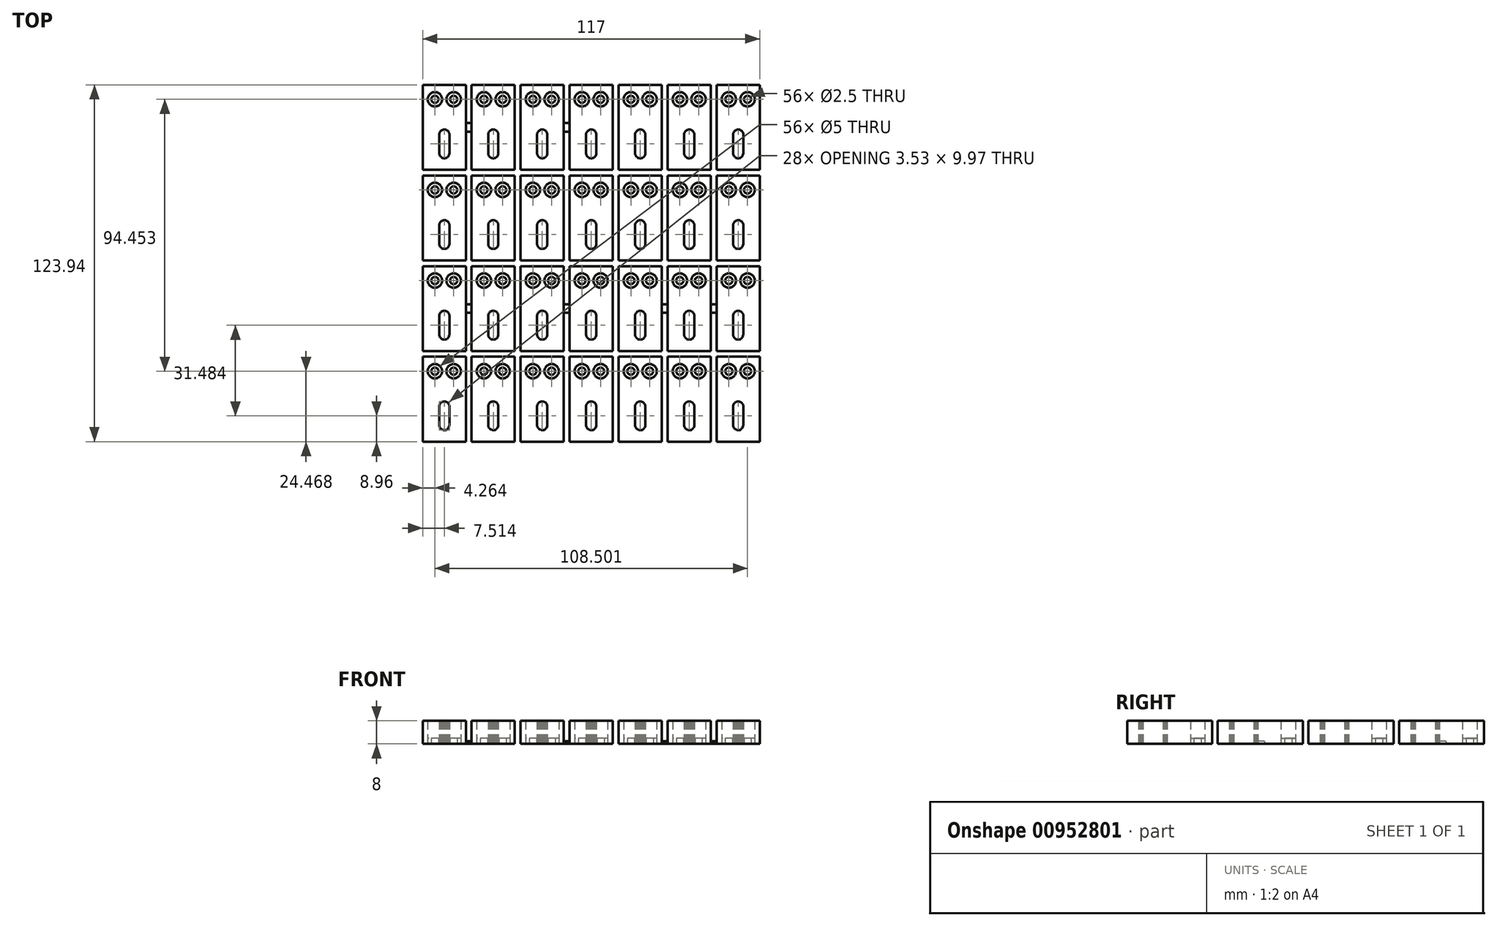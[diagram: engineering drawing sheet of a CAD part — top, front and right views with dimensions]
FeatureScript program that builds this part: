
annotation { "Feature Type Name" : "Feature", "Feature Type Description" : "" }
export const myFeature = defineFeature(function(context is Context, id is Id, definition is map)
    precondition{}
    {
        {
            var Q0;
            Q0=qCreatedBy(makeId("Top.planeOp"),FACE);
            var sketch = newSketch(context, id + "F0", { "sketchPlane" : qUnion([Q0])});
            skLineSegment(sketch, "E0", {"start": v(-58.5, -32.48) * mm, "end": v(-58.5, -61.97) * mm});
            skLineSegment(sketch, "E1", {"start": v(-58.5, -61.97) * mm, "end": v(-43.5, -61.97) * mm});
            skLineSegment(sketch, "E2", {"start": v(-43.5, -61.97) * mm, "end": v(-43.5, -32.48) * mm});
            skLineSegment(sketch, "E3", {"start": v(-43.5, -32.48) * mm, "end": v(-58.5, -32.48) * mm});
            skArc(sketch, "E4", {"start": v(-46.49, -37.5) * mm, "mid": v(-46.85, -36.62) * mm, "end": v(-47.74, -36.25) * mm});
            skArc(sketch, "E5", {"start": v(-47.74, -36.25) * mm, "mid": v(-48.62, -36.62) * mm, "end": v(-48.99, -37.5) * mm});
            skArc(sketch, "E6", {"start": v(-48.99, -37.5) * mm, "mid": v(-48.62, -38.39) * mm, "end": v(-47.74, -38.75) * mm});
            skArc(sketch, "E7", {"start": v(-47.74, -38.75) * mm, "mid": v(-46.85, -38.39) * mm, "end": v(-46.49, -37.5) * mm});
            skArc(sketch, "E8", {"start": v(-52.99, -37.5) * mm, "mid": v(-53.35, -36.62) * mm, "end": v(-54.24, -36.25) * mm});
            skArc(sketch, "E9", {"start": v(-54.24, -36.25) * mm, "mid": v(-55.12, -36.62) * mm, "end": v(-55.49, -37.5) * mm});
            skArc(sketch, "E10", {"start": v(-55.49, -37.5) * mm, "mid": v(-55.12, -38.39) * mm, "end": v(-54.24, -38.75) * mm});
            skArc(sketch, "E11", {"start": v(-54.24, -38.75) * mm, "mid": v(-53.35, -38.39) * mm, "end": v(-52.99, -37.5) * mm});
            skArc(sketch, "E12", {"start": v(-45.24, -37.5) * mm, "mid": v(-45.97, -35.73) * mm, "end": v(-47.74, -35) * mm});
            skArc(sketch, "E13", {"start": v(-47.74, -35) * mm, "mid": v(-49.5, -35.73) * mm, "end": v(-50.24, -37.5) * mm});
            skArc(sketch, "E14", {"start": v(-50.24, -37.5) * mm, "mid": v(-49.5, -39.27) * mm, "end": v(-47.74, -40) * mm});
            skArc(sketch, "E15", {"start": v(-47.74, -40) * mm, "mid": v(-45.97, -39.27) * mm, "end": v(-45.24, -37.5) * mm});
            skArc(sketch, "E16", {"start": v(-51.74, -37.5) * mm, "mid": v(-52.47, -35.73) * mm, "end": v(-54.24, -35) * mm});
            skArc(sketch, "E17", {"start": v(-54.24, -35) * mm, "mid": v(-56, -35.73) * mm, "end": v(-56.74, -37.5) * mm});
            skArc(sketch, "E18", {"start": v(-56.74, -37.5) * mm, "mid": v(-56, -39.27) * mm, "end": v(-54.24, -40) * mm});
            skArc(sketch, "E19", {"start": v(-54.24, -40) * mm, "mid": v(-52.47, -39.27) * mm, "end": v(-51.74, -37.5) * mm});
            skLineSegment(sketch, "E20", {"start": v(-52.75, -56.51) * mm, "end": v(-52.73, -56.57) * mm});
            skLineSegment(sketch, "E21", {"start": v(-52.73, -56.57) * mm, "end": v(-52.65, -56.81) * mm});
            skLineSegment(sketch, "E22", {"start": v(-52.65, -56.81) * mm, "end": v(-52.6, -56.95) * mm});
            skLineSegment(sketch, "E23", {"start": v(-52.6, -56.95) * mm, "end": v(-52.56, -57.05) * mm});
            skLineSegment(sketch, "E24", {"start": v(-52.56, -57.05) * mm, "end": v(-52.5, -57.13) * mm});
            skLineSegment(sketch, "E25", {"start": v(-52.5, -57.13) * mm, "end": v(-52.43, -57.22) * mm});
            skLineSegment(sketch, "E26", {"start": v(-52.43, -57.22) * mm, "end": v(-52.4, -57.26) * mm});
            skLineSegment(sketch, "E27", {"start": v(-52.4, -57.26) * mm, "end": v(-52.4, -57.3) * mm});
            skLineSegment(sketch, "E28", {"start": v(-52.4, -57.3) * mm, "end": v(-52.36, -57.35) * mm});
            skLineSegment(sketch, "E29", {"start": v(-52.36, -57.35) * mm, "end": v(-52.27, -57.44) * mm});
            skLineSegment(sketch, "E30", {"start": v(-52.27, -57.44) * mm, "end": v(-52.08, -57.62) * mm});
            skLineSegment(sketch, "E31", {"start": v(-52.08, -57.62) * mm, "end": v(-52.03, -57.67) * mm});
            skLineSegment(sketch, "E32", {"start": v(-52.03, -57.67) * mm, "end": v(-51.98, -57.69) * mm});
            skLineSegment(sketch, "E33", {"start": v(-51.98, -57.69) * mm, "end": v(-51.96, -57.7) * mm});
            skLineSegment(sketch, "E34", {"start": v(-51.96, -57.7) * mm, "end": v(-51.95, -57.7) * mm});
            skLineSegment(sketch, "E35", {"start": v(-51.95, -57.7) * mm, "end": v(-51.92, -57.73) * mm});
            skLineSegment(sketch, "E36", {"start": v(-51.92, -57.73) * mm, "end": v(-51.86, -57.76) * mm});
            skLineSegment(sketch, "E37", {"start": v(-51.86, -57.76) * mm, "end": v(-51.58, -57.9) * mm});
            skLineSegment(sketch, "E38", {"start": v(-51.58, -57.9) * mm, "end": v(-51.46, -57.94) * mm});
            skLineSegment(sketch, "E39", {"start": v(-51.46, -57.94) * mm, "end": v(-51.32, -57.97) * mm});
            skLineSegment(sketch, "E40", {"start": v(-51.32, -57.97) * mm, "end": v(-51.16, -57.99) * mm});
            skLineSegment(sketch, "E41", {"start": v(-51.16, -57.99) * mm, "end": v(-51, -58) * mm});
            skLineSegment(sketch, "E42", {"start": v(-51, -58) * mm, "end": v(-50.83, -57.99) * mm});
            skLineSegment(sketch, "E43", {"start": v(-50.83, -57.99) * mm, "end": v(-50.67, -57.97) * mm});
            skLineSegment(sketch, "E44", {"start": v(-50.67, -57.97) * mm, "end": v(-50.52, -57.94) * mm});
            skLineSegment(sketch, "E45", {"start": v(-50.52, -57.94) * mm, "end": v(-50.4, -57.9) * mm});
            skLineSegment(sketch, "E46", {"start": v(-50.4, -57.9) * mm, "end": v(-50.1, -57.77) * mm});
            skLineSegment(sketch, "E47", {"start": v(-50.1, -57.77) * mm, "end": v(-50.04, -57.73) * mm});
            skLineSegment(sketch, "E48", {"start": v(-50.04, -57.73) * mm, "end": v(-50.02, -57.7) * mm});
            skLineSegment(sketch, "E49", {"start": v(-50.02, -57.7) * mm, "end": v(-50.01, -57.7) * mm});
            skLineSegment(sketch, "E50", {"start": v(-50.01, -57.7) * mm, "end": v(-50, -57.69) * mm});
            skLineSegment(sketch, "E51", {"start": v(-50, -57.69) * mm, "end": v(-49.96, -57.67) * mm});
            skLineSegment(sketch, "E52", {"start": v(-49.96, -57.67) * mm, "end": v(-49.9, -57.63) * mm});
            skLineSegment(sketch, "E53", {"start": v(-49.9, -57.63) * mm, "end": v(-49.76, -57.5) * mm});
            skLineSegment(sketch, "E54", {"start": v(-49.76, -57.5) * mm, "end": v(-49.63, -57.38) * mm});
            skLineSegment(sketch, "E55", {"start": v(-49.63, -57.38) * mm, "end": v(-49.6, -57.33) * mm});
            skLineSegment(sketch, "E56", {"start": v(-49.6, -57.33) * mm, "end": v(-49.57, -57.3) * mm});
            skLineSegment(sketch, "E57", {"start": v(-49.57, -57.3) * mm, "end": v(-49.56, -57.26) * mm});
            skLineSegment(sketch, "E58", {"start": v(-49.56, -57.26) * mm, "end": v(-49.54, -57.22) * mm});
            skLineSegment(sketch, "E59", {"start": v(-49.54, -57.22) * mm, "end": v(-49.47, -57.14) * mm});
            skLineSegment(sketch, "E60", {"start": v(-49.47, -57.14) * mm, "end": v(-49.43, -57.08) * mm});
            skLineSegment(sketch, "E61", {"start": v(-49.43, -57.08) * mm, "end": v(-49.39, -56.99) * mm});
            skLineSegment(sketch, "E62", {"start": v(-49.39, -56.99) * mm, "end": v(-49.25, -56.59) * mm});
            skLineSegment(sketch, "E63", {"start": v(-49.25, -56.59) * mm, "end": v(-49.22, -56.48) * mm});
            skLineSegment(sketch, "E64", {"start": v(-49.22, -56.48) * mm, "end": v(-49.22, -49.5) * mm});
            skLineSegment(sketch, "E65", {"start": v(-49.22, -49.5) * mm, "end": v(-49.24, -49.42) * mm});
            skLineSegment(sketch, "E66", {"start": v(-49.24, -49.42) * mm, "end": v(-49.33, -49.18) * mm});
            skLineSegment(sketch, "E67", {"start": v(-49.33, -49.18) * mm, "end": v(-49.4, -49.01) * mm});
            skLineSegment(sketch, "E68", {"start": v(-49.4, -49.01) * mm, "end": v(-49.48, -48.86) * mm});
            skLineSegment(sketch, "E69", {"start": v(-49.48, -48.86) * mm, "end": v(-49.55, -48.76) * mm});
            skLineSegment(sketch, "E70", {"start": v(-49.55, -48.76) * mm, "end": v(-49.57, -48.7) * mm});
            skLineSegment(sketch, "E71", {"start": v(-49.57, -48.7) * mm, "end": v(-49.6, -48.66) * mm});
            skLineSegment(sketch, "E72", {"start": v(-49.6, -48.66) * mm, "end": v(-49.68, -48.58) * mm});
            skLineSegment(sketch, "E73", {"start": v(-49.68, -48.58) * mm, "end": v(-49.93, -48.35) * mm});
            skLineSegment(sketch, "E74", {"start": v(-49.93, -48.35) * mm, "end": v(-50.05, -48.27) * mm});
            skLineSegment(sketch, "E75", {"start": v(-50.05, -48.27) * mm, "end": v(-50.2, -48.2) * mm});
            skLineSegment(sketch, "E76", {"start": v(-50.2, -48.2) * mm, "end": v(-50.37, -48.12) * mm});
            skLineSegment(sketch, "E77", {"start": v(-50.37, -48.12) * mm, "end": v(-50.53, -48.06) * mm});
            skLineSegment(sketch, "E78", {"start": v(-50.53, -48.06) * mm, "end": v(-50.6, -48.05) * mm});
            skLineSegment(sketch, "E79", {"start": v(-50.6, -48.05) * mm, "end": v(-50.72, -48.04) * mm});
            skLineSegment(sketch, "E80", {"start": v(-50.72, -48.04) * mm, "end": v(-50.99, -48.03) * mm});
            skLineSegment(sketch, "E81", {"start": v(-50.99, -48.03) * mm, "end": v(-51.25, -48.04) * mm});
            skLineSegment(sketch, "E82", {"start": v(-51.25, -48.04) * mm, "end": v(-51.36, -48.05) * mm});
            skLineSegment(sketch, "E83", {"start": v(-51.36, -48.05) * mm, "end": v(-51.45, -48.06) * mm});
            skLineSegment(sketch, "E84", {"start": v(-51.45, -48.06) * mm, "end": v(-51.64, -48.13) * mm});
            skLineSegment(sketch, "E85", {"start": v(-51.64, -48.13) * mm, "end": v(-51.84, -48.23) * mm});
            skLineSegment(sketch, "E86", {"start": v(-51.84, -48.23) * mm, "end": v(-52.03, -48.35) * mm});
            skLineSegment(sketch, "E87", {"start": v(-52.03, -48.35) * mm, "end": v(-52.2, -48.49) * mm});
            skLineSegment(sketch, "E88", {"start": v(-52.2, -48.49) * mm, "end": v(-52.4, -48.67) * mm});
            skLineSegment(sketch, "E89", {"start": v(-52.4, -48.67) * mm, "end": v(-52.4, -48.7) * mm});
            skLineSegment(sketch, "E90", {"start": v(-52.4, -48.7) * mm, "end": v(-52.43, -48.76) * mm});
            skLineSegment(sketch, "E91", {"start": v(-52.43, -48.76) * mm, "end": v(-52.5, -48.86) * mm});
            skLineSegment(sketch, "E92", {"start": v(-52.5, -48.86) * mm, "end": v(-52.58, -49.01) * mm});
            skLineSegment(sketch, "E93", {"start": v(-52.58, -49.01) * mm, "end": v(-52.65, -49.18) * mm});
            skLineSegment(sketch, "E94", {"start": v(-52.65, -49.18) * mm, "end": v(-52.73, -49.42) * mm});
            skLineSegment(sketch, "E95", {"start": v(-52.73, -49.42) * mm, "end": v(-52.75, -49.5) * mm});
            skLineSegment(sketch, "E96", {"start": v(-52.75, -49.5) * mm, "end": v(-52.75, -56.51) * mm});
            skLineSegment(sketch, "E97", {"start": v(-43.5, -45.73) * mm, "end": v(-43.5, -48.73) * mm});
            skLineSegment(sketch, "E98", {"start": v(-43.5, -48.73) * mm, "end": v(-41.5, -48.73) * mm});
            skLineSegment(sketch, "E99", {"start": v(-41.5, -48.73) * mm, "end": v(-41.5, -45.73) * mm});
            skLineSegment(sketch, "E100", {"start": v(-41.5, -45.73) * mm, "end": v(-43.5, -45.73) * mm});
            skLineSegment(sketch, "E101", {"start": v(-41.5, -32.48) * mm, "end": v(-41.5, -61.97) * mm});
            skLineSegment(sketch, "E102", {"start": v(-41.5, -61.97) * mm, "end": v(-26.5, -61.97) * mm});
            skLineSegment(sketch, "E103", {"start": v(-26.5, -61.97) * mm, "end": v(-26.5, -32.48) * mm});
            skLineSegment(sketch, "E104", {"start": v(-26.5, -32.48) * mm, "end": v(-41.5, -32.48) * mm});
            skArc(sketch, "E105", {"start": v(-29.49, -37.5) * mm, "mid": v(-29.85, -36.62) * mm, "end": v(-30.74, -36.25) * mm});
            skArc(sketch, "E106", {"start": v(-30.74, -36.25) * mm, "mid": v(-31.62, -36.62) * mm, "end": v(-31.99, -37.5) * mm});
            skArc(sketch, "E107", {"start": v(-31.99, -37.5) * mm, "mid": v(-31.62, -38.39) * mm, "end": v(-30.74, -38.75) * mm});
            skArc(sketch, "E108", {"start": v(-30.74, -38.75) * mm, "mid": v(-29.85, -38.39) * mm, "end": v(-29.49, -37.5) * mm});
            skArc(sketch, "E109", {"start": v(-35.99, -37.5) * mm, "mid": v(-36.35, -36.62) * mm, "end": v(-37.24, -36.25) * mm});
            skArc(sketch, "E110", {"start": v(-37.24, -36.25) * mm, "mid": v(-38.12, -36.62) * mm, "end": v(-38.49, -37.5) * mm});
            skArc(sketch, "E111", {"start": v(-38.49, -37.5) * mm, "mid": v(-38.12, -38.39) * mm, "end": v(-37.24, -38.75) * mm});
            skArc(sketch, "E112", {"start": v(-37.24, -38.75) * mm, "mid": v(-36.35, -38.39) * mm, "end": v(-35.99, -37.5) * mm});
            skArc(sketch, "E113", {"start": v(-28.24, -37.5) * mm, "mid": v(-28.97, -35.73) * mm, "end": v(-30.74, -35) * mm});
            skArc(sketch, "E114", {"start": v(-30.74, -35) * mm, "mid": v(-32.5, -35.73) * mm, "end": v(-33.24, -37.5) * mm});
            skArc(sketch, "E115", {"start": v(-33.24, -37.5) * mm, "mid": v(-32.5, -39.27) * mm, "end": v(-30.74, -40) * mm});
            skArc(sketch, "E116", {"start": v(-30.74, -40) * mm, "mid": v(-28.97, -39.27) * mm, "end": v(-28.24, -37.5) * mm});
            skArc(sketch, "E117", {"start": v(-34.74, -37.5) * mm, "mid": v(-35.47, -35.73) * mm, "end": v(-37.24, -35) * mm});
            skArc(sketch, "E118", {"start": v(-37.24, -35) * mm, "mid": v(-39, -35.73) * mm, "end": v(-39.74, -37.5) * mm});
            skArc(sketch, "E119", {"start": v(-39.74, -37.5) * mm, "mid": v(-39, -39.27) * mm, "end": v(-37.24, -40) * mm});
            skArc(sketch, "E120", {"start": v(-37.24, -40) * mm, "mid": v(-35.47, -39.27) * mm, "end": v(-34.74, -37.5) * mm});
            skLineSegment(sketch, "E121", {"start": v(-35.75, -56.51) * mm, "end": v(-35.73, -56.57) * mm});
            skLineSegment(sketch, "E122", {"start": v(-35.73, -56.57) * mm, "end": v(-35.65, -56.81) * mm});
            skLineSegment(sketch, "E123", {"start": v(-35.65, -56.81) * mm, "end": v(-35.6, -56.95) * mm});
            skLineSegment(sketch, "E124", {"start": v(-35.6, -56.95) * mm, "end": v(-35.56, -57.05) * mm});
            skLineSegment(sketch, "E125", {"start": v(-35.56, -57.05) * mm, "end": v(-35.5, -57.13) * mm});
            skLineSegment(sketch, "E126", {"start": v(-35.5, -57.13) * mm, "end": v(-35.43, -57.22) * mm});
            skLineSegment(sketch, "E127", {"start": v(-35.43, -57.22) * mm, "end": v(-35.4, -57.26) * mm});
            skLineSegment(sketch, "E128", {"start": v(-35.4, -57.26) * mm, "end": v(-35.4, -57.3) * mm});
            skLineSegment(sketch, "E129", {"start": v(-35.4, -57.3) * mm, "end": v(-35.36, -57.35) * mm});
            skLineSegment(sketch, "E130", {"start": v(-35.36, -57.35) * mm, "end": v(-35.27, -57.44) * mm});
            skLineSegment(sketch, "E131", {"start": v(-35.27, -57.44) * mm, "end": v(-35.08, -57.62) * mm});
            skLineSegment(sketch, "E132", {"start": v(-35.08, -57.62) * mm, "end": v(-35.03, -57.67) * mm});
            skLineSegment(sketch, "E133", {"start": v(-35.03, -57.67) * mm, "end": v(-34.98, -57.69) * mm});
            skLineSegment(sketch, "E134", {"start": v(-34.98, -57.69) * mm, "end": v(-34.96, -57.7) * mm});
            skLineSegment(sketch, "E135", {"start": v(-34.96, -57.7) * mm, "end": v(-34.95, -57.7) * mm});
            skLineSegment(sketch, "E136", {"start": v(-34.95, -57.7) * mm, "end": v(-34.92, -57.73) * mm});
            skLineSegment(sketch, "E137", {"start": v(-34.92, -57.73) * mm, "end": v(-34.86, -57.76) * mm});
            skLineSegment(sketch, "E138", {"start": v(-34.86, -57.76) * mm, "end": v(-34.58, -57.9) * mm});
            skLineSegment(sketch, "E139", {"start": v(-34.58, -57.9) * mm, "end": v(-34.46, -57.94) * mm});
            skLineSegment(sketch, "E140", {"start": v(-34.46, -57.94) * mm, "end": v(-34.32, -57.97) * mm});
            skLineSegment(sketch, "E141", {"start": v(-34.32, -57.97) * mm, "end": v(-34.16, -57.99) * mm});
            skLineSegment(sketch, "E142", {"start": v(-34.16, -57.99) * mm, "end": v(-34, -58) * mm});
            skLineSegment(sketch, "E143", {"start": v(-34, -58) * mm, "end": v(-33.83, -57.99) * mm});
            skLineSegment(sketch, "E144", {"start": v(-33.83, -57.99) * mm, "end": v(-33.67, -57.97) * mm});
            skLineSegment(sketch, "E145", {"start": v(-33.67, -57.97) * mm, "end": v(-33.52, -57.94) * mm});
            skLineSegment(sketch, "E146", {"start": v(-33.52, -57.94) * mm, "end": v(-33.4, -57.9) * mm});
            skLineSegment(sketch, "E147", {"start": v(-33.4, -57.9) * mm, "end": v(-33.1, -57.77) * mm});
            skLineSegment(sketch, "E148", {"start": v(-33.1, -57.77) * mm, "end": v(-33.04, -57.73) * mm});
            skLineSegment(sketch, "E149", {"start": v(-33.04, -57.73) * mm, "end": v(-33.02, -57.7) * mm});
            skLineSegment(sketch, "E150", {"start": v(-33.02, -57.7) * mm, "end": v(-33.01, -57.7) * mm});
            skLineSegment(sketch, "E151", {"start": v(-33.01, -57.7) * mm, "end": v(-33, -57.69) * mm});
            skLineSegment(sketch, "E152", {"start": v(-33, -57.69) * mm, "end": v(-32.96, -57.67) * mm});
            skLineSegment(sketch, "E153", {"start": v(-32.96, -57.67) * mm, "end": v(-32.9, -57.63) * mm});
            skLineSegment(sketch, "E154", {"start": v(-32.9, -57.63) * mm, "end": v(-32.76, -57.5) * mm});
            skLineSegment(sketch, "E155", {"start": v(-32.76, -57.5) * mm, "end": v(-32.63, -57.38) * mm});
            skLineSegment(sketch, "E156", {"start": v(-32.63, -57.38) * mm, "end": v(-32.6, -57.33) * mm});
            skLineSegment(sketch, "E157", {"start": v(-32.6, -57.33) * mm, "end": v(-32.57, -57.3) * mm});
            skLineSegment(sketch, "E158", {"start": v(-32.57, -57.3) * mm, "end": v(-32.56, -57.26) * mm});
            skLineSegment(sketch, "E159", {"start": v(-32.56, -57.26) * mm, "end": v(-32.54, -57.22) * mm});
            skLineSegment(sketch, "E160", {"start": v(-32.54, -57.22) * mm, "end": v(-32.47, -57.14) * mm});
            skLineSegment(sketch, "E161", {"start": v(-32.47, -57.14) * mm, "end": v(-32.43, -57.08) * mm});
            skLineSegment(sketch, "E162", {"start": v(-32.43, -57.08) * mm, "end": v(-32.39, -56.99) * mm});
            skLineSegment(sketch, "E163", {"start": v(-32.39, -56.99) * mm, "end": v(-32.25, -56.59) * mm});
            skLineSegment(sketch, "E164", {"start": v(-32.25, -56.59) * mm, "end": v(-32.22, -56.48) * mm});
            skLineSegment(sketch, "E165", {"start": v(-32.22, -56.48) * mm, "end": v(-32.22, -49.5) * mm});
            skLineSegment(sketch, "E166", {"start": v(-32.22, -49.5) * mm, "end": v(-32.24, -49.42) * mm});
            skLineSegment(sketch, "E167", {"start": v(-32.24, -49.42) * mm, "end": v(-32.33, -49.18) * mm});
            skLineSegment(sketch, "E168", {"start": v(-32.33, -49.18) * mm, "end": v(-32.4, -49.01) * mm});
            skLineSegment(sketch, "E169", {"start": v(-32.4, -49.01) * mm, "end": v(-32.48, -48.86) * mm});
            skLineSegment(sketch, "E170", {"start": v(-32.48, -48.86) * mm, "end": v(-32.55, -48.76) * mm});
            skLineSegment(sketch, "E171", {"start": v(-32.55, -48.76) * mm, "end": v(-32.57, -48.7) * mm});
            skLineSegment(sketch, "E172", {"start": v(-32.57, -48.7) * mm, "end": v(-32.6, -48.66) * mm});
            skLineSegment(sketch, "E173", {"start": v(-32.6, -48.66) * mm, "end": v(-32.68, -48.58) * mm});
            skLineSegment(sketch, "E174", {"start": v(-32.68, -48.58) * mm, "end": v(-32.93, -48.35) * mm});
            skLineSegment(sketch, "E175", {"start": v(-32.93, -48.35) * mm, "end": v(-33.05, -48.27) * mm});
            skLineSegment(sketch, "E176", {"start": v(-33.05, -48.27) * mm, "end": v(-33.2, -48.2) * mm});
            skLineSegment(sketch, "E177", {"start": v(-33.2, -48.2) * mm, "end": v(-33.37, -48.12) * mm});
            skLineSegment(sketch, "E178", {"start": v(-33.37, -48.12) * mm, "end": v(-33.53, -48.06) * mm});
            skLineSegment(sketch, "E179", {"start": v(-33.53, -48.06) * mm, "end": v(-33.6, -48.05) * mm});
            skLineSegment(sketch, "E180", {"start": v(-33.6, -48.05) * mm, "end": v(-33.72, -48.04) * mm});
            skLineSegment(sketch, "E181", {"start": v(-33.72, -48.04) * mm, "end": v(-33.99, -48.03) * mm});
            skLineSegment(sketch, "E182", {"start": v(-33.99, -48.03) * mm, "end": v(-34.25, -48.04) * mm});
            skLineSegment(sketch, "E183", {"start": v(-34.25, -48.04) * mm, "end": v(-34.36, -48.05) * mm});
            skLineSegment(sketch, "E184", {"start": v(-34.36, -48.05) * mm, "end": v(-34.45, -48.06) * mm});
            skLineSegment(sketch, "E185", {"start": v(-34.45, -48.06) * mm, "end": v(-34.64, -48.13) * mm});
            skLineSegment(sketch, "E186", {"start": v(-34.64, -48.13) * mm, "end": v(-34.84, -48.23) * mm});
            skLineSegment(sketch, "E187", {"start": v(-34.84, -48.23) * mm, "end": v(-35.03, -48.35) * mm});
            skLineSegment(sketch, "E188", {"start": v(-35.03, -48.35) * mm, "end": v(-35.2, -48.49) * mm});
            skLineSegment(sketch, "E189", {"start": v(-35.2, -48.49) * mm, "end": v(-35.4, -48.67) * mm});
            skLineSegment(sketch, "E190", {"start": v(-35.4, -48.67) * mm, "end": v(-35.4, -48.7) * mm});
            skLineSegment(sketch, "E191", {"start": v(-35.4, -48.7) * mm, "end": v(-35.43, -48.76) * mm});
            skLineSegment(sketch, "E192", {"start": v(-35.43, -48.76) * mm, "end": v(-35.5, -48.86) * mm});
            skLineSegment(sketch, "E193", {"start": v(-35.5, -48.86) * mm, "end": v(-35.58, -49.01) * mm});
            skLineSegment(sketch, "E194", {"start": v(-35.58, -49.01) * mm, "end": v(-35.65, -49.18) * mm});
            skLineSegment(sketch, "E195", {"start": v(-35.65, -49.18) * mm, "end": v(-35.73, -49.42) * mm});
            skLineSegment(sketch, "E196", {"start": v(-35.73, -49.42) * mm, "end": v(-35.75, -49.5) * mm});
            skLineSegment(sketch, "E197", {"start": v(-35.75, -49.5) * mm, "end": v(-35.75, -56.51) * mm});
            skLineSegment(sketch, "E198", {"start": v(-26.5, -45.73) * mm, "end": v(-26.5, -48.73) * mm});
            skLineSegment(sketch, "E199", {"start": v(-26.5, -48.73) * mm, "end": v(-24.5, -48.73) * mm});
            skLineSegment(sketch, "E200", {"start": v(-24.5, -48.73) * mm, "end": v(-24.5, -45.73) * mm});
            skLineSegment(sketch, "E201", {"start": v(-24.5, -45.73) * mm, "end": v(-26.5, -45.73) * mm});
            skLineSegment(sketch, "E202", {"start": v(-35.5, -32.48) * mm, "end": v(-32.5, -32.48) * mm});
            skLineSegment(sketch, "E203", {"start": v(-32.5, -32.48) * mm, "end": v(-32.5, -30.48) * mm});
            skLineSegment(sketch, "E204", {"start": v(-32.5, -30.48) * mm, "end": v(-35.5, -30.48) * mm});
            skLineSegment(sketch, "E205", {"start": v(-35.5, -30.48) * mm, "end": v(-35.5, -32.48) * mm});
            skLineSegment(sketch, "E206", {"start": v(-24.5, -32.48) * mm, "end": v(-24.5, -61.97) * mm});
            skLineSegment(sketch, "E207", {"start": v(-24.5, -61.97) * mm, "end": v(-9.5, -61.97) * mm});
            skLineSegment(sketch, "E208", {"start": v(-9.5, -61.97) * mm, "end": v(-9.5, -32.48) * mm});
            skLineSegment(sketch, "E209", {"start": v(-9.5, -32.48) * mm, "end": v(-24.5, -32.48) * mm});
            skArc(sketch, "E210", {"start": v(-12.49, -37.5) * mm, "mid": v(-12.85, -36.62) * mm, "end": v(-13.74, -36.25) * mm});
            skArc(sketch, "E211", {"start": v(-13.74, -36.25) * mm, "mid": v(-14.62, -36.62) * mm, "end": v(-14.99, -37.5) * mm});
            skArc(sketch, "E212", {"start": v(-14.99, -37.5) * mm, "mid": v(-14.62, -38.39) * mm, "end": v(-13.74, -38.75) * mm});
            skArc(sketch, "E213", {"start": v(-13.74, -38.75) * mm, "mid": v(-12.85, -38.39) * mm, "end": v(-12.49, -37.5) * mm});
            skArc(sketch, "E214", {"start": v(-18.99, -37.5) * mm, "mid": v(-19.35, -36.62) * mm, "end": v(-20.24, -36.25) * mm});
            skArc(sketch, "E215", {"start": v(-20.24, -36.25) * mm, "mid": v(-21.12, -36.62) * mm, "end": v(-21.49, -37.5) * mm});
            skArc(sketch, "E216", {"start": v(-21.49, -37.5) * mm, "mid": v(-21.12, -38.39) * mm, "end": v(-20.24, -38.75) * mm});
            skArc(sketch, "E217", {"start": v(-20.24, -38.75) * mm, "mid": v(-19.35, -38.39) * mm, "end": v(-18.99, -37.5) * mm});
            skArc(sketch, "E218", {"start": v(-11.24, -37.5) * mm, "mid": v(-11.97, -35.73) * mm, "end": v(-13.74, -35) * mm});
            skArc(sketch, "E219", {"start": v(-13.74, -35) * mm, "mid": v(-15.5, -35.73) * mm, "end": v(-16.24, -37.5) * mm});
            skArc(sketch, "E220", {"start": v(-16.24, -37.5) * mm, "mid": v(-15.5, -39.27) * mm, "end": v(-13.74, -40) * mm});
            skArc(sketch, "E221", {"start": v(-13.74, -40) * mm, "mid": v(-11.97, -39.27) * mm, "end": v(-11.24, -37.5) * mm});
            skArc(sketch, "E222", {"start": v(-17.74, -37.5) * mm, "mid": v(-18.47, -35.73) * mm, "end": v(-20.24, -35) * mm});
            skArc(sketch, "E223", {"start": v(-20.24, -35) * mm, "mid": v(-22, -35.73) * mm, "end": v(-22.74, -37.5) * mm});
            skArc(sketch, "E224", {"start": v(-22.74, -37.5) * mm, "mid": v(-22, -39.27) * mm, "end": v(-20.24, -40) * mm});
            skArc(sketch, "E225", {"start": v(-20.24, -40) * mm, "mid": v(-18.47, -39.27) * mm, "end": v(-17.74, -37.5) * mm});
            skLineSegment(sketch, "E226", {"start": v(-18.75, -56.51) * mm, "end": v(-18.73, -56.57) * mm});
            skLineSegment(sketch, "E227", {"start": v(-18.73, -56.57) * mm, "end": v(-18.65, -56.81) * mm});
            skLineSegment(sketch, "E228", {"start": v(-18.65, -56.81) * mm, "end": v(-18.6, -56.95) * mm});
            skLineSegment(sketch, "E229", {"start": v(-18.6, -56.95) * mm, "end": v(-18.56, -57.05) * mm});
            skLineSegment(sketch, "E230", {"start": v(-18.56, -57.05) * mm, "end": v(-18.5, -57.13) * mm});
            skLineSegment(sketch, "E231", {"start": v(-18.5, -57.13) * mm, "end": v(-18.43, -57.22) * mm});
            skLineSegment(sketch, "E232", {"start": v(-18.43, -57.22) * mm, "end": v(-18.4, -57.26) * mm});
            skLineSegment(sketch, "E233", {"start": v(-18.4, -57.26) * mm, "end": v(-18.4, -57.3) * mm});
            skLineSegment(sketch, "E234", {"start": v(-18.4, -57.3) * mm, "end": v(-18.36, -57.35) * mm});
            skLineSegment(sketch, "E235", {"start": v(-18.36, -57.35) * mm, "end": v(-18.27, -57.44) * mm});
            skLineSegment(sketch, "E236", {"start": v(-18.27, -57.44) * mm, "end": v(-18.08, -57.62) * mm});
            skLineSegment(sketch, "E237", {"start": v(-18.08, -57.62) * mm, "end": v(-18.03, -57.67) * mm});
            skLineSegment(sketch, "E238", {"start": v(-18.03, -57.67) * mm, "end": v(-17.98, -57.69) * mm});
            skLineSegment(sketch, "E239", {"start": v(-17.98, -57.69) * mm, "end": v(-17.96, -57.7) * mm});
            skLineSegment(sketch, "E240", {"start": v(-17.96, -57.7) * mm, "end": v(-17.95, -57.7) * mm});
            skLineSegment(sketch, "E241", {"start": v(-17.95, -57.7) * mm, "end": v(-17.92, -57.73) * mm});
            skLineSegment(sketch, "E242", {"start": v(-17.92, -57.73) * mm, "end": v(-17.86, -57.76) * mm});
            skLineSegment(sketch, "E243", {"start": v(-17.86, -57.76) * mm, "end": v(-17.58, -57.9) * mm});
            skLineSegment(sketch, "E244", {"start": v(-17.58, -57.9) * mm, "end": v(-17.46, -57.94) * mm});
            skLineSegment(sketch, "E245", {"start": v(-17.46, -57.94) * mm, "end": v(-17.32, -57.97) * mm});
            skLineSegment(sketch, "E246", {"start": v(-17.32, -57.97) * mm, "end": v(-17.16, -57.99) * mm});
            skLineSegment(sketch, "E247", {"start": v(-17.16, -57.99) * mm, "end": v(-17, -58) * mm});
            skLineSegment(sketch, "E248", {"start": v(-17, -58) * mm, "end": v(-16.83, -57.99) * mm});
            skLineSegment(sketch, "E249", {"start": v(-16.83, -57.99) * mm, "end": v(-16.67, -57.97) * mm});
            skLineSegment(sketch, "E250", {"start": v(-16.67, -57.97) * mm, "end": v(-16.52, -57.94) * mm});
            skLineSegment(sketch, "E251", {"start": v(-16.52, -57.94) * mm, "end": v(-16.4, -57.9) * mm});
            skLineSegment(sketch, "E252", {"start": v(-16.4, -57.9) * mm, "end": v(-16.1, -57.77) * mm});
            skLineSegment(sketch, "E253", {"start": v(-16.1, -57.77) * mm, "end": v(-16.04, -57.73) * mm});
            skLineSegment(sketch, "E254", {"start": v(-16.04, -57.73) * mm, "end": v(-16.02, -57.7) * mm});
            skLineSegment(sketch, "E255", {"start": v(-16.02, -57.7) * mm, "end": v(-16.01, -57.7) * mm});
            skLineSegment(sketch, "E256", {"start": v(-16.01, -57.7) * mm, "end": v(-16, -57.69) * mm});
            skLineSegment(sketch, "E257", {"start": v(-16, -57.69) * mm, "end": v(-15.96, -57.67) * mm});
            skLineSegment(sketch, "E258", {"start": v(-15.96, -57.67) * mm, "end": v(-15.9, -57.63) * mm});
            skLineSegment(sketch, "E259", {"start": v(-15.9, -57.63) * mm, "end": v(-15.76, -57.5) * mm});
            skLineSegment(sketch, "E260", {"start": v(-15.76, -57.5) * mm, "end": v(-15.63, -57.38) * mm});
            skLineSegment(sketch, "E261", {"start": v(-15.63, -57.38) * mm, "end": v(-15.6, -57.33) * mm});
            skLineSegment(sketch, "E262", {"start": v(-15.6, -57.33) * mm, "end": v(-15.57, -57.3) * mm});
            skLineSegment(sketch, "E263", {"start": v(-15.57, -57.3) * mm, "end": v(-15.56, -57.26) * mm});
            skLineSegment(sketch, "E264", {"start": v(-15.56, -57.26) * mm, "end": v(-15.54, -57.22) * mm});
            skLineSegment(sketch, "E265", {"start": v(-15.54, -57.22) * mm, "end": v(-15.47, -57.14) * mm});
            skLineSegment(sketch, "E266", {"start": v(-15.47, -57.14) * mm, "end": v(-15.43, -57.08) * mm});
            skLineSegment(sketch, "E267", {"start": v(-15.43, -57.08) * mm, "end": v(-15.39, -56.99) * mm});
            skLineSegment(sketch, "E268", {"start": v(-15.39, -56.99) * mm, "end": v(-15.25, -56.59) * mm});
            skLineSegment(sketch, "E269", {"start": v(-15.25, -56.59) * mm, "end": v(-15.22, -56.48) * mm});
            skLineSegment(sketch, "E270", {"start": v(-15.22, -56.48) * mm, "end": v(-15.22, -49.5) * mm});
            skLineSegment(sketch, "E271", {"start": v(-15.22, -49.5) * mm, "end": v(-15.24, -49.42) * mm});
            skLineSegment(sketch, "E272", {"start": v(-15.24, -49.42) * mm, "end": v(-15.33, -49.18) * mm});
            skLineSegment(sketch, "E273", {"start": v(-15.33, -49.18) * mm, "end": v(-15.4, -49.01) * mm});
            skLineSegment(sketch, "E274", {"start": v(-15.4, -49.01) * mm, "end": v(-15.48, -48.86) * mm});
            skLineSegment(sketch, "E275", {"start": v(-15.48, -48.86) * mm, "end": v(-15.55, -48.76) * mm});
            skLineSegment(sketch, "E276", {"start": v(-15.55, -48.76) * mm, "end": v(-15.57, -48.7) * mm});
            skLineSegment(sketch, "E277", {"start": v(-15.57, -48.7) * mm, "end": v(-15.6, -48.66) * mm});
            skLineSegment(sketch, "E278", {"start": v(-15.6, -48.66) * mm, "end": v(-15.68, -48.58) * mm});
            skLineSegment(sketch, "E279", {"start": v(-15.68, -48.58) * mm, "end": v(-15.93, -48.35) * mm});
            skLineSegment(sketch, "E280", {"start": v(-15.93, -48.35) * mm, "end": v(-16.05, -48.27) * mm});
            skLineSegment(sketch, "E281", {"start": v(-16.05, -48.27) * mm, "end": v(-16.2, -48.2) * mm});
            skLineSegment(sketch, "E282", {"start": v(-16.2, -48.2) * mm, "end": v(-16.37, -48.12) * mm});
            skLineSegment(sketch, "E283", {"start": v(-16.37, -48.12) * mm, "end": v(-16.53, -48.06) * mm});
            skLineSegment(sketch, "E284", {"start": v(-16.53, -48.06) * mm, "end": v(-16.6, -48.05) * mm});
            skLineSegment(sketch, "E285", {"start": v(-16.6, -48.05) * mm, "end": v(-16.72, -48.04) * mm});
            skLineSegment(sketch, "E286", {"start": v(-16.72, -48.04) * mm, "end": v(-16.99, -48.03) * mm});
            skLineSegment(sketch, "E287", {"start": v(-16.99, -48.03) * mm, "end": v(-17.25, -48.04) * mm});
            skLineSegment(sketch, "E288", {"start": v(-17.25, -48.04) * mm, "end": v(-17.36, -48.05) * mm});
            skLineSegment(sketch, "E289", {"start": v(-17.36, -48.05) * mm, "end": v(-17.45, -48.06) * mm});
            skLineSegment(sketch, "E290", {"start": v(-17.45, -48.06) * mm, "end": v(-17.64, -48.13) * mm});
            skLineSegment(sketch, "E291", {"start": v(-17.64, -48.13) * mm, "end": v(-17.84, -48.23) * mm});
            skLineSegment(sketch, "E292", {"start": v(-17.84, -48.23) * mm, "end": v(-18.03, -48.35) * mm});
            skLineSegment(sketch, "E293", {"start": v(-18.03, -48.35) * mm, "end": v(-18.2, -48.49) * mm});
            skLineSegment(sketch, "E294", {"start": v(-18.2, -48.49) * mm, "end": v(-18.4, -48.67) * mm});
            skLineSegment(sketch, "E295", {"start": v(-18.4, -48.67) * mm, "end": v(-18.4, -48.7) * mm});
            skLineSegment(sketch, "E296", {"start": v(-18.4, -48.7) * mm, "end": v(-18.43, -48.76) * mm});
            skLineSegment(sketch, "E297", {"start": v(-18.43, -48.76) * mm, "end": v(-18.5, -48.86) * mm});
            skLineSegment(sketch, "E298", {"start": v(-18.5, -48.86) * mm, "end": v(-18.58, -49.01) * mm});
            skLineSegment(sketch, "E299", {"start": v(-18.58, -49.01) * mm, "end": v(-18.65, -49.18) * mm});
            skLineSegment(sketch, "E300", {"start": v(-18.65, -49.18) * mm, "end": v(-18.73, -49.42) * mm});
            skLineSegment(sketch, "E301", {"start": v(-18.73, -49.42) * mm, "end": v(-18.75, -49.5) * mm});
            skLineSegment(sketch, "E302", {"start": v(-18.75, -49.5) * mm, "end": v(-18.75, -56.51) * mm});
            skLineSegment(sketch, "E303", {"start": v(-18.5, -32.48) * mm, "end": v(-15.5, -32.48) * mm});
            skLineSegment(sketch, "E304", {"start": v(-15.5, -32.48) * mm, "end": v(-15.5, -30.48) * mm});
            skLineSegment(sketch, "E305", {"start": v(-15.5, -30.48) * mm, "end": v(-18.5, -30.48) * mm});
            skLineSegment(sketch, "E306", {"start": v(-18.5, -30.48) * mm, "end": v(-18.5, -32.48) * mm});
            skLineSegment(sketch, "E307", {"start": v(-7.5, -32.48) * mm, "end": v(-7.5, -61.97) * mm});
            skLineSegment(sketch, "E308", {"start": v(-7.5, -61.97) * mm, "end": v(7.5, -61.97) * mm});
            skLineSegment(sketch, "E309", {"start": v(7.5, -61.97) * mm, "end": v(7.5, -32.48) * mm});
            skLineSegment(sketch, "E310", {"start": v(7.5, -32.48) * mm, "end": v(-7.5, -32.48) * mm});
            skArc(sketch, "E311", {"start": v(4.51, -37.5) * mm, "mid": v(4.15, -36.62) * mm, "end": v(3.26, -36.25) * mm});
            skArc(sketch, "E312", {"start": v(3.26, -36.25) * mm, "mid": v(2.38, -36.62) * mm, "end": v(2.01, -37.5) * mm});
            skArc(sketch, "E313", {"start": v(2.01, -37.5) * mm, "mid": v(2.38, -38.39) * mm, "end": v(3.26, -38.75) * mm});
            skArc(sketch, "E314", {"start": v(3.26, -38.75) * mm, "mid": v(4.15, -38.39) * mm, "end": v(4.51, -37.5) * mm});
            skArc(sketch, "E315", {"start": v(-1.99, -37.5) * mm, "mid": v(-2.35, -36.62) * mm, "end": v(-3.24, -36.25) * mm});
            skArc(sketch, "E316", {"start": v(-3.24, -36.25) * mm, "mid": v(-4.12, -36.62) * mm, "end": v(-4.49, -37.5) * mm});
            skArc(sketch, "E317", {"start": v(-4.49, -37.5) * mm, "mid": v(-4.12, -38.39) * mm, "end": v(-3.24, -38.75) * mm});
            skArc(sketch, "E318", {"start": v(-3.24, -38.75) * mm, "mid": v(-2.35, -38.39) * mm, "end": v(-1.99, -37.5) * mm});
            skArc(sketch, "E319", {"start": v(5.76, -37.5) * mm, "mid": v(5.03, -35.73) * mm, "end": v(3.26, -35) * mm});
            skArc(sketch, "E320", {"start": v(3.26, -35) * mm, "mid": v(1.5, -35.73) * mm, "end": v(0.76, -37.5) * mm});
            skArc(sketch, "E321", {"start": v(0.76, -37.5) * mm, "mid": v(1.5, -39.27) * mm, "end": v(3.26, -40) * mm});
            skArc(sketch, "E322", {"start": v(3.26, -40) * mm, "mid": v(5.03, -39.27) * mm, "end": v(5.76, -37.5) * mm});
            skArc(sketch, "E323", {"start": v(-0.74, -37.5) * mm, "mid": v(-1.47, -35.73) * mm, "end": v(-3.24, -35) * mm});
            skArc(sketch, "E324", {"start": v(-3.24, -35) * mm, "mid": v(-5, -35.73) * mm, "end": v(-5.74, -37.5) * mm});
            skArc(sketch, "E325", {"start": v(-5.74, -37.5) * mm, "mid": v(-5, -39.27) * mm, "end": v(-3.24, -40) * mm});
            skArc(sketch, "E326", {"start": v(-3.24, -40) * mm, "mid": v(-1.47, -39.27) * mm, "end": v(-0.74, -37.5) * mm});
            skLineSegment(sketch, "E327", {"start": v(-9.5, -45.73) * mm, "end": v(-9.5, -48.73) * mm});
            skLineSegment(sketch, "E328", {"start": v(-9.5, -48.73) * mm, "end": v(-7.5, -48.73) * mm});
            skLineSegment(sketch, "E329", {"start": v(-7.5, -48.73) * mm, "end": v(-7.5, -45.73) * mm});
            skLineSegment(sketch, "E330", {"start": v(-7.5, -45.73) * mm, "end": v(-9.5, -45.73) * mm});
            skLineSegment(sketch, "E331", {"start": v(-1.75, -56.51) * mm, "end": v(-1.73, -56.57) * mm});
            skLineSegment(sketch, "E332", {"start": v(-1.73, -56.57) * mm, "end": v(-1.65, -56.81) * mm});
            skLineSegment(sketch, "E333", {"start": v(-1.65, -56.81) * mm, "end": v(-1.6, -56.95) * mm});
            skLineSegment(sketch, "E334", {"start": v(-1.6, -56.95) * mm, "end": v(-1.56, -57.05) * mm});
            skLineSegment(sketch, "E335", {"start": v(-1.56, -57.05) * mm, "end": v(-1.5, -57.13) * mm});
            skLineSegment(sketch, "E336", {"start": v(-1.5, -57.13) * mm, "end": v(-1.43, -57.22) * mm});
            skLineSegment(sketch, "E337", {"start": v(-1.43, -57.22) * mm, "end": v(-1.4, -57.26) * mm});
            skLineSegment(sketch, "E338", {"start": v(-1.4, -57.26) * mm, "end": v(-1.4, -57.3) * mm});
            skLineSegment(sketch, "E339", {"start": v(-1.4, -57.3) * mm, "end": v(-1.36, -57.35) * mm});
            skLineSegment(sketch, "E340", {"start": v(-1.36, -57.35) * mm, "end": v(-1.27, -57.44) * mm});
            skLineSegment(sketch, "E341", {"start": v(-1.27, -57.44) * mm, "end": v(-1.08, -57.62) * mm});
            skLineSegment(sketch, "E342", {"start": v(-1.08, -57.62) * mm, "end": v(-1.03, -57.67) * mm});
            skLineSegment(sketch, "E343", {"start": v(-1.03, -57.67) * mm, "end": v(-0.98, -57.69) * mm});
            skLineSegment(sketch, "E344", {"start": v(-0.98, -57.69) * mm, "end": v(-0.96, -57.7) * mm});
            skLineSegment(sketch, "E345", {"start": v(-0.96, -57.7) * mm, "end": v(-0.95, -57.7) * mm});
            skLineSegment(sketch, "E346", {"start": v(-0.95, -57.7) * mm, "end": v(-0.92, -57.73) * mm});
            skLineSegment(sketch, "E347", {"start": v(-0.92, -57.73) * mm, "end": v(-0.86, -57.76) * mm});
            skLineSegment(sketch, "E348", {"start": v(-0.86, -57.76) * mm, "end": v(-0.58, -57.9) * mm});
            skLineSegment(sketch, "E349", {"start": v(-0.58, -57.9) * mm, "end": v(-0.46, -57.94) * mm});
            skLineSegment(sketch, "E350", {"start": v(-0.46, -57.94) * mm, "end": v(-0.32, -57.97) * mm});
            skLineSegment(sketch, "E351", {"start": v(-0.32, -57.97) * mm, "end": v(-0.16, -57.99) * mm});
            skLineSegment(sketch, "E352", {"start": v(-0.16, -57.99) * mm, "end": v(0, -58) * mm});
            skLineSegment(sketch, "E353", {"start": v(0, -58) * mm, "end": v(0.17, -57.99) * mm});
            skLineSegment(sketch, "E354", {"start": v(0.17, -57.99) * mm, "end": v(0.33, -57.97) * mm});
            skLineSegment(sketch, "E355", {"start": v(0.33, -57.97) * mm, "end": v(0.48, -57.94) * mm});
            skLineSegment(sketch, "E356", {"start": v(0.48, -57.94) * mm, "end": v(0.6, -57.9) * mm});
            skLineSegment(sketch, "E357", {"start": v(0.6, -57.9) * mm, "end": v(0.9, -57.77) * mm});
            skLineSegment(sketch, "E358", {"start": v(0.9, -57.77) * mm, "end": v(0.96, -57.73) * mm});
            skLineSegment(sketch, "E359", {"start": v(0.96, -57.73) * mm, "end": v(0.98, -57.7) * mm});
            skLineSegment(sketch, "E360", {"start": v(0.98, -57.7) * mm, "end": v(0.99, -57.7) * mm});
            skLineSegment(sketch, "E361", {"start": v(0.99, -57.7) * mm, "end": v(1, -57.69) * mm});
            skLineSegment(sketch, "E362", {"start": v(1, -57.69) * mm, "end": v(1.04, -57.67) * mm});
            skLineSegment(sketch, "E363", {"start": v(1.04, -57.67) * mm, "end": v(1.1, -57.63) * mm});
            skLineSegment(sketch, "E364", {"start": v(1.1, -57.63) * mm, "end": v(1.24, -57.5) * mm});
            skLineSegment(sketch, "E365", {"start": v(1.24, -57.5) * mm, "end": v(1.37, -57.38) * mm});
            skLineSegment(sketch, "E366", {"start": v(1.37, -57.38) * mm, "end": v(1.4, -57.33) * mm});
            skLineSegment(sketch, "E367", {"start": v(1.4, -57.33) * mm, "end": v(1.43, -57.3) * mm});
            skLineSegment(sketch, "E368", {"start": v(1.43, -57.3) * mm, "end": v(1.44, -57.26) * mm});
            skLineSegment(sketch, "E369", {"start": v(1.44, -57.26) * mm, "end": v(1.46, -57.22) * mm});
            skLineSegment(sketch, "E370", {"start": v(1.46, -57.22) * mm, "end": v(1.53, -57.14) * mm});
            skLineSegment(sketch, "E371", {"start": v(1.53, -57.14) * mm, "end": v(1.57, -57.08) * mm});
            skLineSegment(sketch, "E372", {"start": v(1.57, -57.08) * mm, "end": v(1.61, -56.99) * mm});
            skLineSegment(sketch, "E373", {"start": v(1.61, -56.99) * mm, "end": v(1.75, -56.59) * mm});
            skLineSegment(sketch, "E374", {"start": v(1.75, -56.59) * mm, "end": v(1.78, -56.48) * mm});
            skLineSegment(sketch, "E375", {"start": v(1.78, -56.48) * mm, "end": v(1.78, -49.5) * mm});
            skLineSegment(sketch, "E376", {"start": v(1.78, -49.5) * mm, "end": v(1.76, -49.42) * mm});
            skLineSegment(sketch, "E377", {"start": v(1.76, -49.42) * mm, "end": v(1.67, -49.18) * mm});
            skLineSegment(sketch, "E378", {"start": v(1.67, -49.18) * mm, "end": v(1.6, -49.01) * mm});
            skLineSegment(sketch, "E379", {"start": v(1.6, -49.01) * mm, "end": v(1.52, -48.86) * mm});
            skLineSegment(sketch, "E380", {"start": v(1.52, -48.86) * mm, "end": v(1.45, -48.76) * mm});
            skLineSegment(sketch, "E381", {"start": v(1.45, -48.76) * mm, "end": v(1.43, -48.7) * mm});
            skLineSegment(sketch, "E382", {"start": v(1.43, -48.7) * mm, "end": v(1.4, -48.66) * mm});
            skLineSegment(sketch, "E383", {"start": v(1.4, -48.66) * mm, "end": v(1.32, -48.58) * mm});
            skLineSegment(sketch, "E384", {"start": v(1.32, -48.58) * mm, "end": v(1.07, -48.35) * mm});
            skLineSegment(sketch, "E385", {"start": v(1.07, -48.35) * mm, "end": v(0.95, -48.27) * mm});
            skLineSegment(sketch, "E386", {"start": v(0.95, -48.27) * mm, "end": v(0.8, -48.2) * mm});
            skLineSegment(sketch, "E387", {"start": v(0.8, -48.2) * mm, "end": v(0.63, -48.12) * mm});
            skLineSegment(sketch, "E388", {"start": v(0.63, -48.12) * mm, "end": v(0.47, -48.06) * mm});
            skLineSegment(sketch, "E389", {"start": v(0.47, -48.06) * mm, "end": v(0.4, -48.05) * mm});
            skLineSegment(sketch, "E390", {"start": v(0.4, -48.05) * mm, "end": v(0.28, -48.04) * mm});
            skLineSegment(sketch, "E391", {"start": v(0.28, -48.04) * mm, "end": v(0.01, -48.03) * mm});
            skLineSegment(sketch, "E392", {"start": v(0.01, -48.03) * mm, "end": v(-0.25, -48.04) * mm});
            skLineSegment(sketch, "E393", {"start": v(-0.25, -48.04) * mm, "end": v(-0.36, -48.05) * mm});
            skLineSegment(sketch, "E394", {"start": v(-0.36, -48.05) * mm, "end": v(-0.45, -48.06) * mm});
            skLineSegment(sketch, "E395", {"start": v(-0.45, -48.06) * mm, "end": v(-0.64, -48.13) * mm});
            skLineSegment(sketch, "E396", {"start": v(-0.64, -48.13) * mm, "end": v(-0.84, -48.23) * mm});
            skLineSegment(sketch, "E397", {"start": v(-0.84, -48.23) * mm, "end": v(-1.03, -48.35) * mm});
            skLineSegment(sketch, "E398", {"start": v(-1.03, -48.35) * mm, "end": v(-1.2, -48.49) * mm});
            skLineSegment(sketch, "E399", {"start": v(-1.2, -48.49) * mm, "end": v(-1.4, -48.67) * mm});
            skLineSegment(sketch, "E400", {"start": v(-1.4, -48.67) * mm, "end": v(-1.4, -48.7) * mm});
            skLineSegment(sketch, "E401", {"start": v(-1.4, -48.7) * mm, "end": v(-1.43, -48.76) * mm});
            skLineSegment(sketch, "E402", {"start": v(-1.43, -48.76) * mm, "end": v(-1.5, -48.86) * mm});
            skLineSegment(sketch, "E403", {"start": v(-1.5, -48.86) * mm, "end": v(-1.58, -49.01) * mm});
            skLineSegment(sketch, "E404", {"start": v(-1.58, -49.01) * mm, "end": v(-1.65, -49.18) * mm});
            skLineSegment(sketch, "E405", {"start": v(-1.65, -49.18) * mm, "end": v(-1.73, -49.42) * mm});
            skLineSegment(sketch, "E406", {"start": v(-1.73, -49.42) * mm, "end": v(-1.75, -49.5) * mm});
            skLineSegment(sketch, "E407", {"start": v(-1.75, -49.5) * mm, "end": v(-1.75, -56.51) * mm});
            skLineSegment(sketch, "E408", {"start": v(9.5, -32.48) * mm, "end": v(9.5, -61.97) * mm});
            skLineSegment(sketch, "E409", {"start": v(9.5, -61.97) * mm, "end": v(24.5, -61.97) * mm});
            skLineSegment(sketch, "E410", {"start": v(24.5, -61.97) * mm, "end": v(24.5, -32.48) * mm});
            skLineSegment(sketch, "E411", {"start": v(24.5, -32.48) * mm, "end": v(9.5, -32.48) * mm});
            skArc(sketch, "E412", {"start": v(21.51, -37.5) * mm, "mid": v(21.15, -36.62) * mm, "end": v(20.26, -36.25) * mm});
            skArc(sketch, "E413", {"start": v(20.26, -36.25) * mm, "mid": v(19.38, -36.62) * mm, "end": v(19.01, -37.5) * mm});
            skArc(sketch, "E414", {"start": v(19.01, -37.5) * mm, "mid": v(19.38, -38.39) * mm, "end": v(20.26, -38.75) * mm});
            skArc(sketch, "E415", {"start": v(20.26, -38.75) * mm, "mid": v(21.15, -38.39) * mm, "end": v(21.51, -37.5) * mm});
            skArc(sketch, "E416", {"start": v(15.01, -37.5) * mm, "mid": v(14.65, -36.62) * mm, "end": v(13.76, -36.25) * mm});
            skArc(sketch, "E417", {"start": v(13.76, -36.25) * mm, "mid": v(12.88, -36.62) * mm, "end": v(12.51, -37.5) * mm});
            skArc(sketch, "E418", {"start": v(12.51, -37.5) * mm, "mid": v(12.88, -38.39) * mm, "end": v(13.76, -38.75) * mm});
            skArc(sketch, "E419", {"start": v(13.76, -38.75) * mm, "mid": v(14.65, -38.39) * mm, "end": v(15.01, -37.5) * mm});
            skArc(sketch, "E420", {"start": v(22.76, -37.5) * mm, "mid": v(22.03, -35.73) * mm, "end": v(20.26, -35) * mm});
            skArc(sketch, "E421", {"start": v(20.26, -35) * mm, "mid": v(18.5, -35.73) * mm, "end": v(17.76, -37.5) * mm});
            skArc(sketch, "E422", {"start": v(17.76, -37.5) * mm, "mid": v(18.5, -39.27) * mm, "end": v(20.26, -40) * mm});
            skArc(sketch, "E423", {"start": v(20.26, -40) * mm, "mid": v(22.03, -39.27) * mm, "end": v(22.76, -37.5) * mm});
            skArc(sketch, "E424", {"start": v(16.26, -37.5) * mm, "mid": v(15.53, -35.73) * mm, "end": v(13.76, -35) * mm});
            skArc(sketch, "E425", {"start": v(13.76, -35) * mm, "mid": v(12, -35.73) * mm, "end": v(11.26, -37.5) * mm});
            skArc(sketch, "E426", {"start": v(11.26, -37.5) * mm, "mid": v(12, -39.27) * mm, "end": v(13.76, -40) * mm});
            skArc(sketch, "E427", {"start": v(13.76, -40) * mm, "mid": v(15.53, -39.27) * mm, "end": v(16.26, -37.5) * mm});
            skLineSegment(sketch, "E428", {"start": v(7.5, -45.73) * mm, "end": v(7.5, -48.73) * mm});
            skLineSegment(sketch, "E429", {"start": v(7.5, -48.73) * mm, "end": v(9.5, -48.73) * mm});
            skLineSegment(sketch, "E430", {"start": v(9.5, -48.73) * mm, "end": v(9.5, -45.73) * mm});
            skLineSegment(sketch, "E431", {"start": v(9.5, -45.73) * mm, "end": v(7.5, -45.73) * mm});
            skLineSegment(sketch, "E432", {"start": v(15.25, -56.51) * mm, "end": v(15.27, -56.57) * mm});
            skLineSegment(sketch, "E433", {"start": v(15.27, -56.57) * mm, "end": v(15.35, -56.81) * mm});
            skLineSegment(sketch, "E434", {"start": v(15.35, -56.81) * mm, "end": v(15.4, -56.95) * mm});
            skLineSegment(sketch, "E435", {"start": v(15.4, -56.95) * mm, "end": v(15.44, -57.05) * mm});
            skLineSegment(sketch, "E436", {"start": v(15.44, -57.05) * mm, "end": v(15.5, -57.13) * mm});
            skLineSegment(sketch, "E437", {"start": v(15.5, -57.13) * mm, "end": v(15.57, -57.22) * mm});
            skLineSegment(sketch, "E438", {"start": v(15.57, -57.22) * mm, "end": v(15.6, -57.26) * mm});
            skLineSegment(sketch, "E439", {"start": v(15.6, -57.26) * mm, "end": v(15.6, -57.3) * mm});
            skLineSegment(sketch, "E440", {"start": v(15.6, -57.3) * mm, "end": v(15.64, -57.35) * mm});
            skLineSegment(sketch, "E441", {"start": v(15.64, -57.35) * mm, "end": v(15.73, -57.44) * mm});
            skLineSegment(sketch, "E442", {"start": v(15.73, -57.44) * mm, "end": v(15.92, -57.62) * mm});
            skLineSegment(sketch, "E443", {"start": v(15.92, -57.62) * mm, "end": v(15.97, -57.67) * mm});
            skLineSegment(sketch, "E444", {"start": v(15.97, -57.67) * mm, "end": v(16.02, -57.69) * mm});
            skLineSegment(sketch, "E445", {"start": v(16.02, -57.69) * mm, "end": v(16.04, -57.7) * mm});
            skLineSegment(sketch, "E446", {"start": v(16.04, -57.7) * mm, "end": v(16.05, -57.7) * mm});
            skLineSegment(sketch, "E447", {"start": v(16.05, -57.7) * mm, "end": v(16.08, -57.73) * mm});
            skLineSegment(sketch, "E448", {"start": v(16.08, -57.73) * mm, "end": v(16.14, -57.76) * mm});
            skLineSegment(sketch, "E449", {"start": v(16.14, -57.76) * mm, "end": v(16.42, -57.9) * mm});
            skLineSegment(sketch, "E450", {"start": v(16.42, -57.9) * mm, "end": v(16.54, -57.94) * mm});
            skLineSegment(sketch, "E451", {"start": v(16.54, -57.94) * mm, "end": v(16.68, -57.97) * mm});
            skLineSegment(sketch, "E452", {"start": v(16.68, -57.97) * mm, "end": v(16.84, -57.99) * mm});
            skLineSegment(sketch, "E453", {"start": v(16.84, -57.99) * mm, "end": v(17, -58) * mm});
            skLineSegment(sketch, "E454", {"start": v(17, -58) * mm, "end": v(17.17, -57.99) * mm});
            skLineSegment(sketch, "E455", {"start": v(17.17, -57.99) * mm, "end": v(17.33, -57.97) * mm});
            skLineSegment(sketch, "E456", {"start": v(17.33, -57.97) * mm, "end": v(17.48, -57.94) * mm});
            skLineSegment(sketch, "E457", {"start": v(17.48, -57.94) * mm, "end": v(17.6, -57.9) * mm});
            skLineSegment(sketch, "E458", {"start": v(17.6, -57.9) * mm, "end": v(17.9, -57.77) * mm});
            skLineSegment(sketch, "E459", {"start": v(17.9, -57.77) * mm, "end": v(17.96, -57.73) * mm});
            skLineSegment(sketch, "E460", {"start": v(17.96, -57.73) * mm, "end": v(17.98, -57.7) * mm});
            skLineSegment(sketch, "E461", {"start": v(17.98, -57.7) * mm, "end": v(17.99, -57.7) * mm});
            skLineSegment(sketch, "E462", {"start": v(17.99, -57.7) * mm, "end": v(18, -57.69) * mm});
            skLineSegment(sketch, "E463", {"start": v(18, -57.69) * mm, "end": v(18.04, -57.67) * mm});
            skLineSegment(sketch, "E464", {"start": v(18.04, -57.67) * mm, "end": v(18.1, -57.63) * mm});
            skLineSegment(sketch, "E465", {"start": v(18.1, -57.63) * mm, "end": v(18.24, -57.5) * mm});
            skLineSegment(sketch, "E466", {"start": v(18.24, -57.5) * mm, "end": v(18.37, -57.38) * mm});
            skLineSegment(sketch, "E467", {"start": v(18.37, -57.38) * mm, "end": v(18.4, -57.33) * mm});
            skLineSegment(sketch, "E468", {"start": v(18.4, -57.33) * mm, "end": v(18.43, -57.3) * mm});
            skLineSegment(sketch, "E469", {"start": v(18.43, -57.3) * mm, "end": v(18.44, -57.26) * mm});
            skLineSegment(sketch, "E470", {"start": v(18.44, -57.26) * mm, "end": v(18.46, -57.22) * mm});
            skLineSegment(sketch, "E471", {"start": v(18.46, -57.22) * mm, "end": v(18.53, -57.14) * mm});
            skLineSegment(sketch, "E472", {"start": v(18.53, -57.14) * mm, "end": v(18.57, -57.08) * mm});
            skLineSegment(sketch, "E473", {"start": v(18.57, -57.08) * mm, "end": v(18.61, -56.99) * mm});
            skLineSegment(sketch, "E474", {"start": v(18.61, -56.99) * mm, "end": v(18.75, -56.59) * mm});
            skLineSegment(sketch, "E475", {"start": v(18.75, -56.59) * mm, "end": v(18.78, -56.48) * mm});
            skLineSegment(sketch, "E476", {"start": v(18.78, -56.48) * mm, "end": v(18.78, -49.5) * mm});
            skLineSegment(sketch, "E477", {"start": v(18.78, -49.5) * mm, "end": v(18.76, -49.42) * mm});
            skLineSegment(sketch, "E478", {"start": v(18.76, -49.42) * mm, "end": v(18.67, -49.18) * mm});
            skLineSegment(sketch, "E479", {"start": v(18.67, -49.18) * mm, "end": v(18.6, -49.01) * mm});
            skLineSegment(sketch, "E480", {"start": v(18.6, -49.01) * mm, "end": v(18.52, -48.86) * mm});
            skLineSegment(sketch, "E481", {"start": v(18.52, -48.86) * mm, "end": v(18.45, -48.76) * mm});
            skLineSegment(sketch, "E482", {"start": v(18.45, -48.76) * mm, "end": v(18.43, -48.7) * mm});
            skLineSegment(sketch, "E483", {"start": v(18.43, -48.7) * mm, "end": v(18.4, -48.66) * mm});
            skLineSegment(sketch, "E484", {"start": v(18.4, -48.66) * mm, "end": v(18.32, -48.58) * mm});
            skLineSegment(sketch, "E485", {"start": v(18.32, -48.58) * mm, "end": v(18.07, -48.35) * mm});
            skLineSegment(sketch, "E486", {"start": v(18.07, -48.35) * mm, "end": v(17.95, -48.27) * mm});
            skLineSegment(sketch, "E487", {"start": v(17.95, -48.27) * mm, "end": v(17.8, -48.2) * mm});
            skLineSegment(sketch, "E488", {"start": v(17.8, -48.2) * mm, "end": v(17.63, -48.12) * mm});
            skLineSegment(sketch, "E489", {"start": v(17.63, -48.12) * mm, "end": v(17.47, -48.06) * mm});
            skLineSegment(sketch, "E490", {"start": v(17.47, -48.06) * mm, "end": v(17.4, -48.05) * mm});
            skLineSegment(sketch, "E491", {"start": v(17.4, -48.05) * mm, "end": v(17.28, -48.04) * mm});
            skLineSegment(sketch, "E492", {"start": v(17.28, -48.04) * mm, "end": v(17.01, -48.03) * mm});
            skLineSegment(sketch, "E493", {"start": v(17.01, -48.03) * mm, "end": v(16.75, -48.04) * mm});
            skLineSegment(sketch, "E494", {"start": v(16.75, -48.04) * mm, "end": v(16.64, -48.05) * mm});
            skLineSegment(sketch, "E495", {"start": v(16.64, -48.05) * mm, "end": v(16.55, -48.06) * mm});
            skLineSegment(sketch, "E496", {"start": v(16.55, -48.06) * mm, "end": v(16.36, -48.13) * mm});
            skLineSegment(sketch, "E497", {"start": v(16.36, -48.13) * mm, "end": v(16.16, -48.23) * mm});
            skLineSegment(sketch, "E498", {"start": v(16.16, -48.23) * mm, "end": v(15.97, -48.35) * mm});
            skLineSegment(sketch, "E499", {"start": v(15.97, -48.35) * mm, "end": v(15.8, -48.49) * mm});
            skLineSegment(sketch, "E500", {"start": v(15.8, -48.49) * mm, "end": v(15.6, -48.67) * mm});
            skLineSegment(sketch, "E501", {"start": v(15.6, -48.67) * mm, "end": v(15.6, -48.7) * mm});
            skLineSegment(sketch, "E502", {"start": v(15.6, -48.7) * mm, "end": v(15.57, -48.76) * mm});
            skLineSegment(sketch, "E503", {"start": v(15.57, -48.76) * mm, "end": v(15.5, -48.86) * mm});
            skLineSegment(sketch, "E504", {"start": v(15.5, -48.86) * mm, "end": v(15.42, -49.01) * mm});
            skLineSegment(sketch, "E505", {"start": v(15.42, -49.01) * mm, "end": v(15.35, -49.18) * mm});
            skLineSegment(sketch, "E506", {"start": v(15.35, -49.18) * mm, "end": v(15.27, -49.42) * mm});
            skLineSegment(sketch, "E507", {"start": v(15.27, -49.42) * mm, "end": v(15.25, -49.5) * mm});
            skLineSegment(sketch, "E508", {"start": v(15.25, -49.5) * mm, "end": v(15.25, -56.51) * mm});
            skLineSegment(sketch, "E509", {"start": v(24.5, -45.73) * mm, "end": v(24.5, -48.73) * mm});
            skLineSegment(sketch, "E510", {"start": v(24.5, -48.73) * mm, "end": v(26.5, -48.73) * mm});
            skLineSegment(sketch, "E511", {"start": v(26.5, -48.73) * mm, "end": v(26.5, -45.73) * mm});
            skLineSegment(sketch, "E512", {"start": v(26.5, -45.73) * mm, "end": v(24.5, -45.73) * mm});
            skLineSegment(sketch, "E513", {"start": v(26.5, -32.48) * mm, "end": v(26.5, -61.97) * mm});
            skLineSegment(sketch, "E514", {"start": v(26.5, -61.97) * mm, "end": v(41.5, -61.97) * mm});
            skLineSegment(sketch, "E515", {"start": v(41.5, -61.97) * mm, "end": v(41.5, -32.48) * mm});
            skLineSegment(sketch, "E516", {"start": v(41.5, -32.48) * mm, "end": v(26.5, -32.48) * mm});
            skArc(sketch, "E517", {"start": v(38.51, -37.5) * mm, "mid": v(38.15, -36.62) * mm, "end": v(37.26, -36.25) * mm});
            skArc(sketch, "E518", {"start": v(37.26, -36.25) * mm, "mid": v(36.38, -36.62) * mm, "end": v(36.01, -37.5) * mm});
            skArc(sketch, "E519", {"start": v(36.01, -37.5) * mm, "mid": v(36.38, -38.39) * mm, "end": v(37.26, -38.75) * mm});
            skArc(sketch, "E520", {"start": v(37.26, -38.75) * mm, "mid": v(38.15, -38.39) * mm, "end": v(38.51, -37.5) * mm});
            skArc(sketch, "E521", {"start": v(32.01, -37.5) * mm, "mid": v(31.65, -36.62) * mm, "end": v(30.76, -36.25) * mm});
            skArc(sketch, "E522", {"start": v(30.76, -36.25) * mm, "mid": v(29.88, -36.62) * mm, "end": v(29.51, -37.5) * mm});
            skArc(sketch, "E523", {"start": v(29.51, -37.5) * mm, "mid": v(29.88, -38.39) * mm, "end": v(30.76, -38.75) * mm});
            skArc(sketch, "E524", {"start": v(30.76, -38.75) * mm, "mid": v(31.65, -38.39) * mm, "end": v(32.01, -37.5) * mm});
            skArc(sketch, "E525", {"start": v(39.76, -37.5) * mm, "mid": v(39.03, -35.73) * mm, "end": v(37.26, -35) * mm});
            skArc(sketch, "E526", {"start": v(37.26, -35) * mm, "mid": v(35.5, -35.73) * mm, "end": v(34.76, -37.5) * mm});
            skArc(sketch, "E527", {"start": v(34.76, -37.5) * mm, "mid": v(35.5, -39.27) * mm, "end": v(37.26, -40) * mm});
            skArc(sketch, "E528", {"start": v(37.26, -40) * mm, "mid": v(39.03, -39.27) * mm, "end": v(39.76, -37.5) * mm});
            skArc(sketch, "E529", {"start": v(33.26, -37.5) * mm, "mid": v(32.53, -35.73) * mm, "end": v(30.76, -35) * mm});
            skArc(sketch, "E530", {"start": v(30.76, -35) * mm, "mid": v(29, -35.73) * mm, "end": v(28.26, -37.5) * mm});
            skArc(sketch, "E531", {"start": v(28.26, -37.5) * mm, "mid": v(29, -39.27) * mm, "end": v(30.76, -40) * mm});
            skArc(sketch, "E532", {"start": v(30.76, -40) * mm, "mid": v(32.53, -39.27) * mm, "end": v(33.26, -37.5) * mm});
            skLineSegment(sketch, "E533", {"start": v(32.25, -56.51) * mm, "end": v(32.27, -56.57) * mm});
            skLineSegment(sketch, "E534", {"start": v(32.27, -56.57) * mm, "end": v(32.35, -56.81) * mm});
            skLineSegment(sketch, "E535", {"start": v(32.35, -56.81) * mm, "end": v(32.4, -56.95) * mm});
            skLineSegment(sketch, "E536", {"start": v(32.4, -56.95) * mm, "end": v(32.44, -57.05) * mm});
            skLineSegment(sketch, "E537", {"start": v(32.44, -57.05) * mm, "end": v(32.5, -57.13) * mm});
            skLineSegment(sketch, "E538", {"start": v(32.5, -57.13) * mm, "end": v(32.57, -57.22) * mm});
            skLineSegment(sketch, "E539", {"start": v(32.57, -57.22) * mm, "end": v(32.6, -57.26) * mm});
            skLineSegment(sketch, "E540", {"start": v(32.6, -57.26) * mm, "end": v(32.6, -57.3) * mm});
            skLineSegment(sketch, "E541", {"start": v(32.6, -57.3) * mm, "end": v(32.64, -57.35) * mm});
            skLineSegment(sketch, "E542", {"start": v(32.64, -57.35) * mm, "end": v(32.73, -57.44) * mm});
            skLineSegment(sketch, "E543", {"start": v(32.73, -57.44) * mm, "end": v(32.92, -57.62) * mm});
            skLineSegment(sketch, "E544", {"start": v(32.92, -57.62) * mm, "end": v(32.97, -57.67) * mm});
            skLineSegment(sketch, "E545", {"start": v(32.97, -57.67) * mm, "end": v(33.02, -57.69) * mm});
            skLineSegment(sketch, "E546", {"start": v(33.02, -57.69) * mm, "end": v(33.04, -57.7) * mm});
            skLineSegment(sketch, "E547", {"start": v(33.04, -57.7) * mm, "end": v(33.05, -57.7) * mm});
            skLineSegment(sketch, "E548", {"start": v(33.05, -57.7) * mm, "end": v(33.08, -57.73) * mm});
            skLineSegment(sketch, "E549", {"start": v(33.08, -57.73) * mm, "end": v(33.14, -57.76) * mm});
            skLineSegment(sketch, "E550", {"start": v(33.14, -57.76) * mm, "end": v(33.42, -57.9) * mm});
            skLineSegment(sketch, "E551", {"start": v(33.42, -57.9) * mm, "end": v(33.54, -57.94) * mm});
            skLineSegment(sketch, "E552", {"start": v(33.54, -57.94) * mm, "end": v(33.68, -57.97) * mm});
            skLineSegment(sketch, "E553", {"start": v(33.68, -57.97) * mm, "end": v(33.84, -57.99) * mm});
            skLineSegment(sketch, "E554", {"start": v(33.84, -57.99) * mm, "end": v(34, -58) * mm});
            skLineSegment(sketch, "E555", {"start": v(34, -58) * mm, "end": v(34.17, -57.99) * mm});
            skLineSegment(sketch, "E556", {"start": v(34.17, -57.99) * mm, "end": v(34.33, -57.97) * mm});
            skLineSegment(sketch, "E557", {"start": v(34.33, -57.97) * mm, "end": v(34.48, -57.94) * mm});
            skLineSegment(sketch, "E558", {"start": v(34.48, -57.94) * mm, "end": v(34.6, -57.9) * mm});
            skLineSegment(sketch, "E559", {"start": v(34.6, -57.9) * mm, "end": v(34.9, -57.77) * mm});
            skLineSegment(sketch, "E560", {"start": v(34.9, -57.77) * mm, "end": v(34.96, -57.73) * mm});
            skLineSegment(sketch, "E561", {"start": v(34.96, -57.73) * mm, "end": v(34.98, -57.7) * mm});
            skLineSegment(sketch, "E562", {"start": v(34.98, -57.7) * mm, "end": v(34.99, -57.7) * mm});
            skLineSegment(sketch, "E563", {"start": v(34.99, -57.7) * mm, "end": v(35, -57.69) * mm});
            skLineSegment(sketch, "E564", {"start": v(35, -57.69) * mm, "end": v(35.04, -57.67) * mm});
            skLineSegment(sketch, "E565", {"start": v(35.04, -57.67) * mm, "end": v(35.1, -57.63) * mm});
            skLineSegment(sketch, "E566", {"start": v(35.1, -57.63) * mm, "end": v(35.24, -57.5) * mm});
            skLineSegment(sketch, "E567", {"start": v(35.24, -57.5) * mm, "end": v(35.37, -57.38) * mm});
            skLineSegment(sketch, "E568", {"start": v(35.37, -57.38) * mm, "end": v(35.4, -57.33) * mm});
            skLineSegment(sketch, "E569", {"start": v(35.4, -57.33) * mm, "end": v(35.43, -57.3) * mm});
            skLineSegment(sketch, "E570", {"start": v(35.43, -57.3) * mm, "end": v(35.44, -57.26) * mm});
            skLineSegment(sketch, "E571", {"start": v(35.44, -57.26) * mm, "end": v(35.46, -57.22) * mm});
            skLineSegment(sketch, "E572", {"start": v(35.46, -57.22) * mm, "end": v(35.53, -57.14) * mm});
            skLineSegment(sketch, "E573", {"start": v(35.53, -57.14) * mm, "end": v(35.57, -57.08) * mm});
            skLineSegment(sketch, "E574", {"start": v(35.57, -57.08) * mm, "end": v(35.61, -56.99) * mm});
            skLineSegment(sketch, "E575", {"start": v(35.61, -56.99) * mm, "end": v(35.75, -56.59) * mm});
            skLineSegment(sketch, "E576", {"start": v(35.75, -56.59) * mm, "end": v(35.78, -56.48) * mm});
            skLineSegment(sketch, "E577", {"start": v(35.78, -56.48) * mm, "end": v(35.78, -49.5) * mm});
            skLineSegment(sketch, "E578", {"start": v(35.78, -49.5) * mm, "end": v(35.76, -49.42) * mm});
            skLineSegment(sketch, "E579", {"start": v(35.76, -49.42) * mm, "end": v(35.67, -49.18) * mm});
            skLineSegment(sketch, "E580", {"start": v(35.67, -49.18) * mm, "end": v(35.6, -49.01) * mm});
            skLineSegment(sketch, "E581", {"start": v(35.6, -49.01) * mm, "end": v(35.52, -48.86) * mm});
            skLineSegment(sketch, "E582", {"start": v(35.52, -48.86) * mm, "end": v(35.45, -48.76) * mm});
            skLineSegment(sketch, "E583", {"start": v(35.45, -48.76) * mm, "end": v(35.43, -48.7) * mm});
            skLineSegment(sketch, "E584", {"start": v(35.43, -48.7) * mm, "end": v(35.4, -48.66) * mm});
            skLineSegment(sketch, "E585", {"start": v(35.4, -48.66) * mm, "end": v(35.32, -48.58) * mm});
            skLineSegment(sketch, "E586", {"start": v(35.32, -48.58) * mm, "end": v(35.07, -48.35) * mm});
            skLineSegment(sketch, "E587", {"start": v(35.07, -48.35) * mm, "end": v(34.95, -48.27) * mm});
            skLineSegment(sketch, "E588", {"start": v(34.95, -48.27) * mm, "end": v(34.8, -48.2) * mm});
            skLineSegment(sketch, "E589", {"start": v(34.8, -48.2) * mm, "end": v(34.63, -48.12) * mm});
            skLineSegment(sketch, "E590", {"start": v(34.63, -48.12) * mm, "end": v(34.47, -48.06) * mm});
            skLineSegment(sketch, "E591", {"start": v(34.47, -48.06) * mm, "end": v(34.4, -48.05) * mm});
            skLineSegment(sketch, "E592", {"start": v(34.4, -48.05) * mm, "end": v(34.28, -48.04) * mm});
            skLineSegment(sketch, "E593", {"start": v(34.28, -48.04) * mm, "end": v(34.01, -48.03) * mm});
            skLineSegment(sketch, "E594", {"start": v(34.01, -48.03) * mm, "end": v(33.75, -48.04) * mm});
            skLineSegment(sketch, "E595", {"start": v(33.75, -48.04) * mm, "end": v(33.64, -48.05) * mm});
            skLineSegment(sketch, "E596", {"start": v(33.64, -48.05) * mm, "end": v(33.55, -48.06) * mm});
            skLineSegment(sketch, "E597", {"start": v(33.55, -48.06) * mm, "end": v(33.36, -48.13) * mm});
            skLineSegment(sketch, "E598", {"start": v(33.36, -48.13) * mm, "end": v(33.16, -48.23) * mm});
            skLineSegment(sketch, "E599", {"start": v(33.16, -48.23) * mm, "end": v(32.97, -48.35) * mm});
            skLineSegment(sketch, "E600", {"start": v(32.97, -48.35) * mm, "end": v(32.8, -48.49) * mm});
            skLineSegment(sketch, "E601", {"start": v(32.8, -48.49) * mm, "end": v(32.6, -48.67) * mm});
            skLineSegment(sketch, "E602", {"start": v(32.6, -48.67) * mm, "end": v(32.6, -48.7) * mm});
            skLineSegment(sketch, "E603", {"start": v(32.6, -48.7) * mm, "end": v(32.57, -48.76) * mm});
            skLineSegment(sketch, "E604", {"start": v(32.57, -48.76) * mm, "end": v(32.5, -48.86) * mm});
            skLineSegment(sketch, "E605", {"start": v(32.5, -48.86) * mm, "end": v(32.42, -49.01) * mm});
            skLineSegment(sketch, "E606", {"start": v(32.42, -49.01) * mm, "end": v(32.35, -49.18) * mm});
            skLineSegment(sketch, "E607", {"start": v(32.35, -49.18) * mm, "end": v(32.27, -49.42) * mm});
            skLineSegment(sketch, "E608", {"start": v(32.27, -49.42) * mm, "end": v(32.25, -49.5) * mm});
            skLineSegment(sketch, "E609", {"start": v(32.25, -49.5) * mm, "end": v(32.25, -56.51) * mm});
            skLineSegment(sketch, "E610", {"start": v(43.5, -32.48) * mm, "end": v(43.5, -61.97) * mm});
            skLineSegment(sketch, "E611", {"start": v(43.5, -61.97) * mm, "end": v(58.5, -61.97) * mm});
            skLineSegment(sketch, "E612", {"start": v(58.5, -61.97) * mm, "end": v(58.5, -32.48) * mm});
            skLineSegment(sketch, "E613", {"start": v(58.5, -32.48) * mm, "end": v(43.5, -32.48) * mm});
            skArc(sketch, "E614", {"start": v(55.51, -37.5) * mm, "mid": v(55.15, -36.62) * mm, "end": v(54.26, -36.25) * mm});
            skArc(sketch, "E615", {"start": v(54.26, -36.25) * mm, "mid": v(53.38, -36.62) * mm, "end": v(53.01, -37.5) * mm});
            skArc(sketch, "E616", {"start": v(53.01, -37.5) * mm, "mid": v(53.38, -38.39) * mm, "end": v(54.26, -38.75) * mm});
            skArc(sketch, "E617", {"start": v(54.26, -38.75) * mm, "mid": v(55.15, -38.39) * mm, "end": v(55.51, -37.5) * mm});
            skArc(sketch, "E618", {"start": v(49.01, -37.5) * mm, "mid": v(48.65, -36.62) * mm, "end": v(47.76, -36.25) * mm});
            skArc(sketch, "E619", {"start": v(47.76, -36.25) * mm, "mid": v(46.88, -36.62) * mm, "end": v(46.51, -37.5) * mm});
            skArc(sketch, "E620", {"start": v(46.51, -37.5) * mm, "mid": v(46.88, -38.39) * mm, "end": v(47.76, -38.75) * mm});
            skArc(sketch, "E621", {"start": v(47.76, -38.75) * mm, "mid": v(48.65, -38.39) * mm, "end": v(49.01, -37.5) * mm});
            skArc(sketch, "E622", {"start": v(56.76, -37.5) * mm, "mid": v(56.03, -35.73) * mm, "end": v(54.26, -35) * mm});
            skArc(sketch, "E623", {"start": v(54.26, -35) * mm, "mid": v(52.5, -35.73) * mm, "end": v(51.76, -37.5) * mm});
            skArc(sketch, "E624", {"start": v(51.76, -37.5) * mm, "mid": v(52.5, -39.27) * mm, "end": v(54.26, -40) * mm});
            skArc(sketch, "E625", {"start": v(54.26, -40) * mm, "mid": v(56.03, -39.27) * mm, "end": v(56.76, -37.5) * mm});
            skArc(sketch, "E626", {"start": v(50.26, -37.5) * mm, "mid": v(49.53, -35.73) * mm, "end": v(47.76, -35) * mm});
            skArc(sketch, "E627", {"start": v(47.76, -35) * mm, "mid": v(46, -35.73) * mm, "end": v(45.26, -37.5) * mm});
            skArc(sketch, "E628", {"start": v(45.26, -37.5) * mm, "mid": v(46, -39.27) * mm, "end": v(47.76, -40) * mm});
            skArc(sketch, "E629", {"start": v(47.76, -40) * mm, "mid": v(49.53, -39.27) * mm, "end": v(50.26, -37.5) * mm});
            skLineSegment(sketch, "E630", {"start": v(41.5, -45.73) * mm, "end": v(41.5, -48.73) * mm});
            skLineSegment(sketch, "E631", {"start": v(41.5, -48.73) * mm, "end": v(43.5, -48.73) * mm});
            skLineSegment(sketch, "E632", {"start": v(43.5, -48.73) * mm, "end": v(43.5, -45.73) * mm});
            skLineSegment(sketch, "E633", {"start": v(43.5, -45.73) * mm, "end": v(41.5, -45.73) * mm});
            skLineSegment(sketch, "E634", {"start": v(49.25, -56.51) * mm, "end": v(49.27, -56.57) * mm});
            skLineSegment(sketch, "E635", {"start": v(49.27, -56.57) * mm, "end": v(49.35, -56.81) * mm});
            skLineSegment(sketch, "E636", {"start": v(49.35, -56.81) * mm, "end": v(49.4, -56.95) * mm});
            skLineSegment(sketch, "E637", {"start": v(49.4, -56.95) * mm, "end": v(49.44, -57.05) * mm});
            skLineSegment(sketch, "E638", {"start": v(49.44, -57.05) * mm, "end": v(49.5, -57.13) * mm});
            skLineSegment(sketch, "E639", {"start": v(49.5, -57.13) * mm, "end": v(49.57, -57.22) * mm});
            skLineSegment(sketch, "E640", {"start": v(49.57, -57.22) * mm, "end": v(49.6, -57.26) * mm});
            skLineSegment(sketch, "E641", {"start": v(49.6, -57.26) * mm, "end": v(49.6, -57.3) * mm});
            skLineSegment(sketch, "E642", {"start": v(49.6, -57.3) * mm, "end": v(49.64, -57.35) * mm});
            skLineSegment(sketch, "E643", {"start": v(49.64, -57.35) * mm, "end": v(49.73, -57.44) * mm});
            skLineSegment(sketch, "E644", {"start": v(49.73, -57.44) * mm, "end": v(49.92, -57.62) * mm});
            skLineSegment(sketch, "E645", {"start": v(49.92, -57.62) * mm, "end": v(49.97, -57.67) * mm});
            skLineSegment(sketch, "E646", {"start": v(49.97, -57.67) * mm, "end": v(50.02, -57.69) * mm});
            skLineSegment(sketch, "E647", {"start": v(50.02, -57.69) * mm, "end": v(50.04, -57.7) * mm});
            skLineSegment(sketch, "E648", {"start": v(50.04, -57.7) * mm, "end": v(50.05, -57.7) * mm});
            skLineSegment(sketch, "E649", {"start": v(50.05, -57.7) * mm, "end": v(50.08, -57.73) * mm});
            skLineSegment(sketch, "E650", {"start": v(50.08, -57.73) * mm, "end": v(50.14, -57.76) * mm});
            skLineSegment(sketch, "E651", {"start": v(50.14, -57.76) * mm, "end": v(50.42, -57.9) * mm});
            skLineSegment(sketch, "E652", {"start": v(50.42, -57.9) * mm, "end": v(50.54, -57.94) * mm});
            skLineSegment(sketch, "E653", {"start": v(50.54, -57.94) * mm, "end": v(50.68, -57.97) * mm});
            skLineSegment(sketch, "E654", {"start": v(50.68, -57.97) * mm, "end": v(50.84, -57.99) * mm});
            skLineSegment(sketch, "E655", {"start": v(50.84, -57.99) * mm, "end": v(51, -58) * mm});
            skLineSegment(sketch, "E656", {"start": v(51, -58) * mm, "end": v(51.17, -57.99) * mm});
            skLineSegment(sketch, "E657", {"start": v(51.17, -57.99) * mm, "end": v(51.33, -57.97) * mm});
            skLineSegment(sketch, "E658", {"start": v(51.33, -57.97) * mm, "end": v(51.48, -57.94) * mm});
            skLineSegment(sketch, "E659", {"start": v(51.48, -57.94) * mm, "end": v(51.6, -57.9) * mm});
            skLineSegment(sketch, "E660", {"start": v(51.6, -57.9) * mm, "end": v(51.9, -57.77) * mm});
            skLineSegment(sketch, "E661", {"start": v(51.9, -57.77) * mm, "end": v(51.96, -57.73) * mm});
            skLineSegment(sketch, "E662", {"start": v(51.96, -57.73) * mm, "end": v(51.98, -57.7) * mm});
            skLineSegment(sketch, "E663", {"start": v(51.98, -57.7) * mm, "end": v(51.99, -57.7) * mm});
            skLineSegment(sketch, "E664", {"start": v(51.99, -57.7) * mm, "end": v(52, -57.69) * mm});
            skLineSegment(sketch, "E665", {"start": v(52, -57.69) * mm, "end": v(52.04, -57.67) * mm});
            skLineSegment(sketch, "E666", {"start": v(52.04, -57.67) * mm, "end": v(52.1, -57.63) * mm});
            skLineSegment(sketch, "E667", {"start": v(52.1, -57.63) * mm, "end": v(52.24, -57.5) * mm});
            skLineSegment(sketch, "E668", {"start": v(52.24, -57.5) * mm, "end": v(52.37, -57.38) * mm});
            skLineSegment(sketch, "E669", {"start": v(52.37, -57.38) * mm, "end": v(52.4, -57.33) * mm});
            skLineSegment(sketch, "E670", {"start": v(52.4, -57.33) * mm, "end": v(52.43, -57.3) * mm});
            skLineSegment(sketch, "E671", {"start": v(52.43, -57.3) * mm, "end": v(52.44, -57.26) * mm});
            skLineSegment(sketch, "E672", {"start": v(52.44, -57.26) * mm, "end": v(52.46, -57.22) * mm});
            skLineSegment(sketch, "E673", {"start": v(52.46, -57.22) * mm, "end": v(52.53, -57.14) * mm});
            skLineSegment(sketch, "E674", {"start": v(52.53, -57.14) * mm, "end": v(52.57, -57.08) * mm});
            skLineSegment(sketch, "E675", {"start": v(52.57, -57.08) * mm, "end": v(52.61, -56.99) * mm});
            skLineSegment(sketch, "E676", {"start": v(52.61, -56.99) * mm, "end": v(52.75, -56.59) * mm});
            skLineSegment(sketch, "E677", {"start": v(52.75, -56.59) * mm, "end": v(52.78, -56.48) * mm});
            skLineSegment(sketch, "E678", {"start": v(52.78, -56.48) * mm, "end": v(52.78, -49.5) * mm});
            skLineSegment(sketch, "E679", {"start": v(52.78, -49.5) * mm, "end": v(52.76, -49.42) * mm});
            skLineSegment(sketch, "E680", {"start": v(52.76, -49.42) * mm, "end": v(52.67, -49.18) * mm});
            skLineSegment(sketch, "E681", {"start": v(52.67, -49.18) * mm, "end": v(52.6, -49.01) * mm});
            skLineSegment(sketch, "E682", {"start": v(52.6, -49.01) * mm, "end": v(52.52, -48.86) * mm});
            skLineSegment(sketch, "E683", {"start": v(52.52, -48.86) * mm, "end": v(52.45, -48.76) * mm});
            skLineSegment(sketch, "E684", {"start": v(52.45, -48.76) * mm, "end": v(52.43, -48.7) * mm});
            skLineSegment(sketch, "E685", {"start": v(52.43, -48.7) * mm, "end": v(52.4, -48.66) * mm});
            skLineSegment(sketch, "E686", {"start": v(52.4, -48.66) * mm, "end": v(52.32, -48.58) * mm});
            skLineSegment(sketch, "E687", {"start": v(52.32, -48.58) * mm, "end": v(52.07, -48.35) * mm});
            skLineSegment(sketch, "E688", {"start": v(52.07, -48.35) * mm, "end": v(51.95, -48.27) * mm});
            skLineSegment(sketch, "E689", {"start": v(51.95, -48.27) * mm, "end": v(51.8, -48.2) * mm});
            skLineSegment(sketch, "E690", {"start": v(51.8, -48.2) * mm, "end": v(51.63, -48.12) * mm});
            skLineSegment(sketch, "E691", {"start": v(51.63, -48.12) * mm, "end": v(51.47, -48.06) * mm});
            skLineSegment(sketch, "E692", {"start": v(51.47, -48.06) * mm, "end": v(51.4, -48.05) * mm});
            skLineSegment(sketch, "E693", {"start": v(51.4, -48.05) * mm, "end": v(51.28, -48.04) * mm});
            skLineSegment(sketch, "E694", {"start": v(51.28, -48.04) * mm, "end": v(51.01, -48.03) * mm});
            skLineSegment(sketch, "E695", {"start": v(51.01, -48.03) * mm, "end": v(50.75, -48.04) * mm});
            skLineSegment(sketch, "E696", {"start": v(50.75, -48.04) * mm, "end": v(50.64, -48.05) * mm});
            skLineSegment(sketch, "E697", {"start": v(50.64, -48.05) * mm, "end": v(50.55, -48.06) * mm});
            skLineSegment(sketch, "E698", {"start": v(50.55, -48.06) * mm, "end": v(50.36, -48.13) * mm});
            skLineSegment(sketch, "E699", {"start": v(50.36, -48.13) * mm, "end": v(50.16, -48.23) * mm});
            skLineSegment(sketch, "E700", {"start": v(50.16, -48.23) * mm, "end": v(49.97, -48.35) * mm});
            skLineSegment(sketch, "E701", {"start": v(49.97, -48.35) * mm, "end": v(49.8, -48.49) * mm});
            skLineSegment(sketch, "E702", {"start": v(49.8, -48.49) * mm, "end": v(49.6, -48.67) * mm});
            skLineSegment(sketch, "E703", {"start": v(49.6, -48.67) * mm, "end": v(49.6, -48.7) * mm});
            skLineSegment(sketch, "E704", {"start": v(49.6, -48.7) * mm, "end": v(49.57, -48.76) * mm});
            skLineSegment(sketch, "E705", {"start": v(49.57, -48.76) * mm, "end": v(49.5, -48.86) * mm});
            skLineSegment(sketch, "E706", {"start": v(49.5, -48.86) * mm, "end": v(49.42, -49.01) * mm});
            skLineSegment(sketch, "E707", {"start": v(49.42, -49.01) * mm, "end": v(49.35, -49.18) * mm});
            skLineSegment(sketch, "E708", {"start": v(49.35, -49.18) * mm, "end": v(49.27, -49.42) * mm});
            skLineSegment(sketch, "E709", {"start": v(49.27, -49.42) * mm, "end": v(49.25, -49.5) * mm});
            skLineSegment(sketch, "E710", {"start": v(49.25, -49.5) * mm, "end": v(49.25, -56.51) * mm});
            skLineSegment(sketch, "E711", {"start": v(43.5, -1) * mm, "end": v(43.5, -30.48) * mm});
            skLineSegment(sketch, "E712", {"start": v(43.5, -30.48) * mm, "end": v(58.5, -30.48) * mm});
            skLineSegment(sketch, "E713", {"start": v(58.5, -30.48) * mm, "end": v(58.5, -1) * mm});
            skLineSegment(sketch, "E714", {"start": v(58.5, -1) * mm, "end": v(43.5, -1) * mm});
            skArc(sketch, "E715", {"start": v(55.51, -6.02) * mm, "mid": v(55.15, -5.13) * mm, "end": v(54.26, -4.77) * mm});
            skArc(sketch, "E716", {"start": v(54.26, -4.77) * mm, "mid": v(53.38, -5.13) * mm, "end": v(53.01, -6.02) * mm});
            skArc(sketch, "E717", {"start": v(53.01, -6.02) * mm, "mid": v(53.38, -6.9) * mm, "end": v(54.26, -7.27) * mm});
            skArc(sketch, "E718", {"start": v(54.26, -7.27) * mm, "mid": v(55.15, -6.9) * mm, "end": v(55.51, -6.02) * mm});
            skArc(sketch, "E719", {"start": v(49.01, -6.02) * mm, "mid": v(48.65, -5.13) * mm, "end": v(47.76, -4.77) * mm});
            skArc(sketch, "E720", {"start": v(47.76, -4.77) * mm, "mid": v(46.88, -5.13) * mm, "end": v(46.51, -6.02) * mm});
            skArc(sketch, "E721", {"start": v(46.51, -6.02) * mm, "mid": v(46.88, -6.9) * mm, "end": v(47.76, -7.27) * mm});
            skArc(sketch, "E722", {"start": v(47.76, -7.27) * mm, "mid": v(48.65, -6.9) * mm, "end": v(49.01, -6.02) * mm});
            skArc(sketch, "E723", {"start": v(56.76, -6.02) * mm, "mid": v(56.03, -4.25) * mm, "end": v(54.26, -3.52) * mm});
            skArc(sketch, "E724", {"start": v(54.26, -3.52) * mm, "mid": v(52.5, -4.25) * mm, "end": v(51.76, -6.02) * mm});
            skArc(sketch, "E725", {"start": v(51.76, -6.02) * mm, "mid": v(52.5, -7.79) * mm, "end": v(54.26, -8.52) * mm});
            skArc(sketch, "E726", {"start": v(54.26, -8.52) * mm, "mid": v(56.03, -7.79) * mm, "end": v(56.76, -6.02) * mm});
            skArc(sketch, "E727", {"start": v(50.26, -6.02) * mm, "mid": v(49.53, -4.25) * mm, "end": v(47.76, -3.52) * mm});
            skArc(sketch, "E728", {"start": v(47.76, -3.52) * mm, "mid": v(46, -4.25) * mm, "end": v(45.26, -6.02) * mm});
            skArc(sketch, "E729", {"start": v(45.26, -6.02) * mm, "mid": v(46, -7.79) * mm, "end": v(47.76, -8.52) * mm});
            skArc(sketch, "E730", {"start": v(47.76, -8.52) * mm, "mid": v(49.53, -7.79) * mm, "end": v(50.26, -6.02) * mm});
            skLineSegment(sketch, "E731", {"start": v(49.5, -32.48) * mm, "end": v(52.5, -32.48) * mm});
            skLineSegment(sketch, "E732", {"start": v(52.5, -32.48) * mm, "end": v(52.5, -30.48) * mm});
            skLineSegment(sketch, "E733", {"start": v(52.5, -30.48) * mm, "end": v(49.5, -30.48) * mm});
            skLineSegment(sketch, "E734", {"start": v(49.5, -30.48) * mm, "end": v(49.5, -32.48) * mm});
            skLineSegment(sketch, "E735", {"start": v(41.5, -14.24) * mm, "end": v(41.5, -17.24) * mm});
            skLineSegment(sketch, "E736", {"start": v(41.5, -17.24) * mm, "end": v(43.5, -17.24) * mm});
            skLineSegment(sketch, "E737", {"start": v(43.5, -17.24) * mm, "end": v(43.5, -14.24) * mm});
            skLineSegment(sketch, "E738", {"start": v(43.5, -14.24) * mm, "end": v(41.5, -14.24) * mm});
            skLineSegment(sketch, "E739", {"start": v(49.25, -25.03) * mm, "end": v(49.27, -25.09) * mm});
            skLineSegment(sketch, "E740", {"start": v(49.27, -25.09) * mm, "end": v(49.35, -25.33) * mm});
            skLineSegment(sketch, "E741", {"start": v(49.35, -25.33) * mm, "end": v(49.4, -25.47) * mm});
            skLineSegment(sketch, "E742", {"start": v(49.4, -25.47) * mm, "end": v(49.44, -25.56) * mm});
            skLineSegment(sketch, "E743", {"start": v(49.44, -25.56) * mm, "end": v(49.5, -25.64) * mm});
            skLineSegment(sketch, "E744", {"start": v(49.5, -25.64) * mm, "end": v(49.57, -25.74) * mm});
            skLineSegment(sketch, "E745", {"start": v(49.57, -25.74) * mm, "end": v(49.6, -25.78) * mm});
            skLineSegment(sketch, "E746", {"start": v(49.6, -25.78) * mm, "end": v(49.6, -25.81) * mm});
            skLineSegment(sketch, "E747", {"start": v(49.6, -25.81) * mm, "end": v(49.64, -25.86) * mm});
            skLineSegment(sketch, "E748", {"start": v(49.64, -25.86) * mm, "end": v(49.73, -25.95) * mm});
            skLineSegment(sketch, "E749", {"start": v(49.73, -25.95) * mm, "end": v(49.92, -26.14) * mm});
            skLineSegment(sketch, "E750", {"start": v(49.92, -26.14) * mm, "end": v(49.97, -26.18) * mm});
            skLineSegment(sketch, "E751", {"start": v(49.97, -26.18) * mm, "end": v(50.02, -26.2) * mm});
            skLineSegment(sketch, "E752", {"start": v(50.02, -26.2) * mm, "end": v(50.04, -26.2) * mm});
            skLineSegment(sketch, "E753", {"start": v(50.04, -26.2) * mm, "end": v(50.05, -26.22) * mm});
            skLineSegment(sketch, "E754", {"start": v(50.05, -26.22) * mm, "end": v(50.08, -26.25) * mm});
            skLineSegment(sketch, "E755", {"start": v(50.08, -26.25) * mm, "end": v(50.14, -26.28) * mm});
            skLineSegment(sketch, "E756", {"start": v(50.14, -26.28) * mm, "end": v(50.42, -26.4) * mm});
            skLineSegment(sketch, "E757", {"start": v(50.42, -26.4) * mm, "end": v(50.54, -26.45) * mm});
            skLineSegment(sketch, "E758", {"start": v(50.54, -26.45) * mm, "end": v(50.68, -26.48) * mm});
            skLineSegment(sketch, "E759", {"start": v(50.68, -26.48) * mm, "end": v(50.84, -26.5) * mm});
            skLineSegment(sketch, "E760", {"start": v(50.84, -26.5) * mm, "end": v(51, -26.5) * mm});
            skLineSegment(sketch, "E761", {"start": v(51, -26.5) * mm, "end": v(51.17, -26.5) * mm});
            skLineSegment(sketch, "E762", {"start": v(51.17, -26.5) * mm, "end": v(51.33, -26.49) * mm});
            skLineSegment(sketch, "E763", {"start": v(51.33, -26.49) * mm, "end": v(51.48, -26.45) * mm});
            skLineSegment(sketch, "E764", {"start": v(51.48, -26.45) * mm, "end": v(51.6, -26.41) * mm});
            skLineSegment(sketch, "E765", {"start": v(51.6, -26.41) * mm, "end": v(51.9, -26.29) * mm});
            skLineSegment(sketch, "E766", {"start": v(51.9, -26.29) * mm, "end": v(51.96, -26.25) * mm});
            skLineSegment(sketch, "E767", {"start": v(51.96, -26.25) * mm, "end": v(51.98, -26.22) * mm});
            skLineSegment(sketch, "E768", {"start": v(51.98, -26.22) * mm, "end": v(51.99, -26.2) * mm});
            skLineSegment(sketch, "E769", {"start": v(51.99, -26.2) * mm, "end": v(52, -26.2) * mm});
            skLineSegment(sketch, "E770", {"start": v(52, -26.2) * mm, "end": v(52.04, -26.19) * mm});
            skLineSegment(sketch, "E771", {"start": v(52.04, -26.19) * mm, "end": v(52.1, -26.15) * mm});
            skLineSegment(sketch, "E772", {"start": v(52.1, -26.15) * mm, "end": v(52.24, -26.02) * mm});
            skLineSegment(sketch, "E773", {"start": v(52.24, -26.02) * mm, "end": v(52.37, -25.9) * mm});
            skLineSegment(sketch, "E774", {"start": v(52.37, -25.9) * mm, "end": v(52.4, -25.84) * mm});
            skLineSegment(sketch, "E775", {"start": v(52.4, -25.84) * mm, "end": v(52.43, -25.81) * mm});
            skLineSegment(sketch, "E776", {"start": v(52.43, -25.81) * mm, "end": v(52.44, -25.78) * mm});
            skLineSegment(sketch, "E777", {"start": v(52.44, -25.78) * mm, "end": v(52.46, -25.74) * mm});
            skLineSegment(sketch, "E778", {"start": v(52.46, -25.74) * mm, "end": v(52.53, -25.66) * mm});
            skLineSegment(sketch, "E779", {"start": v(52.53, -25.66) * mm, "end": v(52.57, -25.6) * mm});
            skLineSegment(sketch, "E780", {"start": v(52.57, -25.6) * mm, "end": v(52.61, -25.5) * mm});
            skLineSegment(sketch, "E781", {"start": v(52.61, -25.5) * mm, "end": v(52.75, -25.1) * mm});
            skLineSegment(sketch, "E782", {"start": v(52.75, -25.1) * mm, "end": v(52.78, -25) * mm});
            skLineSegment(sketch, "E783", {"start": v(52.78, -25) * mm, "end": v(52.78, -18) * mm});
            skLineSegment(sketch, "E784", {"start": v(52.78, -18) * mm, "end": v(52.76, -17.94) * mm});
            skLineSegment(sketch, "E785", {"start": v(52.76, -17.94) * mm, "end": v(52.67, -17.7) * mm});
            skLineSegment(sketch, "E786", {"start": v(52.67, -17.7) * mm, "end": v(52.6, -17.53) * mm});
            skLineSegment(sketch, "E787", {"start": v(52.6, -17.53) * mm, "end": v(52.52, -17.38) * mm});
            skLineSegment(sketch, "E788", {"start": v(52.52, -17.38) * mm, "end": v(52.45, -17.27) * mm});
            skLineSegment(sketch, "E789", {"start": v(52.45, -17.27) * mm, "end": v(52.43, -17.22) * mm});
            skLineSegment(sketch, "E790", {"start": v(52.43, -17.22) * mm, "end": v(52.4, -17.18) * mm});
            skLineSegment(sketch, "E791", {"start": v(52.4, -17.18) * mm, "end": v(52.32, -17.1) * mm});
            skLineSegment(sketch, "E792", {"start": v(52.32, -17.1) * mm, "end": v(52.07, -16.87) * mm});
            skLineSegment(sketch, "E793", {"start": v(52.07, -16.87) * mm, "end": v(51.95, -16.79) * mm});
            skLineSegment(sketch, "E794", {"start": v(51.95, -16.79) * mm, "end": v(51.8, -16.7) * mm});
            skLineSegment(sketch, "E795", {"start": v(51.8, -16.7) * mm, "end": v(51.63, -16.63) * mm});
            skLineSegment(sketch, "E796", {"start": v(51.63, -16.63) * mm, "end": v(51.47, -16.58) * mm});
            skLineSegment(sketch, "E797", {"start": v(51.47, -16.58) * mm, "end": v(51.4, -16.56) * mm});
            skLineSegment(sketch, "E798", {"start": v(51.4, -16.56) * mm, "end": v(51.28, -16.55) * mm});
            skLineSegment(sketch, "E799", {"start": v(51.28, -16.55) * mm, "end": v(51.01, -16.54) * mm});
            skLineSegment(sketch, "E800", {"start": v(51.01, -16.54) * mm, "end": v(50.75, -16.55) * mm});
            skLineSegment(sketch, "E801", {"start": v(50.75, -16.55) * mm, "end": v(50.64, -16.56) * mm});
            skLineSegment(sketch, "E802", {"start": v(50.64, -16.56) * mm, "end": v(50.55, -16.58) * mm});
            skLineSegment(sketch, "E803", {"start": v(50.55, -16.58) * mm, "end": v(50.36, -16.65) * mm});
            skLineSegment(sketch, "E804", {"start": v(50.36, -16.65) * mm, "end": v(50.16, -16.74) * mm});
            skLineSegment(sketch, "E805", {"start": v(50.16, -16.74) * mm, "end": v(49.97, -16.87) * mm});
            skLineSegment(sketch, "E806", {"start": v(49.97, -16.87) * mm, "end": v(49.8, -17) * mm});
            skLineSegment(sketch, "E807", {"start": v(49.8, -17) * mm, "end": v(49.6, -17.19) * mm});
            skLineSegment(sketch, "E808", {"start": v(49.6, -17.19) * mm, "end": v(49.6, -17.21) * mm});
            skLineSegment(sketch, "E809", {"start": v(49.6, -17.21) * mm, "end": v(49.57, -17.27) * mm});
            skLineSegment(sketch, "E810", {"start": v(49.57, -17.27) * mm, "end": v(49.5, -17.38) * mm});
            skLineSegment(sketch, "E811", {"start": v(49.5, -17.38) * mm, "end": v(49.42, -17.53) * mm});
            skLineSegment(sketch, "E812", {"start": v(49.42, -17.53) * mm, "end": v(49.35, -17.7) * mm});
            skLineSegment(sketch, "E813", {"start": v(49.35, -17.7) * mm, "end": v(49.27, -17.94) * mm});
            skLineSegment(sketch, "E814", {"start": v(49.27, -17.94) * mm, "end": v(49.25, -18) * mm});
            skLineSegment(sketch, "E815", {"start": v(49.25, -18) * mm, "end": v(49.25, -25.03) * mm});
            skLineSegment(sketch, "E816", {"start": v(49.5, -1) * mm, "end": v(52.5, -1) * mm});
            skLineSegment(sketch, "E817", {"start": v(52.5, -1) * mm, "end": v(52.5, 1) * mm});
            skLineSegment(sketch, "E818", {"start": v(52.5, 1) * mm, "end": v(49.5, 1) * mm});
            skLineSegment(sketch, "E819", {"start": v(49.5, 1) * mm, "end": v(49.5, -1) * mm});
            skLineSegment(sketch, "E820", {"start": v(26.5, -1) * mm, "end": v(26.5, -30.48) * mm});
            skLineSegment(sketch, "E821", {"start": v(26.5, -30.48) * mm, "end": v(41.5, -30.48) * mm});
            skLineSegment(sketch, "E822", {"start": v(41.5, -30.48) * mm, "end": v(41.5, -1) * mm});
            skLineSegment(sketch, "E823", {"start": v(41.5, -1) * mm, "end": v(26.5, -1) * mm});
            skArc(sketch, "E824", {"start": v(38.51, -6.02) * mm, "mid": v(38.15, -5.13) * mm, "end": v(37.26, -4.77) * mm});
            skArc(sketch, "E825", {"start": v(37.26, -4.77) * mm, "mid": v(36.38, -5.13) * mm, "end": v(36.01, -6.02) * mm});
            skArc(sketch, "E826", {"start": v(36.01, -6.02) * mm, "mid": v(36.38, -6.9) * mm, "end": v(37.26, -7.27) * mm});
            skArc(sketch, "E827", {"start": v(37.26, -7.27) * mm, "mid": v(38.15, -6.9) * mm, "end": v(38.51, -6.02) * mm});
            skArc(sketch, "E828", {"start": v(32.01, -6.02) * mm, "mid": v(31.65, -5.13) * mm, "end": v(30.76, -4.77) * mm});
            skArc(sketch, "E829", {"start": v(30.76, -4.77) * mm, "mid": v(29.88, -5.13) * mm, "end": v(29.51, -6.02) * mm});
            skArc(sketch, "E830", {"start": v(29.51, -6.02) * mm, "mid": v(29.88, -6.9) * mm, "end": v(30.76, -7.27) * mm});
            skArc(sketch, "E831", {"start": v(30.76, -7.27) * mm, "mid": v(31.65, -6.9) * mm, "end": v(32.01, -6.02) * mm});
            skArc(sketch, "E832", {"start": v(39.76, -6.02) * mm, "mid": v(39.03, -4.25) * mm, "end": v(37.26, -3.52) * mm});
            skArc(sketch, "E833", {"start": v(37.26, -3.52) * mm, "mid": v(35.5, -4.25) * mm, "end": v(34.76, -6.02) * mm});
            skArc(sketch, "E834", {"start": v(34.76, -6.02) * mm, "mid": v(35.5, -7.79) * mm, "end": v(37.26, -8.52) * mm});
            skArc(sketch, "E835", {"start": v(37.26, -8.52) * mm, "mid": v(39.03, -7.79) * mm, "end": v(39.76, -6.02) * mm});
            skArc(sketch, "E836", {"start": v(33.26, -6.02) * mm, "mid": v(32.53, -4.25) * mm, "end": v(30.76, -3.52) * mm});
            skArc(sketch, "E837", {"start": v(30.76, -3.52) * mm, "mid": v(29, -4.25) * mm, "end": v(28.26, -6.02) * mm});
            skArc(sketch, "E838", {"start": v(28.26, -6.02) * mm, "mid": v(29, -7.79) * mm, "end": v(30.76, -8.52) * mm});
            skArc(sketch, "E839", {"start": v(30.76, -8.52) * mm, "mid": v(32.53, -7.79) * mm, "end": v(33.26, -6.02) * mm});
            skLineSegment(sketch, "E840", {"start": v(32.5, -32.48) * mm, "end": v(35.5, -32.48) * mm});
            skLineSegment(sketch, "E841", {"start": v(35.5, -32.48) * mm, "end": v(35.5, -30.48) * mm});
            skLineSegment(sketch, "E842", {"start": v(35.5, -30.48) * mm, "end": v(32.5, -30.48) * mm});
            skLineSegment(sketch, "E843", {"start": v(32.5, -30.48) * mm, "end": v(32.5, -32.48) * mm});
            skLineSegment(sketch, "E844", {"start": v(24.5, -14.24) * mm, "end": v(24.5, -17.24) * mm});
            skLineSegment(sketch, "E845", {"start": v(24.5, -17.24) * mm, "end": v(26.5, -17.24) * mm});
            skLineSegment(sketch, "E846", {"start": v(26.5, -17.24) * mm, "end": v(26.5, -14.24) * mm});
            skLineSegment(sketch, "E847", {"start": v(26.5, -14.24) * mm, "end": v(24.5, -14.24) * mm});
            skLineSegment(sketch, "E848", {"start": v(32.25, -25.03) * mm, "end": v(32.27, -25.09) * mm});
            skLineSegment(sketch, "E849", {"start": v(32.27, -25.09) * mm, "end": v(32.35, -25.33) * mm});
            skLineSegment(sketch, "E850", {"start": v(32.35, -25.33) * mm, "end": v(32.4, -25.47) * mm});
            skLineSegment(sketch, "E851", {"start": v(32.4, -25.47) * mm, "end": v(32.44, -25.56) * mm});
            skLineSegment(sketch, "E852", {"start": v(32.44, -25.56) * mm, "end": v(32.5, -25.64) * mm});
            skLineSegment(sketch, "E853", {"start": v(32.5, -25.64) * mm, "end": v(32.57, -25.74) * mm});
            skLineSegment(sketch, "E854", {"start": v(32.57, -25.74) * mm, "end": v(32.6, -25.78) * mm});
            skLineSegment(sketch, "E855", {"start": v(32.6, -25.78) * mm, "end": v(32.6, -25.81) * mm});
            skLineSegment(sketch, "E856", {"start": v(32.6, -25.81) * mm, "end": v(32.64, -25.86) * mm});
            skLineSegment(sketch, "E857", {"start": v(32.64, -25.86) * mm, "end": v(32.73, -25.95) * mm});
            skLineSegment(sketch, "E858", {"start": v(32.73, -25.95) * mm, "end": v(32.92, -26.14) * mm});
            skLineSegment(sketch, "E859", {"start": v(32.92, -26.14) * mm, "end": v(32.97, -26.18) * mm});
            skLineSegment(sketch, "E860", {"start": v(32.97, -26.18) * mm, "end": v(33.02, -26.2) * mm});
            skLineSegment(sketch, "E861", {"start": v(33.02, -26.2) * mm, "end": v(33.04, -26.2) * mm});
            skLineSegment(sketch, "E862", {"start": v(33.04, -26.2) * mm, "end": v(33.05, -26.22) * mm});
            skLineSegment(sketch, "E863", {"start": v(33.05, -26.22) * mm, "end": v(33.08, -26.25) * mm});
            skLineSegment(sketch, "E864", {"start": v(33.08, -26.25) * mm, "end": v(33.14, -26.28) * mm});
            skLineSegment(sketch, "E865", {"start": v(33.14, -26.28) * mm, "end": v(33.42, -26.4) * mm});
            skLineSegment(sketch, "E866", {"start": v(33.42, -26.4) * mm, "end": v(33.54, -26.45) * mm});
            skLineSegment(sketch, "E867", {"start": v(33.54, -26.45) * mm, "end": v(33.68, -26.48) * mm});
            skLineSegment(sketch, "E868", {"start": v(33.68, -26.48) * mm, "end": v(33.84, -26.5) * mm});
            skLineSegment(sketch, "E869", {"start": v(33.84, -26.5) * mm, "end": v(34, -26.5) * mm});
            skLineSegment(sketch, "E870", {"start": v(34, -26.5) * mm, "end": v(34.17, -26.5) * mm});
            skLineSegment(sketch, "E871", {"start": v(34.17, -26.5) * mm, "end": v(34.33, -26.49) * mm});
            skLineSegment(sketch, "E872", {"start": v(34.33, -26.49) * mm, "end": v(34.48, -26.45) * mm});
            skLineSegment(sketch, "E873", {"start": v(34.48, -26.45) * mm, "end": v(34.6, -26.41) * mm});
            skLineSegment(sketch, "E874", {"start": v(34.6, -26.41) * mm, "end": v(34.9, -26.29) * mm});
            skLineSegment(sketch, "E875", {"start": v(34.9, -26.29) * mm, "end": v(34.96, -26.25) * mm});
            skLineSegment(sketch, "E876", {"start": v(34.96, -26.25) * mm, "end": v(34.98, -26.22) * mm});
            skLineSegment(sketch, "E877", {"start": v(34.98, -26.22) * mm, "end": v(34.99, -26.2) * mm});
            skLineSegment(sketch, "E878", {"start": v(34.99, -26.2) * mm, "end": v(35, -26.2) * mm});
            skLineSegment(sketch, "E879", {"start": v(35, -26.2) * mm, "end": v(35.04, -26.19) * mm});
            skLineSegment(sketch, "E880", {"start": v(35.04, -26.19) * mm, "end": v(35.1, -26.15) * mm});
            skLineSegment(sketch, "E881", {"start": v(35.1, -26.15) * mm, "end": v(35.24, -26.02) * mm});
            skLineSegment(sketch, "E882", {"start": v(35.24, -26.02) * mm, "end": v(35.37, -25.9) * mm});
            skLineSegment(sketch, "E883", {"start": v(35.37, -25.9) * mm, "end": v(35.4, -25.84) * mm});
            skLineSegment(sketch, "E884", {"start": v(35.4, -25.84) * mm, "end": v(35.43, -25.81) * mm});
            skLineSegment(sketch, "E885", {"start": v(35.43, -25.81) * mm, "end": v(35.44, -25.78) * mm});
            skLineSegment(sketch, "E886", {"start": v(35.44, -25.78) * mm, "end": v(35.46, -25.74) * mm});
            skLineSegment(sketch, "E887", {"start": v(35.46, -25.74) * mm, "end": v(35.53, -25.66) * mm});
            skLineSegment(sketch, "E888", {"start": v(35.53, -25.66) * mm, "end": v(35.57, -25.6) * mm});
            skLineSegment(sketch, "E889", {"start": v(35.57, -25.6) * mm, "end": v(35.61, -25.5) * mm});
            skLineSegment(sketch, "E890", {"start": v(35.61, -25.5) * mm, "end": v(35.75, -25.1) * mm});
            skLineSegment(sketch, "E891", {"start": v(35.75, -25.1) * mm, "end": v(35.78, -25) * mm});
            skLineSegment(sketch, "E892", {"start": v(35.78, -25) * mm, "end": v(35.78, -18) * mm});
            skLineSegment(sketch, "E893", {"start": v(35.78, -18) * mm, "end": v(35.76, -17.94) * mm});
            skLineSegment(sketch, "E894", {"start": v(35.76, -17.94) * mm, "end": v(35.67, -17.7) * mm});
            skLineSegment(sketch, "E895", {"start": v(35.67, -17.7) * mm, "end": v(35.6, -17.53) * mm});
            skLineSegment(sketch, "E896", {"start": v(35.6, -17.53) * mm, "end": v(35.52, -17.38) * mm});
            skLineSegment(sketch, "E897", {"start": v(35.52, -17.38) * mm, "end": v(35.45, -17.27) * mm});
            skLineSegment(sketch, "E898", {"start": v(35.45, -17.27) * mm, "end": v(35.43, -17.22) * mm});
            skLineSegment(sketch, "E899", {"start": v(35.43, -17.22) * mm, "end": v(35.4, -17.18) * mm});
            skLineSegment(sketch, "E900", {"start": v(35.4, -17.18) * mm, "end": v(35.32, -17.1) * mm});
            skLineSegment(sketch, "E901", {"start": v(35.32, -17.1) * mm, "end": v(35.07, -16.87) * mm});
            skLineSegment(sketch, "E902", {"start": v(35.07, -16.87) * mm, "end": v(34.95, -16.79) * mm});
            skLineSegment(sketch, "E903", {"start": v(34.95, -16.79) * mm, "end": v(34.8, -16.7) * mm});
            skLineSegment(sketch, "E904", {"start": v(34.8, -16.7) * mm, "end": v(34.63, -16.63) * mm});
            skLineSegment(sketch, "E905", {"start": v(34.63, -16.63) * mm, "end": v(34.47, -16.58) * mm});
            skLineSegment(sketch, "E906", {"start": v(34.47, -16.58) * mm, "end": v(34.4, -16.56) * mm});
            skLineSegment(sketch, "E907", {"start": v(34.4, -16.56) * mm, "end": v(34.28, -16.55) * mm});
            skLineSegment(sketch, "E908", {"start": v(34.28, -16.55) * mm, "end": v(34.01, -16.54) * mm});
            skLineSegment(sketch, "E909", {"start": v(34.01, -16.54) * mm, "end": v(33.75, -16.55) * mm});
            skLineSegment(sketch, "E910", {"start": v(33.75, -16.55) * mm, "end": v(33.64, -16.56) * mm});
            skLineSegment(sketch, "E911", {"start": v(33.64, -16.56) * mm, "end": v(33.55, -16.58) * mm});
            skLineSegment(sketch, "E912", {"start": v(33.55, -16.58) * mm, "end": v(33.36, -16.65) * mm});
            skLineSegment(sketch, "E913", {"start": v(33.36, -16.65) * mm, "end": v(33.16, -16.74) * mm});
            skLineSegment(sketch, "E914", {"start": v(33.16, -16.74) * mm, "end": v(32.97, -16.87) * mm});
            skLineSegment(sketch, "E915", {"start": v(32.97, -16.87) * mm, "end": v(32.8, -17) * mm});
            skLineSegment(sketch, "E916", {"start": v(32.8, -17) * mm, "end": v(32.6, -17.19) * mm});
            skLineSegment(sketch, "E917", {"start": v(32.6, -17.19) * mm, "end": v(32.6, -17.21) * mm});
            skLineSegment(sketch, "E918", {"start": v(32.6, -17.21) * mm, "end": v(32.57, -17.27) * mm});
            skLineSegment(sketch, "E919", {"start": v(32.57, -17.27) * mm, "end": v(32.5, -17.38) * mm});
            skLineSegment(sketch, "E920", {"start": v(32.5, -17.38) * mm, "end": v(32.42, -17.53) * mm});
            skLineSegment(sketch, "E921", {"start": v(32.42, -17.53) * mm, "end": v(32.35, -17.7) * mm});
            skLineSegment(sketch, "E922", {"start": v(32.35, -17.7) * mm, "end": v(32.27, -17.94) * mm});
            skLineSegment(sketch, "E923", {"start": v(32.27, -17.94) * mm, "end": v(32.25, -18) * mm});
            skLineSegment(sketch, "E924", {"start": v(32.25, -18) * mm, "end": v(32.25, -25.03) * mm});
            skLineSegment(sketch, "E925", {"start": v(9.5, -1) * mm, "end": v(9.5, -30.48) * mm});
            skLineSegment(sketch, "E926", {"start": v(9.5, -30.48) * mm, "end": v(24.5, -30.48) * mm});
            skLineSegment(sketch, "E927", {"start": v(24.5, -30.48) * mm, "end": v(24.5, -1) * mm});
            skLineSegment(sketch, "E928", {"start": v(24.5, -1) * mm, "end": v(9.5, -1) * mm});
            skArc(sketch, "E929", {"start": v(21.51, -6.02) * mm, "mid": v(21.15, -5.13) * mm, "end": v(20.26, -4.77) * mm});
            skArc(sketch, "E930", {"start": v(20.26, -4.77) * mm, "mid": v(19.38, -5.13) * mm, "end": v(19.01, -6.02) * mm});
            skArc(sketch, "E931", {"start": v(19.01, -6.02) * mm, "mid": v(19.38, -6.9) * mm, "end": v(20.26, -7.27) * mm});
            skArc(sketch, "E932", {"start": v(20.26, -7.27) * mm, "mid": v(21.15, -6.9) * mm, "end": v(21.51, -6.02) * mm});
            skArc(sketch, "E933", {"start": v(15.01, -6.02) * mm, "mid": v(14.65, -5.13) * mm, "end": v(13.76, -4.77) * mm});
            skArc(sketch, "E934", {"start": v(13.76, -4.77) * mm, "mid": v(12.88, -5.13) * mm, "end": v(12.51, -6.02) * mm});
            skArc(sketch, "E935", {"start": v(12.51, -6.02) * mm, "mid": v(12.88, -6.9) * mm, "end": v(13.76, -7.27) * mm});
            skArc(sketch, "E936", {"start": v(13.76, -7.27) * mm, "mid": v(14.65, -6.9) * mm, "end": v(15.01, -6.02) * mm});
            skArc(sketch, "E937", {"start": v(22.76, -6.02) * mm, "mid": v(22.03, -4.25) * mm, "end": v(20.26, -3.52) * mm});
            skArc(sketch, "E938", {"start": v(20.26, -3.52) * mm, "mid": v(18.5, -4.25) * mm, "end": v(17.76, -6.02) * mm});
            skArc(sketch, "E939", {"start": v(17.76, -6.02) * mm, "mid": v(18.5, -7.79) * mm, "end": v(20.26, -8.52) * mm});
            skArc(sketch, "E940", {"start": v(20.26, -8.52) * mm, "mid": v(22.03, -7.79) * mm, "end": v(22.76, -6.02) * mm});
            skArc(sketch, "E941", {"start": v(16.26, -6.02) * mm, "mid": v(15.53, -4.25) * mm, "end": v(13.76, -3.52) * mm});
            skArc(sketch, "E942", {"start": v(13.76, -3.52) * mm, "mid": v(12, -4.25) * mm, "end": v(11.26, -6.02) * mm});
            skArc(sketch, "E943", {"start": v(11.26, -6.02) * mm, "mid": v(12, -7.79) * mm, "end": v(13.76, -8.52) * mm});
            skArc(sketch, "E944", {"start": v(13.76, -8.52) * mm, "mid": v(15.53, -7.79) * mm, "end": v(16.26, -6.02) * mm});
            skLineSegment(sketch, "E945", {"start": v(15.5, -32.48) * mm, "end": v(18.5, -32.48) * mm});
            skLineSegment(sketch, "E946", {"start": v(18.5, -32.48) * mm, "end": v(18.5, -30.48) * mm});
            skLineSegment(sketch, "E947", {"start": v(18.5, -30.48) * mm, "end": v(15.5, -30.48) * mm});
            skLineSegment(sketch, "E948", {"start": v(15.5, -30.48) * mm, "end": v(15.5, -32.48) * mm});
            skLineSegment(sketch, "E949", {"start": v(15.25, -25.03) * mm, "end": v(15.27, -25.09) * mm});
            skLineSegment(sketch, "E950", {"start": v(15.27, -25.09) * mm, "end": v(15.35, -25.33) * mm});
            skLineSegment(sketch, "E951", {"start": v(15.35, -25.33) * mm, "end": v(15.4, -25.47) * mm});
            skLineSegment(sketch, "E952", {"start": v(15.4, -25.47) * mm, "end": v(15.44, -25.56) * mm});
            skLineSegment(sketch, "E953", {"start": v(15.44, -25.56) * mm, "end": v(15.5, -25.64) * mm});
            skLineSegment(sketch, "E954", {"start": v(15.5, -25.64) * mm, "end": v(15.57, -25.74) * mm});
            skLineSegment(sketch, "E955", {"start": v(15.57, -25.74) * mm, "end": v(15.6, -25.78) * mm});
            skLineSegment(sketch, "E956", {"start": v(15.6, -25.78) * mm, "end": v(15.6, -25.81) * mm});
            skLineSegment(sketch, "E957", {"start": v(15.6, -25.81) * mm, "end": v(15.64, -25.86) * mm});
            skLineSegment(sketch, "E958", {"start": v(15.64, -25.86) * mm, "end": v(15.73, -25.95) * mm});
            skLineSegment(sketch, "E959", {"start": v(15.73, -25.95) * mm, "end": v(15.92, -26.14) * mm});
            skLineSegment(sketch, "E960", {"start": v(15.92, -26.14) * mm, "end": v(15.97, -26.18) * mm});
            skLineSegment(sketch, "E961", {"start": v(15.97, -26.18) * mm, "end": v(16.02, -26.2) * mm});
            skLineSegment(sketch, "E962", {"start": v(16.02, -26.2) * mm, "end": v(16.04, -26.2) * mm});
            skLineSegment(sketch, "E963", {"start": v(16.04, -26.2) * mm, "end": v(16.05, -26.22) * mm});
            skLineSegment(sketch, "E964", {"start": v(16.05, -26.22) * mm, "end": v(16.08, -26.25) * mm});
            skLineSegment(sketch, "E965", {"start": v(16.08, -26.25) * mm, "end": v(16.14, -26.28) * mm});
            skLineSegment(sketch, "E966", {"start": v(16.14, -26.28) * mm, "end": v(16.42, -26.4) * mm});
            skLineSegment(sketch, "E967", {"start": v(16.42, -26.4) * mm, "end": v(16.54, -26.45) * mm});
            skLineSegment(sketch, "E968", {"start": v(16.54, -26.45) * mm, "end": v(16.68, -26.48) * mm});
            skLineSegment(sketch, "E969", {"start": v(16.68, -26.48) * mm, "end": v(16.84, -26.5) * mm});
            skLineSegment(sketch, "E970", {"start": v(16.84, -26.5) * mm, "end": v(17, -26.5) * mm});
            skLineSegment(sketch, "E971", {"start": v(17, -26.5) * mm, "end": v(17.17, -26.5) * mm});
            skLineSegment(sketch, "E972", {"start": v(17.17, -26.5) * mm, "end": v(17.33, -26.49) * mm});
            skLineSegment(sketch, "E973", {"start": v(17.33, -26.49) * mm, "end": v(17.48, -26.45) * mm});
            skLineSegment(sketch, "E974", {"start": v(17.48, -26.45) * mm, "end": v(17.6, -26.41) * mm});
            skLineSegment(sketch, "E975", {"start": v(17.6, -26.41) * mm, "end": v(17.9, -26.29) * mm});
            skLineSegment(sketch, "E976", {"start": v(17.9, -26.29) * mm, "end": v(17.96, -26.25) * mm});
            skLineSegment(sketch, "E977", {"start": v(17.96, -26.25) * mm, "end": v(17.98, -26.22) * mm});
            skLineSegment(sketch, "E978", {"start": v(17.98, -26.22) * mm, "end": v(17.99, -26.2) * mm});
            skLineSegment(sketch, "E979", {"start": v(17.99, -26.2) * mm, "end": v(18, -26.2) * mm});
            skLineSegment(sketch, "E980", {"start": v(18, -26.2) * mm, "end": v(18.04, -26.19) * mm});
            skLineSegment(sketch, "E981", {"start": v(18.04, -26.19) * mm, "end": v(18.1, -26.15) * mm});
            skLineSegment(sketch, "E982", {"start": v(18.1, -26.15) * mm, "end": v(18.24, -26.02) * mm});
            skLineSegment(sketch, "E983", {"start": v(18.24, -26.02) * mm, "end": v(18.37, -25.9) * mm});
            skLineSegment(sketch, "E984", {"start": v(18.37, -25.9) * mm, "end": v(18.4, -25.84) * mm});
            skLineSegment(sketch, "E985", {"start": v(18.4, -25.84) * mm, "end": v(18.43, -25.81) * mm});
            skLineSegment(sketch, "E986", {"start": v(18.43, -25.81) * mm, "end": v(18.44, -25.78) * mm});
            skLineSegment(sketch, "E987", {"start": v(18.44, -25.78) * mm, "end": v(18.46, -25.74) * mm});
            skLineSegment(sketch, "E988", {"start": v(18.46, -25.74) * mm, "end": v(18.53, -25.66) * mm});
            skLineSegment(sketch, "E989", {"start": v(18.53, -25.66) * mm, "end": v(18.57, -25.6) * mm});
            skLineSegment(sketch, "E990", {"start": v(18.57, -25.6) * mm, "end": v(18.61, -25.5) * mm});
            skLineSegment(sketch, "E991", {"start": v(18.61, -25.5) * mm, "end": v(18.75, -25.1) * mm});
            skLineSegment(sketch, "E992", {"start": v(18.75, -25.1) * mm, "end": v(18.78, -25) * mm});
            skLineSegment(sketch, "E993", {"start": v(18.78, -25) * mm, "end": v(18.78, -18) * mm});
            skLineSegment(sketch, "E994", {"start": v(18.78, -18) * mm, "end": v(18.76, -17.94) * mm});
            skLineSegment(sketch, "E995", {"start": v(18.76, -17.94) * mm, "end": v(18.67, -17.7) * mm});
            skLineSegment(sketch, "E996", {"start": v(18.67, -17.7) * mm, "end": v(18.6, -17.53) * mm});
            skLineSegment(sketch, "E997", {"start": v(18.6, -17.53) * mm, "end": v(18.52, -17.38) * mm});
            skLineSegment(sketch, "E998", {"start": v(18.52, -17.38) * mm, "end": v(18.45, -17.27) * mm});
            skLineSegment(sketch, "E999", {"start": v(18.45, -17.27) * mm, "end": v(18.43, -17.22) * mm});
            skLineSegment(sketch, "E1000", {"start": v(18.43, -17.22) * mm, "end": v(18.4, -17.18) * mm});
            skLineSegment(sketch, "E1001", {"start": v(18.4, -17.18) * mm, "end": v(18.32, -17.1) * mm});
            skLineSegment(sketch, "E1002", {"start": v(18.32, -17.1) * mm, "end": v(18.07, -16.87) * mm});
            skLineSegment(sketch, "E1003", {"start": v(18.07, -16.87) * mm, "end": v(17.95, -16.79) * mm});
            skLineSegment(sketch, "E1004", {"start": v(17.95, -16.79) * mm, "end": v(17.8, -16.7) * mm});
            skLineSegment(sketch, "E1005", {"start": v(17.8, -16.7) * mm, "end": v(17.63, -16.63) * mm});
            skLineSegment(sketch, "E1006", {"start": v(17.63, -16.63) * mm, "end": v(17.47, -16.58) * mm});
            skLineSegment(sketch, "E1007", {"start": v(17.47, -16.58) * mm, "end": v(17.4, -16.56) * mm});
            skLineSegment(sketch, "E1008", {"start": v(17.4, -16.56) * mm, "end": v(17.28, -16.55) * mm});
            skLineSegment(sketch, "E1009", {"start": v(17.28, -16.55) * mm, "end": v(17.01, -16.54) * mm});
            skLineSegment(sketch, "E1010", {"start": v(17.01, -16.54) * mm, "end": v(16.75, -16.55) * mm});
            skLineSegment(sketch, "E1011", {"start": v(16.75, -16.55) * mm, "end": v(16.64, -16.56) * mm});
            skLineSegment(sketch, "E1012", {"start": v(16.64, -16.56) * mm, "end": v(16.55, -16.58) * mm});
            skLineSegment(sketch, "E1013", {"start": v(16.55, -16.58) * mm, "end": v(16.36, -16.65) * mm});
            skLineSegment(sketch, "E1014", {"start": v(16.36, -16.65) * mm, "end": v(16.16, -16.74) * mm});
            skLineSegment(sketch, "E1015", {"start": v(16.16, -16.74) * mm, "end": v(15.97, -16.87) * mm});
            skLineSegment(sketch, "E1016", {"start": v(15.97, -16.87) * mm, "end": v(15.8, -17) * mm});
            skLineSegment(sketch, "E1017", {"start": v(15.8, -17) * mm, "end": v(15.6, -17.19) * mm});
            skLineSegment(sketch, "E1018", {"start": v(15.6, -17.19) * mm, "end": v(15.6, -17.21) * mm});
            skLineSegment(sketch, "E1019", {"start": v(15.6, -17.21) * mm, "end": v(15.57, -17.27) * mm});
            skLineSegment(sketch, "E1020", {"start": v(15.57, -17.27) * mm, "end": v(15.5, -17.38) * mm});
            skLineSegment(sketch, "E1021", {"start": v(15.5, -17.38) * mm, "end": v(15.42, -17.53) * mm});
            skLineSegment(sketch, "E1022", {"start": v(15.42, -17.53) * mm, "end": v(15.35, -17.7) * mm});
            skLineSegment(sketch, "E1023", {"start": v(15.35, -17.7) * mm, "end": v(15.27, -17.94) * mm});
            skLineSegment(sketch, "E1024", {"start": v(15.27, -17.94) * mm, "end": v(15.25, -18) * mm});
            skLineSegment(sketch, "E1025", {"start": v(15.25, -18) * mm, "end": v(15.25, -25.03) * mm});
            skLineSegment(sketch, "E1026", {"start": v(15.5, -1) * mm, "end": v(18.5, -1) * mm});
            skLineSegment(sketch, "E1027", {"start": v(18.5, -1) * mm, "end": v(18.5, 1) * mm});
            skLineSegment(sketch, "E1028", {"start": v(18.5, 1) * mm, "end": v(15.5, 1) * mm});
            skLineSegment(sketch, "E1029", {"start": v(15.5, 1) * mm, "end": v(15.5, -1) * mm});
            skLineSegment(sketch, "E1030", {"start": v(-7.5, -1) * mm, "end": v(-7.5, -30.48) * mm});
            skLineSegment(sketch, "E1031", {"start": v(-7.5, -30.48) * mm, "end": v(7.5, -30.48) * mm});
            skLineSegment(sketch, "E1032", {"start": v(7.5, -30.48) * mm, "end": v(7.5, -1) * mm});
            skLineSegment(sketch, "E1033", {"start": v(7.5, -1) * mm, "end": v(-7.5, -1) * mm});
            skArc(sketch, "E1034", {"start": v(4.51, -6.02) * mm, "mid": v(4.15, -5.13) * mm, "end": v(3.26, -4.77) * mm});
            skArc(sketch, "E1035", {"start": v(3.26, -4.77) * mm, "mid": v(2.38, -5.13) * mm, "end": v(2.01, -6.02) * mm});
            skArc(sketch, "E1036", {"start": v(2.01, -6.02) * mm, "mid": v(2.38, -6.9) * mm, "end": v(3.26, -7.27) * mm});
            skArc(sketch, "E1037", {"start": v(3.26, -7.27) * mm, "mid": v(4.15, -6.9) * mm, "end": v(4.51, -6.02) * mm});
            skArc(sketch, "E1038", {"start": v(-1.99, -6.02) * mm, "mid": v(-2.35, -5.13) * mm, "end": v(-3.24, -4.77) * mm});
            skArc(sketch, "E1039", {"start": v(-3.24, -4.77) * mm, "mid": v(-4.12, -5.13) * mm, "end": v(-4.49, -6.02) * mm});
            skArc(sketch, "E1040", {"start": v(-4.49, -6.02) * mm, "mid": v(-4.12, -6.9) * mm, "end": v(-3.24, -7.27) * mm});
            skArc(sketch, "E1041", {"start": v(-3.24, -7.27) * mm, "mid": v(-2.35, -6.9) * mm, "end": v(-1.99, -6.02) * mm});
            skArc(sketch, "E1042", {"start": v(5.76, -6.02) * mm, "mid": v(5.03, -4.25) * mm, "end": v(3.26, -3.52) * mm});
            skArc(sketch, "E1043", {"start": v(3.26, -3.52) * mm, "mid": v(1.5, -4.25) * mm, "end": v(0.76, -6.02) * mm});
            skArc(sketch, "E1044", {"start": v(0.76, -6.02) * mm, "mid": v(1.5, -7.79) * mm, "end": v(3.26, -8.52) * mm});
            skArc(sketch, "E1045", {"start": v(3.26, -8.52) * mm, "mid": v(5.03, -7.79) * mm, "end": v(5.76, -6.02) * mm});
            skArc(sketch, "E1046", {"start": v(-0.74, -6.02) * mm, "mid": v(-1.47, -4.25) * mm, "end": v(-3.24, -3.52) * mm});
            skArc(sketch, "E1047", {"start": v(-3.24, -3.52) * mm, "mid": v(-5, -4.25) * mm, "end": v(-5.74, -6.02) * mm});
            skArc(sketch, "E1048", {"start": v(-5.74, -6.02) * mm, "mid": v(-5, -7.79) * mm, "end": v(-3.24, -8.52) * mm});
            skArc(sketch, "E1049", {"start": v(-3.24, -8.52) * mm, "mid": v(-1.47, -7.79) * mm, "end": v(-0.74, -6.02) * mm});
            skLineSegment(sketch, "E1050", {"start": v(-1.5, -32.48) * mm, "end": v(1.5, -32.48) * mm});
            skLineSegment(sketch, "E1051", {"start": v(1.5, -32.48) * mm, "end": v(1.5, -30.48) * mm});
            skLineSegment(sketch, "E1052", {"start": v(1.5, -30.48) * mm, "end": v(-1.5, -30.48) * mm});
            skLineSegment(sketch, "E1053", {"start": v(-1.5, -30.48) * mm, "end": v(-1.5, -32.48) * mm});
            skLineSegment(sketch, "E1054", {"start": v(-9.5, -14.24) * mm, "end": v(-9.5, -17.24) * mm});
            skLineSegment(sketch, "E1055", {"start": v(-9.5, -17.24) * mm, "end": v(-7.5, -17.24) * mm});
            skLineSegment(sketch, "E1056", {"start": v(-7.5, -17.24) * mm, "end": v(-7.5, -14.24) * mm});
            skLineSegment(sketch, "E1057", {"start": v(-7.5, -14.24) * mm, "end": v(-9.5, -14.24) * mm});
            skLineSegment(sketch, "E1058", {"start": v(-1.75, -25.03) * mm, "end": v(-1.73, -25.09) * mm});
            skLineSegment(sketch, "E1059", {"start": v(-1.73, -25.09) * mm, "end": v(-1.65, -25.33) * mm});
            skLineSegment(sketch, "E1060", {"start": v(-1.65, -25.33) * mm, "end": v(-1.6, -25.47) * mm});
            skLineSegment(sketch, "E1061", {"start": v(-1.6, -25.47) * mm, "end": v(-1.56, -25.56) * mm});
            skLineSegment(sketch, "E1062", {"start": v(-1.56, -25.56) * mm, "end": v(-1.5, -25.64) * mm});
            skLineSegment(sketch, "E1063", {"start": v(-1.5, -25.64) * mm, "end": v(-1.43, -25.74) * mm});
            skLineSegment(sketch, "E1064", {"start": v(-1.43, -25.74) * mm, "end": v(-1.4, -25.78) * mm});
            skLineSegment(sketch, "E1065", {"start": v(-1.4, -25.78) * mm, "end": v(-1.4, -25.81) * mm});
            skLineSegment(sketch, "E1066", {"start": v(-1.4, -25.81) * mm, "end": v(-1.36, -25.86) * mm});
            skLineSegment(sketch, "E1067", {"start": v(-1.36, -25.86) * mm, "end": v(-1.27, -25.95) * mm});
            skLineSegment(sketch, "E1068", {"start": v(-1.27, -25.95) * mm, "end": v(-1.08, -26.14) * mm});
            skLineSegment(sketch, "E1069", {"start": v(-1.08, -26.14) * mm, "end": v(-1.03, -26.18) * mm});
            skLineSegment(sketch, "E1070", {"start": v(-1.03, -26.18) * mm, "end": v(-0.98, -26.2) * mm});
            skLineSegment(sketch, "E1071", {"start": v(-0.98, -26.2) * mm, "end": v(-0.96, -26.2) * mm});
            skLineSegment(sketch, "E1072", {"start": v(-0.96, -26.2) * mm, "end": v(-0.95, -26.22) * mm});
            skLineSegment(sketch, "E1073", {"start": v(-0.95, -26.22) * mm, "end": v(-0.92, -26.25) * mm});
            skLineSegment(sketch, "E1074", {"start": v(-0.92, -26.25) * mm, "end": v(-0.86, -26.28) * mm});
            skLineSegment(sketch, "E1075", {"start": v(-0.86, -26.28) * mm, "end": v(-0.58, -26.4) * mm});
            skLineSegment(sketch, "E1076", {"start": v(-0.58, -26.4) * mm, "end": v(-0.46, -26.45) * mm});
            skLineSegment(sketch, "E1077", {"start": v(-0.46, -26.45) * mm, "end": v(-0.32, -26.48) * mm});
            skLineSegment(sketch, "E1078", {"start": v(-0.32, -26.48) * mm, "end": v(-0.16, -26.5) * mm});
            skLineSegment(sketch, "E1079", {"start": v(-0.16, -26.5) * mm, "end": v(0, -26.5) * mm});
            skLineSegment(sketch, "E1080", {"start": v(0, -26.5) * mm, "end": v(0.17, -26.5) * mm});
            skLineSegment(sketch, "E1081", {"start": v(0.17, -26.5) * mm, "end": v(0.33, -26.49) * mm});
            skLineSegment(sketch, "E1082", {"start": v(0.33, -26.49) * mm, "end": v(0.48, -26.45) * mm});
            skLineSegment(sketch, "E1083", {"start": v(0.48, -26.45) * mm, "end": v(0.6, -26.41) * mm});
            skLineSegment(sketch, "E1084", {"start": v(0.6, -26.41) * mm, "end": v(0.9, -26.29) * mm});
            skLineSegment(sketch, "E1085", {"start": v(0.9, -26.29) * mm, "end": v(0.96, -26.25) * mm});
            skLineSegment(sketch, "E1086", {"start": v(0.96, -26.25) * mm, "end": v(0.98, -26.22) * mm});
            skLineSegment(sketch, "E1087", {"start": v(0.98, -26.22) * mm, "end": v(0.99, -26.2) * mm});
            skLineSegment(sketch, "E1088", {"start": v(0.99, -26.2) * mm, "end": v(1, -26.2) * mm});
            skLineSegment(sketch, "E1089", {"start": v(1, -26.2) * mm, "end": v(1.04, -26.19) * mm});
            skLineSegment(sketch, "E1090", {"start": v(1.04, -26.19) * mm, "end": v(1.1, -26.15) * mm});
            skLineSegment(sketch, "E1091", {"start": v(1.1, -26.15) * mm, "end": v(1.24, -26.02) * mm});
            skLineSegment(sketch, "E1092", {"start": v(1.24, -26.02) * mm, "end": v(1.37, -25.9) * mm});
            skLineSegment(sketch, "E1093", {"start": v(1.37, -25.9) * mm, "end": v(1.4, -25.84) * mm});
            skLineSegment(sketch, "E1094", {"start": v(1.4, -25.84) * mm, "end": v(1.43, -25.81) * mm});
            skLineSegment(sketch, "E1095", {"start": v(1.43, -25.81) * mm, "end": v(1.44, -25.78) * mm});
            skLineSegment(sketch, "E1096", {"start": v(1.44, -25.78) * mm, "end": v(1.46, -25.74) * mm});
            skLineSegment(sketch, "E1097", {"start": v(1.46, -25.74) * mm, "end": v(1.53, -25.66) * mm});
            skLineSegment(sketch, "E1098", {"start": v(1.53, -25.66) * mm, "end": v(1.57, -25.6) * mm});
            skLineSegment(sketch, "E1099", {"start": v(1.57, -25.6) * mm, "end": v(1.61, -25.5) * mm});
            skLineSegment(sketch, "E1100", {"start": v(1.61, -25.5) * mm, "end": v(1.75, -25.1) * mm});
            skLineSegment(sketch, "E1101", {"start": v(1.75, -25.1) * mm, "end": v(1.78, -25) * mm});
            skLineSegment(sketch, "E1102", {"start": v(1.78, -25) * mm, "end": v(1.78, -18) * mm});
            skLineSegment(sketch, "E1103", {"start": v(1.78, -18) * mm, "end": v(1.76, -17.94) * mm});
            skLineSegment(sketch, "E1104", {"start": v(1.76, -17.94) * mm, "end": v(1.67, -17.7) * mm});
            skLineSegment(sketch, "E1105", {"start": v(1.67, -17.7) * mm, "end": v(1.6, -17.53) * mm});
            skLineSegment(sketch, "E1106", {"start": v(1.6, -17.53) * mm, "end": v(1.52, -17.38) * mm});
            skLineSegment(sketch, "E1107", {"start": v(1.52, -17.38) * mm, "end": v(1.45, -17.27) * mm});
            skLineSegment(sketch, "E1108", {"start": v(1.45, -17.27) * mm, "end": v(1.43, -17.22) * mm});
            skLineSegment(sketch, "E1109", {"start": v(1.43, -17.22) * mm, "end": v(1.4, -17.18) * mm});
            skLineSegment(sketch, "E1110", {"start": v(1.4, -17.18) * mm, "end": v(1.32, -17.1) * mm});
            skLineSegment(sketch, "E1111", {"start": v(1.32, -17.1) * mm, "end": v(1.07, -16.87) * mm});
            skLineSegment(sketch, "E1112", {"start": v(1.07, -16.87) * mm, "end": v(0.95, -16.79) * mm});
            skLineSegment(sketch, "E1113", {"start": v(0.95, -16.79) * mm, "end": v(0.8, -16.7) * mm});
            skLineSegment(sketch, "E1114", {"start": v(0.8, -16.7) * mm, "end": v(0.63, -16.63) * mm});
            skLineSegment(sketch, "E1115", {"start": v(0.63, -16.63) * mm, "end": v(0.47, -16.58) * mm});
            skLineSegment(sketch, "E1116", {"start": v(0.47, -16.58) * mm, "end": v(0.4, -16.56) * mm});
            skLineSegment(sketch, "E1117", {"start": v(0.4, -16.56) * mm, "end": v(0.28, -16.55) * mm});
            skLineSegment(sketch, "E1118", {"start": v(0.28, -16.55) * mm, "end": v(0.01, -16.54) * mm});
            skLineSegment(sketch, "E1119", {"start": v(0.01, -16.54) * mm, "end": v(-0.25, -16.55) * mm});
            skLineSegment(sketch, "E1120", {"start": v(-0.25, -16.55) * mm, "end": v(-0.36, -16.56) * mm});
            skLineSegment(sketch, "E1121", {"start": v(-0.36, -16.56) * mm, "end": v(-0.45, -16.58) * mm});
            skLineSegment(sketch, "E1122", {"start": v(-0.45, -16.58) * mm, "end": v(-0.64, -16.65) * mm});
            skLineSegment(sketch, "E1123", {"start": v(-0.64, -16.65) * mm, "end": v(-0.84, -16.74) * mm});
            skLineSegment(sketch, "E1124", {"start": v(-0.84, -16.74) * mm, "end": v(-1.03, -16.87) * mm});
            skLineSegment(sketch, "E1125", {"start": v(-1.03, -16.87) * mm, "end": v(-1.2, -17) * mm});
            skLineSegment(sketch, "E1126", {"start": v(-1.2, -17) * mm, "end": v(-1.4, -17.19) * mm});
            skLineSegment(sketch, "E1127", {"start": v(-1.4, -17.19) * mm, "end": v(-1.4, -17.21) * mm});
            skLineSegment(sketch, "E1128", {"start": v(-1.4, -17.21) * mm, "end": v(-1.43, -17.27) * mm});
            skLineSegment(sketch, "E1129", {"start": v(-1.43, -17.27) * mm, "end": v(-1.5, -17.38) * mm});
            skLineSegment(sketch, "E1130", {"start": v(-1.5, -17.38) * mm, "end": v(-1.58, -17.53) * mm});
            skLineSegment(sketch, "E1131", {"start": v(-1.58, -17.53) * mm, "end": v(-1.65, -17.7) * mm});
            skLineSegment(sketch, "E1132", {"start": v(-1.65, -17.7) * mm, "end": v(-1.73, -17.94) * mm});
            skLineSegment(sketch, "E1133", {"start": v(-1.73, -17.94) * mm, "end": v(-1.75, -18) * mm});
            skLineSegment(sketch, "E1134", {"start": v(-1.75, -18) * mm, "end": v(-1.75, -25.03) * mm});
            skLineSegment(sketch, "E1135", {"start": v(7.5, -14.24) * mm, "end": v(7.5, -17.24) * mm});
            skLineSegment(sketch, "E1136", {"start": v(7.5, -17.24) * mm, "end": v(9.5, -17.24) * mm});
            skLineSegment(sketch, "E1137", {"start": v(9.5, -17.24) * mm, "end": v(9.5, -14.24) * mm});
            skLineSegment(sketch, "E1138", {"start": v(9.5, -14.24) * mm, "end": v(7.5, -14.24) * mm});
            skLineSegment(sketch, "E1139", {"start": v(-1.5, -1) * mm, "end": v(1.5, -1) * mm});
            skLineSegment(sketch, "E1140", {"start": v(1.5, -1) * mm, "end": v(1.5, 1) * mm});
            skLineSegment(sketch, "E1141", {"start": v(1.5, 1) * mm, "end": v(-1.5, 1) * mm});
            skLineSegment(sketch, "E1142", {"start": v(-1.5, 1) * mm, "end": v(-1.5, -1) * mm});
            skLineSegment(sketch, "E1143", {"start": v(-24.5, -1) * mm, "end": v(-24.5, -30.48) * mm});
            skLineSegment(sketch, "E1144", {"start": v(-24.5, -30.48) * mm, "end": v(-9.5, -30.48) * mm});
            skLineSegment(sketch, "E1145", {"start": v(-9.5, -30.48) * mm, "end": v(-9.5, -1) * mm});
            skLineSegment(sketch, "E1146", {"start": v(-9.5, -1) * mm, "end": v(-24.5, -1) * mm});
            skArc(sketch, "E1147", {"start": v(-12.49, -6.02) * mm, "mid": v(-12.85, -5.13) * mm, "end": v(-13.74, -4.77) * mm});
            skArc(sketch, "E1148", {"start": v(-13.74, -4.77) * mm, "mid": v(-14.62, -5.13) * mm, "end": v(-14.99, -6.02) * mm});
            skArc(sketch, "E1149", {"start": v(-14.99, -6.02) * mm, "mid": v(-14.62, -6.9) * mm, "end": v(-13.74, -7.27) * mm});
            skArc(sketch, "E1150", {"start": v(-13.74, -7.27) * mm, "mid": v(-12.85, -6.9) * mm, "end": v(-12.49, -6.02) * mm});
            skArc(sketch, "E1151", {"start": v(-18.99, -6.02) * mm, "mid": v(-19.35, -5.13) * mm, "end": v(-20.24, -4.77) * mm});
            skArc(sketch, "E1152", {"start": v(-20.24, -4.77) * mm, "mid": v(-21.12, -5.13) * mm, "end": v(-21.49, -6.02) * mm});
            skArc(sketch, "E1153", {"start": v(-21.49, -6.02) * mm, "mid": v(-21.12, -6.9) * mm, "end": v(-20.24, -7.27) * mm});
            skArc(sketch, "E1154", {"start": v(-20.24, -7.27) * mm, "mid": v(-19.35, -6.9) * mm, "end": v(-18.99, -6.02) * mm});
            skArc(sketch, "E1155", {"start": v(-11.24, -6.02) * mm, "mid": v(-11.97, -4.25) * mm, "end": v(-13.74, -3.52) * mm});
            skArc(sketch, "E1156", {"start": v(-13.74, -3.52) * mm, "mid": v(-15.5, -4.25) * mm, "end": v(-16.24, -6.02) * mm});
            skArc(sketch, "E1157", {"start": v(-16.24, -6.02) * mm, "mid": v(-15.5, -7.79) * mm, "end": v(-13.74, -8.52) * mm});
            skArc(sketch, "E1158", {"start": v(-13.74, -8.52) * mm, "mid": v(-11.97, -7.79) * mm, "end": v(-11.24, -6.02) * mm});
            skArc(sketch, "E1159", {"start": v(-17.74, -6.02) * mm, "mid": v(-18.47, -4.25) * mm, "end": v(-20.24, -3.52) * mm});
            skArc(sketch, "E1160", {"start": v(-20.24, -3.52) * mm, "mid": v(-22, -4.25) * mm, "end": v(-22.74, -6.02) * mm});
            skArc(sketch, "E1161", {"start": v(-22.74, -6.02) * mm, "mid": v(-22, -7.79) * mm, "end": v(-20.24, -8.52) * mm});
            skArc(sketch, "E1162", {"start": v(-20.24, -8.52) * mm, "mid": v(-18.47, -7.79) * mm, "end": v(-17.74, -6.02) * mm});
            skLineSegment(sketch, "E1163", {"start": v(-18.75, -25.03) * mm, "end": v(-18.73, -25.09) * mm});
            skLineSegment(sketch, "E1164", {"start": v(-18.73, -25.09) * mm, "end": v(-18.65, -25.33) * mm});
            skLineSegment(sketch, "E1165", {"start": v(-18.65, -25.33) * mm, "end": v(-18.6, -25.47) * mm});
            skLineSegment(sketch, "E1166", {"start": v(-18.6, -25.47) * mm, "end": v(-18.56, -25.56) * mm});
            skLineSegment(sketch, "E1167", {"start": v(-18.56, -25.56) * mm, "end": v(-18.5, -25.64) * mm});
            skLineSegment(sketch, "E1168", {"start": v(-18.5, -25.64) * mm, "end": v(-18.43, -25.74) * mm});
            skLineSegment(sketch, "E1169", {"start": v(-18.43, -25.74) * mm, "end": v(-18.4, -25.78) * mm});
            skLineSegment(sketch, "E1170", {"start": v(-18.4, -25.78) * mm, "end": v(-18.4, -25.81) * mm});
            skLineSegment(sketch, "E1171", {"start": v(-18.4, -25.81) * mm, "end": v(-18.36, -25.86) * mm});
            skLineSegment(sketch, "E1172", {"start": v(-18.36, -25.86) * mm, "end": v(-18.27, -25.95) * mm});
            skLineSegment(sketch, "E1173", {"start": v(-18.27, -25.95) * mm, "end": v(-18.08, -26.14) * mm});
            skLineSegment(sketch, "E1174", {"start": v(-18.08, -26.14) * mm, "end": v(-18.03, -26.18) * mm});
            skLineSegment(sketch, "E1175", {"start": v(-18.03, -26.18) * mm, "end": v(-17.98, -26.2) * mm});
            skLineSegment(sketch, "E1176", {"start": v(-17.98, -26.2) * mm, "end": v(-17.96, -26.2) * mm});
            skLineSegment(sketch, "E1177", {"start": v(-17.96, -26.2) * mm, "end": v(-17.95, -26.22) * mm});
            skLineSegment(sketch, "E1178", {"start": v(-17.95, -26.22) * mm, "end": v(-17.92, -26.25) * mm});
            skLineSegment(sketch, "E1179", {"start": v(-17.92, -26.25) * mm, "end": v(-17.86, -26.28) * mm});
            skLineSegment(sketch, "E1180", {"start": v(-17.86, -26.28) * mm, "end": v(-17.58, -26.4) * mm});
            skLineSegment(sketch, "E1181", {"start": v(-17.58, -26.4) * mm, "end": v(-17.46, -26.45) * mm});
            skLineSegment(sketch, "E1182", {"start": v(-17.46, -26.45) * mm, "end": v(-17.32, -26.48) * mm});
            skLineSegment(sketch, "E1183", {"start": v(-17.32, -26.48) * mm, "end": v(-17.16, -26.5) * mm});
            skLineSegment(sketch, "E1184", {"start": v(-17.16, -26.5) * mm, "end": v(-17, -26.5) * mm});
            skLineSegment(sketch, "E1185", {"start": v(-17, -26.5) * mm, "end": v(-16.83, -26.5) * mm});
            skLineSegment(sketch, "E1186", {"start": v(-16.83, -26.5) * mm, "end": v(-16.67, -26.49) * mm});
            skLineSegment(sketch, "E1187", {"start": v(-16.67, -26.49) * mm, "end": v(-16.52, -26.45) * mm});
            skLineSegment(sketch, "E1188", {"start": v(-16.52, -26.45) * mm, "end": v(-16.4, -26.41) * mm});
            skLineSegment(sketch, "E1189", {"start": v(-16.4, -26.41) * mm, "end": v(-16.1, -26.29) * mm});
            skLineSegment(sketch, "E1190", {"start": v(-16.1, -26.29) * mm, "end": v(-16.04, -26.25) * mm});
            skLineSegment(sketch, "E1191", {"start": v(-16.04, -26.25) * mm, "end": v(-16.02, -26.22) * mm});
            skLineSegment(sketch, "E1192", {"start": v(-16.02, -26.22) * mm, "end": v(-16.01, -26.2) * mm});
            skLineSegment(sketch, "E1193", {"start": v(-16.01, -26.2) * mm, "end": v(-16, -26.2) * mm});
            skLineSegment(sketch, "E1194", {"start": v(-16, -26.2) * mm, "end": v(-15.96, -26.19) * mm});
            skLineSegment(sketch, "E1195", {"start": v(-15.96, -26.19) * mm, "end": v(-15.9, -26.15) * mm});
            skLineSegment(sketch, "E1196", {"start": v(-15.9, -26.15) * mm, "end": v(-15.76, -26.02) * mm});
            skLineSegment(sketch, "E1197", {"start": v(-15.76, -26.02) * mm, "end": v(-15.63, -25.9) * mm});
            skLineSegment(sketch, "E1198", {"start": v(-15.63, -25.9) * mm, "end": v(-15.6, -25.84) * mm});
            skLineSegment(sketch, "E1199", {"start": v(-15.6, -25.84) * mm, "end": v(-15.57, -25.81) * mm});
            skLineSegment(sketch, "E1200", {"start": v(-15.57, -25.81) * mm, "end": v(-15.56, -25.78) * mm});
            skLineSegment(sketch, "E1201", {"start": v(-15.56, -25.78) * mm, "end": v(-15.54, -25.74) * mm});
            skLineSegment(sketch, "E1202", {"start": v(-15.54, -25.74) * mm, "end": v(-15.47, -25.66) * mm});
            skLineSegment(sketch, "E1203", {"start": v(-15.47, -25.66) * mm, "end": v(-15.43, -25.6) * mm});
            skLineSegment(sketch, "E1204", {"start": v(-15.43, -25.6) * mm, "end": v(-15.39, -25.5) * mm});
            skLineSegment(sketch, "E1205", {"start": v(-15.39, -25.5) * mm, "end": v(-15.25, -25.1) * mm});
            skLineSegment(sketch, "E1206", {"start": v(-15.25, -25.1) * mm, "end": v(-15.22, -25) * mm});
            skLineSegment(sketch, "E1207", {"start": v(-15.22, -25) * mm, "end": v(-15.22, -18) * mm});
            skLineSegment(sketch, "E1208", {"start": v(-15.22, -18) * mm, "end": v(-15.24, -17.94) * mm});
            skLineSegment(sketch, "E1209", {"start": v(-15.24, -17.94) * mm, "end": v(-15.33, -17.7) * mm});
            skLineSegment(sketch, "E1210", {"start": v(-15.33, -17.7) * mm, "end": v(-15.4, -17.53) * mm});
            skLineSegment(sketch, "E1211", {"start": v(-15.4, -17.53) * mm, "end": v(-15.48, -17.38) * mm});
            skLineSegment(sketch, "E1212", {"start": v(-15.48, -17.38) * mm, "end": v(-15.55, -17.27) * mm});
            skLineSegment(sketch, "E1213", {"start": v(-15.55, -17.27) * mm, "end": v(-15.57, -17.22) * mm});
            skLineSegment(sketch, "E1214", {"start": v(-15.57, -17.22) * mm, "end": v(-15.6, -17.18) * mm});
            skLineSegment(sketch, "E1215", {"start": v(-15.6, -17.18) * mm, "end": v(-15.68, -17.1) * mm});
            skLineSegment(sketch, "E1216", {"start": v(-15.68, -17.1) * mm, "end": v(-15.93, -16.87) * mm});
            skLineSegment(sketch, "E1217", {"start": v(-15.93, -16.87) * mm, "end": v(-16.05, -16.79) * mm});
            skLineSegment(sketch, "E1218", {"start": v(-16.05, -16.79) * mm, "end": v(-16.2, -16.7) * mm});
            skLineSegment(sketch, "E1219", {"start": v(-16.2, -16.7) * mm, "end": v(-16.37, -16.63) * mm});
            skLineSegment(sketch, "E1220", {"start": v(-16.37, -16.63) * mm, "end": v(-16.53, -16.58) * mm});
            skLineSegment(sketch, "E1221", {"start": v(-16.53, -16.58) * mm, "end": v(-16.6, -16.56) * mm});
            skLineSegment(sketch, "E1222", {"start": v(-16.6, -16.56) * mm, "end": v(-16.72, -16.55) * mm});
            skLineSegment(sketch, "E1223", {"start": v(-16.72, -16.55) * mm, "end": v(-16.99, -16.54) * mm});
            skLineSegment(sketch, "E1224", {"start": v(-16.99, -16.54) * mm, "end": v(-17.25, -16.55) * mm});
            skLineSegment(sketch, "E1225", {"start": v(-17.25, -16.55) * mm, "end": v(-17.36, -16.56) * mm});
            skLineSegment(sketch, "E1226", {"start": v(-17.36, -16.56) * mm, "end": v(-17.45, -16.58) * mm});
            skLineSegment(sketch, "E1227", {"start": v(-17.45, -16.58) * mm, "end": v(-17.64, -16.65) * mm});
            skLineSegment(sketch, "E1228", {"start": v(-17.64, -16.65) * mm, "end": v(-17.84, -16.74) * mm});
            skLineSegment(sketch, "E1229", {"start": v(-17.84, -16.74) * mm, "end": v(-18.03, -16.87) * mm});
            skLineSegment(sketch, "E1230", {"start": v(-18.03, -16.87) * mm, "end": v(-18.2, -17) * mm});
            skLineSegment(sketch, "E1231", {"start": v(-18.2, -17) * mm, "end": v(-18.4, -17.19) * mm});
            skLineSegment(sketch, "E1232", {"start": v(-18.4, -17.19) * mm, "end": v(-18.4, -17.21) * mm});
            skLineSegment(sketch, "E1233", {"start": v(-18.4, -17.21) * mm, "end": v(-18.43, -17.27) * mm});
            skLineSegment(sketch, "E1234", {"start": v(-18.43, -17.27) * mm, "end": v(-18.5, -17.38) * mm});
            skLineSegment(sketch, "E1235", {"start": v(-18.5, -17.38) * mm, "end": v(-18.58, -17.53) * mm});
            skLineSegment(sketch, "E1236", {"start": v(-18.58, -17.53) * mm, "end": v(-18.65, -17.7) * mm});
            skLineSegment(sketch, "E1237", {"start": v(-18.65, -17.7) * mm, "end": v(-18.73, -17.94) * mm});
            skLineSegment(sketch, "E1238", {"start": v(-18.73, -17.94) * mm, "end": v(-18.75, -18) * mm});
            skLineSegment(sketch, "E1239", {"start": v(-18.75, -18) * mm, "end": v(-18.75, -25.03) * mm});
            skLineSegment(sketch, "E1240", {"start": v(-18.5, -1) * mm, "end": v(-15.5, -1) * mm});
            skLineSegment(sketch, "E1241", {"start": v(-15.5, -1) * mm, "end": v(-15.5, 1) * mm});
            skLineSegment(sketch, "E1242", {"start": v(-15.5, 1) * mm, "end": v(-18.5, 1) * mm});
            skLineSegment(sketch, "E1243", {"start": v(-18.5, 1) * mm, "end": v(-18.5, -1) * mm});
            skLineSegment(sketch, "E1244", {"start": v(-41.5, -1) * mm, "end": v(-41.5, -30.48) * mm});
            skLineSegment(sketch, "E1245", {"start": v(-41.5, -30.48) * mm, "end": v(-26.5, -30.48) * mm});
            skLineSegment(sketch, "E1246", {"start": v(-26.5, -30.48) * mm, "end": v(-26.5, -1) * mm});
            skLineSegment(sketch, "E1247", {"start": v(-26.5, -1) * mm, "end": v(-41.5, -1) * mm});
            skArc(sketch, "E1248", {"start": v(-29.49, -6.02) * mm, "mid": v(-29.85, -5.13) * mm, "end": v(-30.74, -4.77) * mm});
            skArc(sketch, "E1249", {"start": v(-30.74, -4.77) * mm, "mid": v(-31.62, -5.13) * mm, "end": v(-31.99, -6.02) * mm});
            skArc(sketch, "E1250", {"start": v(-31.99, -6.02) * mm, "mid": v(-31.62, -6.9) * mm, "end": v(-30.74, -7.27) * mm});
            skArc(sketch, "E1251", {"start": v(-30.74, -7.27) * mm, "mid": v(-29.85, -6.9) * mm, "end": v(-29.49, -6.02) * mm});
            skArc(sketch, "E1252", {"start": v(-35.99, -6.02) * mm, "mid": v(-36.35, -5.13) * mm, "end": v(-37.24, -4.77) * mm});
            skArc(sketch, "E1253", {"start": v(-37.24, -4.77) * mm, "mid": v(-38.12, -5.13) * mm, "end": v(-38.49, -6.02) * mm});
            skArc(sketch, "E1254", {"start": v(-38.49, -6.02) * mm, "mid": v(-38.12, -6.9) * mm, "end": v(-37.24, -7.27) * mm});
            skArc(sketch, "E1255", {"start": v(-37.24, -7.27) * mm, "mid": v(-36.35, -6.9) * mm, "end": v(-35.99, -6.02) * mm});
            skArc(sketch, "E1256", {"start": v(-28.24, -6.02) * mm, "mid": v(-28.97, -4.25) * mm, "end": v(-30.74, -3.52) * mm});
            skArc(sketch, "E1257", {"start": v(-30.74, -3.52) * mm, "mid": v(-32.5, -4.25) * mm, "end": v(-33.24, -6.02) * mm});
            skArc(sketch, "E1258", {"start": v(-33.24, -6.02) * mm, "mid": v(-32.5, -7.79) * mm, "end": v(-30.74, -8.52) * mm});
            skArc(sketch, "E1259", {"start": v(-30.74, -8.52) * mm, "mid": v(-28.97, -7.79) * mm, "end": v(-28.24, -6.02) * mm});
            skArc(sketch, "E1260", {"start": v(-34.74, -6.02) * mm, "mid": v(-35.47, -4.25) * mm, "end": v(-37.24, -3.52) * mm});
            skArc(sketch, "E1261", {"start": v(-37.24, -3.52) * mm, "mid": v(-39, -4.25) * mm, "end": v(-39.74, -6.02) * mm});
            skArc(sketch, "E1262", {"start": v(-39.74, -6.02) * mm, "mid": v(-39, -7.79) * mm, "end": v(-37.24, -8.52) * mm});
            skArc(sketch, "E1263", {"start": v(-37.24, -8.52) * mm, "mid": v(-35.47, -7.79) * mm, "end": v(-34.74, -6.02) * mm});
            skLineSegment(sketch, "E1264", {"start": v(-43.5, -14.24) * mm, "end": v(-43.5, -17.24) * mm});
            skLineSegment(sketch, "E1265", {"start": v(-43.5, -17.24) * mm, "end": v(-41.5, -17.24) * mm});
            skLineSegment(sketch, "E1266", {"start": v(-41.5, -17.24) * mm, "end": v(-41.5, -14.24) * mm});
            skLineSegment(sketch, "E1267", {"start": v(-41.5, -14.24) * mm, "end": v(-43.5, -14.24) * mm});
            skLineSegment(sketch, "E1268", {"start": v(-35.75, -25.03) * mm, "end": v(-35.73, -25.09) * mm});
            skLineSegment(sketch, "E1269", {"start": v(-35.73, -25.09) * mm, "end": v(-35.65, -25.33) * mm});
            skLineSegment(sketch, "E1270", {"start": v(-35.65, -25.33) * mm, "end": v(-35.6, -25.47) * mm});
            skLineSegment(sketch, "E1271", {"start": v(-35.6, -25.47) * mm, "end": v(-35.56, -25.56) * mm});
            skLineSegment(sketch, "E1272", {"start": v(-35.56, -25.56) * mm, "end": v(-35.5, -25.64) * mm});
            skLineSegment(sketch, "E1273", {"start": v(-35.5, -25.64) * mm, "end": v(-35.43, -25.74) * mm});
            skLineSegment(sketch, "E1274", {"start": v(-35.43, -25.74) * mm, "end": v(-35.4, -25.78) * mm});
            skLineSegment(sketch, "E1275", {"start": v(-35.4, -25.78) * mm, "end": v(-35.4, -25.81) * mm});
            skLineSegment(sketch, "E1276", {"start": v(-35.4, -25.81) * mm, "end": v(-35.36, -25.86) * mm});
            skLineSegment(sketch, "E1277", {"start": v(-35.36, -25.86) * mm, "end": v(-35.27, -25.95) * mm});
            skLineSegment(sketch, "E1278", {"start": v(-35.27, -25.95) * mm, "end": v(-35.08, -26.14) * mm});
            skLineSegment(sketch, "E1279", {"start": v(-35.08, -26.14) * mm, "end": v(-35.03, -26.18) * mm});
            skLineSegment(sketch, "E1280", {"start": v(-35.03, -26.18) * mm, "end": v(-34.98, -26.2) * mm});
            skLineSegment(sketch, "E1281", {"start": v(-34.98, -26.2) * mm, "end": v(-34.96, -26.2) * mm});
            skLineSegment(sketch, "E1282", {"start": v(-34.96, -26.2) * mm, "end": v(-34.95, -26.22) * mm});
            skLineSegment(sketch, "E1283", {"start": v(-34.95, -26.22) * mm, "end": v(-34.92, -26.25) * mm});
            skLineSegment(sketch, "E1284", {"start": v(-34.92, -26.25) * mm, "end": v(-34.86, -26.28) * mm});
            skLineSegment(sketch, "E1285", {"start": v(-34.86, -26.28) * mm, "end": v(-34.58, -26.4) * mm});
            skLineSegment(sketch, "E1286", {"start": v(-34.58, -26.4) * mm, "end": v(-34.46, -26.45) * mm});
            skLineSegment(sketch, "E1287", {"start": v(-34.46, -26.45) * mm, "end": v(-34.32, -26.48) * mm});
            skLineSegment(sketch, "E1288", {"start": v(-34.32, -26.48) * mm, "end": v(-34.16, -26.5) * mm});
            skLineSegment(sketch, "E1289", {"start": v(-34.16, -26.5) * mm, "end": v(-34, -26.5) * mm});
            skLineSegment(sketch, "E1290", {"start": v(-34, -26.5) * mm, "end": v(-33.83, -26.5) * mm});
            skLineSegment(sketch, "E1291", {"start": v(-33.83, -26.5) * mm, "end": v(-33.67, -26.49) * mm});
            skLineSegment(sketch, "E1292", {"start": v(-33.67, -26.49) * mm, "end": v(-33.52, -26.45) * mm});
            skLineSegment(sketch, "E1293", {"start": v(-33.52, -26.45) * mm, "end": v(-33.4, -26.41) * mm});
            skLineSegment(sketch, "E1294", {"start": v(-33.4, -26.41) * mm, "end": v(-33.1, -26.29) * mm});
            skLineSegment(sketch, "E1295", {"start": v(-33.1, -26.29) * mm, "end": v(-33.04, -26.25) * mm});
            skLineSegment(sketch, "E1296", {"start": v(-33.04, -26.25) * mm, "end": v(-33.02, -26.22) * mm});
            skLineSegment(sketch, "E1297", {"start": v(-33.02, -26.22) * mm, "end": v(-33.01, -26.2) * mm});
            skLineSegment(sketch, "E1298", {"start": v(-33.01, -26.2) * mm, "end": v(-33, -26.2) * mm});
            skLineSegment(sketch, "E1299", {"start": v(-33, -26.2) * mm, "end": v(-32.96, -26.19) * mm});
            skLineSegment(sketch, "E1300", {"start": v(-32.96, -26.19) * mm, "end": v(-32.9, -26.15) * mm});
            skLineSegment(sketch, "E1301", {"start": v(-32.9, -26.15) * mm, "end": v(-32.76, -26.02) * mm});
            skLineSegment(sketch, "E1302", {"start": v(-32.76, -26.02) * mm, "end": v(-32.63, -25.9) * mm});
            skLineSegment(sketch, "E1303", {"start": v(-32.63, -25.9) * mm, "end": v(-32.6, -25.84) * mm});
            skLineSegment(sketch, "E1304", {"start": v(-32.6, -25.84) * mm, "end": v(-32.57, -25.81) * mm});
            skLineSegment(sketch, "E1305", {"start": v(-32.57, -25.81) * mm, "end": v(-32.56, -25.78) * mm});
            skLineSegment(sketch, "E1306", {"start": v(-32.56, -25.78) * mm, "end": v(-32.54, -25.74) * mm});
            skLineSegment(sketch, "E1307", {"start": v(-32.54, -25.74) * mm, "end": v(-32.47, -25.66) * mm});
            skLineSegment(sketch, "E1308", {"start": v(-32.47, -25.66) * mm, "end": v(-32.43, -25.6) * mm});
            skLineSegment(sketch, "E1309", {"start": v(-32.43, -25.6) * mm, "end": v(-32.39, -25.5) * mm});
            skLineSegment(sketch, "E1310", {"start": v(-32.39, -25.5) * mm, "end": v(-32.25, -25.1) * mm});
            skLineSegment(sketch, "E1311", {"start": v(-32.25, -25.1) * mm, "end": v(-32.22, -25) * mm});
            skLineSegment(sketch, "E1312", {"start": v(-32.22, -25) * mm, "end": v(-32.22, -18) * mm});
            skLineSegment(sketch, "E1313", {"start": v(-32.22, -18) * mm, "end": v(-32.24, -17.94) * mm});
            skLineSegment(sketch, "E1314", {"start": v(-32.24, -17.94) * mm, "end": v(-32.33, -17.7) * mm});
            skLineSegment(sketch, "E1315", {"start": v(-32.33, -17.7) * mm, "end": v(-32.4, -17.53) * mm});
            skLineSegment(sketch, "E1316", {"start": v(-32.4, -17.53) * mm, "end": v(-32.48, -17.38) * mm});
            skLineSegment(sketch, "E1317", {"start": v(-32.48, -17.38) * mm, "end": v(-32.55, -17.27) * mm});
            skLineSegment(sketch, "E1318", {"start": v(-32.55, -17.27) * mm, "end": v(-32.57, -17.22) * mm});
            skLineSegment(sketch, "E1319", {"start": v(-32.57, -17.22) * mm, "end": v(-32.6, -17.18) * mm});
            skLineSegment(sketch, "E1320", {"start": v(-32.6, -17.18) * mm, "end": v(-32.68, -17.1) * mm});
            skLineSegment(sketch, "E1321", {"start": v(-32.68, -17.1) * mm, "end": v(-32.93, -16.87) * mm});
            skLineSegment(sketch, "E1322", {"start": v(-32.93, -16.87) * mm, "end": v(-33.05, -16.79) * mm});
            skLineSegment(sketch, "E1323", {"start": v(-33.05, -16.79) * mm, "end": v(-33.2, -16.7) * mm});
            skLineSegment(sketch, "E1324", {"start": v(-33.2, -16.7) * mm, "end": v(-33.37, -16.63) * mm});
            skLineSegment(sketch, "E1325", {"start": v(-33.37, -16.63) * mm, "end": v(-33.53, -16.58) * mm});
            skLineSegment(sketch, "E1326", {"start": v(-33.53, -16.58) * mm, "end": v(-33.6, -16.56) * mm});
            skLineSegment(sketch, "E1327", {"start": v(-33.6, -16.56) * mm, "end": v(-33.72, -16.55) * mm});
            skLineSegment(sketch, "E1328", {"start": v(-33.72, -16.55) * mm, "end": v(-33.99, -16.54) * mm});
            skLineSegment(sketch, "E1329", {"start": v(-33.99, -16.54) * mm, "end": v(-34.25, -16.55) * mm});
            skLineSegment(sketch, "E1330", {"start": v(-34.25, -16.55) * mm, "end": v(-34.36, -16.56) * mm});
            skLineSegment(sketch, "E1331", {"start": v(-34.36, -16.56) * mm, "end": v(-34.45, -16.58) * mm});
            skLineSegment(sketch, "E1332", {"start": v(-34.45, -16.58) * mm, "end": v(-34.64, -16.65) * mm});
            skLineSegment(sketch, "E1333", {"start": v(-34.64, -16.65) * mm, "end": v(-34.84, -16.74) * mm});
            skLineSegment(sketch, "E1334", {"start": v(-34.84, -16.74) * mm, "end": v(-35.03, -16.87) * mm});
            skLineSegment(sketch, "E1335", {"start": v(-35.03, -16.87) * mm, "end": v(-35.2, -17) * mm});
            skLineSegment(sketch, "E1336", {"start": v(-35.2, -17) * mm, "end": v(-35.4, -17.19) * mm});
            skLineSegment(sketch, "E1337", {"start": v(-35.4, -17.19) * mm, "end": v(-35.4, -17.21) * mm});
            skLineSegment(sketch, "E1338", {"start": v(-35.4, -17.21) * mm, "end": v(-35.43, -17.27) * mm});
            skLineSegment(sketch, "E1339", {"start": v(-35.43, -17.27) * mm, "end": v(-35.5, -17.38) * mm});
            skLineSegment(sketch, "E1340", {"start": v(-35.5, -17.38) * mm, "end": v(-35.58, -17.53) * mm});
            skLineSegment(sketch, "E1341", {"start": v(-35.58, -17.53) * mm, "end": v(-35.65, -17.7) * mm});
            skLineSegment(sketch, "E1342", {"start": v(-35.65, -17.7) * mm, "end": v(-35.73, -17.94) * mm});
            skLineSegment(sketch, "E1343", {"start": v(-35.73, -17.94) * mm, "end": v(-35.75, -18) * mm});
            skLineSegment(sketch, "E1344", {"start": v(-35.75, -18) * mm, "end": v(-35.75, -25.03) * mm});
            skLineSegment(sketch, "E1345", {"start": v(-26.5, -14.24) * mm, "end": v(-26.5, -17.24) * mm});
            skLineSegment(sketch, "E1346", {"start": v(-26.5, -17.24) * mm, "end": v(-24.5, -17.24) * mm});
            skLineSegment(sketch, "E1347", {"start": v(-24.5, -17.24) * mm, "end": v(-24.5, -14.24) * mm});
            skLineSegment(sketch, "E1348", {"start": v(-24.5, -14.24) * mm, "end": v(-26.5, -14.24) * mm});
            skLineSegment(sketch, "E1349", {"start": v(-58.5, -1) * mm, "end": v(-58.5, -30.48) * mm});
            skLineSegment(sketch, "E1350", {"start": v(-58.5, -30.48) * mm, "end": v(-43.5, -30.48) * mm});
            skLineSegment(sketch, "E1351", {"start": v(-43.5, -30.48) * mm, "end": v(-43.5, -1) * mm});
            skLineSegment(sketch, "E1352", {"start": v(-43.5, -1) * mm, "end": v(-58.5, -1) * mm});
            skArc(sketch, "E1353", {"start": v(-46.49, -6.02) * mm, "mid": v(-46.85, -5.13) * mm, "end": v(-47.74, -4.77) * mm});
            skArc(sketch, "E1354", {"start": v(-47.74, -4.77) * mm, "mid": v(-48.62, -5.13) * mm, "end": v(-48.99, -6.02) * mm});
            skArc(sketch, "E1355", {"start": v(-48.99, -6.02) * mm, "mid": v(-48.62, -6.9) * mm, "end": v(-47.74, -7.27) * mm});
            skArc(sketch, "E1356", {"start": v(-47.74, -7.27) * mm, "mid": v(-46.85, -6.9) * mm, "end": v(-46.49, -6.02) * mm});
            skArc(sketch, "E1357", {"start": v(-52.99, -6.02) * mm, "mid": v(-53.35, -5.13) * mm, "end": v(-54.24, -4.77) * mm});
            skArc(sketch, "E1358", {"start": v(-54.24, -4.77) * mm, "mid": v(-55.12, -5.13) * mm, "end": v(-55.49, -6.02) * mm});
            skArc(sketch, "E1359", {"start": v(-55.49, -6.02) * mm, "mid": v(-55.12, -6.9) * mm, "end": v(-54.24, -7.27) * mm});
            skArc(sketch, "E1360", {"start": v(-54.24, -7.27) * mm, "mid": v(-53.35, -6.9) * mm, "end": v(-52.99, -6.02) * mm});
            skArc(sketch, "E1361", {"start": v(-45.24, -6.02) * mm, "mid": v(-45.97, -4.25) * mm, "end": v(-47.74, -3.52) * mm});
            skArc(sketch, "E1362", {"start": v(-47.74, -3.52) * mm, "mid": v(-49.5, -4.25) * mm, "end": v(-50.24, -6.02) * mm});
            skArc(sketch, "E1363", {"start": v(-50.24, -6.02) * mm, "mid": v(-49.5, -7.79) * mm, "end": v(-47.74, -8.52) * mm});
            skArc(sketch, "E1364", {"start": v(-47.74, -8.52) * mm, "mid": v(-45.97, -7.79) * mm, "end": v(-45.24, -6.02) * mm});
            skArc(sketch, "E1365", {"start": v(-51.74, -6.02) * mm, "mid": v(-52.47, -4.25) * mm, "end": v(-54.24, -3.52) * mm});
            skArc(sketch, "E1366", {"start": v(-54.24, -3.52) * mm, "mid": v(-56, -4.25) * mm, "end": v(-56.74, -6.02) * mm});
            skArc(sketch, "E1367", {"start": v(-56.74, -6.02) * mm, "mid": v(-56, -7.79) * mm, "end": v(-54.24, -8.52) * mm});
            skArc(sketch, "E1368", {"start": v(-54.24, -8.52) * mm, "mid": v(-52.47, -7.79) * mm, "end": v(-51.74, -6.02) * mm});
            skLineSegment(sketch, "E1369", {"start": v(-52.5, -32.48) * mm, "end": v(-49.5, -32.48) * mm});
            skLineSegment(sketch, "E1370", {"start": v(-49.5, -32.48) * mm, "end": v(-49.5, -30.48) * mm});
            skLineSegment(sketch, "E1371", {"start": v(-49.5, -30.48) * mm, "end": v(-52.5, -30.48) * mm});
            skLineSegment(sketch, "E1372", {"start": v(-52.5, -30.48) * mm, "end": v(-52.5, -32.48) * mm});
            skLineSegment(sketch, "E1373", {"start": v(-52.75, -25.03) * mm, "end": v(-52.73, -25.09) * mm});
            skLineSegment(sketch, "E1374", {"start": v(-52.73, -25.09) * mm, "end": v(-52.65, -25.33) * mm});
            skLineSegment(sketch, "E1375", {"start": v(-52.65, -25.33) * mm, "end": v(-52.6, -25.47) * mm});
            skLineSegment(sketch, "E1376", {"start": v(-52.6, -25.47) * mm, "end": v(-52.56, -25.56) * mm});
            skLineSegment(sketch, "E1377", {"start": v(-52.56, -25.56) * mm, "end": v(-52.5, -25.64) * mm});
            skLineSegment(sketch, "E1378", {"start": v(-52.5, -25.64) * mm, "end": v(-52.43, -25.74) * mm});
            skLineSegment(sketch, "E1379", {"start": v(-52.43, -25.74) * mm, "end": v(-52.4, -25.78) * mm});
            skLineSegment(sketch, "E1380", {"start": v(-52.4, -25.78) * mm, "end": v(-52.4, -25.81) * mm});
            skLineSegment(sketch, "E1381", {"start": v(-52.4, -25.81) * mm, "end": v(-52.36, -25.86) * mm});
            skLineSegment(sketch, "E1382", {"start": v(-52.36, -25.86) * mm, "end": v(-52.27, -25.95) * mm});
            skLineSegment(sketch, "E1383", {"start": v(-52.27, -25.95) * mm, "end": v(-52.08, -26.14) * mm});
            skLineSegment(sketch, "E1384", {"start": v(-52.08, -26.14) * mm, "end": v(-52.03, -26.18) * mm});
            skLineSegment(sketch, "E1385", {"start": v(-52.03, -26.18) * mm, "end": v(-51.98, -26.2) * mm});
            skLineSegment(sketch, "E1386", {"start": v(-51.98, -26.2) * mm, "end": v(-51.96, -26.2) * mm});
            skLineSegment(sketch, "E1387", {"start": v(-51.96, -26.2) * mm, "end": v(-51.95, -26.22) * mm});
            skLineSegment(sketch, "E1388", {"start": v(-51.95, -26.22) * mm, "end": v(-51.92, -26.25) * mm});
            skLineSegment(sketch, "E1389", {"start": v(-51.92, -26.25) * mm, "end": v(-51.86, -26.28) * mm});
            skLineSegment(sketch, "E1390", {"start": v(-51.86, -26.28) * mm, "end": v(-51.58, -26.4) * mm});
            skLineSegment(sketch, "E1391", {"start": v(-51.58, -26.4) * mm, "end": v(-51.46, -26.45) * mm});
            skLineSegment(sketch, "E1392", {"start": v(-51.46, -26.45) * mm, "end": v(-51.32, -26.48) * mm});
            skLineSegment(sketch, "E1393", {"start": v(-51.32, -26.48) * mm, "end": v(-51.16, -26.5) * mm});
            skLineSegment(sketch, "E1394", {"start": v(-51.16, -26.5) * mm, "end": v(-51, -26.5) * mm});
            skLineSegment(sketch, "E1395", {"start": v(-51, -26.5) * mm, "end": v(-50.83, -26.5) * mm});
            skLineSegment(sketch, "E1396", {"start": v(-50.83, -26.5) * mm, "end": v(-50.67, -26.49) * mm});
            skLineSegment(sketch, "E1397", {"start": v(-50.67, -26.49) * mm, "end": v(-50.52, -26.45) * mm});
            skLineSegment(sketch, "E1398", {"start": v(-50.52, -26.45) * mm, "end": v(-50.4, -26.41) * mm});
            skLineSegment(sketch, "E1399", {"start": v(-50.4, -26.41) * mm, "end": v(-50.1, -26.29) * mm});
            skLineSegment(sketch, "E1400", {"start": v(-50.1, -26.29) * mm, "end": v(-50.04, -26.25) * mm});
            skLineSegment(sketch, "E1401", {"start": v(-50.04, -26.25) * mm, "end": v(-50.02, -26.22) * mm});
            skLineSegment(sketch, "E1402", {"start": v(-50.02, -26.22) * mm, "end": v(-50.01, -26.2) * mm});
            skLineSegment(sketch, "E1403", {"start": v(-50.01, -26.2) * mm, "end": v(-50, -26.2) * mm});
            skLineSegment(sketch, "E1404", {"start": v(-50, -26.2) * mm, "end": v(-49.96, -26.19) * mm});
            skLineSegment(sketch, "E1405", {"start": v(-49.96, -26.19) * mm, "end": v(-49.9, -26.15) * mm});
            skLineSegment(sketch, "E1406", {"start": v(-49.9, -26.15) * mm, "end": v(-49.76, -26.02) * mm});
            skLineSegment(sketch, "E1407", {"start": v(-49.76, -26.02) * mm, "end": v(-49.63, -25.9) * mm});
            skLineSegment(sketch, "E1408", {"start": v(-49.63, -25.9) * mm, "end": v(-49.6, -25.84) * mm});
            skLineSegment(sketch, "E1409", {"start": v(-49.6, -25.84) * mm, "end": v(-49.57, -25.81) * mm});
            skLineSegment(sketch, "E1410", {"start": v(-49.57, -25.81) * mm, "end": v(-49.56, -25.78) * mm});
            skLineSegment(sketch, "E1411", {"start": v(-49.56, -25.78) * mm, "end": v(-49.54, -25.74) * mm});
            skLineSegment(sketch, "E1412", {"start": v(-49.54, -25.74) * mm, "end": v(-49.47, -25.66) * mm});
            skLineSegment(sketch, "E1413", {"start": v(-49.47, -25.66) * mm, "end": v(-49.43, -25.6) * mm});
            skLineSegment(sketch, "E1414", {"start": v(-49.43, -25.6) * mm, "end": v(-49.39, -25.5) * mm});
            skLineSegment(sketch, "E1415", {"start": v(-49.39, -25.5) * mm, "end": v(-49.25, -25.1) * mm});
            skLineSegment(sketch, "E1416", {"start": v(-49.25, -25.1) * mm, "end": v(-49.22, -25) * mm});
            skLineSegment(sketch, "E1417", {"start": v(-49.22, -25) * mm, "end": v(-49.22, -18) * mm});
            skLineSegment(sketch, "E1418", {"start": v(-49.22, -18) * mm, "end": v(-49.24, -17.94) * mm});
            skLineSegment(sketch, "E1419", {"start": v(-49.24, -17.94) * mm, "end": v(-49.33, -17.7) * mm});
            skLineSegment(sketch, "E1420", {"start": v(-49.33, -17.7) * mm, "end": v(-49.4, -17.53) * mm});
            skLineSegment(sketch, "E1421", {"start": v(-49.4, -17.53) * mm, "end": v(-49.48, -17.38) * mm});
            skLineSegment(sketch, "E1422", {"start": v(-49.48, -17.38) * mm, "end": v(-49.55, -17.27) * mm});
            skLineSegment(sketch, "E1423", {"start": v(-49.55, -17.27) * mm, "end": v(-49.57, -17.22) * mm});
            skLineSegment(sketch, "E1424", {"start": v(-49.57, -17.22) * mm, "end": v(-49.6, -17.18) * mm});
            skLineSegment(sketch, "E1425", {"start": v(-49.6, -17.18) * mm, "end": v(-49.68, -17.1) * mm});
            skLineSegment(sketch, "E1426", {"start": v(-49.68, -17.1) * mm, "end": v(-49.93, -16.87) * mm});
            skLineSegment(sketch, "E1427", {"start": v(-49.93, -16.87) * mm, "end": v(-50.05, -16.79) * mm});
            skLineSegment(sketch, "E1428", {"start": v(-50.05, -16.79) * mm, "end": v(-50.2, -16.7) * mm});
            skLineSegment(sketch, "E1429", {"start": v(-50.2, -16.7) * mm, "end": v(-50.37, -16.63) * mm});
            skLineSegment(sketch, "E1430", {"start": v(-50.37, -16.63) * mm, "end": v(-50.53, -16.58) * mm});
            skLineSegment(sketch, "E1431", {"start": v(-50.53, -16.58) * mm, "end": v(-50.6, -16.56) * mm});
            skLineSegment(sketch, "E1432", {"start": v(-50.6, -16.56) * mm, "end": v(-50.72, -16.55) * mm});
            skLineSegment(sketch, "E1433", {"start": v(-50.72, -16.55) * mm, "end": v(-50.99, -16.54) * mm});
            skLineSegment(sketch, "E1434", {"start": v(-50.99, -16.54) * mm, "end": v(-51.25, -16.55) * mm});
            skLineSegment(sketch, "E1435", {"start": v(-51.25, -16.55) * mm, "end": v(-51.36, -16.56) * mm});
            skLineSegment(sketch, "E1436", {"start": v(-51.36, -16.56) * mm, "end": v(-51.45, -16.58) * mm});
            skLineSegment(sketch, "E1437", {"start": v(-51.45, -16.58) * mm, "end": v(-51.64, -16.65) * mm});
            skLineSegment(sketch, "E1438", {"start": v(-51.64, -16.65) * mm, "end": v(-51.84, -16.74) * mm});
            skLineSegment(sketch, "E1439", {"start": v(-51.84, -16.74) * mm, "end": v(-52.03, -16.87) * mm});
            skLineSegment(sketch, "E1440", {"start": v(-52.03, -16.87) * mm, "end": v(-52.2, -17) * mm});
            skLineSegment(sketch, "E1441", {"start": v(-52.2, -17) * mm, "end": v(-52.4, -17.19) * mm});
            skLineSegment(sketch, "E1442", {"start": v(-52.4, -17.19) * mm, "end": v(-52.4, -17.21) * mm});
            skLineSegment(sketch, "E1443", {"start": v(-52.4, -17.21) * mm, "end": v(-52.43, -17.27) * mm});
            skLineSegment(sketch, "E1444", {"start": v(-52.43, -17.27) * mm, "end": v(-52.5, -17.38) * mm});
            skLineSegment(sketch, "E1445", {"start": v(-52.5, -17.38) * mm, "end": v(-52.58, -17.53) * mm});
            skLineSegment(sketch, "E1446", {"start": v(-52.58, -17.53) * mm, "end": v(-52.65, -17.7) * mm});
            skLineSegment(sketch, "E1447", {"start": v(-52.65, -17.7) * mm, "end": v(-52.73, -17.94) * mm});
            skLineSegment(sketch, "E1448", {"start": v(-52.73, -17.94) * mm, "end": v(-52.75, -18) * mm});
            skLineSegment(sketch, "E1449", {"start": v(-52.75, -18) * mm, "end": v(-52.75, -25.03) * mm});
            skLineSegment(sketch, "E1450", {"start": v(-52.5, -1) * mm, "end": v(-49.5, -1) * mm});
            skLineSegment(sketch, "E1451", {"start": v(-49.5, -1) * mm, "end": v(-49.5, 1) * mm});
            skLineSegment(sketch, "E1452", {"start": v(-49.5, 1) * mm, "end": v(-52.5, 1) * mm});
            skLineSegment(sketch, "E1453", {"start": v(-52.5, 1) * mm, "end": v(-52.5, -1) * mm});
            skLineSegment(sketch, "E1454", {"start": v(-58.5, 30.48) * mm, "end": v(-58.5, 1) * mm});
            skLineSegment(sketch, "E1455", {"start": v(-58.5, 1) * mm, "end": v(-43.5, 1) * mm});
            skLineSegment(sketch, "E1456", {"start": v(-43.5, 1) * mm, "end": v(-43.5, 30.48) * mm});
            skLineSegment(sketch, "E1457", {"start": v(-43.5, 30.48) * mm, "end": v(-58.5, 30.48) * mm});
            skArc(sketch, "E1458", {"start": v(-46.49, 25.47) * mm, "mid": v(-46.85, 26.35) * mm, "end": v(-47.74, 26.72) * mm});
            skArc(sketch, "E1459", {"start": v(-47.74, 26.72) * mm, "mid": v(-48.62, 26.35) * mm, "end": v(-48.99, 25.47) * mm});
            skArc(sketch, "E1460", {"start": v(-48.99, 25.47) * mm, "mid": v(-48.62, 24.58) * mm, "end": v(-47.74, 24.22) * mm});
            skArc(sketch, "E1461", {"start": v(-47.74, 24.22) * mm, "mid": v(-46.85, 24.58) * mm, "end": v(-46.49, 25.47) * mm});
            skArc(sketch, "E1462", {"start": v(-52.99, 25.47) * mm, "mid": v(-53.35, 26.35) * mm, "end": v(-54.24, 26.72) * mm});
            skArc(sketch, "E1463", {"start": v(-54.24, 26.72) * mm, "mid": v(-55.12, 26.35) * mm, "end": v(-55.49, 25.47) * mm});
            skArc(sketch, "E1464", {"start": v(-55.49, 25.47) * mm, "mid": v(-55.12, 24.58) * mm, "end": v(-54.24, 24.22) * mm});
            skArc(sketch, "E1465", {"start": v(-54.24, 24.22) * mm, "mid": v(-53.35, 24.58) * mm, "end": v(-52.99, 25.47) * mm});
            skArc(sketch, "E1466", {"start": v(-45.24, 25.47) * mm, "mid": v(-45.97, 27.23) * mm, "end": v(-47.74, 27.97) * mm});
            skArc(sketch, "E1467", {"start": v(-47.74, 27.97) * mm, "mid": v(-49.5, 27.23) * mm, "end": v(-50.24, 25.47) * mm});
            skArc(sketch, "E1468", {"start": v(-50.24, 25.47) * mm, "mid": v(-49.5, 23.7) * mm, "end": v(-47.74, 22.97) * mm});
            skArc(sketch, "E1469", {"start": v(-47.74, 22.97) * mm, "mid": v(-45.97, 23.7) * mm, "end": v(-45.24, 25.47) * mm});
            skArc(sketch, "E1470", {"start": v(-51.74, 25.47) * mm, "mid": v(-52.47, 27.23) * mm, "end": v(-54.24, 27.97) * mm});
            skArc(sketch, "E1471", {"start": v(-54.24, 27.97) * mm, "mid": v(-56, 27.23) * mm, "end": v(-56.74, 25.47) * mm});
            skArc(sketch, "E1472", {"start": v(-56.74, 25.47) * mm, "mid": v(-56, 23.7) * mm, "end": v(-54.24, 22.97) * mm});
            skArc(sketch, "E1473", {"start": v(-54.24, 22.97) * mm, "mid": v(-52.47, 23.7) * mm, "end": v(-51.74, 25.47) * mm});
            skLineSegment(sketch, "E1474", {"start": v(-52.75, 6.46) * mm, "end": v(-52.73, 6.4) * mm});
            skLineSegment(sketch, "E1475", {"start": v(-52.73, 6.4) * mm, "end": v(-52.65, 6.16) * mm});
            skLineSegment(sketch, "E1476", {"start": v(-52.65, 6.16) * mm, "end": v(-52.6, 6.02) * mm});
            skLineSegment(sketch, "E1477", {"start": v(-52.6, 6.02) * mm, "end": v(-52.56, 5.92) * mm});
            skLineSegment(sketch, "E1478", {"start": v(-52.56, 5.92) * mm, "end": v(-52.5, 5.84) * mm});
            skLineSegment(sketch, "E1479", {"start": v(-52.5, 5.84) * mm, "end": v(-52.43, 5.74) * mm});
            skLineSegment(sketch, "E1480", {"start": v(-52.43, 5.74) * mm, "end": v(-52.4, 5.7) * mm});
            skLineSegment(sketch, "E1481", {"start": v(-52.4, 5.7) * mm, "end": v(-52.4, 5.67) * mm});
            skLineSegment(sketch, "E1482", {"start": v(-52.4, 5.67) * mm, "end": v(-52.36, 5.62) * mm});
            skLineSegment(sketch, "E1483", {"start": v(-52.36, 5.62) * mm, "end": v(-52.27, 5.53) * mm});
            skLineSegment(sketch, "E1484", {"start": v(-52.27, 5.53) * mm, "end": v(-52.08, 5.35) * mm});
            skLineSegment(sketch, "E1485", {"start": v(-52.08, 5.35) * mm, "end": v(-52.03, 5.3) * mm});
            skLineSegment(sketch, "E1486", {"start": v(-52.03, 5.3) * mm, "end": v(-51.98, 5.28) * mm});
            skLineSegment(sketch, "E1487", {"start": v(-51.98, 5.28) * mm, "end": v(-51.96, 5.28) * mm});
            skLineSegment(sketch, "E1488", {"start": v(-51.96, 5.28) * mm, "end": v(-51.95, 5.26) * mm});
            skLineSegment(sketch, "E1489", {"start": v(-51.95, 5.26) * mm, "end": v(-51.92, 5.24) * mm});
            skLineSegment(sketch, "E1490", {"start": v(-51.92, 5.24) * mm, "end": v(-51.86, 5.2) * mm});
            skLineSegment(sketch, "E1491", {"start": v(-51.86, 5.2) * mm, "end": v(-51.58, 5.08) * mm});
            skLineSegment(sketch, "E1492", {"start": v(-51.58, 5.08) * mm, "end": v(-51.46, 5.03) * mm});
            skLineSegment(sketch, "E1493", {"start": v(-51.46, 5.03) * mm, "end": v(-51.32, 5) * mm});
            skLineSegment(sketch, "E1494", {"start": v(-51.32, 5) * mm, "end": v(-51.16, 4.98) * mm});
            skLineSegment(sketch, "E1495", {"start": v(-51.16, 4.98) * mm, "end": v(-51, 4.98) * mm});
            skLineSegment(sketch, "E1496", {"start": v(-51, 4.98) * mm, "end": v(-50.83, 4.98) * mm});
            skLineSegment(sketch, "E1497", {"start": v(-50.83, 4.98) * mm, "end": v(-50.67, 5) * mm});
            skLineSegment(sketch, "E1498", {"start": v(-50.67, 5) * mm, "end": v(-50.52, 5.03) * mm});
            skLineSegment(sketch, "E1499", {"start": v(-50.52, 5.03) * mm, "end": v(-50.4, 5.07) * mm});
            skLineSegment(sketch, "E1500", {"start": v(-50.4, 5.07) * mm, "end": v(-50.1, 5.2) * mm});
            skLineSegment(sketch, "E1501", {"start": v(-50.1, 5.2) * mm, "end": v(-50.04, 5.24) * mm});
            skLineSegment(sketch, "E1502", {"start": v(-50.04, 5.24) * mm, "end": v(-50.02, 5.26) * mm});
            skLineSegment(sketch, "E1503", {"start": v(-50.02, 5.26) * mm, "end": v(-50.01, 5.28) * mm});
            skLineSegment(sketch, "E1504", {"start": v(-50.01, 5.28) * mm, "end": v(-50, 5.28) * mm});
            skLineSegment(sketch, "E1505", {"start": v(-50, 5.28) * mm, "end": v(-49.96, 5.3) * mm});
            skLineSegment(sketch, "E1506", {"start": v(-49.96, 5.3) * mm, "end": v(-49.9, 5.34) * mm});
            skLineSegment(sketch, "E1507", {"start": v(-49.9, 5.34) * mm, "end": v(-49.76, 5.46) * mm});
            skLineSegment(sketch, "E1508", {"start": v(-49.76, 5.46) * mm, "end": v(-49.63, 5.6) * mm});
            skLineSegment(sketch, "E1509", {"start": v(-49.63, 5.6) * mm, "end": v(-49.6, 5.64) * mm});
            skLineSegment(sketch, "E1510", {"start": v(-49.6, 5.64) * mm, "end": v(-49.57, 5.67) * mm});
            skLineSegment(sketch, "E1511", {"start": v(-49.57, 5.67) * mm, "end": v(-49.56, 5.7) * mm});
            skLineSegment(sketch, "E1512", {"start": v(-49.56, 5.7) * mm, "end": v(-49.54, 5.74) * mm});
            skLineSegment(sketch, "E1513", {"start": v(-49.54, 5.74) * mm, "end": v(-49.47, 5.83) * mm});
            skLineSegment(sketch, "E1514", {"start": v(-49.47, 5.83) * mm, "end": v(-49.43, 5.89) * mm});
            skLineSegment(sketch, "E1515", {"start": v(-49.43, 5.89) * mm, "end": v(-49.39, 5.98) * mm});
            skLineSegment(sketch, "E1516", {"start": v(-49.39, 5.98) * mm, "end": v(-49.25, 6.38) * mm});
            skLineSegment(sketch, "E1517", {"start": v(-49.25, 6.38) * mm, "end": v(-49.22, 6.49) * mm});
            skLineSegment(sketch, "E1518", {"start": v(-49.22, 6.49) * mm, "end": v(-49.22, 13.48) * mm});
            skLineSegment(sketch, "E1519", {"start": v(-49.22, 13.48) * mm, "end": v(-49.24, 13.55) * mm});
            skLineSegment(sketch, "E1520", {"start": v(-49.24, 13.55) * mm, "end": v(-49.33, 13.8) * mm});
            skLineSegment(sketch, "E1521", {"start": v(-49.33, 13.8) * mm, "end": v(-49.4, 13.96) * mm});
            skLineSegment(sketch, "E1522", {"start": v(-49.4, 13.96) * mm, "end": v(-49.48, 14.1) * mm});
            skLineSegment(sketch, "E1523", {"start": v(-49.48, 14.1) * mm, "end": v(-49.55, 14.21) * mm});
            skLineSegment(sketch, "E1524", {"start": v(-49.55, 14.21) * mm, "end": v(-49.57, 14.27) * mm});
            skLineSegment(sketch, "E1525", {"start": v(-49.57, 14.27) * mm, "end": v(-49.6, 14.3) * mm});
            skLineSegment(sketch, "E1526", {"start": v(-49.6, 14.3) * mm, "end": v(-49.68, 14.39) * mm});
            skLineSegment(sketch, "E1527", {"start": v(-49.68, 14.39) * mm, "end": v(-49.93, 14.62) * mm});
            skLineSegment(sketch, "E1528", {"start": v(-49.93, 14.62) * mm, "end": v(-50.05, 14.7) * mm});
            skLineSegment(sketch, "E1529", {"start": v(-50.05, 14.7) * mm, "end": v(-50.2, 14.78) * mm});
            skLineSegment(sketch, "E1530", {"start": v(-50.2, 14.78) * mm, "end": v(-50.37, 14.85) * mm});
            skLineSegment(sketch, "E1531", {"start": v(-50.37, 14.85) * mm, "end": v(-50.53, 14.9) * mm});
            skLineSegment(sketch, "E1532", {"start": v(-50.53, 14.9) * mm, "end": v(-50.6, 14.92) * mm});
            skLineSegment(sketch, "E1533", {"start": v(-50.6, 14.92) * mm, "end": v(-50.72, 14.93) * mm});
            skLineSegment(sketch, "E1534", {"start": v(-50.72, 14.93) * mm, "end": v(-50.99, 14.94) * mm});
            skLineSegment(sketch, "E1535", {"start": v(-50.99, 14.94) * mm, "end": v(-51.25, 14.93) * mm});
            skLineSegment(sketch, "E1536", {"start": v(-51.25, 14.93) * mm, "end": v(-51.36, 14.92) * mm});
            skLineSegment(sketch, "E1537", {"start": v(-51.36, 14.92) * mm, "end": v(-51.45, 14.9) * mm});
            skLineSegment(sketch, "E1538", {"start": v(-51.45, 14.9) * mm, "end": v(-51.64, 14.84) * mm});
            skLineSegment(sketch, "E1539", {"start": v(-51.64, 14.84) * mm, "end": v(-51.84, 14.74) * mm});
            skLineSegment(sketch, "E1540", {"start": v(-51.84, 14.74) * mm, "end": v(-52.03, 14.62) * mm});
            skLineSegment(sketch, "E1541", {"start": v(-52.03, 14.62) * mm, "end": v(-52.2, 14.48) * mm});
            skLineSegment(sketch, "E1542", {"start": v(-52.2, 14.48) * mm, "end": v(-52.4, 14.3) * mm});
            skLineSegment(sketch, "E1543", {"start": v(-52.4, 14.3) * mm, "end": v(-52.4, 14.27) * mm});
            skLineSegment(sketch, "E1544", {"start": v(-52.4, 14.27) * mm, "end": v(-52.43, 14.21) * mm});
            skLineSegment(sketch, "E1545", {"start": v(-52.43, 14.21) * mm, "end": v(-52.5, 14.1) * mm});
            skLineSegment(sketch, "E1546", {"start": v(-52.5, 14.1) * mm, "end": v(-52.58, 13.96) * mm});
            skLineSegment(sketch, "E1547", {"start": v(-52.58, 13.96) * mm, "end": v(-52.65, 13.8) * mm});
            skLineSegment(sketch, "E1548", {"start": v(-52.65, 13.8) * mm, "end": v(-52.73, 13.55) * mm});
            skLineSegment(sketch, "E1549", {"start": v(-52.73, 13.55) * mm, "end": v(-52.75, 13.48) * mm});
            skLineSegment(sketch, "E1550", {"start": v(-52.75, 13.48) * mm, "end": v(-52.75, 6.46) * mm});
            skLineSegment(sketch, "E1551", {"start": v(-52.5, 30.48) * mm, "end": v(-49.5, 30.48) * mm});
            skLineSegment(sketch, "E1552", {"start": v(-49.5, 30.48) * mm, "end": v(-49.5, 32.48) * mm});
            skLineSegment(sketch, "E1553", {"start": v(-49.5, 32.48) * mm, "end": v(-52.5, 32.48) * mm});
            skLineSegment(sketch, "E1554", {"start": v(-52.5, 32.48) * mm, "end": v(-52.5, 30.48) * mm});
            skLineSegment(sketch, "E1555", {"start": v(-41.5, 30.48) * mm, "end": v(-41.5, 1) * mm});
            skLineSegment(sketch, "E1556", {"start": v(-41.5, 1) * mm, "end": v(-26.5, 1) * mm});
            skLineSegment(sketch, "E1557", {"start": v(-26.5, 1) * mm, "end": v(-26.5, 30.48) * mm});
            skLineSegment(sketch, "E1558", {"start": v(-26.5, 30.48) * mm, "end": v(-41.5, 30.48) * mm});
            skArc(sketch, "E1559", {"start": v(-29.49, 25.47) * mm, "mid": v(-29.85, 26.35) * mm, "end": v(-30.74, 26.72) * mm});
            skArc(sketch, "E1560", {"start": v(-30.74, 26.72) * mm, "mid": v(-31.62, 26.35) * mm, "end": v(-31.99, 25.47) * mm});
            skArc(sketch, "E1561", {"start": v(-31.99, 25.47) * mm, "mid": v(-31.62, 24.58) * mm, "end": v(-30.74, 24.22) * mm});
            skArc(sketch, "E1562", {"start": v(-30.74, 24.22) * mm, "mid": v(-29.85, 24.58) * mm, "end": v(-29.49, 25.47) * mm});
            skArc(sketch, "E1563", {"start": v(-35.99, 25.47) * mm, "mid": v(-36.35, 26.35) * mm, "end": v(-37.24, 26.72) * mm});
            skArc(sketch, "E1564", {"start": v(-37.24, 26.72) * mm, "mid": v(-38.12, 26.35) * mm, "end": v(-38.49, 25.47) * mm});
            skArc(sketch, "E1565", {"start": v(-38.49, 25.47) * mm, "mid": v(-38.12, 24.58) * mm, "end": v(-37.24, 24.22) * mm});
            skArc(sketch, "E1566", {"start": v(-37.24, 24.22) * mm, "mid": v(-36.35, 24.58) * mm, "end": v(-35.99, 25.47) * mm});
            skArc(sketch, "E1567", {"start": v(-28.24, 25.47) * mm, "mid": v(-28.97, 27.23) * mm, "end": v(-30.74, 27.97) * mm});
            skArc(sketch, "E1568", {"start": v(-30.74, 27.97) * mm, "mid": v(-32.5, 27.23) * mm, "end": v(-33.24, 25.47) * mm});
            skArc(sketch, "E1569", {"start": v(-33.24, 25.47) * mm, "mid": v(-32.5, 23.7) * mm, "end": v(-30.74, 22.97) * mm});
            skArc(sketch, "E1570", {"start": v(-30.74, 22.97) * mm, "mid": v(-28.97, 23.7) * mm, "end": v(-28.24, 25.47) * mm});
            skArc(sketch, "E1571", {"start": v(-34.74, 25.47) * mm, "mid": v(-35.47, 27.23) * mm, "end": v(-37.24, 27.97) * mm});
            skArc(sketch, "E1572", {"start": v(-37.24, 27.97) * mm, "mid": v(-39, 27.23) * mm, "end": v(-39.74, 25.47) * mm});
            skArc(sketch, "E1573", {"start": v(-39.74, 25.47) * mm, "mid": v(-39, 23.7) * mm, "end": v(-37.24, 22.97) * mm});
            skArc(sketch, "E1574", {"start": v(-37.24, 22.97) * mm, "mid": v(-35.47, 23.7) * mm, "end": v(-34.74, 25.47) * mm});
            skLineSegment(sketch, "E1575", {"start": v(-35.5, -1) * mm, "end": v(-32.5, -1) * mm});
            skLineSegment(sketch, "E1576", {"start": v(-32.5, -1) * mm, "end": v(-32.5, 1) * mm});
            skLineSegment(sketch, "E1577", {"start": v(-32.5, 1) * mm, "end": v(-35.5, 1) * mm});
            skLineSegment(sketch, "E1578", {"start": v(-35.5, 1) * mm, "end": v(-35.5, -1) * mm});
            skLineSegment(sketch, "E1579", {"start": v(-43.5, 17.24) * mm, "end": v(-43.5, 14.24) * mm});
            skLineSegment(sketch, "E1580", {"start": v(-43.5, 14.24) * mm, "end": v(-41.5, 14.24) * mm});
            skLineSegment(sketch, "E1581", {"start": v(-41.5, 14.24) * mm, "end": v(-41.5, 17.24) * mm});
            skLineSegment(sketch, "E1582", {"start": v(-41.5, 17.24) * mm, "end": v(-43.5, 17.24) * mm});
            skLineSegment(sketch, "E1583", {"start": v(-35.75, 6.46) * mm, "end": v(-35.73, 6.4) * mm});
            skLineSegment(sketch, "E1584", {"start": v(-35.73, 6.4) * mm, "end": v(-35.65, 6.16) * mm});
            skLineSegment(sketch, "E1585", {"start": v(-35.65, 6.16) * mm, "end": v(-35.6, 6.02) * mm});
            skLineSegment(sketch, "E1586", {"start": v(-35.6, 6.02) * mm, "end": v(-35.56, 5.92) * mm});
            skLineSegment(sketch, "E1587", {"start": v(-35.56, 5.92) * mm, "end": v(-35.5, 5.84) * mm});
            skLineSegment(sketch, "E1588", {"start": v(-35.5, 5.84) * mm, "end": v(-35.43, 5.74) * mm});
            skLineSegment(sketch, "E1589", {"start": v(-35.43, 5.74) * mm, "end": v(-35.4, 5.7) * mm});
            skLineSegment(sketch, "E1590", {"start": v(-35.4, 5.7) * mm, "end": v(-35.4, 5.67) * mm});
            skLineSegment(sketch, "E1591", {"start": v(-35.4, 5.67) * mm, "end": v(-35.36, 5.62) * mm});
            skLineSegment(sketch, "E1592", {"start": v(-35.36, 5.62) * mm, "end": v(-35.27, 5.53) * mm});
            skLineSegment(sketch, "E1593", {"start": v(-35.27, 5.53) * mm, "end": v(-35.08, 5.35) * mm});
            skLineSegment(sketch, "E1594", {"start": v(-35.08, 5.35) * mm, "end": v(-35.03, 5.3) * mm});
            skLineSegment(sketch, "E1595", {"start": v(-35.03, 5.3) * mm, "end": v(-34.98, 5.28) * mm});
            skLineSegment(sketch, "E1596", {"start": v(-34.98, 5.28) * mm, "end": v(-34.96, 5.28) * mm});
            skLineSegment(sketch, "E1597", {"start": v(-34.96, 5.28) * mm, "end": v(-34.95, 5.26) * mm});
            skLineSegment(sketch, "E1598", {"start": v(-34.95, 5.26) * mm, "end": v(-34.92, 5.24) * mm});
            skLineSegment(sketch, "E1599", {"start": v(-34.92, 5.24) * mm, "end": v(-34.86, 5.2) * mm});
            skLineSegment(sketch, "E1600", {"start": v(-34.86, 5.2) * mm, "end": v(-34.58, 5.08) * mm});
            skLineSegment(sketch, "E1601", {"start": v(-34.58, 5.08) * mm, "end": v(-34.46, 5.03) * mm});
            skLineSegment(sketch, "E1602", {"start": v(-34.46, 5.03) * mm, "end": v(-34.32, 5) * mm});
            skLineSegment(sketch, "E1603", {"start": v(-34.32, 5) * mm, "end": v(-34.16, 4.98) * mm});
            skLineSegment(sketch, "E1604", {"start": v(-34.16, 4.98) * mm, "end": v(-34, 4.98) * mm});
            skLineSegment(sketch, "E1605", {"start": v(-34, 4.98) * mm, "end": v(-33.83, 4.98) * mm});
            skLineSegment(sketch, "E1606", {"start": v(-33.83, 4.98) * mm, "end": v(-33.67, 5) * mm});
            skLineSegment(sketch, "E1607", {"start": v(-33.67, 5) * mm, "end": v(-33.52, 5.03) * mm});
            skLineSegment(sketch, "E1608", {"start": v(-33.52, 5.03) * mm, "end": v(-33.4, 5.07) * mm});
            skLineSegment(sketch, "E1609", {"start": v(-33.4, 5.07) * mm, "end": v(-33.1, 5.2) * mm});
            skLineSegment(sketch, "E1610", {"start": v(-33.1, 5.2) * mm, "end": v(-33.04, 5.24) * mm});
            skLineSegment(sketch, "E1611", {"start": v(-33.04, 5.24) * mm, "end": v(-33.02, 5.26) * mm});
            skLineSegment(sketch, "E1612", {"start": v(-33.02, 5.26) * mm, "end": v(-33.01, 5.28) * mm});
            skLineSegment(sketch, "E1613", {"start": v(-33.01, 5.28) * mm, "end": v(-33, 5.28) * mm});
            skLineSegment(sketch, "E1614", {"start": v(-33, 5.28) * mm, "end": v(-32.96, 5.3) * mm});
            skLineSegment(sketch, "E1615", {"start": v(-32.96, 5.3) * mm, "end": v(-32.9, 5.34) * mm});
            skLineSegment(sketch, "E1616", {"start": v(-32.9, 5.34) * mm, "end": v(-32.76, 5.46) * mm});
            skLineSegment(sketch, "E1617", {"start": v(-32.76, 5.46) * mm, "end": v(-32.63, 5.6) * mm});
            skLineSegment(sketch, "E1618", {"start": v(-32.63, 5.6) * mm, "end": v(-32.6, 5.64) * mm});
            skLineSegment(sketch, "E1619", {"start": v(-32.6, 5.64) * mm, "end": v(-32.57, 5.67) * mm});
            skLineSegment(sketch, "E1620", {"start": v(-32.57, 5.67) * mm, "end": v(-32.56, 5.7) * mm});
            skLineSegment(sketch, "E1621", {"start": v(-32.56, 5.7) * mm, "end": v(-32.54, 5.74) * mm});
            skLineSegment(sketch, "E1622", {"start": v(-32.54, 5.74) * mm, "end": v(-32.47, 5.83) * mm});
            skLineSegment(sketch, "E1623", {"start": v(-32.47, 5.83) * mm, "end": v(-32.43, 5.89) * mm});
            skLineSegment(sketch, "E1624", {"start": v(-32.43, 5.89) * mm, "end": v(-32.39, 5.98) * mm});
            skLineSegment(sketch, "E1625", {"start": v(-32.39, 5.98) * mm, "end": v(-32.25, 6.38) * mm});
            skLineSegment(sketch, "E1626", {"start": v(-32.25, 6.38) * mm, "end": v(-32.22, 6.49) * mm});
            skLineSegment(sketch, "E1627", {"start": v(-32.22, 6.49) * mm, "end": v(-32.22, 13.48) * mm});
            skLineSegment(sketch, "E1628", {"start": v(-32.22, 13.48) * mm, "end": v(-32.24, 13.55) * mm});
            skLineSegment(sketch, "E1629", {"start": v(-32.24, 13.55) * mm, "end": v(-32.33, 13.8) * mm});
            skLineSegment(sketch, "E1630", {"start": v(-32.33, 13.8) * mm, "end": v(-32.4, 13.96) * mm});
            skLineSegment(sketch, "E1631", {"start": v(-32.4, 13.96) * mm, "end": v(-32.48, 14.1) * mm});
            skLineSegment(sketch, "E1632", {"start": v(-32.48, 14.1) * mm, "end": v(-32.55, 14.21) * mm});
            skLineSegment(sketch, "E1633", {"start": v(-32.55, 14.21) * mm, "end": v(-32.57, 14.27) * mm});
            skLineSegment(sketch, "E1634", {"start": v(-32.57, 14.27) * mm, "end": v(-32.6, 14.3) * mm});
            skLineSegment(sketch, "E1635", {"start": v(-32.6, 14.3) * mm, "end": v(-32.68, 14.39) * mm});
            skLineSegment(sketch, "E1636", {"start": v(-32.68, 14.39) * mm, "end": v(-32.93, 14.62) * mm});
            skLineSegment(sketch, "E1637", {"start": v(-32.93, 14.62) * mm, "end": v(-33.05, 14.7) * mm});
            skLineSegment(sketch, "E1638", {"start": v(-33.05, 14.7) * mm, "end": v(-33.2, 14.78) * mm});
            skLineSegment(sketch, "E1639", {"start": v(-33.2, 14.78) * mm, "end": v(-33.37, 14.85) * mm});
            skLineSegment(sketch, "E1640", {"start": v(-33.37, 14.85) * mm, "end": v(-33.53, 14.9) * mm});
            skLineSegment(sketch, "E1641", {"start": v(-33.53, 14.9) * mm, "end": v(-33.6, 14.92) * mm});
            skLineSegment(sketch, "E1642", {"start": v(-33.6, 14.92) * mm, "end": v(-33.72, 14.93) * mm});
            skLineSegment(sketch, "E1643", {"start": v(-33.72, 14.93) * mm, "end": v(-33.99, 14.94) * mm});
            skLineSegment(sketch, "E1644", {"start": v(-33.99, 14.94) * mm, "end": v(-34.25, 14.93) * mm});
            skLineSegment(sketch, "E1645", {"start": v(-34.25, 14.93) * mm, "end": v(-34.36, 14.92) * mm});
            skLineSegment(sketch, "E1646", {"start": v(-34.36, 14.92) * mm, "end": v(-34.45, 14.9) * mm});
            skLineSegment(sketch, "E1647", {"start": v(-34.45, 14.9) * mm, "end": v(-34.64, 14.84) * mm});
            skLineSegment(sketch, "E1648", {"start": v(-34.64, 14.84) * mm, "end": v(-34.84, 14.74) * mm});
            skLineSegment(sketch, "E1649", {"start": v(-34.84, 14.74) * mm, "end": v(-35.03, 14.62) * mm});
            skLineSegment(sketch, "E1650", {"start": v(-35.03, 14.62) * mm, "end": v(-35.2, 14.48) * mm});
            skLineSegment(sketch, "E1651", {"start": v(-35.2, 14.48) * mm, "end": v(-35.4, 14.3) * mm});
            skLineSegment(sketch, "E1652", {"start": v(-35.4, 14.3) * mm, "end": v(-35.4, 14.27) * mm});
            skLineSegment(sketch, "E1653", {"start": v(-35.4, 14.27) * mm, "end": v(-35.43, 14.21) * mm});
            skLineSegment(sketch, "E1654", {"start": v(-35.43, 14.21) * mm, "end": v(-35.5, 14.1) * mm});
            skLineSegment(sketch, "E1655", {"start": v(-35.5, 14.1) * mm, "end": v(-35.58, 13.96) * mm});
            skLineSegment(sketch, "E1656", {"start": v(-35.58, 13.96) * mm, "end": v(-35.65, 13.8) * mm});
            skLineSegment(sketch, "E1657", {"start": v(-35.65, 13.8) * mm, "end": v(-35.73, 13.55) * mm});
            skLineSegment(sketch, "E1658", {"start": v(-35.73, 13.55) * mm, "end": v(-35.75, 13.48) * mm});
            skLineSegment(sketch, "E1659", {"start": v(-35.75, 13.48) * mm, "end": v(-35.75, 6.46) * mm});
            skLineSegment(sketch, "E1660", {"start": v(-35.5, 30.48) * mm, "end": v(-32.5, 30.48) * mm});
            skLineSegment(sketch, "E1661", {"start": v(-32.5, 30.48) * mm, "end": v(-32.5, 32.48) * mm});
            skLineSegment(sketch, "E1662", {"start": v(-32.5, 32.48) * mm, "end": v(-35.5, 32.48) * mm});
            skLineSegment(sketch, "E1663", {"start": v(-35.5, 32.48) * mm, "end": v(-35.5, 30.48) * mm});
            skLineSegment(sketch, "E1664", {"start": v(-24.5, 30.48) * mm, "end": v(-24.5, 1) * mm});
            skLineSegment(sketch, "E1665", {"start": v(-24.5, 1) * mm, "end": v(-9.5, 1) * mm});
            skLineSegment(sketch, "E1666", {"start": v(-9.5, 1) * mm, "end": v(-9.5, 30.48) * mm});
            skLineSegment(sketch, "E1667", {"start": v(-9.5, 30.48) * mm, "end": v(-24.5, 30.48) * mm});
            skArc(sketch, "E1668", {"start": v(-12.49, 25.47) * mm, "mid": v(-12.85, 26.35) * mm, "end": v(-13.74, 26.72) * mm});
            skArc(sketch, "E1669", {"start": v(-13.74, 26.72) * mm, "mid": v(-14.62, 26.35) * mm, "end": v(-14.99, 25.47) * mm});
            skArc(sketch, "E1670", {"start": v(-14.99, 25.47) * mm, "mid": v(-14.62, 24.58) * mm, "end": v(-13.74, 24.22) * mm});
            skArc(sketch, "E1671", {"start": v(-13.74, 24.22) * mm, "mid": v(-12.85, 24.58) * mm, "end": v(-12.49, 25.47) * mm});
            skArc(sketch, "E1672", {"start": v(-18.99, 25.47) * mm, "mid": v(-19.35, 26.35) * mm, "end": v(-20.24, 26.72) * mm});
            skArc(sketch, "E1673", {"start": v(-20.24, 26.72) * mm, "mid": v(-21.12, 26.35) * mm, "end": v(-21.49, 25.47) * mm});
            skArc(sketch, "E1674", {"start": v(-21.49, 25.47) * mm, "mid": v(-21.12, 24.58) * mm, "end": v(-20.24, 24.22) * mm});
            skArc(sketch, "E1675", {"start": v(-20.24, 24.22) * mm, "mid": v(-19.35, 24.58) * mm, "end": v(-18.99, 25.47) * mm});
            skArc(sketch, "E1676", {"start": v(-11.24, 25.47) * mm, "mid": v(-11.97, 27.23) * mm, "end": v(-13.74, 27.97) * mm});
            skArc(sketch, "E1677", {"start": v(-13.74, 27.97) * mm, "mid": v(-15.5, 27.23) * mm, "end": v(-16.24, 25.47) * mm});
            skArc(sketch, "E1678", {"start": v(-16.24, 25.47) * mm, "mid": v(-15.5, 23.7) * mm, "end": v(-13.74, 22.97) * mm});
            skArc(sketch, "E1679", {"start": v(-13.74, 22.97) * mm, "mid": v(-11.97, 23.7) * mm, "end": v(-11.24, 25.47) * mm});
            skArc(sketch, "E1680", {"start": v(-17.74, 25.47) * mm, "mid": v(-18.47, 27.23) * mm, "end": v(-20.24, 27.97) * mm});
            skArc(sketch, "E1681", {"start": v(-20.24, 27.97) * mm, "mid": v(-22, 27.23) * mm, "end": v(-22.74, 25.47) * mm});
            skArc(sketch, "E1682", {"start": v(-22.74, 25.47) * mm, "mid": v(-22, 23.7) * mm, "end": v(-20.24, 22.97) * mm});
            skArc(sketch, "E1683", {"start": v(-20.24, 22.97) * mm, "mid": v(-18.47, 23.7) * mm, "end": v(-17.74, 25.47) * mm});
            skLineSegment(sketch, "E1684", {"start": v(-26.5, 17.24) * mm, "end": v(-26.5, 14.24) * mm});
            skLineSegment(sketch, "E1685", {"start": v(-26.5, 14.24) * mm, "end": v(-24.5, 14.24) * mm});
            skLineSegment(sketch, "E1686", {"start": v(-24.5, 14.24) * mm, "end": v(-24.5, 17.24) * mm});
            skLineSegment(sketch, "E1687", {"start": v(-24.5, 17.24) * mm, "end": v(-26.5, 17.24) * mm});
            skLineSegment(sketch, "E1688", {"start": v(-18.75, 6.46) * mm, "end": v(-18.73, 6.4) * mm});
            skLineSegment(sketch, "E1689", {"start": v(-18.73, 6.4) * mm, "end": v(-18.65, 6.16) * mm});
            skLineSegment(sketch, "E1690", {"start": v(-18.65, 6.16) * mm, "end": v(-18.6, 6.02) * mm});
            skLineSegment(sketch, "E1691", {"start": v(-18.6, 6.02) * mm, "end": v(-18.56, 5.92) * mm});
            skLineSegment(sketch, "E1692", {"start": v(-18.56, 5.92) * mm, "end": v(-18.5, 5.84) * mm});
            skLineSegment(sketch, "E1693", {"start": v(-18.5, 5.84) * mm, "end": v(-18.43, 5.74) * mm});
            skLineSegment(sketch, "E1694", {"start": v(-18.43, 5.74) * mm, "end": v(-18.4, 5.7) * mm});
            skLineSegment(sketch, "E1695", {"start": v(-18.4, 5.7) * mm, "end": v(-18.4, 5.67) * mm});
            skLineSegment(sketch, "E1696", {"start": v(-18.4, 5.67) * mm, "end": v(-18.36, 5.62) * mm});
            skLineSegment(sketch, "E1697", {"start": v(-18.36, 5.62) * mm, "end": v(-18.27, 5.53) * mm});
            skLineSegment(sketch, "E1698", {"start": v(-18.27, 5.53) * mm, "end": v(-18.08, 5.35) * mm});
            skLineSegment(sketch, "E1699", {"start": v(-18.08, 5.35) * mm, "end": v(-18.03, 5.3) * mm});
            skLineSegment(sketch, "E1700", {"start": v(-18.03, 5.3) * mm, "end": v(-17.98, 5.28) * mm});
            skLineSegment(sketch, "E1701", {"start": v(-17.98, 5.28) * mm, "end": v(-17.96, 5.28) * mm});
            skLineSegment(sketch, "E1702", {"start": v(-17.96, 5.28) * mm, "end": v(-17.95, 5.26) * mm});
            skLineSegment(sketch, "E1703", {"start": v(-17.95, 5.26) * mm, "end": v(-17.92, 5.24) * mm});
            skLineSegment(sketch, "E1704", {"start": v(-17.92, 5.24) * mm, "end": v(-17.86, 5.2) * mm});
            skLineSegment(sketch, "E1705", {"start": v(-17.86, 5.2) * mm, "end": v(-17.58, 5.08) * mm});
            skLineSegment(sketch, "E1706", {"start": v(-17.58, 5.08) * mm, "end": v(-17.46, 5.03) * mm});
            skLineSegment(sketch, "E1707", {"start": v(-17.46, 5.03) * mm, "end": v(-17.32, 5) * mm});
            skLineSegment(sketch, "E1708", {"start": v(-17.32, 5) * mm, "end": v(-17.16, 4.98) * mm});
            skLineSegment(sketch, "E1709", {"start": v(-17.16, 4.98) * mm, "end": v(-17, 4.98) * mm});
            skLineSegment(sketch, "E1710", {"start": v(-17, 4.98) * mm, "end": v(-16.83, 4.98) * mm});
            skLineSegment(sketch, "E1711", {"start": v(-16.83, 4.98) * mm, "end": v(-16.67, 5) * mm});
            skLineSegment(sketch, "E1712", {"start": v(-16.67, 5) * mm, "end": v(-16.52, 5.03) * mm});
            skLineSegment(sketch, "E1713", {"start": v(-16.52, 5.03) * mm, "end": v(-16.4, 5.07) * mm});
            skLineSegment(sketch, "E1714", {"start": v(-16.4, 5.07) * mm, "end": v(-16.1, 5.2) * mm});
            skLineSegment(sketch, "E1715", {"start": v(-16.1, 5.2) * mm, "end": v(-16.04, 5.24) * mm});
            skLineSegment(sketch, "E1716", {"start": v(-16.04, 5.24) * mm, "end": v(-16.02, 5.26) * mm});
            skLineSegment(sketch, "E1717", {"start": v(-16.02, 5.26) * mm, "end": v(-16.01, 5.28) * mm});
            skLineSegment(sketch, "E1718", {"start": v(-16.01, 5.28) * mm, "end": v(-16, 5.28) * mm});
            skLineSegment(sketch, "E1719", {"start": v(-16, 5.28) * mm, "end": v(-15.96, 5.3) * mm});
            skLineSegment(sketch, "E1720", {"start": v(-15.96, 5.3) * mm, "end": v(-15.9, 5.34) * mm});
            skLineSegment(sketch, "E1721", {"start": v(-15.9, 5.34) * mm, "end": v(-15.76, 5.46) * mm});
            skLineSegment(sketch, "E1722", {"start": v(-15.76, 5.46) * mm, "end": v(-15.63, 5.6) * mm});
            skLineSegment(sketch, "E1723", {"start": v(-15.63, 5.6) * mm, "end": v(-15.6, 5.64) * mm});
            skLineSegment(sketch, "E1724", {"start": v(-15.6, 5.64) * mm, "end": v(-15.57, 5.67) * mm});
            skLineSegment(sketch, "E1725", {"start": v(-15.57, 5.67) * mm, "end": v(-15.56, 5.7) * mm});
            skLineSegment(sketch, "E1726", {"start": v(-15.56, 5.7) * mm, "end": v(-15.54, 5.74) * mm});
            skLineSegment(sketch, "E1727", {"start": v(-15.54, 5.74) * mm, "end": v(-15.47, 5.83) * mm});
            skLineSegment(sketch, "E1728", {"start": v(-15.47, 5.83) * mm, "end": v(-15.43, 5.89) * mm});
            skLineSegment(sketch, "E1729", {"start": v(-15.43, 5.89) * mm, "end": v(-15.39, 5.98) * mm});
            skLineSegment(sketch, "E1730", {"start": v(-15.39, 5.98) * mm, "end": v(-15.25, 6.38) * mm});
            skLineSegment(sketch, "E1731", {"start": v(-15.25, 6.38) * mm, "end": v(-15.22, 6.49) * mm});
            skLineSegment(sketch, "E1732", {"start": v(-15.22, 6.49) * mm, "end": v(-15.22, 13.48) * mm});
            skLineSegment(sketch, "E1733", {"start": v(-15.22, 13.48) * mm, "end": v(-15.24, 13.55) * mm});
            skLineSegment(sketch, "E1734", {"start": v(-15.24, 13.55) * mm, "end": v(-15.33, 13.8) * mm});
            skLineSegment(sketch, "E1735", {"start": v(-15.33, 13.8) * mm, "end": v(-15.4, 13.96) * mm});
            skLineSegment(sketch, "E1736", {"start": v(-15.4, 13.96) * mm, "end": v(-15.48, 14.1) * mm});
            skLineSegment(sketch, "E1737", {"start": v(-15.48, 14.1) * mm, "end": v(-15.55, 14.21) * mm});
            skLineSegment(sketch, "E1738", {"start": v(-15.55, 14.21) * mm, "end": v(-15.57, 14.27) * mm});
            skLineSegment(sketch, "E1739", {"start": v(-15.57, 14.27) * mm, "end": v(-15.6, 14.3) * mm});
            skLineSegment(sketch, "E1740", {"start": v(-15.6, 14.3) * mm, "end": v(-15.68, 14.39) * mm});
            skLineSegment(sketch, "E1741", {"start": v(-15.68, 14.39) * mm, "end": v(-15.93, 14.62) * mm});
            skLineSegment(sketch, "E1742", {"start": v(-15.93, 14.62) * mm, "end": v(-16.05, 14.7) * mm});
            skLineSegment(sketch, "E1743", {"start": v(-16.05, 14.7) * mm, "end": v(-16.2, 14.78) * mm});
            skLineSegment(sketch, "E1744", {"start": v(-16.2, 14.78) * mm, "end": v(-16.37, 14.85) * mm});
            skLineSegment(sketch, "E1745", {"start": v(-16.37, 14.85) * mm, "end": v(-16.53, 14.9) * mm});
            skLineSegment(sketch, "E1746", {"start": v(-16.53, 14.9) * mm, "end": v(-16.6, 14.92) * mm});
            skLineSegment(sketch, "E1747", {"start": v(-16.6, 14.92) * mm, "end": v(-16.72, 14.93) * mm});
            skLineSegment(sketch, "E1748", {"start": v(-16.72, 14.93) * mm, "end": v(-16.99, 14.94) * mm});
            skLineSegment(sketch, "E1749", {"start": v(-16.99, 14.94) * mm, "end": v(-17.25, 14.93) * mm});
            skLineSegment(sketch, "E1750", {"start": v(-17.25, 14.93) * mm, "end": v(-17.36, 14.92) * mm});
            skLineSegment(sketch, "E1751", {"start": v(-17.36, 14.92) * mm, "end": v(-17.45, 14.9) * mm});
            skLineSegment(sketch, "E1752", {"start": v(-17.45, 14.9) * mm, "end": v(-17.64, 14.84) * mm});
            skLineSegment(sketch, "E1753", {"start": v(-17.64, 14.84) * mm, "end": v(-17.84, 14.74) * mm});
            skLineSegment(sketch, "E1754", {"start": v(-17.84, 14.74) * mm, "end": v(-18.03, 14.62) * mm});
            skLineSegment(sketch, "E1755", {"start": v(-18.03, 14.62) * mm, "end": v(-18.2, 14.48) * mm});
            skLineSegment(sketch, "E1756", {"start": v(-18.2, 14.48) * mm, "end": v(-18.4, 14.3) * mm});
            skLineSegment(sketch, "E1757", {"start": v(-18.4, 14.3) * mm, "end": v(-18.4, 14.27) * mm});
            skLineSegment(sketch, "E1758", {"start": v(-18.4, 14.27) * mm, "end": v(-18.43, 14.21) * mm});
            skLineSegment(sketch, "E1759", {"start": v(-18.43, 14.21) * mm, "end": v(-18.5, 14.1) * mm});
            skLineSegment(sketch, "E1760", {"start": v(-18.5, 14.1) * mm, "end": v(-18.58, 13.96) * mm});
            skLineSegment(sketch, "E1761", {"start": v(-18.58, 13.96) * mm, "end": v(-18.65, 13.8) * mm});
            skLineSegment(sketch, "E1762", {"start": v(-18.65, 13.8) * mm, "end": v(-18.73, 13.55) * mm});
            skLineSegment(sketch, "E1763", {"start": v(-18.73, 13.55) * mm, "end": v(-18.75, 13.48) * mm});
            skLineSegment(sketch, "E1764", {"start": v(-18.75, 13.48) * mm, "end": v(-18.75, 6.46) * mm});
            skLineSegment(sketch, "E1765", {"start": v(-18.5, 30.48) * mm, "end": v(-15.5, 30.48) * mm});
            skLineSegment(sketch, "E1766", {"start": v(-15.5, 30.48) * mm, "end": v(-15.5, 32.48) * mm});
            skLineSegment(sketch, "E1767", {"start": v(-15.5, 32.48) * mm, "end": v(-18.5, 32.48) * mm});
            skLineSegment(sketch, "E1768", {"start": v(-18.5, 32.48) * mm, "end": v(-18.5, 30.48) * mm});
            skLineSegment(sketch, "E1769", {"start": v(-7.5, 30.48) * mm, "end": v(-7.5, 1) * mm});
            skLineSegment(sketch, "E1770", {"start": v(-7.5, 1) * mm, "end": v(7.5, 1) * mm});
            skLineSegment(sketch, "E1771", {"start": v(7.5, 1) * mm, "end": v(7.5, 30.48) * mm});
            skLineSegment(sketch, "E1772", {"start": v(7.5, 30.48) * mm, "end": v(-7.5, 30.48) * mm});
            skArc(sketch, "E1773", {"start": v(4.51, 25.47) * mm, "mid": v(4.15, 26.35) * mm, "end": v(3.26, 26.72) * mm});
            skArc(sketch, "E1774", {"start": v(3.26, 26.72) * mm, "mid": v(2.38, 26.35) * mm, "end": v(2.01, 25.47) * mm});
            skArc(sketch, "E1775", {"start": v(2.01, 25.47) * mm, "mid": v(2.38, 24.58) * mm, "end": v(3.26, 24.22) * mm});
            skArc(sketch, "E1776", {"start": v(3.26, 24.22) * mm, "mid": v(4.15, 24.58) * mm, "end": v(4.51, 25.47) * mm});
            skArc(sketch, "E1777", {"start": v(-1.99, 25.47) * mm, "mid": v(-2.35, 26.35) * mm, "end": v(-3.24, 26.72) * mm});
            skArc(sketch, "E1778", {"start": v(-3.24, 26.72) * mm, "mid": v(-4.12, 26.35) * mm, "end": v(-4.49, 25.47) * mm});
            skArc(sketch, "E1779", {"start": v(-4.49, 25.47) * mm, "mid": v(-4.12, 24.58) * mm, "end": v(-3.24, 24.22) * mm});
            skArc(sketch, "E1780", {"start": v(-3.24, 24.22) * mm, "mid": v(-2.35, 24.58) * mm, "end": v(-1.99, 25.47) * mm});
            skArc(sketch, "E1781", {"start": v(5.76, 25.47) * mm, "mid": v(5.03, 27.23) * mm, "end": v(3.26, 27.97) * mm});
            skArc(sketch, "E1782", {"start": v(3.26, 27.97) * mm, "mid": v(1.5, 27.23) * mm, "end": v(0.76, 25.47) * mm});
            skArc(sketch, "E1783", {"start": v(0.76, 25.47) * mm, "mid": v(1.5, 23.7) * mm, "end": v(3.26, 22.97) * mm});
            skArc(sketch, "E1784", {"start": v(3.26, 22.97) * mm, "mid": v(5.03, 23.7) * mm, "end": v(5.76, 25.47) * mm});
            skArc(sketch, "E1785", {"start": v(-0.74, 25.47) * mm, "mid": v(-1.47, 27.23) * mm, "end": v(-3.24, 27.97) * mm});
            skArc(sketch, "E1786", {"start": v(-3.24, 27.97) * mm, "mid": v(-5, 27.23) * mm, "end": v(-5.74, 25.47) * mm});
            skArc(sketch, "E1787", {"start": v(-5.74, 25.47) * mm, "mid": v(-5, 23.7) * mm, "end": v(-3.24, 22.97) * mm});
            skArc(sketch, "E1788", {"start": v(-3.24, 22.97) * mm, "mid": v(-1.47, 23.7) * mm, "end": v(-0.74, 25.47) * mm});
            skLineSegment(sketch, "E1789", {"start": v(-9.5, 17.24) * mm, "end": v(-9.5, 14.24) * mm});
            skLineSegment(sketch, "E1790", {"start": v(-9.5, 14.24) * mm, "end": v(-7.5, 14.24) * mm});
            skLineSegment(sketch, "E1791", {"start": v(-7.5, 14.24) * mm, "end": v(-7.5, 17.24) * mm});
            skLineSegment(sketch, "E1792", {"start": v(-7.5, 17.24) * mm, "end": v(-9.5, 17.24) * mm});
            skLineSegment(sketch, "E1793", {"start": v(-1.75, 6.46) * mm, "end": v(-1.73, 6.4) * mm});
            skLineSegment(sketch, "E1794", {"start": v(-1.73, 6.4) * mm, "end": v(-1.65, 6.16) * mm});
            skLineSegment(sketch, "E1795", {"start": v(-1.65, 6.16) * mm, "end": v(-1.6, 6.02) * mm});
            skLineSegment(sketch, "E1796", {"start": v(-1.6, 6.02) * mm, "end": v(-1.56, 5.92) * mm});
            skLineSegment(sketch, "E1797", {"start": v(-1.56, 5.92) * mm, "end": v(-1.5, 5.84) * mm});
            skLineSegment(sketch, "E1798", {"start": v(-1.5, 5.84) * mm, "end": v(-1.43, 5.74) * mm});
            skLineSegment(sketch, "E1799", {"start": v(-1.43, 5.74) * mm, "end": v(-1.4, 5.7) * mm});
            skLineSegment(sketch, "E1800", {"start": v(-1.4, 5.7) * mm, "end": v(-1.4, 5.67) * mm});
            skLineSegment(sketch, "E1801", {"start": v(-1.4, 5.67) * mm, "end": v(-1.36, 5.62) * mm});
            skLineSegment(sketch, "E1802", {"start": v(-1.36, 5.62) * mm, "end": v(-1.27, 5.53) * mm});
            skLineSegment(sketch, "E1803", {"start": v(-1.27, 5.53) * mm, "end": v(-1.08, 5.35) * mm});
            skLineSegment(sketch, "E1804", {"start": v(-1.08, 5.35) * mm, "end": v(-1.03, 5.3) * mm});
            skLineSegment(sketch, "E1805", {"start": v(-1.03, 5.3) * mm, "end": v(-0.98, 5.28) * mm});
            skLineSegment(sketch, "E1806", {"start": v(-0.98, 5.28) * mm, "end": v(-0.96, 5.28) * mm});
            skLineSegment(sketch, "E1807", {"start": v(-0.96, 5.28) * mm, "end": v(-0.95, 5.26) * mm});
            skLineSegment(sketch, "E1808", {"start": v(-0.95, 5.26) * mm, "end": v(-0.92, 5.24) * mm});
            skLineSegment(sketch, "E1809", {"start": v(-0.92, 5.24) * mm, "end": v(-0.86, 5.2) * mm});
            skLineSegment(sketch, "E1810", {"start": v(-0.86, 5.2) * mm, "end": v(-0.58, 5.08) * mm});
            skLineSegment(sketch, "E1811", {"start": v(-0.58, 5.08) * mm, "end": v(-0.46, 5.03) * mm});
            skLineSegment(sketch, "E1812", {"start": v(-0.46, 5.03) * mm, "end": v(-0.32, 5) * mm});
            skLineSegment(sketch, "E1813", {"start": v(-0.32, 5) * mm, "end": v(-0.16, 4.98) * mm});
            skLineSegment(sketch, "E1814", {"start": v(-0.16, 4.98) * mm, "end": v(0, 4.98) * mm});
            skLineSegment(sketch, "E1815", {"start": v(0, 4.98) * mm, "end": v(0.17, 4.98) * mm});
            skLineSegment(sketch, "E1816", {"start": v(0.17, 4.98) * mm, "end": v(0.33, 5) * mm});
            skLineSegment(sketch, "E1817", {"start": v(0.33, 5) * mm, "end": v(0.48, 5.03) * mm});
            skLineSegment(sketch, "E1818", {"start": v(0.48, 5.03) * mm, "end": v(0.6, 5.07) * mm});
            skLineSegment(sketch, "E1819", {"start": v(0.6, 5.07) * mm, "end": v(0.9, 5.2) * mm});
            skLineSegment(sketch, "E1820", {"start": v(0.9, 5.2) * mm, "end": v(0.96, 5.24) * mm});
            skLineSegment(sketch, "E1821", {"start": v(0.96, 5.24) * mm, "end": v(0.98, 5.26) * mm});
            skLineSegment(sketch, "E1822", {"start": v(0.98, 5.26) * mm, "end": v(0.99, 5.28) * mm});
            skLineSegment(sketch, "E1823", {"start": v(0.99, 5.28) * mm, "end": v(1, 5.28) * mm});
            skLineSegment(sketch, "E1824", {"start": v(1, 5.28) * mm, "end": v(1.04, 5.3) * mm});
            skLineSegment(sketch, "E1825", {"start": v(1.04, 5.3) * mm, "end": v(1.1, 5.34) * mm});
            skLineSegment(sketch, "E1826", {"start": v(1.1, 5.34) * mm, "end": v(1.24, 5.46) * mm});
            skLineSegment(sketch, "E1827", {"start": v(1.24, 5.46) * mm, "end": v(1.37, 5.6) * mm});
            skLineSegment(sketch, "E1828", {"start": v(1.37, 5.6) * mm, "end": v(1.4, 5.64) * mm});
            skLineSegment(sketch, "E1829", {"start": v(1.4, 5.64) * mm, "end": v(1.43, 5.67) * mm});
            skLineSegment(sketch, "E1830", {"start": v(1.43, 5.67) * mm, "end": v(1.44, 5.7) * mm});
            skLineSegment(sketch, "E1831", {"start": v(1.44, 5.7) * mm, "end": v(1.46, 5.74) * mm});
            skLineSegment(sketch, "E1832", {"start": v(1.46, 5.74) * mm, "end": v(1.53, 5.83) * mm});
            skLineSegment(sketch, "E1833", {"start": v(1.53, 5.83) * mm, "end": v(1.57, 5.89) * mm});
            skLineSegment(sketch, "E1834", {"start": v(1.57, 5.89) * mm, "end": v(1.61, 5.98) * mm});
            skLineSegment(sketch, "E1835", {"start": v(1.61, 5.98) * mm, "end": v(1.75, 6.38) * mm});
            skLineSegment(sketch, "E1836", {"start": v(1.75, 6.38) * mm, "end": v(1.78, 6.49) * mm});
            skLineSegment(sketch, "E1837", {"start": v(1.78, 6.49) * mm, "end": v(1.78, 13.48) * mm});
            skLineSegment(sketch, "E1838", {"start": v(1.78, 13.48) * mm, "end": v(1.76, 13.55) * mm});
            skLineSegment(sketch, "E1839", {"start": v(1.76, 13.55) * mm, "end": v(1.67, 13.8) * mm});
            skLineSegment(sketch, "E1840", {"start": v(1.67, 13.8) * mm, "end": v(1.6, 13.96) * mm});
            skLineSegment(sketch, "E1841", {"start": v(1.6, 13.96) * mm, "end": v(1.52, 14.1) * mm});
            skLineSegment(sketch, "E1842", {"start": v(1.52, 14.1) * mm, "end": v(1.45, 14.21) * mm});
            skLineSegment(sketch, "E1843", {"start": v(1.45, 14.21) * mm, "end": v(1.43, 14.27) * mm});
            skLineSegment(sketch, "E1844", {"start": v(1.43, 14.27) * mm, "end": v(1.4, 14.3) * mm});
            skLineSegment(sketch, "E1845", {"start": v(1.4, 14.3) * mm, "end": v(1.32, 14.39) * mm});
            skLineSegment(sketch, "E1846", {"start": v(1.32, 14.39) * mm, "end": v(1.07, 14.62) * mm});
            skLineSegment(sketch, "E1847", {"start": v(1.07, 14.62) * mm, "end": v(0.95, 14.7) * mm});
            skLineSegment(sketch, "E1848", {"start": v(0.95, 14.7) * mm, "end": v(0.8, 14.78) * mm});
            skLineSegment(sketch, "E1849", {"start": v(0.8, 14.78) * mm, "end": v(0.63, 14.85) * mm});
            skLineSegment(sketch, "E1850", {"start": v(0.63, 14.85) * mm, "end": v(0.47, 14.9) * mm});
            skLineSegment(sketch, "E1851", {"start": v(0.47, 14.9) * mm, "end": v(0.4, 14.92) * mm});
            skLineSegment(sketch, "E1852", {"start": v(0.4, 14.92) * mm, "end": v(0.28, 14.93) * mm});
            skLineSegment(sketch, "E1853", {"start": v(0.28, 14.93) * mm, "end": v(0.01, 14.94) * mm});
            skLineSegment(sketch, "E1854", {"start": v(0.01, 14.94) * mm, "end": v(-0.25, 14.93) * mm});
            skLineSegment(sketch, "E1855", {"start": v(-0.25, 14.93) * mm, "end": v(-0.36, 14.92) * mm});
            skLineSegment(sketch, "E1856", {"start": v(-0.36, 14.92) * mm, "end": v(-0.45, 14.9) * mm});
            skLineSegment(sketch, "E1857", {"start": v(-0.45, 14.9) * mm, "end": v(-0.64, 14.84) * mm});
            skLineSegment(sketch, "E1858", {"start": v(-0.64, 14.84) * mm, "end": v(-0.84, 14.74) * mm});
            skLineSegment(sketch, "E1859", {"start": v(-0.84, 14.74) * mm, "end": v(-1.03, 14.62) * mm});
            skLineSegment(sketch, "E1860", {"start": v(-1.03, 14.62) * mm, "end": v(-1.2, 14.48) * mm});
            skLineSegment(sketch, "E1861", {"start": v(-1.2, 14.48) * mm, "end": v(-1.4, 14.3) * mm});
            skLineSegment(sketch, "E1862", {"start": v(-1.4, 14.3) * mm, "end": v(-1.4, 14.27) * mm});
            skLineSegment(sketch, "E1863", {"start": v(-1.4, 14.27) * mm, "end": v(-1.43, 14.21) * mm});
            skLineSegment(sketch, "E1864", {"start": v(-1.43, 14.21) * mm, "end": v(-1.5, 14.1) * mm});
            skLineSegment(sketch, "E1865", {"start": v(-1.5, 14.1) * mm, "end": v(-1.58, 13.96) * mm});
            skLineSegment(sketch, "E1866", {"start": v(-1.58, 13.96) * mm, "end": v(-1.65, 13.8) * mm});
            skLineSegment(sketch, "E1867", {"start": v(-1.65, 13.8) * mm, "end": v(-1.73, 13.55) * mm});
            skLineSegment(sketch, "E1868", {"start": v(-1.73, 13.55) * mm, "end": v(-1.75, 13.48) * mm});
            skLineSegment(sketch, "E1869", {"start": v(-1.75, 13.48) * mm, "end": v(-1.75, 6.46) * mm});
            skLineSegment(sketch, "E1870", {"start": v(-1.5, 30.48) * mm, "end": v(1.5, 30.48) * mm});
            skLineSegment(sketch, "E1871", {"start": v(1.5, 30.48) * mm, "end": v(1.5, 32.48) * mm});
            skLineSegment(sketch, "E1872", {"start": v(1.5, 32.48) * mm, "end": v(-1.5, 32.48) * mm});
            skLineSegment(sketch, "E1873", {"start": v(-1.5, 32.48) * mm, "end": v(-1.5, 30.48) * mm});
            skLineSegment(sketch, "E1874", {"start": v(9.5, 30.48) * mm, "end": v(9.5, 1) * mm});
            skLineSegment(sketch, "E1875", {"start": v(9.5, 1) * mm, "end": v(24.5, 1) * mm});
            skLineSegment(sketch, "E1876", {"start": v(24.5, 1) * mm, "end": v(24.5, 30.48) * mm});
            skLineSegment(sketch, "E1877", {"start": v(24.5, 30.48) * mm, "end": v(9.5, 30.48) * mm});
            skArc(sketch, "E1878", {"start": v(21.51, 25.47) * mm, "mid": v(21.15, 26.35) * mm, "end": v(20.26, 26.72) * mm});
            skArc(sketch, "E1879", {"start": v(20.26, 26.72) * mm, "mid": v(19.38, 26.35) * mm, "end": v(19.01, 25.47) * mm});
            skArc(sketch, "E1880", {"start": v(19.01, 25.47) * mm, "mid": v(19.38, 24.58) * mm, "end": v(20.26, 24.22) * mm});
            skArc(sketch, "E1881", {"start": v(20.26, 24.22) * mm, "mid": v(21.15, 24.58) * mm, "end": v(21.51, 25.47) * mm});
            skArc(sketch, "E1882", {"start": v(15.01, 25.47) * mm, "mid": v(14.65, 26.35) * mm, "end": v(13.76, 26.72) * mm});
            skArc(sketch, "E1883", {"start": v(13.76, 26.72) * mm, "mid": v(12.88, 26.35) * mm, "end": v(12.51, 25.47) * mm});
            skArc(sketch, "E1884", {"start": v(12.51, 25.47) * mm, "mid": v(12.88, 24.58) * mm, "end": v(13.76, 24.22) * mm});
            skArc(sketch, "E1885", {"start": v(13.76, 24.22) * mm, "mid": v(14.65, 24.58) * mm, "end": v(15.01, 25.47) * mm});
            skArc(sketch, "E1886", {"start": v(22.76, 25.47) * mm, "mid": v(22.03, 27.23) * mm, "end": v(20.26, 27.97) * mm});
            skArc(sketch, "E1887", {"start": v(20.26, 27.97) * mm, "mid": v(18.5, 27.23) * mm, "end": v(17.76, 25.47) * mm});
            skArc(sketch, "E1888", {"start": v(17.76, 25.47) * mm, "mid": v(18.5, 23.7) * mm, "end": v(20.26, 22.97) * mm});
            skArc(sketch, "E1889", {"start": v(20.26, 22.97) * mm, "mid": v(22.03, 23.7) * mm, "end": v(22.76, 25.47) * mm});
            skArc(sketch, "E1890", {"start": v(16.26, 25.47) * mm, "mid": v(15.53, 27.23) * mm, "end": v(13.76, 27.97) * mm});
            skArc(sketch, "E1891", {"start": v(13.76, 27.97) * mm, "mid": v(12, 27.23) * mm, "end": v(11.26, 25.47) * mm});
            skArc(sketch, "E1892", {"start": v(11.26, 25.47) * mm, "mid": v(12, 23.7) * mm, "end": v(13.76, 22.97) * mm});
            skArc(sketch, "E1893", {"start": v(13.76, 22.97) * mm, "mid": v(15.53, 23.7) * mm, "end": v(16.26, 25.47) * mm});
            skLineSegment(sketch, "E1894", {"start": v(7.5, 17.24) * mm, "end": v(7.5, 14.24) * mm});
            skLineSegment(sketch, "E1895", {"start": v(7.5, 14.24) * mm, "end": v(9.5, 14.24) * mm});
            skLineSegment(sketch, "E1896", {"start": v(9.5, 14.24) * mm, "end": v(9.5, 17.24) * mm});
            skLineSegment(sketch, "E1897", {"start": v(9.5, 17.24) * mm, "end": v(7.5, 17.24) * mm});
            skLineSegment(sketch, "E1898", {"start": v(15.25, 6.46) * mm, "end": v(15.27, 6.4) * mm});
            skLineSegment(sketch, "E1899", {"start": v(15.27, 6.4) * mm, "end": v(15.35, 6.16) * mm});
            skLineSegment(sketch, "E1900", {"start": v(15.35, 6.16) * mm, "end": v(15.4, 6.02) * mm});
            skLineSegment(sketch, "E1901", {"start": v(15.4, 6.02) * mm, "end": v(15.44, 5.92) * mm});
            skLineSegment(sketch, "E1902", {"start": v(15.44, 5.92) * mm, "end": v(15.5, 5.84) * mm});
            skLineSegment(sketch, "E1903", {"start": v(15.5, 5.84) * mm, "end": v(15.57, 5.74) * mm});
            skLineSegment(sketch, "E1904", {"start": v(15.57, 5.74) * mm, "end": v(15.6, 5.7) * mm});
            skLineSegment(sketch, "E1905", {"start": v(15.6, 5.7) * mm, "end": v(15.6, 5.67) * mm});
            skLineSegment(sketch, "E1906", {"start": v(15.6, 5.67) * mm, "end": v(15.64, 5.62) * mm});
            skLineSegment(sketch, "E1907", {"start": v(15.64, 5.62) * mm, "end": v(15.73, 5.53) * mm});
            skLineSegment(sketch, "E1908", {"start": v(15.73, 5.53) * mm, "end": v(15.92, 5.35) * mm});
            skLineSegment(sketch, "E1909", {"start": v(15.92, 5.35) * mm, "end": v(15.97, 5.3) * mm});
            skLineSegment(sketch, "E1910", {"start": v(15.97, 5.3) * mm, "end": v(16.02, 5.28) * mm});
            skLineSegment(sketch, "E1911", {"start": v(16.02, 5.28) * mm, "end": v(16.04, 5.28) * mm});
            skLineSegment(sketch, "E1912", {"start": v(16.04, 5.28) * mm, "end": v(16.05, 5.26) * mm});
            skLineSegment(sketch, "E1913", {"start": v(16.05, 5.26) * mm, "end": v(16.08, 5.24) * mm});
            skLineSegment(sketch, "E1914", {"start": v(16.08, 5.24) * mm, "end": v(16.14, 5.2) * mm});
            skLineSegment(sketch, "E1915", {"start": v(16.14, 5.2) * mm, "end": v(16.42, 5.08) * mm});
            skLineSegment(sketch, "E1916", {"start": v(16.42, 5.08) * mm, "end": v(16.54, 5.03) * mm});
            skLineSegment(sketch, "E1917", {"start": v(16.54, 5.03) * mm, "end": v(16.68, 5) * mm});
            skLineSegment(sketch, "E1918", {"start": v(16.68, 5) * mm, "end": v(16.84, 4.98) * mm});
            skLineSegment(sketch, "E1919", {"start": v(16.84, 4.98) * mm, "end": v(17, 4.98) * mm});
            skLineSegment(sketch, "E1920", {"start": v(17, 4.98) * mm, "end": v(17.17, 4.98) * mm});
            skLineSegment(sketch, "E1921", {"start": v(17.17, 4.98) * mm, "end": v(17.33, 5) * mm});
            skLineSegment(sketch, "E1922", {"start": v(17.33, 5) * mm, "end": v(17.48, 5.03) * mm});
            skLineSegment(sketch, "E1923", {"start": v(17.48, 5.03) * mm, "end": v(17.6, 5.07) * mm});
            skLineSegment(sketch, "E1924", {"start": v(17.6, 5.07) * mm, "end": v(17.9, 5.2) * mm});
            skLineSegment(sketch, "E1925", {"start": v(17.9, 5.2) * mm, "end": v(17.96, 5.24) * mm});
            skLineSegment(sketch, "E1926", {"start": v(17.96, 5.24) * mm, "end": v(17.98, 5.26) * mm});
            skLineSegment(sketch, "E1927", {"start": v(17.98, 5.26) * mm, "end": v(17.99, 5.28) * mm});
            skLineSegment(sketch, "E1928", {"start": v(17.99, 5.28) * mm, "end": v(18, 5.28) * mm});
            skLineSegment(sketch, "E1929", {"start": v(18, 5.28) * mm, "end": v(18.04, 5.3) * mm});
            skLineSegment(sketch, "E1930", {"start": v(18.04, 5.3) * mm, "end": v(18.1, 5.34) * mm});
            skLineSegment(sketch, "E1931", {"start": v(18.1, 5.34) * mm, "end": v(18.24, 5.46) * mm});
            skLineSegment(sketch, "E1932", {"start": v(18.24, 5.46) * mm, "end": v(18.37, 5.6) * mm});
            skLineSegment(sketch, "E1933", {"start": v(18.37, 5.6) * mm, "end": v(18.4, 5.64) * mm});
            skLineSegment(sketch, "E1934", {"start": v(18.4, 5.64) * mm, "end": v(18.43, 5.67) * mm});
            skLineSegment(sketch, "E1935", {"start": v(18.43, 5.67) * mm, "end": v(18.44, 5.7) * mm});
            skLineSegment(sketch, "E1936", {"start": v(18.44, 5.7) * mm, "end": v(18.46, 5.74) * mm});
            skLineSegment(sketch, "E1937", {"start": v(18.46, 5.74) * mm, "end": v(18.53, 5.83) * mm});
            skLineSegment(sketch, "E1938", {"start": v(18.53, 5.83) * mm, "end": v(18.57, 5.89) * mm});
            skLineSegment(sketch, "E1939", {"start": v(18.57, 5.89) * mm, "end": v(18.61, 5.98) * mm});
            skLineSegment(sketch, "E1940", {"start": v(18.61, 5.98) * mm, "end": v(18.75, 6.38) * mm});
            skLineSegment(sketch, "E1941", {"start": v(18.75, 6.38) * mm, "end": v(18.78, 6.49) * mm});
            skLineSegment(sketch, "E1942", {"start": v(18.78, 6.49) * mm, "end": v(18.78, 13.48) * mm});
            skLineSegment(sketch, "E1943", {"start": v(18.78, 13.48) * mm, "end": v(18.76, 13.55) * mm});
            skLineSegment(sketch, "E1944", {"start": v(18.76, 13.55) * mm, "end": v(18.67, 13.8) * mm});
            skLineSegment(sketch, "E1945", {"start": v(18.67, 13.8) * mm, "end": v(18.6, 13.96) * mm});
            skLineSegment(sketch, "E1946", {"start": v(18.6, 13.96) * mm, "end": v(18.52, 14.1) * mm});
            skLineSegment(sketch, "E1947", {"start": v(18.52, 14.1) * mm, "end": v(18.45, 14.21) * mm});
            skLineSegment(sketch, "E1948", {"start": v(18.45, 14.21) * mm, "end": v(18.43, 14.27) * mm});
            skLineSegment(sketch, "E1949", {"start": v(18.43, 14.27) * mm, "end": v(18.4, 14.3) * mm});
            skLineSegment(sketch, "E1950", {"start": v(18.4, 14.3) * mm, "end": v(18.32, 14.39) * mm});
            skLineSegment(sketch, "E1951", {"start": v(18.32, 14.39) * mm, "end": v(18.07, 14.62) * mm});
            skLineSegment(sketch, "E1952", {"start": v(18.07, 14.62) * mm, "end": v(17.95, 14.7) * mm});
            skLineSegment(sketch, "E1953", {"start": v(17.95, 14.7) * mm, "end": v(17.8, 14.78) * mm});
            skLineSegment(sketch, "E1954", {"start": v(17.8, 14.78) * mm, "end": v(17.63, 14.85) * mm});
            skLineSegment(sketch, "E1955", {"start": v(17.63, 14.85) * mm, "end": v(17.47, 14.9) * mm});
            skLineSegment(sketch, "E1956", {"start": v(17.47, 14.9) * mm, "end": v(17.4, 14.92) * mm});
            skLineSegment(sketch, "E1957", {"start": v(17.4, 14.92) * mm, "end": v(17.28, 14.93) * mm});
            skLineSegment(sketch, "E1958", {"start": v(17.28, 14.93) * mm, "end": v(17.01, 14.94) * mm});
            skLineSegment(sketch, "E1959", {"start": v(17.01, 14.94) * mm, "end": v(16.75, 14.93) * mm});
            skLineSegment(sketch, "E1960", {"start": v(16.75, 14.93) * mm, "end": v(16.64, 14.92) * mm});
            skLineSegment(sketch, "E1961", {"start": v(16.64, 14.92) * mm, "end": v(16.55, 14.9) * mm});
            skLineSegment(sketch, "E1962", {"start": v(16.55, 14.9) * mm, "end": v(16.36, 14.84) * mm});
            skLineSegment(sketch, "E1963", {"start": v(16.36, 14.84) * mm, "end": v(16.16, 14.74) * mm});
            skLineSegment(sketch, "E1964", {"start": v(16.16, 14.74) * mm, "end": v(15.97, 14.62) * mm});
            skLineSegment(sketch, "E1965", {"start": v(15.97, 14.62) * mm, "end": v(15.8, 14.48) * mm});
            skLineSegment(sketch, "E1966", {"start": v(15.8, 14.48) * mm, "end": v(15.6, 14.3) * mm});
            skLineSegment(sketch, "E1967", {"start": v(15.6, 14.3) * mm, "end": v(15.6, 14.27) * mm});
            skLineSegment(sketch, "E1968", {"start": v(15.6, 14.27) * mm, "end": v(15.57, 14.21) * mm});
            skLineSegment(sketch, "E1969", {"start": v(15.57, 14.21) * mm, "end": v(15.5, 14.1) * mm});
            skLineSegment(sketch, "E1970", {"start": v(15.5, 14.1) * mm, "end": v(15.42, 13.96) * mm});
            skLineSegment(sketch, "E1971", {"start": v(15.42, 13.96) * mm, "end": v(15.35, 13.8) * mm});
            skLineSegment(sketch, "E1972", {"start": v(15.35, 13.8) * mm, "end": v(15.27, 13.55) * mm});
            skLineSegment(sketch, "E1973", {"start": v(15.27, 13.55) * mm, "end": v(15.25, 13.48) * mm});
            skLineSegment(sketch, "E1974", {"start": v(15.25, 13.48) * mm, "end": v(15.25, 6.46) * mm});
            skLineSegment(sketch, "E1975", {"start": v(24.5, 17.24) * mm, "end": v(24.5, 14.24) * mm});
            skLineSegment(sketch, "E1976", {"start": v(24.5, 14.24) * mm, "end": v(26.5, 14.24) * mm});
            skLineSegment(sketch, "E1977", {"start": v(26.5, 14.24) * mm, "end": v(26.5, 17.24) * mm});
            skLineSegment(sketch, "E1978", {"start": v(26.5, 17.24) * mm, "end": v(24.5, 17.24) * mm});
            skLineSegment(sketch, "E1979", {"start": v(26.5, 30.48) * mm, "end": v(26.5, 1) * mm});
            skLineSegment(sketch, "E1980", {"start": v(26.5, 1) * mm, "end": v(41.5, 1) * mm});
            skLineSegment(sketch, "E1981", {"start": v(41.5, 1) * mm, "end": v(41.5, 30.48) * mm});
            skLineSegment(sketch, "E1982", {"start": v(41.5, 30.48) * mm, "end": v(26.5, 30.48) * mm});
            skArc(sketch, "E1983", {"start": v(38.51, 25.47) * mm, "mid": v(38.15, 26.35) * mm, "end": v(37.26, 26.72) * mm});
            skArc(sketch, "E1984", {"start": v(37.26, 26.72) * mm, "mid": v(36.38, 26.35) * mm, "end": v(36.01, 25.47) * mm});
            skArc(sketch, "E1985", {"start": v(36.01, 25.47) * mm, "mid": v(36.38, 24.58) * mm, "end": v(37.26, 24.22) * mm});
            skArc(sketch, "E1986", {"start": v(37.26, 24.22) * mm, "mid": v(38.15, 24.58) * mm, "end": v(38.51, 25.47) * mm});
            skArc(sketch, "E1987", {"start": v(32.01, 25.47) * mm, "mid": v(31.65, 26.35) * mm, "end": v(30.76, 26.72) * mm});
            skArc(sketch, "E1988", {"start": v(30.76, 26.72) * mm, "mid": v(29.88, 26.35) * mm, "end": v(29.51, 25.47) * mm});
            skArc(sketch, "E1989", {"start": v(29.51, 25.47) * mm, "mid": v(29.88, 24.58) * mm, "end": v(30.76, 24.22) * mm});
            skArc(sketch, "E1990", {"start": v(30.76, 24.22) * mm, "mid": v(31.65, 24.58) * mm, "end": v(32.01, 25.47) * mm});
            skArc(sketch, "E1991", {"start": v(39.76, 25.47) * mm, "mid": v(39.03, 27.23) * mm, "end": v(37.26, 27.97) * mm});
            skArc(sketch, "E1992", {"start": v(37.26, 27.97) * mm, "mid": v(35.5, 27.23) * mm, "end": v(34.76, 25.47) * mm});
            skArc(sketch, "E1993", {"start": v(34.76, 25.47) * mm, "mid": v(35.5, 23.7) * mm, "end": v(37.26, 22.97) * mm});
            skArc(sketch, "E1994", {"start": v(37.26, 22.97) * mm, "mid": v(39.03, 23.7) * mm, "end": v(39.76, 25.47) * mm});
            skArc(sketch, "E1995", {"start": v(33.26, 25.47) * mm, "mid": v(32.53, 27.23) * mm, "end": v(30.76, 27.97) * mm});
            skArc(sketch, "E1996", {"start": v(30.76, 27.97) * mm, "mid": v(29, 27.23) * mm, "end": v(28.26, 25.47) * mm});
            skArc(sketch, "E1997", {"start": v(28.26, 25.47) * mm, "mid": v(29, 23.7) * mm, "end": v(30.76, 22.97) * mm});
            skArc(sketch, "E1998", {"start": v(30.76, 22.97) * mm, "mid": v(32.53, 23.7) * mm, "end": v(33.26, 25.47) * mm});
            skLineSegment(sketch, "E1999", {"start": v(32.5, -1) * mm, "end": v(35.5, -1) * mm});
            skLineSegment(sketch, "E2000", {"start": v(35.5, -1) * mm, "end": v(35.5, 1) * mm});
            skLineSegment(sketch, "E2001", {"start": v(35.5, 1) * mm, "end": v(32.5, 1) * mm});
            skLineSegment(sketch, "E2002", {"start": v(32.5, 1) * mm, "end": v(32.5, -1) * mm});
            skLineSegment(sketch, "E2003", {"start": v(32.25, 6.46) * mm, "end": v(32.27, 6.4) * mm});
            skLineSegment(sketch, "E2004", {"start": v(32.27, 6.4) * mm, "end": v(32.35, 6.16) * mm});
            skLineSegment(sketch, "E2005", {"start": v(32.35, 6.16) * mm, "end": v(32.4, 6.02) * mm});
            skLineSegment(sketch, "E2006", {"start": v(32.4, 6.02) * mm, "end": v(32.44, 5.92) * mm});
            skLineSegment(sketch, "E2007", {"start": v(32.44, 5.92) * mm, "end": v(32.5, 5.84) * mm});
            skLineSegment(sketch, "E2008", {"start": v(32.5, 5.84) * mm, "end": v(32.57, 5.74) * mm});
            skLineSegment(sketch, "E2009", {"start": v(32.57, 5.74) * mm, "end": v(32.6, 5.7) * mm});
            skLineSegment(sketch, "E2010", {"start": v(32.6, 5.7) * mm, "end": v(32.6, 5.67) * mm});
            skLineSegment(sketch, "E2011", {"start": v(32.6, 5.67) * mm, "end": v(32.64, 5.62) * mm});
            skLineSegment(sketch, "E2012", {"start": v(32.64, 5.62) * mm, "end": v(32.73, 5.53) * mm});
            skLineSegment(sketch, "E2013", {"start": v(32.73, 5.53) * mm, "end": v(32.92, 5.35) * mm});
            skLineSegment(sketch, "E2014", {"start": v(32.92, 5.35) * mm, "end": v(32.97, 5.3) * mm});
            skLineSegment(sketch, "E2015", {"start": v(32.97, 5.3) * mm, "end": v(33.02, 5.28) * mm});
            skLineSegment(sketch, "E2016", {"start": v(33.02, 5.28) * mm, "end": v(33.04, 5.28) * mm});
            skLineSegment(sketch, "E2017", {"start": v(33.04, 5.28) * mm, "end": v(33.05, 5.26) * mm});
            skLineSegment(sketch, "E2018", {"start": v(33.05, 5.26) * mm, "end": v(33.08, 5.24) * mm});
            skLineSegment(sketch, "E2019", {"start": v(33.08, 5.24) * mm, "end": v(33.14, 5.2) * mm});
            skLineSegment(sketch, "E2020", {"start": v(33.14, 5.2) * mm, "end": v(33.42, 5.08) * mm});
            skLineSegment(sketch, "E2021", {"start": v(33.42, 5.08) * mm, "end": v(33.54, 5.03) * mm});
            skLineSegment(sketch, "E2022", {"start": v(33.54, 5.03) * mm, "end": v(33.68, 5) * mm});
            skLineSegment(sketch, "E2023", {"start": v(33.68, 5) * mm, "end": v(33.84, 4.98) * mm});
            skLineSegment(sketch, "E2024", {"start": v(33.84, 4.98) * mm, "end": v(34, 4.98) * mm});
            skLineSegment(sketch, "E2025", {"start": v(34, 4.98) * mm, "end": v(34.17, 4.98) * mm});
            skLineSegment(sketch, "E2026", {"start": v(34.17, 4.98) * mm, "end": v(34.33, 5) * mm});
            skLineSegment(sketch, "E2027", {"start": v(34.33, 5) * mm, "end": v(34.48, 5.03) * mm});
            skLineSegment(sketch, "E2028", {"start": v(34.48, 5.03) * mm, "end": v(34.6, 5.07) * mm});
            skLineSegment(sketch, "E2029", {"start": v(34.6, 5.07) * mm, "end": v(34.9, 5.2) * mm});
            skLineSegment(sketch, "E2030", {"start": v(34.9, 5.2) * mm, "end": v(34.96, 5.24) * mm});
            skLineSegment(sketch, "E2031", {"start": v(34.96, 5.24) * mm, "end": v(34.98, 5.26) * mm});
            skLineSegment(sketch, "E2032", {"start": v(34.98, 5.26) * mm, "end": v(34.99, 5.28) * mm});
            skLineSegment(sketch, "E2033", {"start": v(34.99, 5.28) * mm, "end": v(35, 5.28) * mm});
            skLineSegment(sketch, "E2034", {"start": v(35, 5.28) * mm, "end": v(35.04, 5.3) * mm});
            skLineSegment(sketch, "E2035", {"start": v(35.04, 5.3) * mm, "end": v(35.1, 5.34) * mm});
            skLineSegment(sketch, "E2036", {"start": v(35.1, 5.34) * mm, "end": v(35.24, 5.46) * mm});
            skLineSegment(sketch, "E2037", {"start": v(35.24, 5.46) * mm, "end": v(35.37, 5.6) * mm});
            skLineSegment(sketch, "E2038", {"start": v(35.37, 5.6) * mm, "end": v(35.4, 5.64) * mm});
            skLineSegment(sketch, "E2039", {"start": v(35.4, 5.64) * mm, "end": v(35.43, 5.67) * mm});
            skLineSegment(sketch, "E2040", {"start": v(35.43, 5.67) * mm, "end": v(35.44, 5.7) * mm});
            skLineSegment(sketch, "E2041", {"start": v(35.44, 5.7) * mm, "end": v(35.46, 5.74) * mm});
            skLineSegment(sketch, "E2042", {"start": v(35.46, 5.74) * mm, "end": v(35.53, 5.83) * mm});
            skLineSegment(sketch, "E2043", {"start": v(35.53, 5.83) * mm, "end": v(35.57, 5.89) * mm});
            skLineSegment(sketch, "E2044", {"start": v(35.57, 5.89) * mm, "end": v(35.61, 5.98) * mm});
            skLineSegment(sketch, "E2045", {"start": v(35.61, 5.98) * mm, "end": v(35.75, 6.38) * mm});
            skLineSegment(sketch, "E2046", {"start": v(35.75, 6.38) * mm, "end": v(35.78, 6.49) * mm});
            skLineSegment(sketch, "E2047", {"start": v(35.78, 6.49) * mm, "end": v(35.78, 13.48) * mm});
            skLineSegment(sketch, "E2048", {"start": v(35.78, 13.48) * mm, "end": v(35.76, 13.55) * mm});
            skLineSegment(sketch, "E2049", {"start": v(35.76, 13.55) * mm, "end": v(35.67, 13.8) * mm});
            skLineSegment(sketch, "E2050", {"start": v(35.67, 13.8) * mm, "end": v(35.6, 13.96) * mm});
            skLineSegment(sketch, "E2051", {"start": v(35.6, 13.96) * mm, "end": v(35.52, 14.1) * mm});
            skLineSegment(sketch, "E2052", {"start": v(35.52, 14.1) * mm, "end": v(35.45, 14.21) * mm});
            skLineSegment(sketch, "E2053", {"start": v(35.45, 14.21) * mm, "end": v(35.43, 14.27) * mm});
            skLineSegment(sketch, "E2054", {"start": v(35.43, 14.27) * mm, "end": v(35.4, 14.3) * mm});
            skLineSegment(sketch, "E2055", {"start": v(35.4, 14.3) * mm, "end": v(35.32, 14.39) * mm});
            skLineSegment(sketch, "E2056", {"start": v(35.32, 14.39) * mm, "end": v(35.07, 14.62) * mm});
            skLineSegment(sketch, "E2057", {"start": v(35.07, 14.62) * mm, "end": v(34.95, 14.7) * mm});
            skLineSegment(sketch, "E2058", {"start": v(34.95, 14.7) * mm, "end": v(34.8, 14.78) * mm});
            skLineSegment(sketch, "E2059", {"start": v(34.8, 14.78) * mm, "end": v(34.63, 14.85) * mm});
            skLineSegment(sketch, "E2060", {"start": v(34.63, 14.85) * mm, "end": v(34.47, 14.9) * mm});
            skLineSegment(sketch, "E2061", {"start": v(34.47, 14.9) * mm, "end": v(34.4, 14.92) * mm});
            skLineSegment(sketch, "E2062", {"start": v(34.4, 14.92) * mm, "end": v(34.28, 14.93) * mm});
            skLineSegment(sketch, "E2063", {"start": v(34.28, 14.93) * mm, "end": v(34.01, 14.94) * mm});
            skLineSegment(sketch, "E2064", {"start": v(34.01, 14.94) * mm, "end": v(33.75, 14.93) * mm});
            skLineSegment(sketch, "E2065", {"start": v(33.75, 14.93) * mm, "end": v(33.64, 14.92) * mm});
            skLineSegment(sketch, "E2066", {"start": v(33.64, 14.92) * mm, "end": v(33.55, 14.9) * mm});
            skLineSegment(sketch, "E2067", {"start": v(33.55, 14.9) * mm, "end": v(33.36, 14.84) * mm});
            skLineSegment(sketch, "E2068", {"start": v(33.36, 14.84) * mm, "end": v(33.16, 14.74) * mm});
            skLineSegment(sketch, "E2069", {"start": v(33.16, 14.74) * mm, "end": v(32.97, 14.62) * mm});
            skLineSegment(sketch, "E2070", {"start": v(32.97, 14.62) * mm, "end": v(32.8, 14.48) * mm});
            skLineSegment(sketch, "E2071", {"start": v(32.8, 14.48) * mm, "end": v(32.6, 14.3) * mm});
            skLineSegment(sketch, "E2072", {"start": v(32.6, 14.3) * mm, "end": v(32.6, 14.27) * mm});
            skLineSegment(sketch, "E2073", {"start": v(32.6, 14.27) * mm, "end": v(32.57, 14.21) * mm});
            skLineSegment(sketch, "E2074", {"start": v(32.57, 14.21) * mm, "end": v(32.5, 14.1) * mm});
            skLineSegment(sketch, "E2075", {"start": v(32.5, 14.1) * mm, "end": v(32.42, 13.96) * mm});
            skLineSegment(sketch, "E2076", {"start": v(32.42, 13.96) * mm, "end": v(32.35, 13.8) * mm});
            skLineSegment(sketch, "E2077", {"start": v(32.35, 13.8) * mm, "end": v(32.27, 13.55) * mm});
            skLineSegment(sketch, "E2078", {"start": v(32.27, 13.55) * mm, "end": v(32.25, 13.48) * mm});
            skLineSegment(sketch, "E2079", {"start": v(32.25, 13.48) * mm, "end": v(32.25, 6.46) * mm});
            skLineSegment(sketch, "E2080", {"start": v(32.5, 30.48) * mm, "end": v(35.5, 30.48) * mm});
            skLineSegment(sketch, "E2081", {"start": v(35.5, 30.48) * mm, "end": v(35.5, 32.48) * mm});
            skLineSegment(sketch, "E2082", {"start": v(35.5, 32.48) * mm, "end": v(32.5, 32.48) * mm});
            skLineSegment(sketch, "E2083", {"start": v(32.5, 32.48) * mm, "end": v(32.5, 30.48) * mm});
            skLineSegment(sketch, "E2084", {"start": v(43.5, 30.48) * mm, "end": v(43.5, 1) * mm});
            skLineSegment(sketch, "E2085", {"start": v(43.5, 1) * mm, "end": v(58.5, 1) * mm});
            skLineSegment(sketch, "E2086", {"start": v(58.5, 1) * mm, "end": v(58.5, 30.48) * mm});
            skLineSegment(sketch, "E2087", {"start": v(58.5, 30.48) * mm, "end": v(43.5, 30.48) * mm});
            skArc(sketch, "E2088", {"start": v(55.51, 25.47) * mm, "mid": v(55.15, 26.35) * mm, "end": v(54.26, 26.72) * mm});
            skArc(sketch, "E2089", {"start": v(54.26, 26.72) * mm, "mid": v(53.38, 26.35) * mm, "end": v(53.01, 25.47) * mm});
            skArc(sketch, "E2090", {"start": v(53.01, 25.47) * mm, "mid": v(53.38, 24.58) * mm, "end": v(54.26, 24.22) * mm});
            skArc(sketch, "E2091", {"start": v(54.26, 24.22) * mm, "mid": v(55.15, 24.58) * mm, "end": v(55.51, 25.47) * mm});
            skArc(sketch, "E2092", {"start": v(49.01, 25.47) * mm, "mid": v(48.65, 26.35) * mm, "end": v(47.76, 26.72) * mm});
            skArc(sketch, "E2093", {"start": v(47.76, 26.72) * mm, "mid": v(46.88, 26.35) * mm, "end": v(46.51, 25.47) * mm});
            skArc(sketch, "E2094", {"start": v(46.51, 25.47) * mm, "mid": v(46.88, 24.58) * mm, "end": v(47.76, 24.22) * mm});
            skArc(sketch, "E2095", {"start": v(47.76, 24.22) * mm, "mid": v(48.65, 24.58) * mm, "end": v(49.01, 25.47) * mm});
            skArc(sketch, "E2096", {"start": v(56.76, 25.47) * mm, "mid": v(56.03, 27.23) * mm, "end": v(54.26, 27.97) * mm});
            skArc(sketch, "E2097", {"start": v(54.26, 27.97) * mm, "mid": v(52.5, 27.23) * mm, "end": v(51.76, 25.47) * mm});
            skArc(sketch, "E2098", {"start": v(51.76, 25.47) * mm, "mid": v(52.5, 23.7) * mm, "end": v(54.26, 22.97) * mm});
            skArc(sketch, "E2099", {"start": v(54.26, 22.97) * mm, "mid": v(56.03, 23.7) * mm, "end": v(56.76, 25.47) * mm});
            skArc(sketch, "E2100", {"start": v(50.26, 25.47) * mm, "mid": v(49.53, 27.23) * mm, "end": v(47.76, 27.97) * mm});
            skArc(sketch, "E2101", {"start": v(47.76, 27.97) * mm, "mid": v(46, 27.23) * mm, "end": v(45.26, 25.47) * mm});
            skArc(sketch, "E2102", {"start": v(45.26, 25.47) * mm, "mid": v(46, 23.7) * mm, "end": v(47.76, 22.97) * mm});
            skArc(sketch, "E2103", {"start": v(47.76, 22.97) * mm, "mid": v(49.53, 23.7) * mm, "end": v(50.26, 25.47) * mm});
            skLineSegment(sketch, "E2104", {"start": v(41.5, 17.24) * mm, "end": v(41.5, 14.24) * mm});
            skLineSegment(sketch, "E2105", {"start": v(41.5, 14.24) * mm, "end": v(43.5, 14.24) * mm});
            skLineSegment(sketch, "E2106", {"start": v(43.5, 14.24) * mm, "end": v(43.5, 17.24) * mm});
            skLineSegment(sketch, "E2107", {"start": v(43.5, 17.24) * mm, "end": v(41.5, 17.24) * mm});
            skLineSegment(sketch, "E2108", {"start": v(49.25, 6.46) * mm, "end": v(49.27, 6.4) * mm});
            skLineSegment(sketch, "E2109", {"start": v(49.27, 6.4) * mm, "end": v(49.35, 6.16) * mm});
            skLineSegment(sketch, "E2110", {"start": v(49.35, 6.16) * mm, "end": v(49.4, 6.02) * mm});
            skLineSegment(sketch, "E2111", {"start": v(49.4, 6.02) * mm, "end": v(49.44, 5.92) * mm});
            skLineSegment(sketch, "E2112", {"start": v(49.44, 5.92) * mm, "end": v(49.5, 5.84) * mm});
            skLineSegment(sketch, "E2113", {"start": v(49.5, 5.84) * mm, "end": v(49.57, 5.74) * mm});
            skLineSegment(sketch, "E2114", {"start": v(49.57, 5.74) * mm, "end": v(49.6, 5.7) * mm});
            skLineSegment(sketch, "E2115", {"start": v(49.6, 5.7) * mm, "end": v(49.6, 5.67) * mm});
            skLineSegment(sketch, "E2116", {"start": v(49.6, 5.67) * mm, "end": v(49.64, 5.62) * mm});
            skLineSegment(sketch, "E2117", {"start": v(49.64, 5.62) * mm, "end": v(49.73, 5.53) * mm});
            skLineSegment(sketch, "E2118", {"start": v(49.73, 5.53) * mm, "end": v(49.92, 5.35) * mm});
            skLineSegment(sketch, "E2119", {"start": v(49.92, 5.35) * mm, "end": v(49.97, 5.3) * mm});
            skLineSegment(sketch, "E2120", {"start": v(49.97, 5.3) * mm, "end": v(50.02, 5.28) * mm});
            skLineSegment(sketch, "E2121", {"start": v(50.02, 5.28) * mm, "end": v(50.04, 5.28) * mm});
            skLineSegment(sketch, "E2122", {"start": v(50.04, 5.28) * mm, "end": v(50.05, 5.26) * mm});
            skLineSegment(sketch, "E2123", {"start": v(50.05, 5.26) * mm, "end": v(50.08, 5.24) * mm});
            skLineSegment(sketch, "E2124", {"start": v(50.08, 5.24) * mm, "end": v(50.14, 5.2) * mm});
            skLineSegment(sketch, "E2125", {"start": v(50.14, 5.2) * mm, "end": v(50.42, 5.08) * mm});
            skLineSegment(sketch, "E2126", {"start": v(50.42, 5.08) * mm, "end": v(50.54, 5.03) * mm});
            skLineSegment(sketch, "E2127", {"start": v(50.54, 5.03) * mm, "end": v(50.68, 5) * mm});
            skLineSegment(sketch, "E2128", {"start": v(50.68, 5) * mm, "end": v(50.84, 4.98) * mm});
            skLineSegment(sketch, "E2129", {"start": v(50.84, 4.98) * mm, "end": v(51, 4.98) * mm});
            skLineSegment(sketch, "E2130", {"start": v(51, 4.98) * mm, "end": v(51.17, 4.98) * mm});
            skLineSegment(sketch, "E2131", {"start": v(51.17, 4.98) * mm, "end": v(51.33, 5) * mm});
            skLineSegment(sketch, "E2132", {"start": v(51.33, 5) * mm, "end": v(51.48, 5.03) * mm});
            skLineSegment(sketch, "E2133", {"start": v(51.48, 5.03) * mm, "end": v(51.6, 5.07) * mm});
            skLineSegment(sketch, "E2134", {"start": v(51.6, 5.07) * mm, "end": v(51.9, 5.2) * mm});
            skLineSegment(sketch, "E2135", {"start": v(51.9, 5.2) * mm, "end": v(51.96, 5.24) * mm});
            skLineSegment(sketch, "E2136", {"start": v(51.96, 5.24) * mm, "end": v(51.98, 5.26) * mm});
            skLineSegment(sketch, "E2137", {"start": v(51.98, 5.26) * mm, "end": v(51.99, 5.28) * mm});
            skLineSegment(sketch, "E2138", {"start": v(51.99, 5.28) * mm, "end": v(52, 5.28) * mm});
            skLineSegment(sketch, "E2139", {"start": v(52, 5.28) * mm, "end": v(52.04, 5.3) * mm});
            skLineSegment(sketch, "E2140", {"start": v(52.04, 5.3) * mm, "end": v(52.1, 5.34) * mm});
            skLineSegment(sketch, "E2141", {"start": v(52.1, 5.34) * mm, "end": v(52.24, 5.46) * mm});
            skLineSegment(sketch, "E2142", {"start": v(52.24, 5.46) * mm, "end": v(52.37, 5.6) * mm});
            skLineSegment(sketch, "E2143", {"start": v(52.37, 5.6) * mm, "end": v(52.4, 5.64) * mm});
            skLineSegment(sketch, "E2144", {"start": v(52.4, 5.64) * mm, "end": v(52.43, 5.67) * mm});
            skLineSegment(sketch, "E2145", {"start": v(52.43, 5.67) * mm, "end": v(52.44, 5.7) * mm});
            skLineSegment(sketch, "E2146", {"start": v(52.44, 5.7) * mm, "end": v(52.46, 5.74) * mm});
            skLineSegment(sketch, "E2147", {"start": v(52.46, 5.74) * mm, "end": v(52.53, 5.83) * mm});
            skLineSegment(sketch, "E2148", {"start": v(52.53, 5.83) * mm, "end": v(52.57, 5.89) * mm});
            skLineSegment(sketch, "E2149", {"start": v(52.57, 5.89) * mm, "end": v(52.61, 5.98) * mm});
            skLineSegment(sketch, "E2150", {"start": v(52.61, 5.98) * mm, "end": v(52.75, 6.38) * mm});
            skLineSegment(sketch, "E2151", {"start": v(52.75, 6.38) * mm, "end": v(52.78, 6.49) * mm});
            skLineSegment(sketch, "E2152", {"start": v(52.78, 6.49) * mm, "end": v(52.78, 13.48) * mm});
            skLineSegment(sketch, "E2153", {"start": v(52.78, 13.48) * mm, "end": v(52.76, 13.55) * mm});
            skLineSegment(sketch, "E2154", {"start": v(52.76, 13.55) * mm, "end": v(52.67, 13.8) * mm});
            skLineSegment(sketch, "E2155", {"start": v(52.67, 13.8) * mm, "end": v(52.6, 13.96) * mm});
            skLineSegment(sketch, "E2156", {"start": v(52.6, 13.96) * mm, "end": v(52.52, 14.1) * mm});
            skLineSegment(sketch, "E2157", {"start": v(52.52, 14.1) * mm, "end": v(52.45, 14.21) * mm});
            skLineSegment(sketch, "E2158", {"start": v(52.45, 14.21) * mm, "end": v(52.43, 14.27) * mm});
            skLineSegment(sketch, "E2159", {"start": v(52.43, 14.27) * mm, "end": v(52.4, 14.3) * mm});
            skLineSegment(sketch, "E2160", {"start": v(52.4, 14.3) * mm, "end": v(52.32, 14.39) * mm});
            skLineSegment(sketch, "E2161", {"start": v(52.32, 14.39) * mm, "end": v(52.07, 14.62) * mm});
            skLineSegment(sketch, "E2162", {"start": v(52.07, 14.62) * mm, "end": v(51.95, 14.7) * mm});
            skLineSegment(sketch, "E2163", {"start": v(51.95, 14.7) * mm, "end": v(51.8, 14.78) * mm});
            skLineSegment(sketch, "E2164", {"start": v(51.8, 14.78) * mm, "end": v(51.63, 14.85) * mm});
            skLineSegment(sketch, "E2165", {"start": v(51.63, 14.85) * mm, "end": v(51.47, 14.9) * mm});
            skLineSegment(sketch, "E2166", {"start": v(51.47, 14.9) * mm, "end": v(51.4, 14.92) * mm});
            skLineSegment(sketch, "E2167", {"start": v(51.4, 14.92) * mm, "end": v(51.28, 14.93) * mm});
            skLineSegment(sketch, "E2168", {"start": v(51.28, 14.93) * mm, "end": v(51.01, 14.94) * mm});
            skLineSegment(sketch, "E2169", {"start": v(51.01, 14.94) * mm, "end": v(50.75, 14.93) * mm});
            skLineSegment(sketch, "E2170", {"start": v(50.75, 14.93) * mm, "end": v(50.64, 14.92) * mm});
            skLineSegment(sketch, "E2171", {"start": v(50.64, 14.92) * mm, "end": v(50.55, 14.9) * mm});
            skLineSegment(sketch, "E2172", {"start": v(50.55, 14.9) * mm, "end": v(50.36, 14.84) * mm});
            skLineSegment(sketch, "E2173", {"start": v(50.36, 14.84) * mm, "end": v(50.16, 14.74) * mm});
            skLineSegment(sketch, "E2174", {"start": v(50.16, 14.74) * mm, "end": v(49.97, 14.62) * mm});
            skLineSegment(sketch, "E2175", {"start": v(49.97, 14.62) * mm, "end": v(49.8, 14.48) * mm});
            skLineSegment(sketch, "E2176", {"start": v(49.8, 14.48) * mm, "end": v(49.6, 14.3) * mm});
            skLineSegment(sketch, "E2177", {"start": v(49.6, 14.3) * mm, "end": v(49.6, 14.27) * mm});
            skLineSegment(sketch, "E2178", {"start": v(49.6, 14.27) * mm, "end": v(49.57, 14.21) * mm});
            skLineSegment(sketch, "E2179", {"start": v(49.57, 14.21) * mm, "end": v(49.5, 14.1) * mm});
            skLineSegment(sketch, "E2180", {"start": v(49.5, 14.1) * mm, "end": v(49.42, 13.96) * mm});
            skLineSegment(sketch, "E2181", {"start": v(49.42, 13.96) * mm, "end": v(49.35, 13.8) * mm});
            skLineSegment(sketch, "E2182", {"start": v(49.35, 13.8) * mm, "end": v(49.27, 13.55) * mm});
            skLineSegment(sketch, "E2183", {"start": v(49.27, 13.55) * mm, "end": v(49.25, 13.48) * mm});
            skLineSegment(sketch, "E2184", {"start": v(49.25, 13.48) * mm, "end": v(49.25, 6.46) * mm});
            skLineSegment(sketch, "E2185", {"start": v(43.5, 61.97) * mm, "end": v(43.5, 32.48) * mm});
            skLineSegment(sketch, "E2186", {"start": v(43.5, 32.48) * mm, "end": v(58.5, 32.48) * mm});
            skLineSegment(sketch, "E2187", {"start": v(58.5, 32.48) * mm, "end": v(58.5, 61.97) * mm});
            skLineSegment(sketch, "E2188", {"start": v(58.5, 61.97) * mm, "end": v(43.5, 61.97) * mm});
            skArc(sketch, "E2189", {"start": v(55.51, 56.95) * mm, "mid": v(55.15, 57.83) * mm, "end": v(54.26, 58.2) * mm});
            skArc(sketch, "E2190", {"start": v(54.26, 58.2) * mm, "mid": v(53.38, 57.83) * mm, "end": v(53.01, 56.95) * mm});
            skArc(sketch, "E2191", {"start": v(53.01, 56.95) * mm, "mid": v(53.38, 56.07) * mm, "end": v(54.26, 55.7) * mm});
            skArc(sketch, "E2192", {"start": v(54.26, 55.7) * mm, "mid": v(55.15, 56.07) * mm, "end": v(55.51, 56.95) * mm});
            skArc(sketch, "E2193", {"start": v(49.01, 56.95) * mm, "mid": v(48.65, 57.83) * mm, "end": v(47.76, 58.2) * mm});
            skArc(sketch, "E2194", {"start": v(47.76, 58.2) * mm, "mid": v(46.88, 57.83) * mm, "end": v(46.51, 56.95) * mm});
            skArc(sketch, "E2195", {"start": v(46.51, 56.95) * mm, "mid": v(46.88, 56.07) * mm, "end": v(47.76, 55.7) * mm});
            skArc(sketch, "E2196", {"start": v(47.76, 55.7) * mm, "mid": v(48.65, 56.07) * mm, "end": v(49.01, 56.95) * mm});
            skArc(sketch, "E2197", {"start": v(56.76, 56.95) * mm, "mid": v(56.03, 58.72) * mm, "end": v(54.26, 59.45) * mm});
            skArc(sketch, "E2198", {"start": v(54.26, 59.45) * mm, "mid": v(52.5, 58.72) * mm, "end": v(51.76, 56.95) * mm});
            skArc(sketch, "E2199", {"start": v(51.76, 56.95) * mm, "mid": v(52.5, 55.18) * mm, "end": v(54.26, 54.45) * mm});
            skArc(sketch, "E2200", {"start": v(54.26, 54.45) * mm, "mid": v(56.03, 55.18) * mm, "end": v(56.76, 56.95) * mm});
            skArc(sketch, "E2201", {"start": v(50.26, 56.95) * mm, "mid": v(49.53, 58.72) * mm, "end": v(47.76, 59.45) * mm});
            skArc(sketch, "E2202", {"start": v(47.76, 59.45) * mm, "mid": v(46, 58.72) * mm, "end": v(45.26, 56.95) * mm});
            skArc(sketch, "E2203", {"start": v(45.26, 56.95) * mm, "mid": v(46, 55.18) * mm, "end": v(47.76, 54.45) * mm});
            skArc(sketch, "E2204", {"start": v(47.76, 54.45) * mm, "mid": v(49.53, 55.18) * mm, "end": v(50.26, 56.95) * mm});
            skLineSegment(sketch, "E2205", {"start": v(49.5, 30.48) * mm, "end": v(52.5, 30.48) * mm});
            skLineSegment(sketch, "E2206", {"start": v(52.5, 30.48) * mm, "end": v(52.5, 32.48) * mm});
            skLineSegment(sketch, "E2207", {"start": v(52.5, 32.48) * mm, "end": v(49.5, 32.48) * mm});
            skLineSegment(sketch, "E2208", {"start": v(49.5, 32.48) * mm, "end": v(49.5, 30.48) * mm});
            skLineSegment(sketch, "E2209", {"start": v(49.25, 37.94) * mm, "end": v(49.27, 37.88) * mm});
            skLineSegment(sketch, "E2210", {"start": v(49.27, 37.88) * mm, "end": v(49.35, 37.64) * mm});
            skLineSegment(sketch, "E2211", {"start": v(49.35, 37.64) * mm, "end": v(49.4, 37.5) * mm});
            skLineSegment(sketch, "E2212", {"start": v(49.4, 37.5) * mm, "end": v(49.44, 37.4) * mm});
            skLineSegment(sketch, "E2213", {"start": v(49.44, 37.4) * mm, "end": v(49.5, 37.32) * mm});
            skLineSegment(sketch, "E2214", {"start": v(49.5, 37.32) * mm, "end": v(49.57, 37.23) * mm});
            skLineSegment(sketch, "E2215", {"start": v(49.57, 37.23) * mm, "end": v(49.6, 37.19) * mm});
            skLineSegment(sketch, "E2216", {"start": v(49.6, 37.19) * mm, "end": v(49.6, 37.16) * mm});
            skLineSegment(sketch, "E2217", {"start": v(49.6, 37.16) * mm, "end": v(49.64, 37.1) * mm});
            skLineSegment(sketch, "E2218", {"start": v(49.64, 37.1) * mm, "end": v(49.73, 37.02) * mm});
            skLineSegment(sketch, "E2219", {"start": v(49.73, 37.02) * mm, "end": v(49.92, 36.83) * mm});
            skLineSegment(sketch, "E2220", {"start": v(49.92, 36.83) * mm, "end": v(49.97, 36.79) * mm});
            skLineSegment(sketch, "E2221", {"start": v(49.97, 36.79) * mm, "end": v(50.02, 36.77) * mm});
            skLineSegment(sketch, "E2222", {"start": v(50.02, 36.77) * mm, "end": v(50.04, 36.76) * mm});
            skLineSegment(sketch, "E2223", {"start": v(50.04, 36.76) * mm, "end": v(50.05, 36.74) * mm});
            skLineSegment(sketch, "E2224", {"start": v(50.05, 36.74) * mm, "end": v(50.08, 36.72) * mm});
            skLineSegment(sketch, "E2225", {"start": v(50.08, 36.72) * mm, "end": v(50.14, 36.69) * mm});
            skLineSegment(sketch, "E2226", {"start": v(50.14, 36.69) * mm, "end": v(50.42, 36.56) * mm});
            skLineSegment(sketch, "E2227", {"start": v(50.42, 36.56) * mm, "end": v(50.54, 36.52) * mm});
            skLineSegment(sketch, "E2228", {"start": v(50.54, 36.52) * mm, "end": v(50.68, 36.49) * mm});
            skLineSegment(sketch, "E2229", {"start": v(50.68, 36.49) * mm, "end": v(50.84, 36.47) * mm});
            skLineSegment(sketch, "E2230", {"start": v(50.84, 36.47) * mm, "end": v(51, 36.46) * mm});
            skLineSegment(sketch, "E2231", {"start": v(51, 36.46) * mm, "end": v(51.17, 36.47) * mm});
            skLineSegment(sketch, "E2232", {"start": v(51.17, 36.47) * mm, "end": v(51.33, 36.48) * mm});
            skLineSegment(sketch, "E2233", {"start": v(51.33, 36.48) * mm, "end": v(51.48, 36.51) * mm});
            skLineSegment(sketch, "E2234", {"start": v(51.48, 36.51) * mm, "end": v(51.6, 36.56) * mm});
            skLineSegment(sketch, "E2235", {"start": v(51.6, 36.56) * mm, "end": v(51.9, 36.68) * mm});
            skLineSegment(sketch, "E2236", {"start": v(51.9, 36.68) * mm, "end": v(51.96, 36.72) * mm});
            skLineSegment(sketch, "E2237", {"start": v(51.96, 36.72) * mm, "end": v(51.98, 36.74) * mm});
            skLineSegment(sketch, "E2238", {"start": v(51.98, 36.74) * mm, "end": v(51.99, 36.76) * mm});
            skLineSegment(sketch, "E2239", {"start": v(51.99, 36.76) * mm, "end": v(52, 36.77) * mm});
            skLineSegment(sketch, "E2240", {"start": v(52, 36.77) * mm, "end": v(52.04, 36.78) * mm});
            skLineSegment(sketch, "E2241", {"start": v(52.04, 36.78) * mm, "end": v(52.1, 36.82) * mm});
            skLineSegment(sketch, "E2242", {"start": v(52.1, 36.82) * mm, "end": v(52.24, 36.94) * mm});
            skLineSegment(sketch, "E2243", {"start": v(52.24, 36.94) * mm, "end": v(52.37, 37.08) * mm});
            skLineSegment(sketch, "E2244", {"start": v(52.37, 37.08) * mm, "end": v(52.4, 37.13) * mm});
            skLineSegment(sketch, "E2245", {"start": v(52.4, 37.13) * mm, "end": v(52.43, 37.16) * mm});
            skLineSegment(sketch, "E2246", {"start": v(52.43, 37.16) * mm, "end": v(52.44, 37.19) * mm});
            skLineSegment(sketch, "E2247", {"start": v(52.44, 37.19) * mm, "end": v(52.46, 37.23) * mm});
            skLineSegment(sketch, "E2248", {"start": v(52.46, 37.23) * mm, "end": v(52.53, 37.3) * mm});
            skLineSegment(sketch, "E2249", {"start": v(52.53, 37.3) * mm, "end": v(52.57, 37.37) * mm});
            skLineSegment(sketch, "E2250", {"start": v(52.57, 37.37) * mm, "end": v(52.61, 37.47) * mm});
            skLineSegment(sketch, "E2251", {"start": v(52.61, 37.47) * mm, "end": v(52.75, 37.87) * mm});
            skLineSegment(sketch, "E2252", {"start": v(52.75, 37.87) * mm, "end": v(52.78, 37.97) * mm});
            skLineSegment(sketch, "E2253", {"start": v(52.78, 37.97) * mm, "end": v(52.78, 44.96) * mm});
            skLineSegment(sketch, "E2254", {"start": v(52.78, 44.96) * mm, "end": v(52.76, 45.03) * mm});
            skLineSegment(sketch, "E2255", {"start": v(52.76, 45.03) * mm, "end": v(52.67, 45.28) * mm});
            skLineSegment(sketch, "E2256", {"start": v(52.67, 45.28) * mm, "end": v(52.6, 45.44) * mm});
            skLineSegment(sketch, "E2257", {"start": v(52.6, 45.44) * mm, "end": v(52.52, 45.6) * mm});
            skLineSegment(sketch, "E2258", {"start": v(52.52, 45.6) * mm, "end": v(52.45, 45.7) * mm});
            skLineSegment(sketch, "E2259", {"start": v(52.45, 45.7) * mm, "end": v(52.43, 45.75) * mm});
            skLineSegment(sketch, "E2260", {"start": v(52.43, 45.75) * mm, "end": v(52.4, 45.8) * mm});
            skLineSegment(sketch, "E2261", {"start": v(52.4, 45.8) * mm, "end": v(52.32, 45.87) * mm});
            skLineSegment(sketch, "E2262", {"start": v(52.32, 45.87) * mm, "end": v(52.07, 46.1) * mm});
            skLineSegment(sketch, "E2263", {"start": v(52.07, 46.1) * mm, "end": v(51.95, 46.18) * mm});
            skLineSegment(sketch, "E2264", {"start": v(51.95, 46.18) * mm, "end": v(51.8, 46.26) * mm});
            skLineSegment(sketch, "E2265", {"start": v(51.8, 46.26) * mm, "end": v(51.63, 46.34) * mm});
            skLineSegment(sketch, "E2266", {"start": v(51.63, 46.34) * mm, "end": v(51.47, 46.4) * mm});
            skLineSegment(sketch, "E2267", {"start": v(51.47, 46.4) * mm, "end": v(51.4, 46.4) * mm});
            skLineSegment(sketch, "E2268", {"start": v(51.4, 46.4) * mm, "end": v(51.28, 46.42) * mm});
            skLineSegment(sketch, "E2269", {"start": v(51.28, 46.42) * mm, "end": v(51.01, 46.43) * mm});
            skLineSegment(sketch, "E2270", {"start": v(51.01, 46.43) * mm, "end": v(50.75, 46.42) * mm});
            skLineSegment(sketch, "E2271", {"start": v(50.75, 46.42) * mm, "end": v(50.64, 46.4) * mm});
            skLineSegment(sketch, "E2272", {"start": v(50.64, 46.4) * mm, "end": v(50.55, 46.4) * mm});
            skLineSegment(sketch, "E2273", {"start": v(50.55, 46.4) * mm, "end": v(50.36, 46.32) * mm});
            skLineSegment(sketch, "E2274", {"start": v(50.36, 46.32) * mm, "end": v(50.16, 46.22) * mm});
            skLineSegment(sketch, "E2275", {"start": v(50.16, 46.22) * mm, "end": v(49.97, 46.1) * mm});
            skLineSegment(sketch, "E2276", {"start": v(49.97, 46.1) * mm, "end": v(49.8, 45.97) * mm});
            skLineSegment(sketch, "E2277", {"start": v(49.8, 45.97) * mm, "end": v(49.6, 45.78) * mm});
            skLineSegment(sketch, "E2278", {"start": v(49.6, 45.78) * mm, "end": v(49.6, 45.75) * mm});
            skLineSegment(sketch, "E2279", {"start": v(49.6, 45.75) * mm, "end": v(49.57, 45.7) * mm});
            skLineSegment(sketch, "E2280", {"start": v(49.57, 45.7) * mm, "end": v(49.5, 45.6) * mm});
            skLineSegment(sketch, "E2281", {"start": v(49.5, 45.6) * mm, "end": v(49.42, 45.44) * mm});
            skLineSegment(sketch, "E2282", {"start": v(49.42, 45.44) * mm, "end": v(49.35, 45.28) * mm});
            skLineSegment(sketch, "E2283", {"start": v(49.35, 45.28) * mm, "end": v(49.27, 45.03) * mm});
            skLineSegment(sketch, "E2284", {"start": v(49.27, 45.03) * mm, "end": v(49.25, 44.96) * mm});
            skLineSegment(sketch, "E2285", {"start": v(49.25, 44.96) * mm, "end": v(49.25, 37.94) * mm});
            skLineSegment(sketch, "E2286", {"start": v(26.5, 61.97) * mm, "end": v(26.5, 32.48) * mm});
            skLineSegment(sketch, "E2287", {"start": v(26.5, 32.48) * mm, "end": v(41.5, 32.48) * mm});
            skLineSegment(sketch, "E2288", {"start": v(41.5, 32.48) * mm, "end": v(41.5, 61.97) * mm});
            skLineSegment(sketch, "E2289", {"start": v(41.5, 61.97) * mm, "end": v(26.5, 61.97) * mm});
            skArc(sketch, "E2290", {"start": v(38.51, 56.95) * mm, "mid": v(38.15, 57.83) * mm, "end": v(37.26, 58.2) * mm});
            skArc(sketch, "E2291", {"start": v(37.26, 58.2) * mm, "mid": v(36.38, 57.83) * mm, "end": v(36.01, 56.95) * mm});
            skArc(sketch, "E2292", {"start": v(36.01, 56.95) * mm, "mid": v(36.38, 56.07) * mm, "end": v(37.26, 55.7) * mm});
            skArc(sketch, "E2293", {"start": v(37.26, 55.7) * mm, "mid": v(38.15, 56.07) * mm, "end": v(38.51, 56.95) * mm});
            skArc(sketch, "E2294", {"start": v(32.01, 56.95) * mm, "mid": v(31.65, 57.83) * mm, "end": v(30.76, 58.2) * mm});
            skArc(sketch, "E2295", {"start": v(30.76, 58.2) * mm, "mid": v(29.88, 57.83) * mm, "end": v(29.51, 56.95) * mm});
            skArc(sketch, "E2296", {"start": v(29.51, 56.95) * mm, "mid": v(29.88, 56.07) * mm, "end": v(30.76, 55.7) * mm});
            skArc(sketch, "E2297", {"start": v(30.76, 55.7) * mm, "mid": v(31.65, 56.07) * mm, "end": v(32.01, 56.95) * mm});
            skArc(sketch, "E2298", {"start": v(39.76, 56.95) * mm, "mid": v(39.03, 58.72) * mm, "end": v(37.26, 59.45) * mm});
            skArc(sketch, "E2299", {"start": v(37.26, 59.45) * mm, "mid": v(35.5, 58.72) * mm, "end": v(34.76, 56.95) * mm});
            skArc(sketch, "E2300", {"start": v(34.76, 56.95) * mm, "mid": v(35.5, 55.18) * mm, "end": v(37.26, 54.45) * mm});
            skArc(sketch, "E2301", {"start": v(37.26, 54.45) * mm, "mid": v(39.03, 55.18) * mm, "end": v(39.76, 56.95) * mm});
            skArc(sketch, "E2302", {"start": v(33.26, 56.95) * mm, "mid": v(32.53, 58.72) * mm, "end": v(30.76, 59.45) * mm});
            skArc(sketch, "E2303", {"start": v(30.76, 59.45) * mm, "mid": v(29, 58.72) * mm, "end": v(28.26, 56.95) * mm});
            skArc(sketch, "E2304", {"start": v(28.26, 56.95) * mm, "mid": v(29, 55.18) * mm, "end": v(30.76, 54.45) * mm});
            skArc(sketch, "E2305", {"start": v(30.76, 54.45) * mm, "mid": v(32.53, 55.18) * mm, "end": v(33.26, 56.95) * mm});
            skLineSegment(sketch, "E2306", {"start": v(32.25, 37.94) * mm, "end": v(32.27, 37.88) * mm});
            skLineSegment(sketch, "E2307", {"start": v(32.27, 37.88) * mm, "end": v(32.35, 37.64) * mm});
            skLineSegment(sketch, "E2308", {"start": v(32.35, 37.64) * mm, "end": v(32.4, 37.5) * mm});
            skLineSegment(sketch, "E2309", {"start": v(32.4, 37.5) * mm, "end": v(32.44, 37.4) * mm});
            skLineSegment(sketch, "E2310", {"start": v(32.44, 37.4) * mm, "end": v(32.5, 37.32) * mm});
            skLineSegment(sketch, "E2311", {"start": v(32.5, 37.32) * mm, "end": v(32.57, 37.23) * mm});
            skLineSegment(sketch, "E2312", {"start": v(32.57, 37.23) * mm, "end": v(32.6, 37.19) * mm});
            skLineSegment(sketch, "E2313", {"start": v(32.6, 37.19) * mm, "end": v(32.6, 37.16) * mm});
            skLineSegment(sketch, "E2314", {"start": v(32.6, 37.16) * mm, "end": v(32.64, 37.1) * mm});
            skLineSegment(sketch, "E2315", {"start": v(32.64, 37.1) * mm, "end": v(32.73, 37.02) * mm});
            skLineSegment(sketch, "E2316", {"start": v(32.73, 37.02) * mm, "end": v(32.92, 36.83) * mm});
            skLineSegment(sketch, "E2317", {"start": v(32.92, 36.83) * mm, "end": v(32.97, 36.79) * mm});
            skLineSegment(sketch, "E2318", {"start": v(32.97, 36.79) * mm, "end": v(33.02, 36.77) * mm});
            skLineSegment(sketch, "E2319", {"start": v(33.02, 36.77) * mm, "end": v(33.04, 36.76) * mm});
            skLineSegment(sketch, "E2320", {"start": v(33.04, 36.76) * mm, "end": v(33.05, 36.74) * mm});
            skLineSegment(sketch, "E2321", {"start": v(33.05, 36.74) * mm, "end": v(33.08, 36.72) * mm});
            skLineSegment(sketch, "E2322", {"start": v(33.08, 36.72) * mm, "end": v(33.14, 36.69) * mm});
            skLineSegment(sketch, "E2323", {"start": v(33.14, 36.69) * mm, "end": v(33.42, 36.56) * mm});
            skLineSegment(sketch, "E2324", {"start": v(33.42, 36.56) * mm, "end": v(33.54, 36.52) * mm});
            skLineSegment(sketch, "E2325", {"start": v(33.54, 36.52) * mm, "end": v(33.68, 36.49) * mm});
            skLineSegment(sketch, "E2326", {"start": v(33.68, 36.49) * mm, "end": v(33.84, 36.47) * mm});
            skLineSegment(sketch, "E2327", {"start": v(33.84, 36.47) * mm, "end": v(34, 36.46) * mm});
            skLineSegment(sketch, "E2328", {"start": v(34, 36.46) * mm, "end": v(34.17, 36.47) * mm});
            skLineSegment(sketch, "E2329", {"start": v(34.17, 36.47) * mm, "end": v(34.33, 36.48) * mm});
            skLineSegment(sketch, "E2330", {"start": v(34.33, 36.48) * mm, "end": v(34.48, 36.51) * mm});
            skLineSegment(sketch, "E2331", {"start": v(34.48, 36.51) * mm, "end": v(34.6, 36.56) * mm});
            skLineSegment(sketch, "E2332", {"start": v(34.6, 36.56) * mm, "end": v(34.9, 36.68) * mm});
            skLineSegment(sketch, "E2333", {"start": v(34.9, 36.68) * mm, "end": v(34.96, 36.72) * mm});
            skLineSegment(sketch, "E2334", {"start": v(34.96, 36.72) * mm, "end": v(34.98, 36.74) * mm});
            skLineSegment(sketch, "E2335", {"start": v(34.98, 36.74) * mm, "end": v(34.99, 36.76) * mm});
            skLineSegment(sketch, "E2336", {"start": v(34.99, 36.76) * mm, "end": v(35, 36.77) * mm});
            skLineSegment(sketch, "E2337", {"start": v(35, 36.77) * mm, "end": v(35.04, 36.78) * mm});
            skLineSegment(sketch, "E2338", {"start": v(35.04, 36.78) * mm, "end": v(35.1, 36.82) * mm});
            skLineSegment(sketch, "E2339", {"start": v(35.1, 36.82) * mm, "end": v(35.24, 36.94) * mm});
            skLineSegment(sketch, "E2340", {"start": v(35.24, 36.94) * mm, "end": v(35.37, 37.08) * mm});
            skLineSegment(sketch, "E2341", {"start": v(35.37, 37.08) * mm, "end": v(35.4, 37.13) * mm});
            skLineSegment(sketch, "E2342", {"start": v(35.4, 37.13) * mm, "end": v(35.43, 37.16) * mm});
            skLineSegment(sketch, "E2343", {"start": v(35.43, 37.16) * mm, "end": v(35.44, 37.19) * mm});
            skLineSegment(sketch, "E2344", {"start": v(35.44, 37.19) * mm, "end": v(35.46, 37.23) * mm});
            skLineSegment(sketch, "E2345", {"start": v(35.46, 37.23) * mm, "end": v(35.53, 37.3) * mm});
            skLineSegment(sketch, "E2346", {"start": v(35.53, 37.3) * mm, "end": v(35.57, 37.37) * mm});
            skLineSegment(sketch, "E2347", {"start": v(35.57, 37.37) * mm, "end": v(35.61, 37.47) * mm});
            skLineSegment(sketch, "E2348", {"start": v(35.61, 37.47) * mm, "end": v(35.75, 37.87) * mm});
            skLineSegment(sketch, "E2349", {"start": v(35.75, 37.87) * mm, "end": v(35.78, 37.97) * mm});
            skLineSegment(sketch, "E2350", {"start": v(35.78, 37.97) * mm, "end": v(35.78, 44.96) * mm});
            skLineSegment(sketch, "E2351", {"start": v(35.78, 44.96) * mm, "end": v(35.76, 45.03) * mm});
            skLineSegment(sketch, "E2352", {"start": v(35.76, 45.03) * mm, "end": v(35.67, 45.28) * mm});
            skLineSegment(sketch, "E2353", {"start": v(35.67, 45.28) * mm, "end": v(35.6, 45.44) * mm});
            skLineSegment(sketch, "E2354", {"start": v(35.6, 45.44) * mm, "end": v(35.52, 45.6) * mm});
            skLineSegment(sketch, "E2355", {"start": v(35.52, 45.6) * mm, "end": v(35.45, 45.7) * mm});
            skLineSegment(sketch, "E2356", {"start": v(35.45, 45.7) * mm, "end": v(35.43, 45.75) * mm});
            skLineSegment(sketch, "E2357", {"start": v(35.43, 45.75) * mm, "end": v(35.4, 45.8) * mm});
            skLineSegment(sketch, "E2358", {"start": v(35.4, 45.8) * mm, "end": v(35.32, 45.87) * mm});
            skLineSegment(sketch, "E2359", {"start": v(35.32, 45.87) * mm, "end": v(35.07, 46.1) * mm});
            skLineSegment(sketch, "E2360", {"start": v(35.07, 46.1) * mm, "end": v(34.95, 46.18) * mm});
            skLineSegment(sketch, "E2361", {"start": v(34.95, 46.18) * mm, "end": v(34.8, 46.26) * mm});
            skLineSegment(sketch, "E2362", {"start": v(34.8, 46.26) * mm, "end": v(34.63, 46.34) * mm});
            skLineSegment(sketch, "E2363", {"start": v(34.63, 46.34) * mm, "end": v(34.47, 46.4) * mm});
            skLineSegment(sketch, "E2364", {"start": v(34.47, 46.4) * mm, "end": v(34.4, 46.4) * mm});
            skLineSegment(sketch, "E2365", {"start": v(34.4, 46.4) * mm, "end": v(34.28, 46.42) * mm});
            skLineSegment(sketch, "E2366", {"start": v(34.28, 46.42) * mm, "end": v(34.01, 46.43) * mm});
            skLineSegment(sketch, "E2367", {"start": v(34.01, 46.43) * mm, "end": v(33.75, 46.42) * mm});
            skLineSegment(sketch, "E2368", {"start": v(33.75, 46.42) * mm, "end": v(33.64, 46.4) * mm});
            skLineSegment(sketch, "E2369", {"start": v(33.64, 46.4) * mm, "end": v(33.55, 46.4) * mm});
            skLineSegment(sketch, "E2370", {"start": v(33.55, 46.4) * mm, "end": v(33.36, 46.32) * mm});
            skLineSegment(sketch, "E2371", {"start": v(33.36, 46.32) * mm, "end": v(33.16, 46.22) * mm});
            skLineSegment(sketch, "E2372", {"start": v(33.16, 46.22) * mm, "end": v(32.97, 46.1) * mm});
            skLineSegment(sketch, "E2373", {"start": v(32.97, 46.1) * mm, "end": v(32.8, 45.97) * mm});
            skLineSegment(sketch, "E2374", {"start": v(32.8, 45.97) * mm, "end": v(32.6, 45.78) * mm});
            skLineSegment(sketch, "E2375", {"start": v(32.6, 45.78) * mm, "end": v(32.6, 45.75) * mm});
            skLineSegment(sketch, "E2376", {"start": v(32.6, 45.75) * mm, "end": v(32.57, 45.7) * mm});
            skLineSegment(sketch, "E2377", {"start": v(32.57, 45.7) * mm, "end": v(32.5, 45.6) * mm});
            skLineSegment(sketch, "E2378", {"start": v(32.5, 45.6) * mm, "end": v(32.42, 45.44) * mm});
            skLineSegment(sketch, "E2379", {"start": v(32.42, 45.44) * mm, "end": v(32.35, 45.28) * mm});
            skLineSegment(sketch, "E2380", {"start": v(32.35, 45.28) * mm, "end": v(32.27, 45.03) * mm});
            skLineSegment(sketch, "E2381", {"start": v(32.27, 45.03) * mm, "end": v(32.25, 44.96) * mm});
            skLineSegment(sketch, "E2382", {"start": v(32.25, 44.96) * mm, "end": v(32.25, 37.94) * mm});
            skLineSegment(sketch, "E2383", {"start": v(41.5, 48.73) * mm, "end": v(41.5, 45.73) * mm});
            skLineSegment(sketch, "E2384", {"start": v(41.5, 45.73) * mm, "end": v(43.5, 45.73) * mm});
            skLineSegment(sketch, "E2385", {"start": v(43.5, 45.73) * mm, "end": v(43.5, 48.73) * mm});
            skLineSegment(sketch, "E2386", {"start": v(43.5, 48.73) * mm, "end": v(41.5, 48.73) * mm});
            skLineSegment(sketch, "E2387", {"start": v(9.5, 61.97) * mm, "end": v(9.5, 32.48) * mm});
            skLineSegment(sketch, "E2388", {"start": v(9.5, 32.48) * mm, "end": v(24.5, 32.48) * mm});
            skLineSegment(sketch, "E2389", {"start": v(24.5, 32.48) * mm, "end": v(24.5, 61.97) * mm});
            skLineSegment(sketch, "E2390", {"start": v(24.5, 61.97) * mm, "end": v(9.5, 61.97) * mm});
            skArc(sketch, "E2391", {"start": v(21.51, 56.95) * mm, "mid": v(21.15, 57.83) * mm, "end": v(20.26, 58.2) * mm});
            skArc(sketch, "E2392", {"start": v(20.26, 58.2) * mm, "mid": v(19.38, 57.83) * mm, "end": v(19.01, 56.95) * mm});
            skArc(sketch, "E2393", {"start": v(19.01, 56.95) * mm, "mid": v(19.38, 56.07) * mm, "end": v(20.26, 55.7) * mm});
            skArc(sketch, "E2394", {"start": v(20.26, 55.7) * mm, "mid": v(21.15, 56.07) * mm, "end": v(21.51, 56.95) * mm});
            skArc(sketch, "E2395", {"start": v(15.01, 56.95) * mm, "mid": v(14.65, 57.83) * mm, "end": v(13.76, 58.2) * mm});
            skArc(sketch, "E2396", {"start": v(13.76, 58.2) * mm, "mid": v(12.88, 57.83) * mm, "end": v(12.51, 56.95) * mm});
            skArc(sketch, "E2397", {"start": v(12.51, 56.95) * mm, "mid": v(12.88, 56.07) * mm, "end": v(13.76, 55.7) * mm});
            skArc(sketch, "E2398", {"start": v(13.76, 55.7) * mm, "mid": v(14.65, 56.07) * mm, "end": v(15.01, 56.95) * mm});
            skArc(sketch, "E2399", {"start": v(22.76, 56.95) * mm, "mid": v(22.03, 58.72) * mm, "end": v(20.26, 59.45) * mm});
            skArc(sketch, "E2400", {"start": v(20.26, 59.45) * mm, "mid": v(18.5, 58.72) * mm, "end": v(17.76, 56.95) * mm});
            skArc(sketch, "E2401", {"start": v(17.76, 56.95) * mm, "mid": v(18.5, 55.18) * mm, "end": v(20.26, 54.45) * mm});
            skArc(sketch, "E2402", {"start": v(20.26, 54.45) * mm, "mid": v(22.03, 55.18) * mm, "end": v(22.76, 56.95) * mm});
            skArc(sketch, "E2403", {"start": v(16.26, 56.95) * mm, "mid": v(15.53, 58.72) * mm, "end": v(13.76, 59.45) * mm});
            skArc(sketch, "E2404", {"start": v(13.76, 59.45) * mm, "mid": v(12, 58.72) * mm, "end": v(11.26, 56.95) * mm});
            skArc(sketch, "E2405", {"start": v(11.26, 56.95) * mm, "mid": v(12, 55.18) * mm, "end": v(13.76, 54.45) * mm});
            skArc(sketch, "E2406", {"start": v(13.76, 54.45) * mm, "mid": v(15.53, 55.18) * mm, "end": v(16.26, 56.95) * mm});
            skLineSegment(sketch, "E2407", {"start": v(15.5, 30.48) * mm, "end": v(18.5, 30.48) * mm});
            skLineSegment(sketch, "E2408", {"start": v(18.5, 30.48) * mm, "end": v(18.5, 32.48) * mm});
            skLineSegment(sketch, "E2409", {"start": v(18.5, 32.48) * mm, "end": v(15.5, 32.48) * mm});
            skLineSegment(sketch, "E2410", {"start": v(15.5, 32.48) * mm, "end": v(15.5, 30.48) * mm});
            skLineSegment(sketch, "E2411", {"start": v(15.25, 37.94) * mm, "end": v(15.27, 37.88) * mm});
            skLineSegment(sketch, "E2412", {"start": v(15.27, 37.88) * mm, "end": v(15.35, 37.64) * mm});
            skLineSegment(sketch, "E2413", {"start": v(15.35, 37.64) * mm, "end": v(15.4, 37.5) * mm});
            skLineSegment(sketch, "E2414", {"start": v(15.4, 37.5) * mm, "end": v(15.44, 37.4) * mm});
            skLineSegment(sketch, "E2415", {"start": v(15.44, 37.4) * mm, "end": v(15.5, 37.32) * mm});
            skLineSegment(sketch, "E2416", {"start": v(15.5, 37.32) * mm, "end": v(15.57, 37.23) * mm});
            skLineSegment(sketch, "E2417", {"start": v(15.57, 37.23) * mm, "end": v(15.6, 37.19) * mm});
            skLineSegment(sketch, "E2418", {"start": v(15.6, 37.19) * mm, "end": v(15.6, 37.16) * mm});
            skLineSegment(sketch, "E2419", {"start": v(15.6, 37.16) * mm, "end": v(15.64, 37.1) * mm});
            skLineSegment(sketch, "E2420", {"start": v(15.64, 37.1) * mm, "end": v(15.73, 37.02) * mm});
            skLineSegment(sketch, "E2421", {"start": v(15.73, 37.02) * mm, "end": v(15.92, 36.83) * mm});
            skLineSegment(sketch, "E2422", {"start": v(15.92, 36.83) * mm, "end": v(15.97, 36.79) * mm});
            skLineSegment(sketch, "E2423", {"start": v(15.97, 36.79) * mm, "end": v(16.02, 36.77) * mm});
            skLineSegment(sketch, "E2424", {"start": v(16.02, 36.77) * mm, "end": v(16.04, 36.76) * mm});
            skLineSegment(sketch, "E2425", {"start": v(16.04, 36.76) * mm, "end": v(16.05, 36.74) * mm});
            skLineSegment(sketch, "E2426", {"start": v(16.05, 36.74) * mm, "end": v(16.08, 36.72) * mm});
            skLineSegment(sketch, "E2427", {"start": v(16.08, 36.72) * mm, "end": v(16.14, 36.69) * mm});
            skLineSegment(sketch, "E2428", {"start": v(16.14, 36.69) * mm, "end": v(16.42, 36.56) * mm});
            skLineSegment(sketch, "E2429", {"start": v(16.42, 36.56) * mm, "end": v(16.54, 36.52) * mm});
            skLineSegment(sketch, "E2430", {"start": v(16.54, 36.52) * mm, "end": v(16.68, 36.49) * mm});
            skLineSegment(sketch, "E2431", {"start": v(16.68, 36.49) * mm, "end": v(16.84, 36.47) * mm});
            skLineSegment(sketch, "E2432", {"start": v(16.84, 36.47) * mm, "end": v(17, 36.46) * mm});
            skLineSegment(sketch, "E2433", {"start": v(17, 36.46) * mm, "end": v(17.17, 36.47) * mm});
            skLineSegment(sketch, "E2434", {"start": v(17.17, 36.47) * mm, "end": v(17.33, 36.48) * mm});
            skLineSegment(sketch, "E2435", {"start": v(17.33, 36.48) * mm, "end": v(17.48, 36.51) * mm});
            skLineSegment(sketch, "E2436", {"start": v(17.48, 36.51) * mm, "end": v(17.6, 36.56) * mm});
            skLineSegment(sketch, "E2437", {"start": v(17.6, 36.56) * mm, "end": v(17.9, 36.68) * mm});
            skLineSegment(sketch, "E2438", {"start": v(17.9, 36.68) * mm, "end": v(17.96, 36.72) * mm});
            skLineSegment(sketch, "E2439", {"start": v(17.96, 36.72) * mm, "end": v(17.98, 36.74) * mm});
            skLineSegment(sketch, "E2440", {"start": v(17.98, 36.74) * mm, "end": v(17.99, 36.76) * mm});
            skLineSegment(sketch, "E2441", {"start": v(17.99, 36.76) * mm, "end": v(18, 36.77) * mm});
            skLineSegment(sketch, "E2442", {"start": v(18, 36.77) * mm, "end": v(18.04, 36.78) * mm});
            skLineSegment(sketch, "E2443", {"start": v(18.04, 36.78) * mm, "end": v(18.1, 36.82) * mm});
            skLineSegment(sketch, "E2444", {"start": v(18.1, 36.82) * mm, "end": v(18.24, 36.94) * mm});
            skLineSegment(sketch, "E2445", {"start": v(18.24, 36.94) * mm, "end": v(18.37, 37.08) * mm});
            skLineSegment(sketch, "E2446", {"start": v(18.37, 37.08) * mm, "end": v(18.4, 37.13) * mm});
            skLineSegment(sketch, "E2447", {"start": v(18.4, 37.13) * mm, "end": v(18.43, 37.16) * mm});
            skLineSegment(sketch, "E2448", {"start": v(18.43, 37.16) * mm, "end": v(18.44, 37.19) * mm});
            skLineSegment(sketch, "E2449", {"start": v(18.44, 37.19) * mm, "end": v(18.46, 37.23) * mm});
            skLineSegment(sketch, "E2450", {"start": v(18.46, 37.23) * mm, "end": v(18.53, 37.3) * mm});
            skLineSegment(sketch, "E2451", {"start": v(18.53, 37.3) * mm, "end": v(18.57, 37.37) * mm});
            skLineSegment(sketch, "E2452", {"start": v(18.57, 37.37) * mm, "end": v(18.61, 37.47) * mm});
            skLineSegment(sketch, "E2453", {"start": v(18.61, 37.47) * mm, "end": v(18.75, 37.87) * mm});
            skLineSegment(sketch, "E2454", {"start": v(18.75, 37.87) * mm, "end": v(18.78, 37.97) * mm});
            skLineSegment(sketch, "E2455", {"start": v(18.78, 37.97) * mm, "end": v(18.78, 44.96) * mm});
            skLineSegment(sketch, "E2456", {"start": v(18.78, 44.96) * mm, "end": v(18.76, 45.03) * mm});
            skLineSegment(sketch, "E2457", {"start": v(18.76, 45.03) * mm, "end": v(18.67, 45.28) * mm});
            skLineSegment(sketch, "E2458", {"start": v(18.67, 45.28) * mm, "end": v(18.6, 45.44) * mm});
            skLineSegment(sketch, "E2459", {"start": v(18.6, 45.44) * mm, "end": v(18.52, 45.6) * mm});
            skLineSegment(sketch, "E2460", {"start": v(18.52, 45.6) * mm, "end": v(18.45, 45.7) * mm});
            skLineSegment(sketch, "E2461", {"start": v(18.45, 45.7) * mm, "end": v(18.43, 45.75) * mm});
            skLineSegment(sketch, "E2462", {"start": v(18.43, 45.75) * mm, "end": v(18.4, 45.8) * mm});
            skLineSegment(sketch, "E2463", {"start": v(18.4, 45.8) * mm, "end": v(18.32, 45.87) * mm});
            skLineSegment(sketch, "E2464", {"start": v(18.32, 45.87) * mm, "end": v(18.07, 46.1) * mm});
            skLineSegment(sketch, "E2465", {"start": v(18.07, 46.1) * mm, "end": v(17.95, 46.18) * mm});
            skLineSegment(sketch, "E2466", {"start": v(17.95, 46.18) * mm, "end": v(17.8, 46.26) * mm});
            skLineSegment(sketch, "E2467", {"start": v(17.8, 46.26) * mm, "end": v(17.63, 46.34) * mm});
            skLineSegment(sketch, "E2468", {"start": v(17.63, 46.34) * mm, "end": v(17.47, 46.4) * mm});
            skLineSegment(sketch, "E2469", {"start": v(17.47, 46.4) * mm, "end": v(17.4, 46.4) * mm});
            skLineSegment(sketch, "E2470", {"start": v(17.4, 46.4) * mm, "end": v(17.28, 46.42) * mm});
            skLineSegment(sketch, "E2471", {"start": v(17.28, 46.42) * mm, "end": v(17.01, 46.43) * mm});
            skLineSegment(sketch, "E2472", {"start": v(17.01, 46.43) * mm, "end": v(16.75, 46.42) * mm});
            skLineSegment(sketch, "E2473", {"start": v(16.75, 46.42) * mm, "end": v(16.64, 46.4) * mm});
            skLineSegment(sketch, "E2474", {"start": v(16.64, 46.4) * mm, "end": v(16.55, 46.4) * mm});
            skLineSegment(sketch, "E2475", {"start": v(16.55, 46.4) * mm, "end": v(16.36, 46.32) * mm});
            skLineSegment(sketch, "E2476", {"start": v(16.36, 46.32) * mm, "end": v(16.16, 46.22) * mm});
            skLineSegment(sketch, "E2477", {"start": v(16.16, 46.22) * mm, "end": v(15.97, 46.1) * mm});
            skLineSegment(sketch, "E2478", {"start": v(15.97, 46.1) * mm, "end": v(15.8, 45.97) * mm});
            skLineSegment(sketch, "E2479", {"start": v(15.8, 45.97) * mm, "end": v(15.6, 45.78) * mm});
            skLineSegment(sketch, "E2480", {"start": v(15.6, 45.78) * mm, "end": v(15.6, 45.75) * mm});
            skLineSegment(sketch, "E2481", {"start": v(15.6, 45.75) * mm, "end": v(15.57, 45.7) * mm});
            skLineSegment(sketch, "E2482", {"start": v(15.57, 45.7) * mm, "end": v(15.5, 45.6) * mm});
            skLineSegment(sketch, "E2483", {"start": v(15.5, 45.6) * mm, "end": v(15.42, 45.44) * mm});
            skLineSegment(sketch, "E2484", {"start": v(15.42, 45.44) * mm, "end": v(15.35, 45.28) * mm});
            skLineSegment(sketch, "E2485", {"start": v(15.35, 45.28) * mm, "end": v(15.27, 45.03) * mm});
            skLineSegment(sketch, "E2486", {"start": v(15.27, 45.03) * mm, "end": v(15.25, 44.96) * mm});
            skLineSegment(sketch, "E2487", {"start": v(15.25, 44.96) * mm, "end": v(15.25, 37.94) * mm});
            skLineSegment(sketch, "E2488", {"start": v(24.5, 48.73) * mm, "end": v(24.5, 45.73) * mm});
            skLineSegment(sketch, "E2489", {"start": v(24.5, 45.73) * mm, "end": v(26.5, 45.73) * mm});
            skLineSegment(sketch, "E2490", {"start": v(26.5, 45.73) * mm, "end": v(26.5, 48.73) * mm});
            skLineSegment(sketch, "E2491", {"start": v(26.5, 48.73) * mm, "end": v(24.5, 48.73) * mm});
            skLineSegment(sketch, "E2492", {"start": v(-7.5, 61.97) * mm, "end": v(-7.5, 32.48) * mm});
            skLineSegment(sketch, "E2493", {"start": v(-7.5, 32.48) * mm, "end": v(7.5, 32.48) * mm});
            skLineSegment(sketch, "E2494", {"start": v(7.5, 32.48) * mm, "end": v(7.5, 61.97) * mm});
            skLineSegment(sketch, "E2495", {"start": v(7.5, 61.97) * mm, "end": v(-7.5, 61.97) * mm});
            skArc(sketch, "E2496", {"start": v(4.51, 56.95) * mm, "mid": v(4.15, 57.83) * mm, "end": v(3.26, 58.2) * mm});
            skArc(sketch, "E2497", {"start": v(3.26, 58.2) * mm, "mid": v(2.38, 57.83) * mm, "end": v(2.01, 56.95) * mm});
            skArc(sketch, "E2498", {"start": v(2.01, 56.95) * mm, "mid": v(2.38, 56.07) * mm, "end": v(3.26, 55.7) * mm});
            skArc(sketch, "E2499", {"start": v(3.26, 55.7) * mm, "mid": v(4.15, 56.07) * mm, "end": v(4.51, 56.95) * mm});
            skArc(sketch, "E2500", {"start": v(-1.99, 56.95) * mm, "mid": v(-2.35, 57.83) * mm, "end": v(-3.24, 58.2) * mm});
            skArc(sketch, "E2501", {"start": v(-3.24, 58.2) * mm, "mid": v(-4.12, 57.83) * mm, "end": v(-4.49, 56.95) * mm});
            skArc(sketch, "E2502", {"start": v(-4.49, 56.95) * mm, "mid": v(-4.12, 56.07) * mm, "end": v(-3.24, 55.7) * mm});
            skArc(sketch, "E2503", {"start": v(-3.24, 55.7) * mm, "mid": v(-2.35, 56.07) * mm, "end": v(-1.99, 56.95) * mm});
            skArc(sketch, "E2504", {"start": v(5.76, 56.95) * mm, "mid": v(5.03, 58.72) * mm, "end": v(3.26, 59.45) * mm});
            skArc(sketch, "E2505", {"start": v(3.26, 59.45) * mm, "mid": v(1.5, 58.72) * mm, "end": v(0.76, 56.95) * mm});
            skArc(sketch, "E2506", {"start": v(0.76, 56.95) * mm, "mid": v(1.5, 55.18) * mm, "end": v(3.26, 54.45) * mm});
            skArc(sketch, "E2507", {"start": v(3.26, 54.45) * mm, "mid": v(5.03, 55.18) * mm, "end": v(5.76, 56.95) * mm});
            skArc(sketch, "E2508", {"start": v(-0.74, 56.95) * mm, "mid": v(-1.47, 58.72) * mm, "end": v(-3.24, 59.45) * mm});
            skArc(sketch, "E2509", {"start": v(-3.24, 59.45) * mm, "mid": v(-5, 58.72) * mm, "end": v(-5.74, 56.95) * mm});
            skArc(sketch, "E2510", {"start": v(-5.74, 56.95) * mm, "mid": v(-5, 55.18) * mm, "end": v(-3.24, 54.45) * mm});
            skArc(sketch, "E2511", {"start": v(-3.24, 54.45) * mm, "mid": v(-1.47, 55.18) * mm, "end": v(-0.74, 56.95) * mm});
            skLineSegment(sketch, "E2512", {"start": v(-9.5, 48.73) * mm, "end": v(-9.5, 45.73) * mm});
            skLineSegment(sketch, "E2513", {"start": v(-9.5, 45.73) * mm, "end": v(-7.5, 45.73) * mm});
            skLineSegment(sketch, "E2514", {"start": v(-7.5, 45.73) * mm, "end": v(-7.5, 48.73) * mm});
            skLineSegment(sketch, "E2515", {"start": v(-7.5, 48.73) * mm, "end": v(-9.5, 48.73) * mm});
            skLineSegment(sketch, "E2516", {"start": v(-1.75, 37.94) * mm, "end": v(-1.73, 37.88) * mm});
            skLineSegment(sketch, "E2517", {"start": v(-1.73, 37.88) * mm, "end": v(-1.65, 37.64) * mm});
            skLineSegment(sketch, "E2518", {"start": v(-1.65, 37.64) * mm, "end": v(-1.6, 37.5) * mm});
            skLineSegment(sketch, "E2519", {"start": v(-1.6, 37.5) * mm, "end": v(-1.56, 37.4) * mm});
            skLineSegment(sketch, "E2520", {"start": v(-1.56, 37.4) * mm, "end": v(-1.5, 37.32) * mm});
            skLineSegment(sketch, "E2521", {"start": v(-1.5, 37.32) * mm, "end": v(-1.43, 37.23) * mm});
            skLineSegment(sketch, "E2522", {"start": v(-1.43, 37.23) * mm, "end": v(-1.4, 37.19) * mm});
            skLineSegment(sketch, "E2523", {"start": v(-1.4, 37.19) * mm, "end": v(-1.4, 37.16) * mm});
            skLineSegment(sketch, "E2524", {"start": v(-1.4, 37.16) * mm, "end": v(-1.36, 37.1) * mm});
            skLineSegment(sketch, "E2525", {"start": v(-1.36, 37.1) * mm, "end": v(-1.27, 37.02) * mm});
            skLineSegment(sketch, "E2526", {"start": v(-1.27, 37.02) * mm, "end": v(-1.08, 36.83) * mm});
            skLineSegment(sketch, "E2527", {"start": v(-1.08, 36.83) * mm, "end": v(-1.03, 36.79) * mm});
            skLineSegment(sketch, "E2528", {"start": v(-1.03, 36.79) * mm, "end": v(-0.98, 36.77) * mm});
            skLineSegment(sketch, "E2529", {"start": v(-0.98, 36.77) * mm, "end": v(-0.96, 36.76) * mm});
            skLineSegment(sketch, "E2530", {"start": v(-0.96, 36.76) * mm, "end": v(-0.95, 36.74) * mm});
            skLineSegment(sketch, "E2531", {"start": v(-0.95, 36.74) * mm, "end": v(-0.92, 36.72) * mm});
            skLineSegment(sketch, "E2532", {"start": v(-0.92, 36.72) * mm, "end": v(-0.86, 36.69) * mm});
            skLineSegment(sketch, "E2533", {"start": v(-0.86, 36.69) * mm, "end": v(-0.58, 36.56) * mm});
            skLineSegment(sketch, "E2534", {"start": v(-0.58, 36.56) * mm, "end": v(-0.46, 36.52) * mm});
            skLineSegment(sketch, "E2535", {"start": v(-0.46, 36.52) * mm, "end": v(-0.32, 36.49) * mm});
            skLineSegment(sketch, "E2536", {"start": v(-0.32, 36.49) * mm, "end": v(-0.16, 36.47) * mm});
            skLineSegment(sketch, "E2537", {"start": v(-0.16, 36.47) * mm, "end": v(0, 36.46) * mm});
            skLineSegment(sketch, "E2538", {"start": v(0, 36.46) * mm, "end": v(0.17, 36.47) * mm});
            skLineSegment(sketch, "E2539", {"start": v(0.17, 36.47) * mm, "end": v(0.33, 36.48) * mm});
            skLineSegment(sketch, "E2540", {"start": v(0.33, 36.48) * mm, "end": v(0.48, 36.51) * mm});
            skLineSegment(sketch, "E2541", {"start": v(0.48, 36.51) * mm, "end": v(0.6, 36.56) * mm});
            skLineSegment(sketch, "E2542", {"start": v(0.6, 36.56) * mm, "end": v(0.9, 36.68) * mm});
            skLineSegment(sketch, "E2543", {"start": v(0.9, 36.68) * mm, "end": v(0.96, 36.72) * mm});
            skLineSegment(sketch, "E2544", {"start": v(0.96, 36.72) * mm, "end": v(0.98, 36.74) * mm});
            skLineSegment(sketch, "E2545", {"start": v(0.98, 36.74) * mm, "end": v(0.99, 36.76) * mm});
            skLineSegment(sketch, "E2546", {"start": v(0.99, 36.76) * mm, "end": v(1, 36.77) * mm});
            skLineSegment(sketch, "E2547", {"start": v(1, 36.77) * mm, "end": v(1.04, 36.78) * mm});
            skLineSegment(sketch, "E2548", {"start": v(1.04, 36.78) * mm, "end": v(1.1, 36.82) * mm});
            skLineSegment(sketch, "E2549", {"start": v(1.1, 36.82) * mm, "end": v(1.24, 36.94) * mm});
            skLineSegment(sketch, "E2550", {"start": v(1.24, 36.94) * mm, "end": v(1.37, 37.08) * mm});
            skLineSegment(sketch, "E2551", {"start": v(1.37, 37.08) * mm, "end": v(1.4, 37.13) * mm});
            skLineSegment(sketch, "E2552", {"start": v(1.4, 37.13) * mm, "end": v(1.43, 37.16) * mm});
            skLineSegment(sketch, "E2553", {"start": v(1.43, 37.16) * mm, "end": v(1.44, 37.19) * mm});
            skLineSegment(sketch, "E2554", {"start": v(1.44, 37.19) * mm, "end": v(1.46, 37.23) * mm});
            skLineSegment(sketch, "E2555", {"start": v(1.46, 37.23) * mm, "end": v(1.53, 37.3) * mm});
            skLineSegment(sketch, "E2556", {"start": v(1.53, 37.3) * mm, "end": v(1.57, 37.37) * mm});
            skLineSegment(sketch, "E2557", {"start": v(1.57, 37.37) * mm, "end": v(1.61, 37.47) * mm});
            skLineSegment(sketch, "E2558", {"start": v(1.61, 37.47) * mm, "end": v(1.75, 37.87) * mm});
            skLineSegment(sketch, "E2559", {"start": v(1.75, 37.87) * mm, "end": v(1.78, 37.97) * mm});
            skLineSegment(sketch, "E2560", {"start": v(1.78, 37.97) * mm, "end": v(1.78, 44.96) * mm});
            skLineSegment(sketch, "E2561", {"start": v(1.78, 44.96) * mm, "end": v(1.76, 45.03) * mm});
            skLineSegment(sketch, "E2562", {"start": v(1.76, 45.03) * mm, "end": v(1.67, 45.28) * mm});
            skLineSegment(sketch, "E2563", {"start": v(1.67, 45.28) * mm, "end": v(1.6, 45.44) * mm});
            skLineSegment(sketch, "E2564", {"start": v(1.6, 45.44) * mm, "end": v(1.52, 45.6) * mm});
            skLineSegment(sketch, "E2565", {"start": v(1.52, 45.6) * mm, "end": v(1.45, 45.7) * mm});
            skLineSegment(sketch, "E2566", {"start": v(1.45, 45.7) * mm, "end": v(1.43, 45.75) * mm});
            skLineSegment(sketch, "E2567", {"start": v(1.43, 45.75) * mm, "end": v(1.4, 45.8) * mm});
            skLineSegment(sketch, "E2568", {"start": v(1.4, 45.8) * mm, "end": v(1.32, 45.87) * mm});
            skLineSegment(sketch, "E2569", {"start": v(1.32, 45.87) * mm, "end": v(1.07, 46.1) * mm});
            skLineSegment(sketch, "E2570", {"start": v(1.07, 46.1) * mm, "end": v(0.95, 46.18) * mm});
            skLineSegment(sketch, "E2571", {"start": v(0.95, 46.18) * mm, "end": v(0.8, 46.26) * mm});
            skLineSegment(sketch, "E2572", {"start": v(0.8, 46.26) * mm, "end": v(0.63, 46.34) * mm});
            skLineSegment(sketch, "E2573", {"start": v(0.63, 46.34) * mm, "end": v(0.47, 46.4) * mm});
            skLineSegment(sketch, "E2574", {"start": v(0.47, 46.4) * mm, "end": v(0.4, 46.4) * mm});
            skLineSegment(sketch, "E2575", {"start": v(0.4, 46.4) * mm, "end": v(0.28, 46.42) * mm});
            skLineSegment(sketch, "E2576", {"start": v(0.28, 46.42) * mm, "end": v(0.01, 46.43) * mm});
            skLineSegment(sketch, "E2577", {"start": v(0.01, 46.43) * mm, "end": v(-0.25, 46.42) * mm});
            skLineSegment(sketch, "E2578", {"start": v(-0.25, 46.42) * mm, "end": v(-0.36, 46.4) * mm});
            skLineSegment(sketch, "E2579", {"start": v(-0.36, 46.4) * mm, "end": v(-0.45, 46.4) * mm});
            skLineSegment(sketch, "E2580", {"start": v(-0.45, 46.4) * mm, "end": v(-0.64, 46.32) * mm});
            skLineSegment(sketch, "E2581", {"start": v(-0.64, 46.32) * mm, "end": v(-0.84, 46.22) * mm});
            skLineSegment(sketch, "E2582", {"start": v(-0.84, 46.22) * mm, "end": v(-1.03, 46.1) * mm});
            skLineSegment(sketch, "E2583", {"start": v(-1.03, 46.1) * mm, "end": v(-1.2, 45.97) * mm});
            skLineSegment(sketch, "E2584", {"start": v(-1.2, 45.97) * mm, "end": v(-1.4, 45.78) * mm});
            skLineSegment(sketch, "E2585", {"start": v(-1.4, 45.78) * mm, "end": v(-1.4, 45.75) * mm});
            skLineSegment(sketch, "E2586", {"start": v(-1.4, 45.75) * mm, "end": v(-1.43, 45.7) * mm});
            skLineSegment(sketch, "E2587", {"start": v(-1.43, 45.7) * mm, "end": v(-1.5, 45.6) * mm});
            skLineSegment(sketch, "E2588", {"start": v(-1.5, 45.6) * mm, "end": v(-1.58, 45.44) * mm});
            skLineSegment(sketch, "E2589", {"start": v(-1.58, 45.44) * mm, "end": v(-1.65, 45.28) * mm});
            skLineSegment(sketch, "E2590", {"start": v(-1.65, 45.28) * mm, "end": v(-1.73, 45.03) * mm});
            skLineSegment(sketch, "E2591", {"start": v(-1.73, 45.03) * mm, "end": v(-1.75, 44.96) * mm});
            skLineSegment(sketch, "E2592", {"start": v(-1.75, 44.96) * mm, "end": v(-1.75, 37.94) * mm});
            skLineSegment(sketch, "E2593", {"start": v(7.5, 48.73) * mm, "end": v(7.5, 45.73) * mm});
            skLineSegment(sketch, "E2594", {"start": v(7.5, 45.73) * mm, "end": v(9.5, 45.73) * mm});
            skLineSegment(sketch, "E2595", {"start": v(9.5, 45.73) * mm, "end": v(9.5, 48.73) * mm});
            skLineSegment(sketch, "E2596", {"start": v(9.5, 48.73) * mm, "end": v(7.5, 48.73) * mm});
            skLineSegment(sketch, "E2597", {"start": v(-24.5, 61.97) * mm, "end": v(-24.5, 32.48) * mm});
            skLineSegment(sketch, "E2598", {"start": v(-24.5, 32.48) * mm, "end": v(-9.5, 32.48) * mm});
            skLineSegment(sketch, "E2599", {"start": v(-9.5, 32.48) * mm, "end": v(-9.5, 61.97) * mm});
            skLineSegment(sketch, "E2600", {"start": v(-9.5, 61.97) * mm, "end": v(-24.5, 61.97) * mm});
            skArc(sketch, "E2601", {"start": v(-12.49, 56.95) * mm, "mid": v(-12.85, 57.83) * mm, "end": v(-13.74, 58.2) * mm});
            skArc(sketch, "E2602", {"start": v(-13.74, 58.2) * mm, "mid": v(-14.62, 57.83) * mm, "end": v(-14.99, 56.95) * mm});
            skArc(sketch, "E2603", {"start": v(-14.99, 56.95) * mm, "mid": v(-14.62, 56.07) * mm, "end": v(-13.74, 55.7) * mm});
            skArc(sketch, "E2604", {"start": v(-13.74, 55.7) * mm, "mid": v(-12.85, 56.07) * mm, "end": v(-12.49, 56.95) * mm});
            skArc(sketch, "E2605", {"start": v(-18.99, 56.95) * mm, "mid": v(-19.35, 57.83) * mm, "end": v(-20.24, 58.2) * mm});
            skArc(sketch, "E2606", {"start": v(-20.24, 58.2) * mm, "mid": v(-21.12, 57.83) * mm, "end": v(-21.49, 56.95) * mm});
            skArc(sketch, "E2607", {"start": v(-21.49, 56.95) * mm, "mid": v(-21.12, 56.07) * mm, "end": v(-20.24, 55.7) * mm});
            skArc(sketch, "E2608", {"start": v(-20.24, 55.7) * mm, "mid": v(-19.35, 56.07) * mm, "end": v(-18.99, 56.95) * mm});
            skArc(sketch, "E2609", {"start": v(-11.24, 56.95) * mm, "mid": v(-11.97, 58.72) * mm, "end": v(-13.74, 59.45) * mm});
            skArc(sketch, "E2610", {"start": v(-13.74, 59.45) * mm, "mid": v(-15.5, 58.72) * mm, "end": v(-16.24, 56.95) * mm});
            skArc(sketch, "E2611", {"start": v(-16.24, 56.95) * mm, "mid": v(-15.5, 55.18) * mm, "end": v(-13.74, 54.45) * mm});
            skArc(sketch, "E2612", {"start": v(-13.74, 54.45) * mm, "mid": v(-11.97, 55.18) * mm, "end": v(-11.24, 56.95) * mm});
            skArc(sketch, "E2613", {"start": v(-17.74, 56.95) * mm, "mid": v(-18.47, 58.72) * mm, "end": v(-20.24, 59.45) * mm});
            skArc(sketch, "E2614", {"start": v(-20.24, 59.45) * mm, "mid": v(-22, 58.72) * mm, "end": v(-22.74, 56.95) * mm});
            skArc(sketch, "E2615", {"start": v(-22.74, 56.95) * mm, "mid": v(-22, 55.18) * mm, "end": v(-20.24, 54.45) * mm});
            skArc(sketch, "E2616", {"start": v(-20.24, 54.45) * mm, "mid": v(-18.47, 55.18) * mm, "end": v(-17.74, 56.95) * mm});
            skLineSegment(sketch, "E2617", {"start": v(-18.75, 37.94) * mm, "end": v(-18.73, 37.88) * mm});
            skLineSegment(sketch, "E2618", {"start": v(-18.73, 37.88) * mm, "end": v(-18.65, 37.64) * mm});
            skLineSegment(sketch, "E2619", {"start": v(-18.65, 37.64) * mm, "end": v(-18.6, 37.5) * mm});
            skLineSegment(sketch, "E2620", {"start": v(-18.6, 37.5) * mm, "end": v(-18.56, 37.4) * mm});
            skLineSegment(sketch, "E2621", {"start": v(-18.56, 37.4) * mm, "end": v(-18.5, 37.32) * mm});
            skLineSegment(sketch, "E2622", {"start": v(-18.5, 37.32) * mm, "end": v(-18.43, 37.23) * mm});
            skLineSegment(sketch, "E2623", {"start": v(-18.43, 37.23) * mm, "end": v(-18.4, 37.19) * mm});
            skLineSegment(sketch, "E2624", {"start": v(-18.4, 37.19) * mm, "end": v(-18.4, 37.16) * mm});
            skLineSegment(sketch, "E2625", {"start": v(-18.4, 37.16) * mm, "end": v(-18.36, 37.1) * mm});
            skLineSegment(sketch, "E2626", {"start": v(-18.36, 37.1) * mm, "end": v(-18.27, 37.02) * mm});
            skLineSegment(sketch, "E2627", {"start": v(-18.27, 37.02) * mm, "end": v(-18.08, 36.83) * mm});
            skLineSegment(sketch, "E2628", {"start": v(-18.08, 36.83) * mm, "end": v(-18.03, 36.79) * mm});
            skLineSegment(sketch, "E2629", {"start": v(-18.03, 36.79) * mm, "end": v(-17.98, 36.77) * mm});
            skLineSegment(sketch, "E2630", {"start": v(-17.98, 36.77) * mm, "end": v(-17.96, 36.76) * mm});
            skLineSegment(sketch, "E2631", {"start": v(-17.96, 36.76) * mm, "end": v(-17.95, 36.74) * mm});
            skLineSegment(sketch, "E2632", {"start": v(-17.95, 36.74) * mm, "end": v(-17.92, 36.72) * mm});
            skLineSegment(sketch, "E2633", {"start": v(-17.92, 36.72) * mm, "end": v(-17.86, 36.69) * mm});
            skLineSegment(sketch, "E2634", {"start": v(-17.86, 36.69) * mm, "end": v(-17.58, 36.56) * mm});
            skLineSegment(sketch, "E2635", {"start": v(-17.58, 36.56) * mm, "end": v(-17.46, 36.52) * mm});
            skLineSegment(sketch, "E2636", {"start": v(-17.46, 36.52) * mm, "end": v(-17.32, 36.49) * mm});
            skLineSegment(sketch, "E2637", {"start": v(-17.32, 36.49) * mm, "end": v(-17.16, 36.47) * mm});
            skLineSegment(sketch, "E2638", {"start": v(-17.16, 36.47) * mm, "end": v(-17, 36.46) * mm});
            skLineSegment(sketch, "E2639", {"start": v(-17, 36.46) * mm, "end": v(-16.83, 36.47) * mm});
            skLineSegment(sketch, "E2640", {"start": v(-16.83, 36.47) * mm, "end": v(-16.67, 36.48) * mm});
            skLineSegment(sketch, "E2641", {"start": v(-16.67, 36.48) * mm, "end": v(-16.52, 36.51) * mm});
            skLineSegment(sketch, "E2642", {"start": v(-16.52, 36.51) * mm, "end": v(-16.4, 36.56) * mm});
            skLineSegment(sketch, "E2643", {"start": v(-16.4, 36.56) * mm, "end": v(-16.1, 36.68) * mm});
            skLineSegment(sketch, "E2644", {"start": v(-16.1, 36.68) * mm, "end": v(-16.04, 36.72) * mm});
            skLineSegment(sketch, "E2645", {"start": v(-16.04, 36.72) * mm, "end": v(-16.02, 36.74) * mm});
            skLineSegment(sketch, "E2646", {"start": v(-16.02, 36.74) * mm, "end": v(-16.01, 36.76) * mm});
            skLineSegment(sketch, "E2647", {"start": v(-16.01, 36.76) * mm, "end": v(-16, 36.77) * mm});
            skLineSegment(sketch, "E2648", {"start": v(-16, 36.77) * mm, "end": v(-15.96, 36.78) * mm});
            skLineSegment(sketch, "E2649", {"start": v(-15.96, 36.78) * mm, "end": v(-15.9, 36.82) * mm});
            skLineSegment(sketch, "E2650", {"start": v(-15.9, 36.82) * mm, "end": v(-15.76, 36.94) * mm});
            skLineSegment(sketch, "E2651", {"start": v(-15.76, 36.94) * mm, "end": v(-15.63, 37.08) * mm});
            skLineSegment(sketch, "E2652", {"start": v(-15.63, 37.08) * mm, "end": v(-15.6, 37.13) * mm});
            skLineSegment(sketch, "E2653", {"start": v(-15.6, 37.13) * mm, "end": v(-15.57, 37.16) * mm});
            skLineSegment(sketch, "E2654", {"start": v(-15.57, 37.16) * mm, "end": v(-15.56, 37.19) * mm});
            skLineSegment(sketch, "E2655", {"start": v(-15.56, 37.19) * mm, "end": v(-15.54, 37.23) * mm});
            skLineSegment(sketch, "E2656", {"start": v(-15.54, 37.23) * mm, "end": v(-15.47, 37.3) * mm});
            skLineSegment(sketch, "E2657", {"start": v(-15.47, 37.3) * mm, "end": v(-15.43, 37.37) * mm});
            skLineSegment(sketch, "E2658", {"start": v(-15.43, 37.37) * mm, "end": v(-15.39, 37.47) * mm});
            skLineSegment(sketch, "E2659", {"start": v(-15.39, 37.47) * mm, "end": v(-15.25, 37.87) * mm});
            skLineSegment(sketch, "E2660", {"start": v(-15.25, 37.87) * mm, "end": v(-15.22, 37.97) * mm});
            skLineSegment(sketch, "E2661", {"start": v(-15.22, 37.97) * mm, "end": v(-15.22, 44.96) * mm});
            skLineSegment(sketch, "E2662", {"start": v(-15.22, 44.96) * mm, "end": v(-15.24, 45.03) * mm});
            skLineSegment(sketch, "E2663", {"start": v(-15.24, 45.03) * mm, "end": v(-15.33, 45.28) * mm});
            skLineSegment(sketch, "E2664", {"start": v(-15.33, 45.28) * mm, "end": v(-15.4, 45.44) * mm});
            skLineSegment(sketch, "E2665", {"start": v(-15.4, 45.44) * mm, "end": v(-15.48, 45.6) * mm});
            skLineSegment(sketch, "E2666", {"start": v(-15.48, 45.6) * mm, "end": v(-15.55, 45.7) * mm});
            skLineSegment(sketch, "E2667", {"start": v(-15.55, 45.7) * mm, "end": v(-15.57, 45.75) * mm});
            skLineSegment(sketch, "E2668", {"start": v(-15.57, 45.75) * mm, "end": v(-15.6, 45.8) * mm});
            skLineSegment(sketch, "E2669", {"start": v(-15.6, 45.8) * mm, "end": v(-15.68, 45.87) * mm});
            skLineSegment(sketch, "E2670", {"start": v(-15.68, 45.87) * mm, "end": v(-15.93, 46.1) * mm});
            skLineSegment(sketch, "E2671", {"start": v(-15.93, 46.1) * mm, "end": v(-16.05, 46.18) * mm});
            skLineSegment(sketch, "E2672", {"start": v(-16.05, 46.18) * mm, "end": v(-16.2, 46.26) * mm});
            skLineSegment(sketch, "E2673", {"start": v(-16.2, 46.26) * mm, "end": v(-16.37, 46.34) * mm});
            skLineSegment(sketch, "E2674", {"start": v(-16.37, 46.34) * mm, "end": v(-16.53, 46.4) * mm});
            skLineSegment(sketch, "E2675", {"start": v(-16.53, 46.4) * mm, "end": v(-16.6, 46.4) * mm});
            skLineSegment(sketch, "E2676", {"start": v(-16.6, 46.4) * mm, "end": v(-16.72, 46.42) * mm});
            skLineSegment(sketch, "E2677", {"start": v(-16.72, 46.42) * mm, "end": v(-16.99, 46.43) * mm});
            skLineSegment(sketch, "E2678", {"start": v(-16.99, 46.43) * mm, "end": v(-17.25, 46.42) * mm});
            skLineSegment(sketch, "E2679", {"start": v(-17.25, 46.42) * mm, "end": v(-17.36, 46.4) * mm});
            skLineSegment(sketch, "E2680", {"start": v(-17.36, 46.4) * mm, "end": v(-17.45, 46.4) * mm});
            skLineSegment(sketch, "E2681", {"start": v(-17.45, 46.4) * mm, "end": v(-17.64, 46.32) * mm});
            skLineSegment(sketch, "E2682", {"start": v(-17.64, 46.32) * mm, "end": v(-17.84, 46.22) * mm});
            skLineSegment(sketch, "E2683", {"start": v(-17.84, 46.22) * mm, "end": v(-18.03, 46.1) * mm});
            skLineSegment(sketch, "E2684", {"start": v(-18.03, 46.1) * mm, "end": v(-18.2, 45.97) * mm});
            skLineSegment(sketch, "E2685", {"start": v(-18.2, 45.97) * mm, "end": v(-18.4, 45.78) * mm});
            skLineSegment(sketch, "E2686", {"start": v(-18.4, 45.78) * mm, "end": v(-18.4, 45.75) * mm});
            skLineSegment(sketch, "E2687", {"start": v(-18.4, 45.75) * mm, "end": v(-18.43, 45.7) * mm});
            skLineSegment(sketch, "E2688", {"start": v(-18.43, 45.7) * mm, "end": v(-18.5, 45.6) * mm});
            skLineSegment(sketch, "E2689", {"start": v(-18.5, 45.6) * mm, "end": v(-18.58, 45.44) * mm});
            skLineSegment(sketch, "E2690", {"start": v(-18.58, 45.44) * mm, "end": v(-18.65, 45.28) * mm});
            skLineSegment(sketch, "E2691", {"start": v(-18.65, 45.28) * mm, "end": v(-18.73, 45.03) * mm});
            skLineSegment(sketch, "E2692", {"start": v(-18.73, 45.03) * mm, "end": v(-18.75, 44.96) * mm});
            skLineSegment(sketch, "E2693", {"start": v(-18.75, 44.96) * mm, "end": v(-18.75, 37.94) * mm});
            skLineSegment(sketch, "E2694", {"start": v(-41.5, 61.97) * mm, "end": v(-41.5, 32.48) * mm});
            skLineSegment(sketch, "E2695", {"start": v(-41.5, 32.48) * mm, "end": v(-26.5, 32.48) * mm});
            skLineSegment(sketch, "E2696", {"start": v(-26.5, 32.48) * mm, "end": v(-26.5, 61.97) * mm});
            skLineSegment(sketch, "E2697", {"start": v(-26.5, 61.97) * mm, "end": v(-41.5, 61.97) * mm});
            skArc(sketch, "E2698", {"start": v(-29.49, 56.95) * mm, "mid": v(-29.85, 57.83) * mm, "end": v(-30.74, 58.2) * mm});
            skArc(sketch, "E2699", {"start": v(-30.74, 58.2) * mm, "mid": v(-31.62, 57.83) * mm, "end": v(-31.99, 56.95) * mm});
            skArc(sketch, "E2700", {"start": v(-31.99, 56.95) * mm, "mid": v(-31.62, 56.07) * mm, "end": v(-30.74, 55.7) * mm});
            skArc(sketch, "E2701", {"start": v(-30.74, 55.7) * mm, "mid": v(-29.85, 56.07) * mm, "end": v(-29.49, 56.95) * mm});
            skArc(sketch, "E2702", {"start": v(-35.99, 56.95) * mm, "mid": v(-36.35, 57.83) * mm, "end": v(-37.24, 58.2) * mm});
            skArc(sketch, "E2703", {"start": v(-37.24, 58.2) * mm, "mid": v(-38.12, 57.83) * mm, "end": v(-38.49, 56.95) * mm});
            skArc(sketch, "E2704", {"start": v(-38.49, 56.95) * mm, "mid": v(-38.12, 56.07) * mm, "end": v(-37.24, 55.7) * mm});
            skArc(sketch, "E2705", {"start": v(-37.24, 55.7) * mm, "mid": v(-36.35, 56.07) * mm, "end": v(-35.99, 56.95) * mm});
            skArc(sketch, "E2706", {"start": v(-28.24, 56.95) * mm, "mid": v(-28.97, 58.72) * mm, "end": v(-30.74, 59.45) * mm});
            skArc(sketch, "E2707", {"start": v(-30.74, 59.45) * mm, "mid": v(-32.5, 58.72) * mm, "end": v(-33.24, 56.95) * mm});
            skArc(sketch, "E2708", {"start": v(-33.24, 56.95) * mm, "mid": v(-32.5, 55.18) * mm, "end": v(-30.74, 54.45) * mm});
            skArc(sketch, "E2709", {"start": v(-30.74, 54.45) * mm, "mid": v(-28.97, 55.18) * mm, "end": v(-28.24, 56.95) * mm});
            skArc(sketch, "E2710", {"start": v(-34.74, 56.95) * mm, "mid": v(-35.47, 58.72) * mm, "end": v(-37.24, 59.45) * mm});
            skArc(sketch, "E2711", {"start": v(-37.24, 59.45) * mm, "mid": v(-39, 58.72) * mm, "end": v(-39.74, 56.95) * mm});
            skArc(sketch, "E2712", {"start": v(-39.74, 56.95) * mm, "mid": v(-39, 55.18) * mm, "end": v(-37.24, 54.45) * mm});
            skArc(sketch, "E2713", {"start": v(-37.24, 54.45) * mm, "mid": v(-35.47, 55.18) * mm, "end": v(-34.74, 56.95) * mm});
            skLineSegment(sketch, "E2714", {"start": v(-43.5, 48.73) * mm, "end": v(-43.5, 45.73) * mm});
            skLineSegment(sketch, "E2715", {"start": v(-43.5, 45.73) * mm, "end": v(-41.5, 45.73) * mm});
            skLineSegment(sketch, "E2716", {"start": v(-41.5, 45.73) * mm, "end": v(-41.5, 48.73) * mm});
            skLineSegment(sketch, "E2717", {"start": v(-41.5, 48.73) * mm, "end": v(-43.5, 48.73) * mm});
            skLineSegment(sketch, "E2718", {"start": v(-35.75, 37.94) * mm, "end": v(-35.73, 37.88) * mm});
            skLineSegment(sketch, "E2719", {"start": v(-35.73, 37.88) * mm, "end": v(-35.65, 37.64) * mm});
            skLineSegment(sketch, "E2720", {"start": v(-35.65, 37.64) * mm, "end": v(-35.6, 37.5) * mm});
            skLineSegment(sketch, "E2721", {"start": v(-35.6, 37.5) * mm, "end": v(-35.56, 37.4) * mm});
            skLineSegment(sketch, "E2722", {"start": v(-35.56, 37.4) * mm, "end": v(-35.5, 37.32) * mm});
            skLineSegment(sketch, "E2723", {"start": v(-35.5, 37.32) * mm, "end": v(-35.43, 37.23) * mm});
            skLineSegment(sketch, "E2724", {"start": v(-35.43, 37.23) * mm, "end": v(-35.4, 37.19) * mm});
            skLineSegment(sketch, "E2725", {"start": v(-35.4, 37.19) * mm, "end": v(-35.4, 37.16) * mm});
            skLineSegment(sketch, "E2726", {"start": v(-35.4, 37.16) * mm, "end": v(-35.36, 37.1) * mm});
            skLineSegment(sketch, "E2727", {"start": v(-35.36, 37.1) * mm, "end": v(-35.27, 37.02) * mm});
            skLineSegment(sketch, "E2728", {"start": v(-35.27, 37.02) * mm, "end": v(-35.08, 36.83) * mm});
            skLineSegment(sketch, "E2729", {"start": v(-35.08, 36.83) * mm, "end": v(-35.03, 36.79) * mm});
            skLineSegment(sketch, "E2730", {"start": v(-35.03, 36.79) * mm, "end": v(-34.98, 36.77) * mm});
            skLineSegment(sketch, "E2731", {"start": v(-34.98, 36.77) * mm, "end": v(-34.96, 36.76) * mm});
            skLineSegment(sketch, "E2732", {"start": v(-34.96, 36.76) * mm, "end": v(-34.95, 36.74) * mm});
            skLineSegment(sketch, "E2733", {"start": v(-34.95, 36.74) * mm, "end": v(-34.92, 36.72) * mm});
            skLineSegment(sketch, "E2734", {"start": v(-34.92, 36.72) * mm, "end": v(-34.86, 36.69) * mm});
            skLineSegment(sketch, "E2735", {"start": v(-34.86, 36.69) * mm, "end": v(-34.58, 36.56) * mm});
            skLineSegment(sketch, "E2736", {"start": v(-34.58, 36.56) * mm, "end": v(-34.46, 36.52) * mm});
            skLineSegment(sketch, "E2737", {"start": v(-34.46, 36.52) * mm, "end": v(-34.32, 36.49) * mm});
            skLineSegment(sketch, "E2738", {"start": v(-34.32, 36.49) * mm, "end": v(-34.16, 36.47) * mm});
            skLineSegment(sketch, "E2739", {"start": v(-34.16, 36.47) * mm, "end": v(-34, 36.46) * mm});
            skLineSegment(sketch, "E2740", {"start": v(-34, 36.46) * mm, "end": v(-33.83, 36.47) * mm});
            skLineSegment(sketch, "E2741", {"start": v(-33.83, 36.47) * mm, "end": v(-33.67, 36.48) * mm});
            skLineSegment(sketch, "E2742", {"start": v(-33.67, 36.48) * mm, "end": v(-33.52, 36.51) * mm});
            skLineSegment(sketch, "E2743", {"start": v(-33.52, 36.51) * mm, "end": v(-33.4, 36.56) * mm});
            skLineSegment(sketch, "E2744", {"start": v(-33.4, 36.56) * mm, "end": v(-33.1, 36.68) * mm});
            skLineSegment(sketch, "E2745", {"start": v(-33.1, 36.68) * mm, "end": v(-33.04, 36.72) * mm});
            skLineSegment(sketch, "E2746", {"start": v(-33.04, 36.72) * mm, "end": v(-33.02, 36.74) * mm});
            skLineSegment(sketch, "E2747", {"start": v(-33.02, 36.74) * mm, "end": v(-33.01, 36.76) * mm});
            skLineSegment(sketch, "E2748", {"start": v(-33.01, 36.76) * mm, "end": v(-33, 36.77) * mm});
            skLineSegment(sketch, "E2749", {"start": v(-33, 36.77) * mm, "end": v(-32.96, 36.78) * mm});
            skLineSegment(sketch, "E2750", {"start": v(-32.96, 36.78) * mm, "end": v(-32.9, 36.82) * mm});
            skLineSegment(sketch, "E2751", {"start": v(-32.9, 36.82) * mm, "end": v(-32.76, 36.94) * mm});
            skLineSegment(sketch, "E2752", {"start": v(-32.76, 36.94) * mm, "end": v(-32.63, 37.08) * mm});
            skLineSegment(sketch, "E2753", {"start": v(-32.63, 37.08) * mm, "end": v(-32.6, 37.13) * mm});
            skLineSegment(sketch, "E2754", {"start": v(-32.6, 37.13) * mm, "end": v(-32.57, 37.16) * mm});
            skLineSegment(sketch, "E2755", {"start": v(-32.57, 37.16) * mm, "end": v(-32.56, 37.19) * mm});
            skLineSegment(sketch, "E2756", {"start": v(-32.56, 37.19) * mm, "end": v(-32.54, 37.23) * mm});
            skLineSegment(sketch, "E2757", {"start": v(-32.54, 37.23) * mm, "end": v(-32.47, 37.3) * mm});
            skLineSegment(sketch, "E2758", {"start": v(-32.47, 37.3) * mm, "end": v(-32.43, 37.37) * mm});
            skLineSegment(sketch, "E2759", {"start": v(-32.43, 37.37) * mm, "end": v(-32.39, 37.47) * mm});
            skLineSegment(sketch, "E2760", {"start": v(-32.39, 37.47) * mm, "end": v(-32.25, 37.87) * mm});
            skLineSegment(sketch, "E2761", {"start": v(-32.25, 37.87) * mm, "end": v(-32.22, 37.97) * mm});
            skLineSegment(sketch, "E2762", {"start": v(-32.22, 37.97) * mm, "end": v(-32.22, 44.96) * mm});
            skLineSegment(sketch, "E2763", {"start": v(-32.22, 44.96) * mm, "end": v(-32.24, 45.03) * mm});
            skLineSegment(sketch, "E2764", {"start": v(-32.24, 45.03) * mm, "end": v(-32.33, 45.28) * mm});
            skLineSegment(sketch, "E2765", {"start": v(-32.33, 45.28) * mm, "end": v(-32.4, 45.44) * mm});
            skLineSegment(sketch, "E2766", {"start": v(-32.4, 45.44) * mm, "end": v(-32.48, 45.6) * mm});
            skLineSegment(sketch, "E2767", {"start": v(-32.48, 45.6) * mm, "end": v(-32.55, 45.7) * mm});
            skLineSegment(sketch, "E2768", {"start": v(-32.55, 45.7) * mm, "end": v(-32.57, 45.75) * mm});
            skLineSegment(sketch, "E2769", {"start": v(-32.57, 45.75) * mm, "end": v(-32.6, 45.8) * mm});
            skLineSegment(sketch, "E2770", {"start": v(-32.6, 45.8) * mm, "end": v(-32.68, 45.87) * mm});
            skLineSegment(sketch, "E2771", {"start": v(-32.68, 45.87) * mm, "end": v(-32.93, 46.1) * mm});
            skLineSegment(sketch, "E2772", {"start": v(-32.93, 46.1) * mm, "end": v(-33.05, 46.18) * mm});
            skLineSegment(sketch, "E2773", {"start": v(-33.05, 46.18) * mm, "end": v(-33.2, 46.26) * mm});
            skLineSegment(sketch, "E2774", {"start": v(-33.2, 46.26) * mm, "end": v(-33.37, 46.34) * mm});
            skLineSegment(sketch, "E2775", {"start": v(-33.37, 46.34) * mm, "end": v(-33.53, 46.4) * mm});
            skLineSegment(sketch, "E2776", {"start": v(-33.53, 46.4) * mm, "end": v(-33.6, 46.4) * mm});
            skLineSegment(sketch, "E2777", {"start": v(-33.6, 46.4) * mm, "end": v(-33.72, 46.42) * mm});
            skLineSegment(sketch, "E2778", {"start": v(-33.72, 46.42) * mm, "end": v(-33.99, 46.43) * mm});
            skLineSegment(sketch, "E2779", {"start": v(-33.99, 46.43) * mm, "end": v(-34.25, 46.42) * mm});
            skLineSegment(sketch, "E2780", {"start": v(-34.25, 46.42) * mm, "end": v(-34.36, 46.4) * mm});
            skLineSegment(sketch, "E2781", {"start": v(-34.36, 46.4) * mm, "end": v(-34.45, 46.4) * mm});
            skLineSegment(sketch, "E2782", {"start": v(-34.45, 46.4) * mm, "end": v(-34.64, 46.32) * mm});
            skLineSegment(sketch, "E2783", {"start": v(-34.64, 46.32) * mm, "end": v(-34.84, 46.22) * mm});
            skLineSegment(sketch, "E2784", {"start": v(-34.84, 46.22) * mm, "end": v(-35.03, 46.1) * mm});
            skLineSegment(sketch, "E2785", {"start": v(-35.03, 46.1) * mm, "end": v(-35.2, 45.97) * mm});
            skLineSegment(sketch, "E2786", {"start": v(-35.2, 45.97) * mm, "end": v(-35.4, 45.78) * mm});
            skLineSegment(sketch, "E2787", {"start": v(-35.4, 45.78) * mm, "end": v(-35.4, 45.75) * mm});
            skLineSegment(sketch, "E2788", {"start": v(-35.4, 45.75) * mm, "end": v(-35.43, 45.7) * mm});
            skLineSegment(sketch, "E2789", {"start": v(-35.43, 45.7) * mm, "end": v(-35.5, 45.6) * mm});
            skLineSegment(sketch, "E2790", {"start": v(-35.5, 45.6) * mm, "end": v(-35.58, 45.44) * mm});
            skLineSegment(sketch, "E2791", {"start": v(-35.58, 45.44) * mm, "end": v(-35.65, 45.28) * mm});
            skLineSegment(sketch, "E2792", {"start": v(-35.65, 45.28) * mm, "end": v(-35.73, 45.03) * mm});
            skLineSegment(sketch, "E2793", {"start": v(-35.73, 45.03) * mm, "end": v(-35.75, 44.96) * mm});
            skLineSegment(sketch, "E2794", {"start": v(-35.75, 44.96) * mm, "end": v(-35.75, 37.94) * mm});
            skLineSegment(sketch, "E2795", {"start": v(-26.5, 48.73) * mm, "end": v(-26.5, 45.73) * mm});
            skLineSegment(sketch, "E2796", {"start": v(-26.5, 45.73) * mm, "end": v(-24.5, 45.73) * mm});
            skLineSegment(sketch, "E2797", {"start": v(-24.5, 45.73) * mm, "end": v(-24.5, 48.73) * mm});
            skLineSegment(sketch, "E2798", {"start": v(-24.5, 48.73) * mm, "end": v(-26.5, 48.73) * mm});
            skLineSegment(sketch, "E2799", {"start": v(-58.5, 61.97) * mm, "end": v(-58.5, 32.48) * mm});
            skLineSegment(sketch, "E2800", {"start": v(-58.5, 32.48) * mm, "end": v(-43.5, 32.48) * mm});
            skLineSegment(sketch, "E2801", {"start": v(-43.5, 32.48) * mm, "end": v(-43.5, 61.97) * mm});
            skLineSegment(sketch, "E2802", {"start": v(-43.5, 61.97) * mm, "end": v(-58.5, 61.97) * mm});
            skArc(sketch, "E2803", {"start": v(-46.49, 56.95) * mm, "mid": v(-46.85, 57.83) * mm, "end": v(-47.74, 58.2) * mm});
            skArc(sketch, "E2804", {"start": v(-47.74, 58.2) * mm, "mid": v(-48.62, 57.83) * mm, "end": v(-48.99, 56.95) * mm});
            skArc(sketch, "E2805", {"start": v(-48.99, 56.95) * mm, "mid": v(-48.62, 56.07) * mm, "end": v(-47.74, 55.7) * mm});
            skArc(sketch, "E2806", {"start": v(-47.74, 55.7) * mm, "mid": v(-46.85, 56.07) * mm, "end": v(-46.49, 56.95) * mm});
            skArc(sketch, "E2807", {"start": v(-52.99, 56.95) * mm, "mid": v(-53.35, 57.83) * mm, "end": v(-54.24, 58.2) * mm});
            skArc(sketch, "E2808", {"start": v(-54.24, 58.2) * mm, "mid": v(-55.12, 57.83) * mm, "end": v(-55.49, 56.95) * mm});
            skArc(sketch, "E2809", {"start": v(-55.49, 56.95) * mm, "mid": v(-55.12, 56.07) * mm, "end": v(-54.24, 55.7) * mm});
            skArc(sketch, "E2810", {"start": v(-54.24, 55.7) * mm, "mid": v(-53.35, 56.07) * mm, "end": v(-52.99, 56.95) * mm});
            skArc(sketch, "E2811", {"start": v(-45.24, 56.95) * mm, "mid": v(-45.97, 58.72) * mm, "end": v(-47.74, 59.45) * mm});
            skArc(sketch, "E2812", {"start": v(-47.74, 59.45) * mm, "mid": v(-49.5, 58.72) * mm, "end": v(-50.24, 56.95) * mm});
            skArc(sketch, "E2813", {"start": v(-50.24, 56.95) * mm, "mid": v(-49.5, 55.18) * mm, "end": v(-47.74, 54.45) * mm});
            skArc(sketch, "E2814", {"start": v(-47.74, 54.45) * mm, "mid": v(-45.97, 55.18) * mm, "end": v(-45.24, 56.95) * mm});
            skArc(sketch, "E2815", {"start": v(-51.74, 56.95) * mm, "mid": v(-52.47, 58.72) * mm, "end": v(-54.24, 59.45) * mm});
            skArc(sketch, "E2816", {"start": v(-54.24, 59.45) * mm, "mid": v(-56, 58.72) * mm, "end": v(-56.74, 56.95) * mm});
            skArc(sketch, "E2817", {"start": v(-56.74, 56.95) * mm, "mid": v(-56, 55.18) * mm, "end": v(-54.24, 54.45) * mm});
            skArc(sketch, "E2818", {"start": v(-54.24, 54.45) * mm, "mid": v(-52.47, 55.18) * mm, "end": v(-51.74, 56.95) * mm});
            skLineSegment(sketch, "E2819", {"start": v(-52.75, 37.94) * mm, "end": v(-52.73, 37.88) * mm});
            skLineSegment(sketch, "E2820", {"start": v(-52.73, 37.88) * mm, "end": v(-52.65, 37.64) * mm});
            skLineSegment(sketch, "E2821", {"start": v(-52.65, 37.64) * mm, "end": v(-52.6, 37.5) * mm});
            skLineSegment(sketch, "E2822", {"start": v(-52.6, 37.5) * mm, "end": v(-52.56, 37.4) * mm});
            skLineSegment(sketch, "E2823", {"start": v(-52.56, 37.4) * mm, "end": v(-52.5, 37.32) * mm});
            skLineSegment(sketch, "E2824", {"start": v(-52.5, 37.32) * mm, "end": v(-52.43, 37.23) * mm});
            skLineSegment(sketch, "E2825", {"start": v(-52.43, 37.23) * mm, "end": v(-52.4, 37.19) * mm});
            skLineSegment(sketch, "E2826", {"start": v(-52.4, 37.19) * mm, "end": v(-52.4, 37.16) * mm});
            skLineSegment(sketch, "E2827", {"start": v(-52.4, 37.16) * mm, "end": v(-52.36, 37.1) * mm});
            skLineSegment(sketch, "E2828", {"start": v(-52.36, 37.1) * mm, "end": v(-52.27, 37.02) * mm});
            skLineSegment(sketch, "E2829", {"start": v(-52.27, 37.02) * mm, "end": v(-52.08, 36.83) * mm});
            skLineSegment(sketch, "E2830", {"start": v(-52.08, 36.83) * mm, "end": v(-52.03, 36.79) * mm});
            skLineSegment(sketch, "E2831", {"start": v(-52.03, 36.79) * mm, "end": v(-51.98, 36.77) * mm});
            skLineSegment(sketch, "E2832", {"start": v(-51.98, 36.77) * mm, "end": v(-51.96, 36.76) * mm});
            skLineSegment(sketch, "E2833", {"start": v(-51.96, 36.76) * mm, "end": v(-51.95, 36.74) * mm});
            skLineSegment(sketch, "E2834", {"start": v(-51.95, 36.74) * mm, "end": v(-51.92, 36.72) * mm});
            skLineSegment(sketch, "E2835", {"start": v(-51.92, 36.72) * mm, "end": v(-51.86, 36.69) * mm});
            skLineSegment(sketch, "E2836", {"start": v(-51.86, 36.69) * mm, "end": v(-51.58, 36.56) * mm});
            skLineSegment(sketch, "E2837", {"start": v(-51.58, 36.56) * mm, "end": v(-51.46, 36.52) * mm});
            skLineSegment(sketch, "E2838", {"start": v(-51.46, 36.52) * mm, "end": v(-51.32, 36.49) * mm});
            skLineSegment(sketch, "E2839", {"start": v(-51.32, 36.49) * mm, "end": v(-51.16, 36.47) * mm});
            skLineSegment(sketch, "E2840", {"start": v(-51.16, 36.47) * mm, "end": v(-51, 36.46) * mm});
            skLineSegment(sketch, "E2841", {"start": v(-51, 36.46) * mm, "end": v(-50.83, 36.47) * mm});
            skLineSegment(sketch, "E2842", {"start": v(-50.83, 36.47) * mm, "end": v(-50.67, 36.48) * mm});
            skLineSegment(sketch, "E2843", {"start": v(-50.67, 36.48) * mm, "end": v(-50.52, 36.51) * mm});
            skLineSegment(sketch, "E2844", {"start": v(-50.52, 36.51) * mm, "end": v(-50.4, 36.56) * mm});
            skLineSegment(sketch, "E2845", {"start": v(-50.4, 36.56) * mm, "end": v(-50.1, 36.68) * mm});
            skLineSegment(sketch, "E2846", {"start": v(-50.1, 36.68) * mm, "end": v(-50.04, 36.72) * mm});
            skLineSegment(sketch, "E2847", {"start": v(-50.04, 36.72) * mm, "end": v(-50.02, 36.74) * mm});
            skLineSegment(sketch, "E2848", {"start": v(-50.02, 36.74) * mm, "end": v(-50.01, 36.76) * mm});
            skLineSegment(sketch, "E2849", {"start": v(-50.01, 36.76) * mm, "end": v(-50, 36.77) * mm});
            skLineSegment(sketch, "E2850", {"start": v(-50, 36.77) * mm, "end": v(-49.96, 36.78) * mm});
            skLineSegment(sketch, "E2851", {"start": v(-49.96, 36.78) * mm, "end": v(-49.9, 36.82) * mm});
            skLineSegment(sketch, "E2852", {"start": v(-49.9, 36.82) * mm, "end": v(-49.76, 36.94) * mm});
            skLineSegment(sketch, "E2853", {"start": v(-49.76, 36.94) * mm, "end": v(-49.63, 37.08) * mm});
            skLineSegment(sketch, "E2854", {"start": v(-49.63, 37.08) * mm, "end": v(-49.6, 37.13) * mm});
            skLineSegment(sketch, "E2855", {"start": v(-49.6, 37.13) * mm, "end": v(-49.57, 37.16) * mm});
            skLineSegment(sketch, "E2856", {"start": v(-49.57, 37.16) * mm, "end": v(-49.56, 37.19) * mm});
            skLineSegment(sketch, "E2857", {"start": v(-49.56, 37.19) * mm, "end": v(-49.54, 37.23) * mm});
            skLineSegment(sketch, "E2858", {"start": v(-49.54, 37.23) * mm, "end": v(-49.47, 37.3) * mm});
            skLineSegment(sketch, "E2859", {"start": v(-49.47, 37.3) * mm, "end": v(-49.43, 37.37) * mm});
            skLineSegment(sketch, "E2860", {"start": v(-49.43, 37.37) * mm, "end": v(-49.39, 37.47) * mm});
            skLineSegment(sketch, "E2861", {"start": v(-49.39, 37.47) * mm, "end": v(-49.25, 37.87) * mm});
            skLineSegment(sketch, "E2862", {"start": v(-49.25, 37.87) * mm, "end": v(-49.22, 37.97) * mm});
            skLineSegment(sketch, "E2863", {"start": v(-49.22, 37.97) * mm, "end": v(-49.22, 44.96) * mm});
            skLineSegment(sketch, "E2864", {"start": v(-49.22, 44.96) * mm, "end": v(-49.24, 45.03) * mm});
            skLineSegment(sketch, "E2865", {"start": v(-49.24, 45.03) * mm, "end": v(-49.33, 45.28) * mm});
            skLineSegment(sketch, "E2866", {"start": v(-49.33, 45.28) * mm, "end": v(-49.4, 45.44) * mm});
            skLineSegment(sketch, "E2867", {"start": v(-49.4, 45.44) * mm, "end": v(-49.48, 45.6) * mm});
            skLineSegment(sketch, "E2868", {"start": v(-49.48, 45.6) * mm, "end": v(-49.55, 45.7) * mm});
            skLineSegment(sketch, "E2869", {"start": v(-49.55, 45.7) * mm, "end": v(-49.57, 45.75) * mm});
            skLineSegment(sketch, "E2870", {"start": v(-49.57, 45.75) * mm, "end": v(-49.6, 45.8) * mm});
            skLineSegment(sketch, "E2871", {"start": v(-49.6, 45.8) * mm, "end": v(-49.68, 45.87) * mm});
            skLineSegment(sketch, "E2872", {"start": v(-49.68, 45.87) * mm, "end": v(-49.93, 46.1) * mm});
            skLineSegment(sketch, "E2873", {"start": v(-49.93, 46.1) * mm, "end": v(-50.05, 46.18) * mm});
            skLineSegment(sketch, "E2874", {"start": v(-50.05, 46.18) * mm, "end": v(-50.2, 46.26) * mm});
            skLineSegment(sketch, "E2875", {"start": v(-50.2, 46.26) * mm, "end": v(-50.37, 46.34) * mm});
            skLineSegment(sketch, "E2876", {"start": v(-50.37, 46.34) * mm, "end": v(-50.53, 46.4) * mm});
            skLineSegment(sketch, "E2877", {"start": v(-50.53, 46.4) * mm, "end": v(-50.6, 46.4) * mm});
            skLineSegment(sketch, "E2878", {"start": v(-50.6, 46.4) * mm, "end": v(-50.72, 46.42) * mm});
            skLineSegment(sketch, "E2879", {"start": v(-50.72, 46.42) * mm, "end": v(-50.99, 46.43) * mm});
            skLineSegment(sketch, "E2880", {"start": v(-50.99, 46.43) * mm, "end": v(-51.25, 46.42) * mm});
            skLineSegment(sketch, "E2881", {"start": v(-51.25, 46.42) * mm, "end": v(-51.36, 46.4) * mm});
            skLineSegment(sketch, "E2882", {"start": v(-51.36, 46.4) * mm, "end": v(-51.45, 46.4) * mm});
            skLineSegment(sketch, "E2883", {"start": v(-51.45, 46.4) * mm, "end": v(-51.64, 46.32) * mm});
            skLineSegment(sketch, "E2884", {"start": v(-51.64, 46.32) * mm, "end": v(-51.84, 46.22) * mm});
            skLineSegment(sketch, "E2885", {"start": v(-51.84, 46.22) * mm, "end": v(-52.03, 46.1) * mm});
            skLineSegment(sketch, "E2886", {"start": v(-52.03, 46.1) * mm, "end": v(-52.2, 45.97) * mm});
            skLineSegment(sketch, "E2887", {"start": v(-52.2, 45.97) * mm, "end": v(-52.4, 45.78) * mm});
            skLineSegment(sketch, "E2888", {"start": v(-52.4, 45.78) * mm, "end": v(-52.4, 45.75) * mm});
            skLineSegment(sketch, "E2889", {"start": v(-52.4, 45.75) * mm, "end": v(-52.43, 45.7) * mm});
            skLineSegment(sketch, "E2890", {"start": v(-52.43, 45.7) * mm, "end": v(-52.5, 45.6) * mm});
            skLineSegment(sketch, "E2891", {"start": v(-52.5, 45.6) * mm, "end": v(-52.58, 45.44) * mm});
            skLineSegment(sketch, "E2892", {"start": v(-52.58, 45.44) * mm, "end": v(-52.65, 45.28) * mm});
            skLineSegment(sketch, "E2893", {"start": v(-52.65, 45.28) * mm, "end": v(-52.73, 45.03) * mm});
            skLineSegment(sketch, "E2894", {"start": v(-52.73, 45.03) * mm, "end": v(-52.75, 44.96) * mm});
            skLineSegment(sketch, "E2895", {"start": v(-52.75, 44.96) * mm, "end": v(-52.75, 37.94) * mm});
            skSolve(sketch);
        }
        {
            var Q0;
            {var subQ6=sQuery(id+"F0.wireOp",EDGE,"E2799");Q0=makeQuery(id+"F0.imprint","IMPRINT",FACE,{"disambiguationData":[TD([[makeQuery(id+"F0.imprint","IMPRINT",EDGE,{"derivedFrom":subQ6}),1.0]])]});}
            var Q1;
            {var subQ0=sQuery(id+"F0.wireOp",EDGE,"E2697");Q1=makeQuery(id+"F0.imprint","IMPRINT",FACE,{"disambiguationData":[TD([[makeQuery(id+"F0.imprint","IMPRINT",EDGE,{"derivedFrom":subQ0}),1.0]])]});}
            var Q2;
            {var subQ0=sQuery(id+"F0.wireOp",EDGE,"E2600");Q2=makeQuery(id+"F0.imprint","IMPRINT",FACE,{"disambiguationData":[TD([[makeQuery(id+"F0.imprint","IMPRINT",EDGE,{"derivedFrom":subQ0}),1.0]])]});}
            var Q3;
            {var subQ0=sQuery(id+"F0.wireOp",EDGE,"E2495");Q3=makeQuery(id+"F0.imprint","IMPRINT",FACE,{"disambiguationData":[TD([[makeQuery(id+"F0.imprint","IMPRINT",EDGE,{"derivedFrom":subQ0}),1.0]])]});}
            var Q4;
            {var subQ0=sQuery(id+"F0.wireOp",EDGE,"E2390");Q4=makeQuery(id+"F0.imprint","IMPRINT",FACE,{"disambiguationData":[TD([[makeQuery(id+"F0.imprint","IMPRINT",EDGE,{"derivedFrom":subQ0}),1.0]])]});}
            var Q5;
            {var subQ0=sQuery(id+"F0.wireOp",EDGE,"E2289");Q5=makeQuery(id+"F0.imprint","IMPRINT",FACE,{"disambiguationData":[TD([[makeQuery(id+"F0.imprint","IMPRINT",EDGE,{"derivedFrom":subQ0}),1.0]])]});}
            var Q6;
            {var subQ1=sQuery(id+"F0.wireOp",EDGE,"E2187");Q6=makeQuery(id+"F0.imprint","IMPRINT",FACE,{"disambiguationData":[TD([[makeQuery(id+"F0.imprint","IMPRINT",EDGE,{"derivedFrom":subQ1}),1.0]])]});}
            var Q7;
            {var subQ4=sQuery(id+"F0.wireOp",EDGE,"E2086");Q7=makeQuery(id+"F0.imprint","IMPRINT",FACE,{"disambiguationData":[TD([[makeQuery(id+"F0.imprint","IMPRINT",EDGE,{"derivedFrom":subQ4}),1.0]])]});}
            var Q8;
            Q8=makeQuery(id+"F0.imprint","IMPRINT",FACE,{"disambiguationData":[TD([[makeQuery(id+"F0.imprint","IMPRINT",EDGE,{"derivedFrom":sQuery(id+"F0.wireOp",EDGE,"E1991")}),-1.0]])]});
            var Q9;
            Q9=makeQuery(id+"F0.imprint","IMPRINT",FACE,{"disambiguationData":[TD([[makeQuery(id+"F0.imprint","IMPRINT",EDGE,{"derivedFrom":sQuery(id+"F0.wireOp",EDGE,"E1886")}),-1.0]])]});
            var Q10;
            Q10=makeQuery(id+"F0.imprint","IMPRINT",FACE,{"disambiguationData":[TD([[makeQuery(id+"F0.imprint","IMPRINT",EDGE,{"derivedFrom":sQuery(id+"F0.wireOp",EDGE,"E1781")}),-1.0]])]});
            var Q11;
            Q11=makeQuery(id+"F0.imprint","IMPRINT",FACE,{"disambiguationData":[TD([[makeQuery(id+"F0.imprint","IMPRINT",EDGE,{"derivedFrom":sQuery(id+"F0.wireOp",EDGE,"E1676")}),-1.0]])]});
            var Q12;
            Q12=makeQuery(id+"F0.imprint","IMPRINT",FACE,{"disambiguationData":[TD([[makeQuery(id+"F0.imprint","IMPRINT",EDGE,{"derivedFrom":sQuery(id+"F0.wireOp",EDGE,"E1567")}),-1.0]])]});
            var Q13;
            {var subQ2=sQuery(id+"F0.wireOp",EDGE,"E1454");Q13=makeQuery(id+"F0.imprint","IMPRINT",FACE,{"disambiguationData":[TD([[makeQuery(id+"F0.imprint","IMPRINT",EDGE,{"derivedFrom":subQ2}),1.0]])]});}
            var Q14;
            {var subQ1=sQuery(id+"F0.wireOp",EDGE,"E1349");Q14=makeQuery(id+"F0.imprint","IMPRINT",FACE,{"disambiguationData":[TD([[makeQuery(id+"F0.imprint","IMPRINT",EDGE,{"derivedFrom":subQ1}),1.0]])]});}
            var Q15;
            Q15=makeQuery(id+"F0.imprint","IMPRINT",FACE,{"disambiguationData":[TD([[makeQuery(id+"F0.imprint","IMPRINT",EDGE,{"derivedFrom":sQuery(id+"F0.wireOp",EDGE,"E1256")}),-1.0]])]});
            var Q16;
            Q16=makeQuery(id+"F0.imprint","IMPRINT",FACE,{"disambiguationData":[TD([[makeQuery(id+"F0.imprint","IMPRINT",EDGE,{"derivedFrom":sQuery(id+"F0.wireOp",EDGE,"E1155")}),-1.0]])]});
            var Q17;
            Q17=makeQuery(id+"F0.imprint","IMPRINT",FACE,{"disambiguationData":[TD([[makeQuery(id+"F0.imprint","IMPRINT",EDGE,{"derivedFrom":sQuery(id+"F0.wireOp",EDGE,"E1042")}),-1.0]])]});
            var Q18;
            Q18=makeQuery(id+"F0.imprint","IMPRINT",FACE,{"disambiguationData":[TD([[makeQuery(id+"F0.imprint","IMPRINT",EDGE,{"derivedFrom":sQuery(id+"F0.wireOp",EDGE,"E937")}),-1.0]])]});
            var Q19;
            Q19=makeQuery(id+"F0.imprint","IMPRINT",FACE,{"disambiguationData":[TD([[makeQuery(id+"F0.imprint","IMPRINT",EDGE,{"derivedFrom":sQuery(id+"F0.wireOp",EDGE,"E832")}),-1.0]])]});
            var Q20;
            {var subQ4=sQuery(id+"F0.wireOp",EDGE,"E713");Q20=makeQuery(id+"F0.imprint","IMPRINT",FACE,{"disambiguationData":[TD([[makeQuery(id+"F0.imprint","IMPRINT",EDGE,{"derivedFrom":subQ4}),1.0]])]});}
            var Q21;
            {var subQ6=sQuery(id+"F0.wireOp",EDGE,"E611");Q21=makeQuery(id+"F0.imprint","IMPRINT",FACE,{"disambiguationData":[TD([[makeQuery(id+"F0.imprint","IMPRINT",EDGE,{"derivedFrom":subQ6}),1.0]])]});}
            var Q22;
            {var subQ7=sQuery(id+"F0.wireOp",EDGE,"E514");Q22=makeQuery(id+"F0.imprint","IMPRINT",FACE,{"disambiguationData":[TD([[makeQuery(id+"F0.imprint","IMPRINT",EDGE,{"derivedFrom":subQ7}),1.0]])]});}
            var Q23;
            {var subQ8=sQuery(id+"F0.wireOp",EDGE,"E409");Q23=makeQuery(id+"F0.imprint","IMPRINT",FACE,{"disambiguationData":[TD([[makeQuery(id+"F0.imprint","IMPRINT",EDGE,{"derivedFrom":subQ8}),1.0]])]});}
            var Q24;
            {var subQ8=sQuery(id+"F0.wireOp",EDGE,"E308");Q24=makeQuery(id+"F0.imprint","IMPRINT",FACE,{"disambiguationData":[TD([[makeQuery(id+"F0.imprint","IMPRINT",EDGE,{"derivedFrom":subQ8}),1.0]])]});}
            var Q25;
            {var subQ7=sQuery(id+"F0.wireOp",EDGE,"E207");Q25=makeQuery(id+"F0.imprint","IMPRINT",FACE,{"disambiguationData":[TD([[makeQuery(id+"F0.imprint","IMPRINT",EDGE,{"derivedFrom":subQ7}),1.0]])]});}
            var Q26;
            {var subQ7=sQuery(id+"F0.wireOp",EDGE,"E102");Q26=makeQuery(id+"F0.imprint","IMPRINT",FACE,{"disambiguationData":[TD([[makeQuery(id+"F0.imprint","IMPRINT",EDGE,{"derivedFrom":subQ7}),1.0]])]});}
            var Q27;
            {var subQ2=sQuery(id+"F0.wireOp",EDGE,"E0");Q27=makeQuery(id+"F0.imprint","IMPRINT",FACE,{"disambiguationData":[TD([[makeQuery(id+"F0.imprint","IMPRINT",EDGE,{"derivedFrom":subQ2}),1.0]])]});}
            extrude(context, id + "F1", {"entities" : qUnion([Q0, Q1, Q2, Q3, Q4, Q5, Q6, Q7, Q8, Q9, Q10, Q11, Q12, Q13, Q14, Q15, Q16, Q17, Q18, Q19, Q20, Q21, Q22, Q23, Q24, Q25, Q26, Q27]), "depth" : 4 * mm, "offsetDistance" : 25 * mm});
        }
        {
            var Q0;
            Q0=makeQuery(id+"F0.imprint","IMPRINT",FACE,{"disambiguationData":[TD([[makeQuery(id+"F0.imprint","IMPRINT",EDGE,{"derivedFrom":sQuery(id+"F0.wireOp",EDGE,"E2807")}),-1.0]])]});
            var Q1;
            Q1=makeQuery(id+"F0.imprint","IMPRINT",FACE,{"disambiguationData":[TD([[makeQuery(id+"F0.imprint","IMPRINT",EDGE,{"derivedFrom":sQuery(id+"F0.wireOp",EDGE,"E2803")}),-1.0]])]});
            var Q2;
            Q2=makeQuery(id+"F0.imprint","IMPRINT",FACE,{"disambiguationData":[TD([[makeQuery(id+"F0.imprint","IMPRINT",EDGE,{"derivedFrom":sQuery(id+"F0.wireOp",EDGE,"E2702")}),-1.0]])]});
            var Q3;
            Q3=makeQuery(id+"F0.imprint","IMPRINT",FACE,{"disambiguationData":[TD([[makeQuery(id+"F0.imprint","IMPRINT",EDGE,{"derivedFrom":sQuery(id+"F0.wireOp",EDGE,"E2698")}),-1.0]])]});
            var Q4;
            Q4=makeQuery(id+"F0.imprint","IMPRINT",FACE,{"disambiguationData":[TD([[makeQuery(id+"F0.imprint","IMPRINT",EDGE,{"derivedFrom":sQuery(id+"F0.wireOp",EDGE,"E2605")}),-1.0]])]});
            var Q5;
            Q5=makeQuery(id+"F0.imprint","IMPRINT",FACE,{"disambiguationData":[TD([[makeQuery(id+"F0.imprint","IMPRINT",EDGE,{"derivedFrom":sQuery(id+"F0.wireOp",EDGE,"E2601")}),-1.0]])]});
            var Q6;
            Q6=makeQuery(id+"F0.imprint","IMPRINT",FACE,{"disambiguationData":[TD([[makeQuery(id+"F0.imprint","IMPRINT",EDGE,{"derivedFrom":sQuery(id+"F0.wireOp",EDGE,"E2500")}),-1.0]])]});
            var Q7;
            Q7=makeQuery(id+"F0.imprint","IMPRINT",FACE,{"disambiguationData":[TD([[makeQuery(id+"F0.imprint","IMPRINT",EDGE,{"derivedFrom":sQuery(id+"F0.wireOp",EDGE,"E2496")}),-1.0]])]});
            var Q8;
            Q8=makeQuery(id+"F0.imprint","IMPRINT",FACE,{"disambiguationData":[TD([[makeQuery(id+"F0.imprint","IMPRINT",EDGE,{"derivedFrom":sQuery(id+"F0.wireOp",EDGE,"E2395")}),-1.0]])]});
            var Q9;
            Q9=makeQuery(id+"F0.imprint","IMPRINT",FACE,{"disambiguationData":[TD([[makeQuery(id+"F0.imprint","IMPRINT",EDGE,{"derivedFrom":sQuery(id+"F0.wireOp",EDGE,"E2391")}),-1.0]])]});
            var Q10;
            Q10=makeQuery(id+"F0.imprint","IMPRINT",FACE,{"disambiguationData":[TD([[makeQuery(id+"F0.imprint","IMPRINT",EDGE,{"derivedFrom":sQuery(id+"F0.wireOp",EDGE,"E2294")}),-1.0]])]});
            var Q11;
            Q11=makeQuery(id+"F0.imprint","IMPRINT",FACE,{"disambiguationData":[TD([[makeQuery(id+"F0.imprint","IMPRINT",EDGE,{"derivedFrom":sQuery(id+"F0.wireOp",EDGE,"E2290")}),-1.0]])]});
            var Q12;
            Q12=makeQuery(id+"F0.imprint","IMPRINT",FACE,{"disambiguationData":[TD([[makeQuery(id+"F0.imprint","IMPRINT",EDGE,{"derivedFrom":sQuery(id+"F0.wireOp",EDGE,"E2193")}),-1.0]])]});
            var Q13;
            Q13=makeQuery(id+"F0.imprint","IMPRINT",FACE,{"disambiguationData":[TD([[makeQuery(id+"F0.imprint","IMPRINT",EDGE,{"derivedFrom":sQuery(id+"F0.wireOp",EDGE,"E2189")}),-1.0]])]});
            extrude(context, id + "F2", {"entities" : qUnion([Q0, Q1, Q2, Q3, Q4, Q5, Q6, Q7, Q8, Q9, Q10, Q11, Q12, Q13]), "depth" : 2 * mm, "offsetDistance" : 25 * mm});
        }
        {
            var Q0;
            Q0=makeQuery(id+"F0.imprint","IMPRINT",FACE,{"disambiguationData":[TD([[makeQuery(id+"F0.imprint","IMPRINT",EDGE,{"derivedFrom":sQuery(id+"F0.wireOp",EDGE,"E1462")}),-1.0]])]});
            var Q1;
            Q1=makeQuery(id+"F0.imprint","IMPRINT",FACE,{"disambiguationData":[TD([[makeQuery(id+"F0.imprint","IMPRINT",EDGE,{"derivedFrom":sQuery(id+"F0.wireOp",EDGE,"E1458")}),-1.0]])]});
            var Q2;
            Q2=makeQuery(id+"F0.imprint","IMPRINT",FACE,{"disambiguationData":[TD([[makeQuery(id+"F0.imprint","IMPRINT",EDGE,{"derivedFrom":sQuery(id+"F0.wireOp",EDGE,"E1563")}),-1.0]])]});
            var Q3;
            Q3=makeQuery(id+"F0.imprint","IMPRINT",FACE,{"disambiguationData":[TD([[makeQuery(id+"F0.imprint","IMPRINT",EDGE,{"derivedFrom":sQuery(id+"F0.wireOp",EDGE,"E1559")}),-1.0]])]});
            var Q4;
            Q4=makeQuery(id+"F0.imprint","IMPRINT",FACE,{"disambiguationData":[TD([[makeQuery(id+"F0.imprint","IMPRINT",EDGE,{"derivedFrom":sQuery(id+"F0.wireOp",EDGE,"E1672")}),-1.0]])]});
            var Q5;
            Q5=makeQuery(id+"F0.imprint","IMPRINT",FACE,{"disambiguationData":[TD([[makeQuery(id+"F0.imprint","IMPRINT",EDGE,{"derivedFrom":sQuery(id+"F0.wireOp",EDGE,"E1668")}),-1.0]])]});
            var Q6;
            Q6=makeQuery(id+"F0.imprint","IMPRINT",FACE,{"disambiguationData":[TD([[makeQuery(id+"F0.imprint","IMPRINT",EDGE,{"derivedFrom":sQuery(id+"F0.wireOp",EDGE,"E1777")}),-1.0]])]});
            var Q7;
            Q7=makeQuery(id+"F0.imprint","IMPRINT",FACE,{"disambiguationData":[TD([[makeQuery(id+"F0.imprint","IMPRINT",EDGE,{"derivedFrom":sQuery(id+"F0.wireOp",EDGE,"E1773")}),-1.0]])]});
            var Q8;
            Q8=makeQuery(id+"F0.imprint","IMPRINT",FACE,{"disambiguationData":[TD([[makeQuery(id+"F0.imprint","IMPRINT",EDGE,{"derivedFrom":sQuery(id+"F0.wireOp",EDGE,"E1882")}),-1.0]])]});
            var Q9;
            Q9=makeQuery(id+"F0.imprint","IMPRINT",FACE,{"disambiguationData":[TD([[makeQuery(id+"F0.imprint","IMPRINT",EDGE,{"derivedFrom":sQuery(id+"F0.wireOp",EDGE,"E1878")}),-1.0]])]});
            var Q10;
            Q10=makeQuery(id+"F0.imprint","IMPRINT",FACE,{"disambiguationData":[TD([[makeQuery(id+"F0.imprint","IMPRINT",EDGE,{"derivedFrom":sQuery(id+"F0.wireOp",EDGE,"E1987")}),-1.0]])]});
            var Q11;
            Q11=makeQuery(id+"F0.imprint","IMPRINT",FACE,{"disambiguationData":[TD([[makeQuery(id+"F0.imprint","IMPRINT",EDGE,{"derivedFrom":sQuery(id+"F0.wireOp",EDGE,"E1983")}),-1.0]])]});
            var Q12;
            Q12=makeQuery(id+"F0.imprint","IMPRINT",FACE,{"disambiguationData":[TD([[makeQuery(id+"F0.imprint","IMPRINT",EDGE,{"derivedFrom":sQuery(id+"F0.wireOp",EDGE,"E2092")}),-1.0]])]});
            var Q13;
            Q13=makeQuery(id+"F0.imprint","IMPRINT",FACE,{"disambiguationData":[TD([[makeQuery(id+"F0.imprint","IMPRINT",EDGE,{"derivedFrom":sQuery(id+"F0.wireOp",EDGE,"E2088")}),-1.0]])]});
            var Q14;
            Q14=makeQuery(id+"F0.imprint","IMPRINT",FACE,{"disambiguationData":[TD([[makeQuery(id+"F0.imprint","IMPRINT",EDGE,{"derivedFrom":sQuery(id+"F0.wireOp",EDGE,"E1357")}),-1.0]])]});
            var Q15;
            Q15=makeQuery(id+"F0.imprint","IMPRINT",FACE,{"disambiguationData":[TD([[makeQuery(id+"F0.imprint","IMPRINT",EDGE,{"derivedFrom":sQuery(id+"F0.wireOp",EDGE,"E1353")}),-1.0]])]});
            var Q16;
            Q16=makeQuery(id+"F0.imprint","IMPRINT",FACE,{"disambiguationData":[TD([[makeQuery(id+"F0.imprint","IMPRINT",EDGE,{"derivedFrom":sQuery(id+"F0.wireOp",EDGE,"E1252")}),-1.0]])]});
            var Q17;
            Q17=makeQuery(id+"F0.imprint","IMPRINT",FACE,{"disambiguationData":[TD([[makeQuery(id+"F0.imprint","IMPRINT",EDGE,{"derivedFrom":sQuery(id+"F0.wireOp",EDGE,"E1248")}),-1.0]])]});
            var Q18;
            Q18=makeQuery(id+"F0.imprint","IMPRINT",FACE,{"disambiguationData":[TD([[makeQuery(id+"F0.imprint","IMPRINT",EDGE,{"derivedFrom":sQuery(id+"F0.wireOp",EDGE,"E1151")}),-1.0]])]});
            var Q19;
            Q19=makeQuery(id+"F0.imprint","IMPRINT",FACE,{"disambiguationData":[TD([[makeQuery(id+"F0.imprint","IMPRINT",EDGE,{"derivedFrom":sQuery(id+"F0.wireOp",EDGE,"E1147")}),-1.0]])]});
            var Q20;
            Q20=makeQuery(id+"F0.imprint","IMPRINT",FACE,{"disambiguationData":[TD([[makeQuery(id+"F0.imprint","IMPRINT",EDGE,{"derivedFrom":sQuery(id+"F0.wireOp",EDGE,"E1038")}),-1.0]])]});
            var Q21;
            Q21=makeQuery(id+"F0.imprint","IMPRINT",FACE,{"disambiguationData":[TD([[makeQuery(id+"F0.imprint","IMPRINT",EDGE,{"derivedFrom":sQuery(id+"F0.wireOp",EDGE,"E1034")}),-1.0]])]});
            var Q22;
            Q22=makeQuery(id+"F0.imprint","IMPRINT",FACE,{"disambiguationData":[TD([[makeQuery(id+"F0.imprint","IMPRINT",EDGE,{"derivedFrom":sQuery(id+"F0.wireOp",EDGE,"E933")}),-1.0]])]});
            var Q23;
            Q23=makeQuery(id+"F0.imprint","IMPRINT",FACE,{"disambiguationData":[TD([[makeQuery(id+"F0.imprint","IMPRINT",EDGE,{"derivedFrom":sQuery(id+"F0.wireOp",EDGE,"E929")}),-1.0]])]});
            var Q24;
            Q24=makeQuery(id+"F0.imprint","IMPRINT",FACE,{"disambiguationData":[TD([[makeQuery(id+"F0.imprint","IMPRINT",EDGE,{"derivedFrom":sQuery(id+"F0.wireOp",EDGE,"E828")}),-1.0]])]});
            var Q25;
            Q25=makeQuery(id+"F0.imprint","IMPRINT",FACE,{"disambiguationData":[TD([[makeQuery(id+"F0.imprint","IMPRINT",EDGE,{"derivedFrom":sQuery(id+"F0.wireOp",EDGE,"E824")}),-1.0]])]});
            var Q26;
            Q26=makeQuery(id+"F0.imprint","IMPRINT",FACE,{"disambiguationData":[TD([[makeQuery(id+"F0.imprint","IMPRINT",EDGE,{"derivedFrom":sQuery(id+"F0.wireOp",EDGE,"E719")}),-1.0]])]});
            var Q27;
            Q27=makeQuery(id+"F0.imprint","IMPRINT",FACE,{"disambiguationData":[TD([[makeQuery(id+"F0.imprint","IMPRINT",EDGE,{"derivedFrom":sQuery(id+"F0.wireOp",EDGE,"E715")}),-1.0]])]});
            extrude(context, id + "F3", {"entities" : qUnion([Q0, Q1, Q2, Q3, Q4, Q5, Q6, Q7, Q8, Q9, Q10, Q11, Q12, Q13, Q14, Q15, Q16, Q17, Q18, Q19, Q20, Q21, Q22, Q23, Q24, Q25, Q26, Q27]), "depth" : 2 * mm, "offsetDistance" : 25 * mm});
        }
        {
            var Q0;
            Q0=makeQuery(id+"F0.imprint","IMPRINT",FACE,{"disambiguationData":[TD([[makeQuery(id+"F0.imprint","IMPRINT",EDGE,{"derivedFrom":sQuery(id+"F0.wireOp",EDGE,"E8")}),-1.0]])]});
            var Q1;
            Q1=makeQuery(id+"F0.imprint","IMPRINT",FACE,{"disambiguationData":[TD([[makeQuery(id+"F0.imprint","IMPRINT",EDGE,{"derivedFrom":sQuery(id+"F0.wireOp",EDGE,"E4")}),-1.0]])]});
            var Q2;
            Q2=makeQuery(id+"F0.imprint","IMPRINT",FACE,{"disambiguationData":[TD([[makeQuery(id+"F0.imprint","IMPRINT",EDGE,{"derivedFrom":sQuery(id+"F0.wireOp",EDGE,"E109")}),-1.0]])]});
            var Q3;
            Q3=makeQuery(id+"F0.imprint","IMPRINT",FACE,{"disambiguationData":[TD([[makeQuery(id+"F0.imprint","IMPRINT",EDGE,{"derivedFrom":sQuery(id+"F0.wireOp",EDGE,"E105")}),-1.0]])]});
            var Q4;
            Q4=makeQuery(id+"F0.imprint","IMPRINT",FACE,{"disambiguationData":[TD([[makeQuery(id+"F0.imprint","IMPRINT",EDGE,{"derivedFrom":sQuery(id+"F0.wireOp",EDGE,"E214")}),-1.0]])]});
            var Q5;
            Q5=makeQuery(id+"F0.imprint","IMPRINT",FACE,{"disambiguationData":[TD([[makeQuery(id+"F0.imprint","IMPRINT",EDGE,{"derivedFrom":sQuery(id+"F0.wireOp",EDGE,"E210")}),-1.0]])]});
            var Q6;
            Q6=makeQuery(id+"F0.imprint","IMPRINT",FACE,{"disambiguationData":[TD([[makeQuery(id+"F0.imprint","IMPRINT",EDGE,{"derivedFrom":sQuery(id+"F0.wireOp",EDGE,"E315")}),-1.0]])]});
            var Q7;
            Q7=makeQuery(id+"F0.imprint","IMPRINT",FACE,{"disambiguationData":[TD([[makeQuery(id+"F0.imprint","IMPRINT",EDGE,{"derivedFrom":sQuery(id+"F0.wireOp",EDGE,"E311")}),-1.0]])]});
            var Q8;
            Q8=makeQuery(id+"F0.imprint","IMPRINT",FACE,{"disambiguationData":[TD([[makeQuery(id+"F0.imprint","IMPRINT",EDGE,{"derivedFrom":sQuery(id+"F0.wireOp",EDGE,"E416")}),-1.0]])]});
            var Q9;
            Q9=makeQuery(id+"F0.imprint","IMPRINT",FACE,{"disambiguationData":[TD([[makeQuery(id+"F0.imprint","IMPRINT",EDGE,{"derivedFrom":sQuery(id+"F0.wireOp",EDGE,"E412")}),-1.0]])]});
            var Q10;
            Q10=makeQuery(id+"F0.imprint","IMPRINT",FACE,{"disambiguationData":[TD([[makeQuery(id+"F0.imprint","IMPRINT",EDGE,{"derivedFrom":sQuery(id+"F0.wireOp",EDGE,"E521")}),-1.0]])]});
            var Q11;
            Q11=makeQuery(id+"F0.imprint","IMPRINT",FACE,{"disambiguationData":[TD([[makeQuery(id+"F0.imprint","IMPRINT",EDGE,{"derivedFrom":sQuery(id+"F0.wireOp",EDGE,"E618")}),-1.0]])]});
            var Q12;
            Q12=makeQuery(id+"F0.imprint","IMPRINT",FACE,{"disambiguationData":[TD([[makeQuery(id+"F0.imprint","IMPRINT",EDGE,{"derivedFrom":sQuery(id+"F0.wireOp",EDGE,"E614")}),-1.0]])]});
            var Q13;
            Q13=makeQuery(id+"F0.imprint","IMPRINT",FACE,{"disambiguationData":[TD([[makeQuery(id+"F0.imprint","IMPRINT",EDGE,{"derivedFrom":sQuery(id+"F0.wireOp",EDGE,"E517")}),-1.0]])]});
            extrude(context, id + "F4", {"entities" : qUnion([Q0, Q1, Q2, Q3, Q4, Q5, Q6, Q7, Q8, Q9, Q10, Q11, Q12, Q13]), "depth" : 2 * mm, "offsetDistance" : 25 * mm});
        }
        {
            var Q0;
            {var subQ0=sQuery(id+"F0.wireOp",EDGE,"E2715");Q0=makeQuery(id+"F0.imprint","IMPRINT",FACE,{"disambiguationData":[TD([[makeQuery(id+"F0.imprint","IMPRINT",EDGE,{"derivedFrom":subQ0}),1.0]])]});}
            var Q1;
            Q1=makeQuery(id+"F0.imprint","IMPRINT",FACE,{"disambiguationData":[TD([[makeQuery(id+"F0.imprint","IMPRINT",EDGE,{"derivedFrom":sQuery(id+"F0.wireOp",EDGE,"E2795")}),1.0]])]});
            var Q2;
            {var subQ0=sQuery(id+"F0.wireOp",EDGE,"E2513");Q2=makeQuery(id+"F0.imprint","IMPRINT",FACE,{"disambiguationData":[TD([[makeQuery(id+"F0.imprint","IMPRINT",EDGE,{"derivedFrom":subQ0}),1.0]])]});}
            var Q3;
            Q3=makeQuery(id+"F0.imprint","IMPRINT",FACE,{"disambiguationData":[TD([[makeQuery(id+"F0.imprint","IMPRINT",EDGE,{"derivedFrom":sQuery(id+"F0.wireOp",EDGE,"E1551")}),1.0]])]});
            var Q4;
            Q4=makeQuery(id+"F0.imprint","IMPRINT",FACE,{"disambiguationData":[TD([[makeQuery(id+"F0.imprint","IMPRINT",EDGE,{"derivedFrom":sQuery(id+"F0.wireOp",EDGE,"E1660")}),1.0]])]});
            var Q5;
            Q5=makeQuery(id+"F0.imprint","IMPRINT",FACE,{"disambiguationData":[TD([[makeQuery(id+"F0.imprint","IMPRINT",EDGE,{"derivedFrom":sQuery(id+"F0.wireOp",EDGE,"E1765")}),1.0]])]});
            var Q6;
            Q6=makeQuery(id+"F0.imprint","IMPRINT",FACE,{"disambiguationData":[TD([[makeQuery(id+"F0.imprint","IMPRINT",EDGE,{"derivedFrom":sQuery(id+"F0.wireOp",EDGE,"E1870")}),1.0]])]});
            var Q7;
            Q7=makeQuery(id+"F0.imprint","IMPRINT",FACE,{"disambiguationData":[TD([[makeQuery(id+"F0.imprint","IMPRINT",EDGE,{"derivedFrom":sQuery(id+"F0.wireOp",EDGE,"E2593")}),1.0]])]});
            var Q8;
            Q8=makeQuery(id+"F0.imprint","IMPRINT",FACE,{"disambiguationData":[TD([[makeQuery(id+"F0.imprint","IMPRINT",EDGE,{"derivedFrom":sQuery(id+"F0.wireOp",EDGE,"E2488")}),1.0]])]});
            var Q9;
            Q9=makeQuery(id+"F0.imprint","IMPRINT",FACE,{"disambiguationData":[TD([[makeQuery(id+"F0.imprint","IMPRINT",EDGE,{"derivedFrom":sQuery(id+"F0.wireOp",EDGE,"E2407")}),1.0]])]});
            var Q10;
            Q10=makeQuery(id+"F0.imprint","IMPRINT",FACE,{"disambiguationData":[TD([[makeQuery(id+"F0.imprint","IMPRINT",EDGE,{"derivedFrom":sQuery(id+"F0.wireOp",EDGE,"E2080")}),1.0]])]});
            var Q11;
            Q11=makeQuery(id+"F0.imprint","IMPRINT",FACE,{"disambiguationData":[TD([[makeQuery(id+"F0.imprint","IMPRINT",EDGE,{"derivedFrom":sQuery(id+"F0.wireOp",EDGE,"E816")}),1.0]])]});
            var Q12;
            Q12=makeQuery(id+"F0.imprint","IMPRINT",FACE,{"disambiguationData":[TD([[makeQuery(id+"F0.imprint","IMPRINT",EDGE,{"derivedFrom":sQuery(id+"F0.wireOp",EDGE,"E2104")}),1.0]])]});
            var Q13;
            Q13=makeQuery(id+"F0.imprint","IMPRINT",FACE,{"disambiguationData":[TD([[makeQuery(id+"F0.imprint","IMPRINT",EDGE,{"derivedFrom":sQuery(id+"F0.wireOp",EDGE,"E1975")}),1.0]])]});
            var Q14;
            Q14=makeQuery(id+"F0.imprint","IMPRINT",FACE,{"disambiguationData":[TD([[makeQuery(id+"F0.imprint","IMPRINT",EDGE,{"derivedFrom":sQuery(id+"F0.wireOp",EDGE,"E1894")}),1.0]])]});
            var Q15;
            Q15=makeQuery(id+"F0.imprint","IMPRINT",FACE,{"disambiguationData":[TD([[makeQuery(id+"F0.imprint","IMPRINT",EDGE,{"derivedFrom":sQuery(id+"F0.wireOp",EDGE,"E1789")}),1.0]])]});
            var Q16;
            Q16=makeQuery(id+"F0.imprint","IMPRINT",FACE,{"disambiguationData":[TD([[makeQuery(id+"F0.imprint","IMPRINT",EDGE,{"derivedFrom":sQuery(id+"F0.wireOp",EDGE,"E1684")}),1.0]])]});
            var Q17;
            Q17=makeQuery(id+"F0.imprint","IMPRINT",FACE,{"disambiguationData":[TD([[makeQuery(id+"F0.imprint","IMPRINT",EDGE,{"derivedFrom":sQuery(id+"F0.wireOp",EDGE,"E1579")}),1.0]])]});
            var Q18;
            Q18=makeQuery(id+"F0.imprint","IMPRINT",FACE,{"disambiguationData":[TD([[makeQuery(id+"F0.imprint","IMPRINT",EDGE,{"derivedFrom":sQuery(id+"F0.wireOp",EDGE,"E1450")}),1.0]])]});
            var Q19;
            Q19=makeQuery(id+"F0.imprint","IMPRINT",FACE,{"disambiguationData":[TD([[makeQuery(id+"F0.imprint","IMPRINT",EDGE,{"derivedFrom":sQuery(id+"F0.wireOp",EDGE,"E1575")}),1.0]])]});
            var Q20;
            Q20=makeQuery(id+"F0.imprint","IMPRINT",FACE,{"disambiguationData":[TD([[makeQuery(id+"F0.imprint","IMPRINT",EDGE,{"derivedFrom":sQuery(id+"F0.wireOp",EDGE,"E1240")}),1.0]])]});
            var Q21;
            Q21=makeQuery(id+"F0.imprint","IMPRINT",FACE,{"disambiguationData":[TD([[makeQuery(id+"F0.imprint","IMPRINT",EDGE,{"derivedFrom":sQuery(id+"F0.wireOp",EDGE,"E1139")}),1.0]])]});
            var Q22;
            Q22=makeQuery(id+"F0.imprint","IMPRINT",FACE,{"disambiguationData":[TD([[makeQuery(id+"F0.imprint","IMPRINT",EDGE,{"derivedFrom":sQuery(id+"F0.wireOp",EDGE,"E1026")}),1.0]])]});
            var Q23;
            Q23=makeQuery(id+"F0.imprint","IMPRINT",FACE,{"disambiguationData":[TD([[makeQuery(id+"F0.imprint","IMPRINT",EDGE,{"derivedFrom":sQuery(id+"F0.wireOp",EDGE,"E1999")}),1.0]])]});
            var Q24;
            {var subQ0=sQuery(id+"F0.wireOp",EDGE,"E1265");Q24=makeQuery(id+"F0.imprint","IMPRINT",FACE,{"disambiguationData":[TD([[makeQuery(id+"F0.imprint","IMPRINT",EDGE,{"derivedFrom":subQ0}),1.0]])]});}
            var Q25;
            Q25=makeQuery(id+"F0.imprint","IMPRINT",FACE,{"disambiguationData":[TD([[makeQuery(id+"F0.imprint","IMPRINT",EDGE,{"derivedFrom":sQuery(id+"F0.wireOp",EDGE,"E1345")}),1.0]])]});
            var Q26;
            {var subQ0=sQuery(id+"F0.wireOp",EDGE,"E1055");Q26=makeQuery(id+"F0.imprint","IMPRINT",FACE,{"disambiguationData":[TD([[makeQuery(id+"F0.imprint","IMPRINT",EDGE,{"derivedFrom":subQ0}),1.0]])]});}
            var Q27;
            Q27=makeQuery(id+"F0.imprint","IMPRINT",FACE,{"disambiguationData":[TD([[makeQuery(id+"F0.imprint","IMPRINT",EDGE,{"derivedFrom":sQuery(id+"F0.wireOp",EDGE,"E1135")}),1.0]])]});
            var Q28;
            {var subQ0=sQuery(id+"F0.wireOp",EDGE,"E845");Q28=makeQuery(id+"F0.imprint","IMPRINT",FACE,{"disambiguationData":[TD([[makeQuery(id+"F0.imprint","IMPRINT",EDGE,{"derivedFrom":subQ0}),1.0]])]});}
            var Q29;
            {var subQ0=sQuery(id+"F0.wireOp",EDGE,"E736");Q29=makeQuery(id+"F0.imprint","IMPRINT",FACE,{"disambiguationData":[TD([[makeQuery(id+"F0.imprint","IMPRINT",EDGE,{"derivedFrom":subQ0}),1.0]])]});}
            var Q30;
            Q30=makeQuery(id+"F0.imprint","IMPRINT",FACE,{"disambiguationData":[TD([[makeQuery(id+"F0.imprint","IMPRINT",EDGE,{"derivedFrom":sQuery(id+"F0.wireOp",EDGE,"E731")}),1.0]])]});
            var Q31;
            Q31=makeQuery(id+"F0.imprint","IMPRINT",FACE,{"disambiguationData":[TD([[makeQuery(id+"F0.imprint","IMPRINT",EDGE,{"derivedFrom":sQuery(id+"F0.wireOp",EDGE,"E840")}),1.0]])]});
            var Q32;
            Q32=makeQuery(id+"F0.imprint","IMPRINT",FACE,{"disambiguationData":[TD([[makeQuery(id+"F0.imprint","IMPRINT",EDGE,{"derivedFrom":sQuery(id+"F0.wireOp",EDGE,"E945")}),1.0]])]});
            var Q33;
            Q33=makeQuery(id+"F0.imprint","IMPRINT",FACE,{"disambiguationData":[TD([[makeQuery(id+"F0.imprint","IMPRINT",EDGE,{"derivedFrom":sQuery(id+"F0.wireOp",EDGE,"E1050")}),1.0]])]});
            var Q34;
            Q34=makeQuery(id+"F0.imprint","IMPRINT",FACE,{"disambiguationData":[TD([[makeQuery(id+"F0.imprint","IMPRINT",EDGE,{"derivedFrom":sQuery(id+"F0.wireOp",EDGE,"E303")}),1.0]])]});
            var Q35;
            Q35=makeQuery(id+"F0.imprint","IMPRINT",FACE,{"disambiguationData":[TD([[makeQuery(id+"F0.imprint","IMPRINT",EDGE,{"derivedFrom":sQuery(id+"F0.wireOp",EDGE,"E202")}),1.0]])]});
            var Q36;
            Q36=makeQuery(id+"F0.imprint","IMPRINT",FACE,{"disambiguationData":[TD([[makeQuery(id+"F0.imprint","IMPRINT",EDGE,{"derivedFrom":sQuery(id+"F0.wireOp",EDGE,"E1369")}),1.0]])]});
            var Q37;
            Q37=makeQuery(id+"F0.imprint","IMPRINT",FACE,{"disambiguationData":[TD([[makeQuery(id+"F0.imprint","IMPRINT",EDGE,{"derivedFrom":sQuery(id+"F0.wireOp",EDGE,"E97")}),1.0]])]});
            var Q38;
            Q38=makeQuery(id+"F0.imprint","IMPRINT",FACE,{"disambiguationData":[TD([[makeQuery(id+"F0.imprint","IMPRINT",EDGE,{"derivedFrom":sQuery(id+"F0.wireOp",EDGE,"E198")}),1.0]])]});
            var Q39;
            Q39=makeQuery(id+"F0.imprint","IMPRINT",FACE,{"disambiguationData":[TD([[makeQuery(id+"F0.imprint","IMPRINT",EDGE,{"derivedFrom":sQuery(id+"F0.wireOp",EDGE,"E327")}),1.0]])]});
            var Q40;
            Q40=makeQuery(id+"F0.imprint","IMPRINT",FACE,{"disambiguationData":[TD([[makeQuery(id+"F0.imprint","IMPRINT",EDGE,{"derivedFrom":sQuery(id+"F0.wireOp",EDGE,"E428")}),1.0]])]});
            var Q41;
            Q41=makeQuery(id+"F0.imprint","IMPRINT",FACE,{"disambiguationData":[TD([[makeQuery(id+"F0.imprint","IMPRINT",EDGE,{"derivedFrom":sQuery(id+"F0.wireOp",EDGE,"E509")}),1.0]])]});
            var Q42;
            Q42=makeQuery(id+"F0.imprint","IMPRINT",FACE,{"disambiguationData":[TD([[makeQuery(id+"F0.imprint","IMPRINT",EDGE,{"derivedFrom":sQuery(id+"F0.wireOp",EDGE,"E630")}),1.0]])]});
            var Q43;
            Q43=makeQuery(id+"F0.imprint","IMPRINT",FACE,{"disambiguationData":[TD([[makeQuery(id+"F0.imprint","IMPRINT",EDGE,{"derivedFrom":sQuery(id+"F0.wireOp",EDGE,"E2383")}),1.0]])]});
            var Q44;
            Q44=makeQuery(id+"F0.imprint","IMPRINT",FACE,{"disambiguationData":[TD([[makeQuery(id+"F0.imprint","IMPRINT",EDGE,{"derivedFrom":sQuery(id+"F0.wireOp",EDGE,"E2205")}),1.0]])]});
            extrude(context, id + "F5", {"entities" : qUnion([Q0, Q1, Q2, Q3, Q4, Q5, Q6, Q7, Q8, Q9, Q10, Q11, Q12, Q13, Q14, Q15, Q16, Q17, Q18, Q19, Q20, Q21, Q22, Q23, Q24, Q25, Q26, Q27, Q28, Q29, Q30, Q31, Q32, Q33, Q34, Q35, Q36, Q37, Q38, Q39, Q40, Q41, Q42, Q43, Q44]), "depth" : 0.9 * mm, "offsetDistance" : 25 * mm});
        }
        {
            var Q0;
            Q0=makeQuery(id+"F1.opExtrude","CAP_FACE",FACE,{"disambiguationData":[OSD([sQuery(id+"F0.wireOp",EDGE,"E2799"),sQuery(id+"F0.wireOp",EDGE,"E2800"),sQuery(id+"F0.wireOp",EDGE,"E2801"),sQuery(id+"F0.wireOp",EDGE,"E2802"),sQuery(id+"F0.wireOp",EDGE,"E2811"),sQuery(id+"F0.wireOp",EDGE,"E2812"),sQuery(id+"F0.wireOp",EDGE,"E2813"),sQuery(id+"F0.wireOp",EDGE,"E2814"),sQuery(id+"F0.wireOp",EDGE,"E2815"),sQuery(id+"F0.wireOp",EDGE,"E2816"),sQuery(id+"F0.wireOp",EDGE,"E2817"),sQuery(id+"F0.wireOp",EDGE,"E2818"),sQuery(id+"F0.wireOp",EDGE,"E2819"),sQuery(id+"F0.wireOp",EDGE,"E2820"),sQuery(id+"F0.wireOp",EDGE,"E2821"),sQuery(id+"F0.wireOp",EDGE,"E2822"),sQuery(id+"F0.wireOp",EDGE,"E2823"),sQuery(id+"F0.wireOp",EDGE,"E2824"),sQuery(id+"F0.wireOp",EDGE,"E2825"),sQuery(id+"F0.wireOp",EDGE,"E2826"),sQuery(id+"F0.wireOp",EDGE,"E2827"),sQuery(id+"F0.wireOp",EDGE,"E2828"),sQuery(id+"F0.wireOp",EDGE,"E2829"),sQuery(id+"F0.wireOp",EDGE,"E2830"),sQuery(id+"F0.wireOp",EDGE,"E2831"),sQuery(id+"F0.wireOp",EDGE,"E2832"),sQuery(id+"F0.wireOp",EDGE,"E2833"),sQuery(id+"F0.wireOp",EDGE,"E2834"),sQuery(id+"F0.wireOp",EDGE,"E2835"),sQuery(id+"F0.wireOp",EDGE,"E2836"),sQuery(id+"F0.wireOp",EDGE,"E2837"),sQuery(id+"F0.wireOp",EDGE,"E2838"),sQuery(id+"F0.wireOp",EDGE,"E2839"),sQuery(id+"F0.wireOp",EDGE,"E2840"),sQuery(id+"F0.wireOp",EDGE,"E2841"),sQuery(id+"F0.wireOp",EDGE,"E2842"),sQuery(id+"F0.wireOp",EDGE,"E2843"),sQuery(id+"F0.wireOp",EDGE,"E2844"),sQuery(id+"F0.wireOp",EDGE,"E2845"),sQuery(id+"F0.wireOp",EDGE,"E2846"),sQuery(id+"F0.wireOp",EDGE,"E2847"),sQuery(id+"F0.wireOp",EDGE,"E2848"),sQuery(id+"F0.wireOp",EDGE,"E2849"),sQuery(id+"F0.wireOp",EDGE,"E2850"),sQuery(id+"F0.wireOp",EDGE,"E2851"),sQuery(id+"F0.wireOp",EDGE,"E2852"),sQuery(id+"F0.wireOp",EDGE,"E2853"),sQuery(id+"F0.wireOp",EDGE,"E2854"),sQuery(id+"F0.wireOp",EDGE,"E2855"),sQuery(id+"F0.wireOp",EDGE,"E2856"),sQuery(id+"F0.wireOp",EDGE,"E2857"),sQuery(id+"F0.wireOp",EDGE,"E2858"),sQuery(id+"F0.wireOp",EDGE,"E2859"),sQuery(id+"F0.wireOp",EDGE,"E2860"),sQuery(id+"F0.wireOp",EDGE,"E2861"),sQuery(id+"F0.wireOp",EDGE,"E2862"),sQuery(id+"F0.wireOp",EDGE,"E2863"),sQuery(id+"F0.wireOp",EDGE,"E2864"),sQuery(id+"F0.wireOp",EDGE,"E2865"),sQuery(id+"F0.wireOp",EDGE,"E2866"),sQuery(id+"F0.wireOp",EDGE,"E2867"),sQuery(id+"F0.wireOp",EDGE,"E2868"),sQuery(id+"F0.wireOp",EDGE,"E2869"),sQuery(id+"F0.wireOp",EDGE,"E2870"),sQuery(id+"F0.wireOp",EDGE,"E2871"),sQuery(id+"F0.wireOp",EDGE,"E2872"),sQuery(id+"F0.wireOp",EDGE,"E2873"),sQuery(id+"F0.wireOp",EDGE,"E2874"),sQuery(id+"F0.wireOp",EDGE,"E2875"),sQuery(id+"F0.wireOp",EDGE,"E2876"),sQuery(id+"F0.wireOp",EDGE,"E2877"),sQuery(id+"F0.wireOp",EDGE,"E2878"),sQuery(id+"F0.wireOp",EDGE,"E2879"),sQuery(id+"F0.wireOp",EDGE,"E2880"),sQuery(id+"F0.wireOp",EDGE,"E2881"),sQuery(id+"F0.wireOp",EDGE,"E2882"),sQuery(id+"F0.wireOp",EDGE,"E2883"),sQuery(id+"F0.wireOp",EDGE,"E2884"),sQuery(id+"F0.wireOp",EDGE,"E2885"),sQuery(id+"F0.wireOp",EDGE,"E2886"),sQuery(id+"F0.wireOp",EDGE,"E2887"),sQuery(id+"F0.wireOp",EDGE,"E2888"),sQuery(id+"F0.wireOp",EDGE,"E2889"),sQuery(id+"F0.wireOp",EDGE,"E2890"),sQuery(id+"F0.wireOp",EDGE,"E2891"),sQuery(id+"F0.wireOp",EDGE,"E2892"),sQuery(id+"F0.wireOp",EDGE,"E2893"),sQuery(id+"F0.wireOp",EDGE,"E2894"),sQuery(id+"F0.wireOp",EDGE,"E2895")])],"isStart":false});
            var Q1;
            Q1=makeQuery(id+"F1.opExtrude","CAP_FACE",FACE,{"disambiguationData":[OSD([sQuery(id+"F0.wireOp",EDGE,"E2694"),sQuery(id+"F0.wireOp",EDGE,"E2695"),sQuery(id+"F0.wireOp",EDGE,"E2696"),sQuery(id+"F0.wireOp",EDGE,"E2697"),sQuery(id+"F0.wireOp",EDGE,"E2706"),sQuery(id+"F0.wireOp",EDGE,"E2707"),sQuery(id+"F0.wireOp",EDGE,"E2708"),sQuery(id+"F0.wireOp",EDGE,"E2709"),sQuery(id+"F0.wireOp",EDGE,"E2710"),sQuery(id+"F0.wireOp",EDGE,"E2711"),sQuery(id+"F0.wireOp",EDGE,"E2712"),sQuery(id+"F0.wireOp",EDGE,"E2713"),sQuery(id+"F0.wireOp",EDGE,"E2716"),sQuery(id+"F0.wireOp",EDGE,"E2718"),sQuery(id+"F0.wireOp",EDGE,"E2719"),sQuery(id+"F0.wireOp",EDGE,"E2720"),sQuery(id+"F0.wireOp",EDGE,"E2721"),sQuery(id+"F0.wireOp",EDGE,"E2722"),sQuery(id+"F0.wireOp",EDGE,"E2723"),sQuery(id+"F0.wireOp",EDGE,"E2724"),sQuery(id+"F0.wireOp",EDGE,"E2725"),sQuery(id+"F0.wireOp",EDGE,"E2726"),sQuery(id+"F0.wireOp",EDGE,"E2727"),sQuery(id+"F0.wireOp",EDGE,"E2728"),sQuery(id+"F0.wireOp",EDGE,"E2729"),sQuery(id+"F0.wireOp",EDGE,"E2730"),sQuery(id+"F0.wireOp",EDGE,"E2731"),sQuery(id+"F0.wireOp",EDGE,"E2732"),sQuery(id+"F0.wireOp",EDGE,"E2733"),sQuery(id+"F0.wireOp",EDGE,"E2734"),sQuery(id+"F0.wireOp",EDGE,"E2735"),sQuery(id+"F0.wireOp",EDGE,"E2736"),sQuery(id+"F0.wireOp",EDGE,"E2737"),sQuery(id+"F0.wireOp",EDGE,"E2738"),sQuery(id+"F0.wireOp",EDGE,"E2739"),sQuery(id+"F0.wireOp",EDGE,"E2740"),sQuery(id+"F0.wireOp",EDGE,"E2741"),sQuery(id+"F0.wireOp",EDGE,"E2742"),sQuery(id+"F0.wireOp",EDGE,"E2743"),sQuery(id+"F0.wireOp",EDGE,"E2744"),sQuery(id+"F0.wireOp",EDGE,"E2745"),sQuery(id+"F0.wireOp",EDGE,"E2746"),sQuery(id+"F0.wireOp",EDGE,"E2747"),sQuery(id+"F0.wireOp",EDGE,"E2748"),sQuery(id+"F0.wireOp",EDGE,"E2749"),sQuery(id+"F0.wireOp",EDGE,"E2750"),sQuery(id+"F0.wireOp",EDGE,"E2751"),sQuery(id+"F0.wireOp",EDGE,"E2752"),sQuery(id+"F0.wireOp",EDGE,"E2753"),sQuery(id+"F0.wireOp",EDGE,"E2754"),sQuery(id+"F0.wireOp",EDGE,"E2755"),sQuery(id+"F0.wireOp",EDGE,"E2756"),sQuery(id+"F0.wireOp",EDGE,"E2757"),sQuery(id+"F0.wireOp",EDGE,"E2758"),sQuery(id+"F0.wireOp",EDGE,"E2759"),sQuery(id+"F0.wireOp",EDGE,"E2760"),sQuery(id+"F0.wireOp",EDGE,"E2761"),sQuery(id+"F0.wireOp",EDGE,"E2762"),sQuery(id+"F0.wireOp",EDGE,"E2763"),sQuery(id+"F0.wireOp",EDGE,"E2764"),sQuery(id+"F0.wireOp",EDGE,"E2765"),sQuery(id+"F0.wireOp",EDGE,"E2766"),sQuery(id+"F0.wireOp",EDGE,"E2767"),sQuery(id+"F0.wireOp",EDGE,"E2768"),sQuery(id+"F0.wireOp",EDGE,"E2769"),sQuery(id+"F0.wireOp",EDGE,"E2770"),sQuery(id+"F0.wireOp",EDGE,"E2771"),sQuery(id+"F0.wireOp",EDGE,"E2772"),sQuery(id+"F0.wireOp",EDGE,"E2773"),sQuery(id+"F0.wireOp",EDGE,"E2774"),sQuery(id+"F0.wireOp",EDGE,"E2775"),sQuery(id+"F0.wireOp",EDGE,"E2776"),sQuery(id+"F0.wireOp",EDGE,"E2777"),sQuery(id+"F0.wireOp",EDGE,"E2778"),sQuery(id+"F0.wireOp",EDGE,"E2779"),sQuery(id+"F0.wireOp",EDGE,"E2780"),sQuery(id+"F0.wireOp",EDGE,"E2781"),sQuery(id+"F0.wireOp",EDGE,"E2782"),sQuery(id+"F0.wireOp",EDGE,"E2783"),sQuery(id+"F0.wireOp",EDGE,"E2784"),sQuery(id+"F0.wireOp",EDGE,"E2785"),sQuery(id+"F0.wireOp",EDGE,"E2786"),sQuery(id+"F0.wireOp",EDGE,"E2787"),sQuery(id+"F0.wireOp",EDGE,"E2788"),sQuery(id+"F0.wireOp",EDGE,"E2789"),sQuery(id+"F0.wireOp",EDGE,"E2790"),sQuery(id+"F0.wireOp",EDGE,"E2791"),sQuery(id+"F0.wireOp",EDGE,"E2792"),sQuery(id+"F0.wireOp",EDGE,"E2793"),sQuery(id+"F0.wireOp",EDGE,"E2794"),sQuery(id+"F0.wireOp",EDGE,"E2795")])],"isStart":false});
            var Q2;
            Q2=makeQuery(id+"F1.opExtrude","CAP_FACE",FACE,{"disambiguationData":[OSD([sQuery(id+"F0.wireOp",EDGE,"E2597"),sQuery(id+"F0.wireOp",EDGE,"E2598"),sQuery(id+"F0.wireOp",EDGE,"E2599"),sQuery(id+"F0.wireOp",EDGE,"E2600"),sQuery(id+"F0.wireOp",EDGE,"E2609"),sQuery(id+"F0.wireOp",EDGE,"E2610"),sQuery(id+"F0.wireOp",EDGE,"E2611"),sQuery(id+"F0.wireOp",EDGE,"E2612"),sQuery(id+"F0.wireOp",EDGE,"E2613"),sQuery(id+"F0.wireOp",EDGE,"E2614"),sQuery(id+"F0.wireOp",EDGE,"E2615"),sQuery(id+"F0.wireOp",EDGE,"E2616"),sQuery(id+"F0.wireOp",EDGE,"E2617"),sQuery(id+"F0.wireOp",EDGE,"E2618"),sQuery(id+"F0.wireOp",EDGE,"E2619"),sQuery(id+"F0.wireOp",EDGE,"E2620"),sQuery(id+"F0.wireOp",EDGE,"E2621"),sQuery(id+"F0.wireOp",EDGE,"E2622"),sQuery(id+"F0.wireOp",EDGE,"E2623"),sQuery(id+"F0.wireOp",EDGE,"E2624"),sQuery(id+"F0.wireOp",EDGE,"E2625"),sQuery(id+"F0.wireOp",EDGE,"E2626"),sQuery(id+"F0.wireOp",EDGE,"E2627"),sQuery(id+"F0.wireOp",EDGE,"E2628"),sQuery(id+"F0.wireOp",EDGE,"E2629"),sQuery(id+"F0.wireOp",EDGE,"E2630"),sQuery(id+"F0.wireOp",EDGE,"E2631"),sQuery(id+"F0.wireOp",EDGE,"E2632"),sQuery(id+"F0.wireOp",EDGE,"E2633"),sQuery(id+"F0.wireOp",EDGE,"E2634"),sQuery(id+"F0.wireOp",EDGE,"E2635"),sQuery(id+"F0.wireOp",EDGE,"E2636"),sQuery(id+"F0.wireOp",EDGE,"E2637"),sQuery(id+"F0.wireOp",EDGE,"E2638"),sQuery(id+"F0.wireOp",EDGE,"E2639"),sQuery(id+"F0.wireOp",EDGE,"E2640"),sQuery(id+"F0.wireOp",EDGE,"E2641"),sQuery(id+"F0.wireOp",EDGE,"E2642"),sQuery(id+"F0.wireOp",EDGE,"E2643"),sQuery(id+"F0.wireOp",EDGE,"E2644"),sQuery(id+"F0.wireOp",EDGE,"E2645"),sQuery(id+"F0.wireOp",EDGE,"E2646"),sQuery(id+"F0.wireOp",EDGE,"E2647"),sQuery(id+"F0.wireOp",EDGE,"E2648"),sQuery(id+"F0.wireOp",EDGE,"E2649"),sQuery(id+"F0.wireOp",EDGE,"E2650"),sQuery(id+"F0.wireOp",EDGE,"E2651"),sQuery(id+"F0.wireOp",EDGE,"E2652"),sQuery(id+"F0.wireOp",EDGE,"E2653"),sQuery(id+"F0.wireOp",EDGE,"E2654"),sQuery(id+"F0.wireOp",EDGE,"E2655"),sQuery(id+"F0.wireOp",EDGE,"E2656"),sQuery(id+"F0.wireOp",EDGE,"E2657"),sQuery(id+"F0.wireOp",EDGE,"E2658"),sQuery(id+"F0.wireOp",EDGE,"E2659"),sQuery(id+"F0.wireOp",EDGE,"E2660"),sQuery(id+"F0.wireOp",EDGE,"E2661"),sQuery(id+"F0.wireOp",EDGE,"E2662"),sQuery(id+"F0.wireOp",EDGE,"E2663"),sQuery(id+"F0.wireOp",EDGE,"E2664"),sQuery(id+"F0.wireOp",EDGE,"E2665"),sQuery(id+"F0.wireOp",EDGE,"E2666"),sQuery(id+"F0.wireOp",EDGE,"E2667"),sQuery(id+"F0.wireOp",EDGE,"E2668"),sQuery(id+"F0.wireOp",EDGE,"E2669"),sQuery(id+"F0.wireOp",EDGE,"E2670"),sQuery(id+"F0.wireOp",EDGE,"E2671"),sQuery(id+"F0.wireOp",EDGE,"E2672"),sQuery(id+"F0.wireOp",EDGE,"E2673"),sQuery(id+"F0.wireOp",EDGE,"E2674"),sQuery(id+"F0.wireOp",EDGE,"E2675"),sQuery(id+"F0.wireOp",EDGE,"E2676"),sQuery(id+"F0.wireOp",EDGE,"E2677"),sQuery(id+"F0.wireOp",EDGE,"E2678"),sQuery(id+"F0.wireOp",EDGE,"E2679"),sQuery(id+"F0.wireOp",EDGE,"E2680"),sQuery(id+"F0.wireOp",EDGE,"E2681"),sQuery(id+"F0.wireOp",EDGE,"E2682"),sQuery(id+"F0.wireOp",EDGE,"E2683"),sQuery(id+"F0.wireOp",EDGE,"E2684"),sQuery(id+"F0.wireOp",EDGE,"E2685"),sQuery(id+"F0.wireOp",EDGE,"E2686"),sQuery(id+"F0.wireOp",EDGE,"E2687"),sQuery(id+"F0.wireOp",EDGE,"E2688"),sQuery(id+"F0.wireOp",EDGE,"E2689"),sQuery(id+"F0.wireOp",EDGE,"E2690"),sQuery(id+"F0.wireOp",EDGE,"E2691"),sQuery(id+"F0.wireOp",EDGE,"E2692"),sQuery(id+"F0.wireOp",EDGE,"E2693"),sQuery(id+"F0.wireOp",EDGE,"E2797")])],"isStart":false});
            var Q3;
            Q3=makeQuery(id+"F1.opExtrude","CAP_FACE",FACE,{"disambiguationData":[OSD([sQuery(id+"F0.wireOp",EDGE,"E2492"),sQuery(id+"F0.wireOp",EDGE,"E2493"),sQuery(id+"F0.wireOp",EDGE,"E2494"),sQuery(id+"F0.wireOp",EDGE,"E2495"),sQuery(id+"F0.wireOp",EDGE,"E2504"),sQuery(id+"F0.wireOp",EDGE,"E2505"),sQuery(id+"F0.wireOp",EDGE,"E2506"),sQuery(id+"F0.wireOp",EDGE,"E2507"),sQuery(id+"F0.wireOp",EDGE,"E2508"),sQuery(id+"F0.wireOp",EDGE,"E2509"),sQuery(id+"F0.wireOp",EDGE,"E2510"),sQuery(id+"F0.wireOp",EDGE,"E2511"),sQuery(id+"F0.wireOp",EDGE,"E2514"),sQuery(id+"F0.wireOp",EDGE,"E2516"),sQuery(id+"F0.wireOp",EDGE,"E2517"),sQuery(id+"F0.wireOp",EDGE,"E2518"),sQuery(id+"F0.wireOp",EDGE,"E2519"),sQuery(id+"F0.wireOp",EDGE,"E2520"),sQuery(id+"F0.wireOp",EDGE,"E2521"),sQuery(id+"F0.wireOp",EDGE,"E2522"),sQuery(id+"F0.wireOp",EDGE,"E2523"),sQuery(id+"F0.wireOp",EDGE,"E2524"),sQuery(id+"F0.wireOp",EDGE,"E2525"),sQuery(id+"F0.wireOp",EDGE,"E2526"),sQuery(id+"F0.wireOp",EDGE,"E2527"),sQuery(id+"F0.wireOp",EDGE,"E2528"),sQuery(id+"F0.wireOp",EDGE,"E2529"),sQuery(id+"F0.wireOp",EDGE,"E2530"),sQuery(id+"F0.wireOp",EDGE,"E2531"),sQuery(id+"F0.wireOp",EDGE,"E2532"),sQuery(id+"F0.wireOp",EDGE,"E2533"),sQuery(id+"F0.wireOp",EDGE,"E2534"),sQuery(id+"F0.wireOp",EDGE,"E2535"),sQuery(id+"F0.wireOp",EDGE,"E2536"),sQuery(id+"F0.wireOp",EDGE,"E2537"),sQuery(id+"F0.wireOp",EDGE,"E2538"),sQuery(id+"F0.wireOp",EDGE,"E2539"),sQuery(id+"F0.wireOp",EDGE,"E2540"),sQuery(id+"F0.wireOp",EDGE,"E2541"),sQuery(id+"F0.wireOp",EDGE,"E2542"),sQuery(id+"F0.wireOp",EDGE,"E2543"),sQuery(id+"F0.wireOp",EDGE,"E2544"),sQuery(id+"F0.wireOp",EDGE,"E2545"),sQuery(id+"F0.wireOp",EDGE,"E2546"),sQuery(id+"F0.wireOp",EDGE,"E2547"),sQuery(id+"F0.wireOp",EDGE,"E2548"),sQuery(id+"F0.wireOp",EDGE,"E2549"),sQuery(id+"F0.wireOp",EDGE,"E2550"),sQuery(id+"F0.wireOp",EDGE,"E2551"),sQuery(id+"F0.wireOp",EDGE,"E2552"),sQuery(id+"F0.wireOp",EDGE,"E2553"),sQuery(id+"F0.wireOp",EDGE,"E2554"),sQuery(id+"F0.wireOp",EDGE,"E2555"),sQuery(id+"F0.wireOp",EDGE,"E2556"),sQuery(id+"F0.wireOp",EDGE,"E2557"),sQuery(id+"F0.wireOp",EDGE,"E2558"),sQuery(id+"F0.wireOp",EDGE,"E2559"),sQuery(id+"F0.wireOp",EDGE,"E2560"),sQuery(id+"F0.wireOp",EDGE,"E2561"),sQuery(id+"F0.wireOp",EDGE,"E2562"),sQuery(id+"F0.wireOp",EDGE,"E2563"),sQuery(id+"F0.wireOp",EDGE,"E2564"),sQuery(id+"F0.wireOp",EDGE,"E2565"),sQuery(id+"F0.wireOp",EDGE,"E2566"),sQuery(id+"F0.wireOp",EDGE,"E2567"),sQuery(id+"F0.wireOp",EDGE,"E2568"),sQuery(id+"F0.wireOp",EDGE,"E2569"),sQuery(id+"F0.wireOp",EDGE,"E2570"),sQuery(id+"F0.wireOp",EDGE,"E2571"),sQuery(id+"F0.wireOp",EDGE,"E2572"),sQuery(id+"F0.wireOp",EDGE,"E2573"),sQuery(id+"F0.wireOp",EDGE,"E2574"),sQuery(id+"F0.wireOp",EDGE,"E2575"),sQuery(id+"F0.wireOp",EDGE,"E2576"),sQuery(id+"F0.wireOp",EDGE,"E2577"),sQuery(id+"F0.wireOp",EDGE,"E2578"),sQuery(id+"F0.wireOp",EDGE,"E2579"),sQuery(id+"F0.wireOp",EDGE,"E2580"),sQuery(id+"F0.wireOp",EDGE,"E2581"),sQuery(id+"F0.wireOp",EDGE,"E2582"),sQuery(id+"F0.wireOp",EDGE,"E2583"),sQuery(id+"F0.wireOp",EDGE,"E2584"),sQuery(id+"F0.wireOp",EDGE,"E2585"),sQuery(id+"F0.wireOp",EDGE,"E2586"),sQuery(id+"F0.wireOp",EDGE,"E2587"),sQuery(id+"F0.wireOp",EDGE,"E2588"),sQuery(id+"F0.wireOp",EDGE,"E2589"),sQuery(id+"F0.wireOp",EDGE,"E2590"),sQuery(id+"F0.wireOp",EDGE,"E2591"),sQuery(id+"F0.wireOp",EDGE,"E2592"),sQuery(id+"F0.wireOp",EDGE,"E2593")])],"isStart":false});
            var Q4;
            Q4=makeQuery(id+"F1.opExtrude","CAP_FACE",FACE,{"disambiguationData":[OSD([sQuery(id+"F0.wireOp",EDGE,"E2387"),sQuery(id+"F0.wireOp",EDGE,"E2388"),sQuery(id+"F0.wireOp",EDGE,"E2389"),sQuery(id+"F0.wireOp",EDGE,"E2390"),sQuery(id+"F0.wireOp",EDGE,"E2399"),sQuery(id+"F0.wireOp",EDGE,"E2400"),sQuery(id+"F0.wireOp",EDGE,"E2401"),sQuery(id+"F0.wireOp",EDGE,"E2402"),sQuery(id+"F0.wireOp",EDGE,"E2403"),sQuery(id+"F0.wireOp",EDGE,"E2404"),sQuery(id+"F0.wireOp",EDGE,"E2405"),sQuery(id+"F0.wireOp",EDGE,"E2406"),sQuery(id+"F0.wireOp",EDGE,"E2409"),sQuery(id+"F0.wireOp",EDGE,"E2411"),sQuery(id+"F0.wireOp",EDGE,"E2412"),sQuery(id+"F0.wireOp",EDGE,"E2413"),sQuery(id+"F0.wireOp",EDGE,"E2414"),sQuery(id+"F0.wireOp",EDGE,"E2415"),sQuery(id+"F0.wireOp",EDGE,"E2416"),sQuery(id+"F0.wireOp",EDGE,"E2417"),sQuery(id+"F0.wireOp",EDGE,"E2418"),sQuery(id+"F0.wireOp",EDGE,"E2419"),sQuery(id+"F0.wireOp",EDGE,"E2420"),sQuery(id+"F0.wireOp",EDGE,"E2421"),sQuery(id+"F0.wireOp",EDGE,"E2422"),sQuery(id+"F0.wireOp",EDGE,"E2423"),sQuery(id+"F0.wireOp",EDGE,"E2424"),sQuery(id+"F0.wireOp",EDGE,"E2425"),sQuery(id+"F0.wireOp",EDGE,"E2426"),sQuery(id+"F0.wireOp",EDGE,"E2427"),sQuery(id+"F0.wireOp",EDGE,"E2428"),sQuery(id+"F0.wireOp",EDGE,"E2429"),sQuery(id+"F0.wireOp",EDGE,"E2430"),sQuery(id+"F0.wireOp",EDGE,"E2431"),sQuery(id+"F0.wireOp",EDGE,"E2432"),sQuery(id+"F0.wireOp",EDGE,"E2433"),sQuery(id+"F0.wireOp",EDGE,"E2434"),sQuery(id+"F0.wireOp",EDGE,"E2435"),sQuery(id+"F0.wireOp",EDGE,"E2436"),sQuery(id+"F0.wireOp",EDGE,"E2437"),sQuery(id+"F0.wireOp",EDGE,"E2438"),sQuery(id+"F0.wireOp",EDGE,"E2439"),sQuery(id+"F0.wireOp",EDGE,"E2440"),sQuery(id+"F0.wireOp",EDGE,"E2441"),sQuery(id+"F0.wireOp",EDGE,"E2442"),sQuery(id+"F0.wireOp",EDGE,"E2443"),sQuery(id+"F0.wireOp",EDGE,"E2444"),sQuery(id+"F0.wireOp",EDGE,"E2445"),sQuery(id+"F0.wireOp",EDGE,"E2446"),sQuery(id+"F0.wireOp",EDGE,"E2447"),sQuery(id+"F0.wireOp",EDGE,"E2448"),sQuery(id+"F0.wireOp",EDGE,"E2449"),sQuery(id+"F0.wireOp",EDGE,"E2450"),sQuery(id+"F0.wireOp",EDGE,"E2451"),sQuery(id+"F0.wireOp",EDGE,"E2452"),sQuery(id+"F0.wireOp",EDGE,"E2453"),sQuery(id+"F0.wireOp",EDGE,"E2454"),sQuery(id+"F0.wireOp",EDGE,"E2455"),sQuery(id+"F0.wireOp",EDGE,"E2456"),sQuery(id+"F0.wireOp",EDGE,"E2457"),sQuery(id+"F0.wireOp",EDGE,"E2458"),sQuery(id+"F0.wireOp",EDGE,"E2459"),sQuery(id+"F0.wireOp",EDGE,"E2460"),sQuery(id+"F0.wireOp",EDGE,"E2461"),sQuery(id+"F0.wireOp",EDGE,"E2462"),sQuery(id+"F0.wireOp",EDGE,"E2463"),sQuery(id+"F0.wireOp",EDGE,"E2464"),sQuery(id+"F0.wireOp",EDGE,"E2465"),sQuery(id+"F0.wireOp",EDGE,"E2466"),sQuery(id+"F0.wireOp",EDGE,"E2467"),sQuery(id+"F0.wireOp",EDGE,"E2468"),sQuery(id+"F0.wireOp",EDGE,"E2469"),sQuery(id+"F0.wireOp",EDGE,"E2470"),sQuery(id+"F0.wireOp",EDGE,"E2471"),sQuery(id+"F0.wireOp",EDGE,"E2472"),sQuery(id+"F0.wireOp",EDGE,"E2473"),sQuery(id+"F0.wireOp",EDGE,"E2474"),sQuery(id+"F0.wireOp",EDGE,"E2475"),sQuery(id+"F0.wireOp",EDGE,"E2476"),sQuery(id+"F0.wireOp",EDGE,"E2477"),sQuery(id+"F0.wireOp",EDGE,"E2478"),sQuery(id+"F0.wireOp",EDGE,"E2479"),sQuery(id+"F0.wireOp",EDGE,"E2480"),sQuery(id+"F0.wireOp",EDGE,"E2481"),sQuery(id+"F0.wireOp",EDGE,"E2482"),sQuery(id+"F0.wireOp",EDGE,"E2483"),sQuery(id+"F0.wireOp",EDGE,"E2484"),sQuery(id+"F0.wireOp",EDGE,"E2485"),sQuery(id+"F0.wireOp",EDGE,"E2486"),sQuery(id+"F0.wireOp",EDGE,"E2487"),sQuery(id+"F0.wireOp",EDGE,"E2488"),sQuery(id+"F0.wireOp",EDGE,"E2595")])],"isStart":false});
            var Q5;
            Q5=makeQuery(id+"F1.opExtrude","CAP_FACE",FACE,{"disambiguationData":[OSD([sQuery(id+"F0.wireOp",EDGE,"E2286"),sQuery(id+"F0.wireOp",EDGE,"E2287"),sQuery(id+"F0.wireOp",EDGE,"E2288"),sQuery(id+"F0.wireOp",EDGE,"E2289"),sQuery(id+"F0.wireOp",EDGE,"E2298"),sQuery(id+"F0.wireOp",EDGE,"E2299"),sQuery(id+"F0.wireOp",EDGE,"E2300"),sQuery(id+"F0.wireOp",EDGE,"E2301"),sQuery(id+"F0.wireOp",EDGE,"E2302"),sQuery(id+"F0.wireOp",EDGE,"E2303"),sQuery(id+"F0.wireOp",EDGE,"E2304"),sQuery(id+"F0.wireOp",EDGE,"E2305"),sQuery(id+"F0.wireOp",EDGE,"E2306"),sQuery(id+"F0.wireOp",EDGE,"E2307"),sQuery(id+"F0.wireOp",EDGE,"E2308"),sQuery(id+"F0.wireOp",EDGE,"E2309"),sQuery(id+"F0.wireOp",EDGE,"E2310"),sQuery(id+"F0.wireOp",EDGE,"E2311"),sQuery(id+"F0.wireOp",EDGE,"E2312"),sQuery(id+"F0.wireOp",EDGE,"E2313"),sQuery(id+"F0.wireOp",EDGE,"E2314"),sQuery(id+"F0.wireOp",EDGE,"E2315"),sQuery(id+"F0.wireOp",EDGE,"E2316"),sQuery(id+"F0.wireOp",EDGE,"E2317"),sQuery(id+"F0.wireOp",EDGE,"E2318"),sQuery(id+"F0.wireOp",EDGE,"E2319"),sQuery(id+"F0.wireOp",EDGE,"E2320"),sQuery(id+"F0.wireOp",EDGE,"E2321"),sQuery(id+"F0.wireOp",EDGE,"E2322"),sQuery(id+"F0.wireOp",EDGE,"E2323"),sQuery(id+"F0.wireOp",EDGE,"E2324"),sQuery(id+"F0.wireOp",EDGE,"E2325"),sQuery(id+"F0.wireOp",EDGE,"E2326"),sQuery(id+"F0.wireOp",EDGE,"E2327"),sQuery(id+"F0.wireOp",EDGE,"E2328"),sQuery(id+"F0.wireOp",EDGE,"E2329"),sQuery(id+"F0.wireOp",EDGE,"E2330"),sQuery(id+"F0.wireOp",EDGE,"E2331"),sQuery(id+"F0.wireOp",EDGE,"E2332"),sQuery(id+"F0.wireOp",EDGE,"E2333"),sQuery(id+"F0.wireOp",EDGE,"E2334"),sQuery(id+"F0.wireOp",EDGE,"E2335"),sQuery(id+"F0.wireOp",EDGE,"E2336"),sQuery(id+"F0.wireOp",EDGE,"E2337"),sQuery(id+"F0.wireOp",EDGE,"E2338"),sQuery(id+"F0.wireOp",EDGE,"E2339"),sQuery(id+"F0.wireOp",EDGE,"E2340"),sQuery(id+"F0.wireOp",EDGE,"E2341"),sQuery(id+"F0.wireOp",EDGE,"E2342"),sQuery(id+"F0.wireOp",EDGE,"E2343"),sQuery(id+"F0.wireOp",EDGE,"E2344"),sQuery(id+"F0.wireOp",EDGE,"E2345"),sQuery(id+"F0.wireOp",EDGE,"E2346"),sQuery(id+"F0.wireOp",EDGE,"E2347"),sQuery(id+"F0.wireOp",EDGE,"E2348"),sQuery(id+"F0.wireOp",EDGE,"E2349"),sQuery(id+"F0.wireOp",EDGE,"E2350"),sQuery(id+"F0.wireOp",EDGE,"E2351"),sQuery(id+"F0.wireOp",EDGE,"E2352"),sQuery(id+"F0.wireOp",EDGE,"E2353"),sQuery(id+"F0.wireOp",EDGE,"E2354"),sQuery(id+"F0.wireOp",EDGE,"E2355"),sQuery(id+"F0.wireOp",EDGE,"E2356"),sQuery(id+"F0.wireOp",EDGE,"E2357"),sQuery(id+"F0.wireOp",EDGE,"E2358"),sQuery(id+"F0.wireOp",EDGE,"E2359"),sQuery(id+"F0.wireOp",EDGE,"E2360"),sQuery(id+"F0.wireOp",EDGE,"E2361"),sQuery(id+"F0.wireOp",EDGE,"E2362"),sQuery(id+"F0.wireOp",EDGE,"E2363"),sQuery(id+"F0.wireOp",EDGE,"E2364"),sQuery(id+"F0.wireOp",EDGE,"E2365"),sQuery(id+"F0.wireOp",EDGE,"E2366"),sQuery(id+"F0.wireOp",EDGE,"E2367"),sQuery(id+"F0.wireOp",EDGE,"E2368"),sQuery(id+"F0.wireOp",EDGE,"E2369"),sQuery(id+"F0.wireOp",EDGE,"E2370"),sQuery(id+"F0.wireOp",EDGE,"E2371"),sQuery(id+"F0.wireOp",EDGE,"E2372"),sQuery(id+"F0.wireOp",EDGE,"E2373"),sQuery(id+"F0.wireOp",EDGE,"E2374"),sQuery(id+"F0.wireOp",EDGE,"E2375"),sQuery(id+"F0.wireOp",EDGE,"E2376"),sQuery(id+"F0.wireOp",EDGE,"E2377"),sQuery(id+"F0.wireOp",EDGE,"E2378"),sQuery(id+"F0.wireOp",EDGE,"E2379"),sQuery(id+"F0.wireOp",EDGE,"E2380"),sQuery(id+"F0.wireOp",EDGE,"E2381"),sQuery(id+"F0.wireOp",EDGE,"E2382"),sQuery(id+"F0.wireOp",EDGE,"E2383"),sQuery(id+"F0.wireOp",EDGE,"E2490")])],"isStart":false});
            var Q6;
            Q6=makeQuery(id+"F1.opExtrude","CAP_FACE",FACE,{"disambiguationData":[OSD([sQuery(id+"F0.wireOp",EDGE,"E2185"),sQuery(id+"F0.wireOp",EDGE,"E2186"),sQuery(id+"F0.wireOp",EDGE,"E2187"),sQuery(id+"F0.wireOp",EDGE,"E2188"),sQuery(id+"F0.wireOp",EDGE,"E2197"),sQuery(id+"F0.wireOp",EDGE,"E2198"),sQuery(id+"F0.wireOp",EDGE,"E2199"),sQuery(id+"F0.wireOp",EDGE,"E2200"),sQuery(id+"F0.wireOp",EDGE,"E2201"),sQuery(id+"F0.wireOp",EDGE,"E2202"),sQuery(id+"F0.wireOp",EDGE,"E2203"),sQuery(id+"F0.wireOp",EDGE,"E2204"),sQuery(id+"F0.wireOp",EDGE,"E2207"),sQuery(id+"F0.wireOp",EDGE,"E2209"),sQuery(id+"F0.wireOp",EDGE,"E2210"),sQuery(id+"F0.wireOp",EDGE,"E2211"),sQuery(id+"F0.wireOp",EDGE,"E2212"),sQuery(id+"F0.wireOp",EDGE,"E2213"),sQuery(id+"F0.wireOp",EDGE,"E2214"),sQuery(id+"F0.wireOp",EDGE,"E2215"),sQuery(id+"F0.wireOp",EDGE,"E2216"),sQuery(id+"F0.wireOp",EDGE,"E2217"),sQuery(id+"F0.wireOp",EDGE,"E2218"),sQuery(id+"F0.wireOp",EDGE,"E2219"),sQuery(id+"F0.wireOp",EDGE,"E2220"),sQuery(id+"F0.wireOp",EDGE,"E2221"),sQuery(id+"F0.wireOp",EDGE,"E2222"),sQuery(id+"F0.wireOp",EDGE,"E2223"),sQuery(id+"F0.wireOp",EDGE,"E2224"),sQuery(id+"F0.wireOp",EDGE,"E2225"),sQuery(id+"F0.wireOp",EDGE,"E2226"),sQuery(id+"F0.wireOp",EDGE,"E2227"),sQuery(id+"F0.wireOp",EDGE,"E2228"),sQuery(id+"F0.wireOp",EDGE,"E2229"),sQuery(id+"F0.wireOp",EDGE,"E2230"),sQuery(id+"F0.wireOp",EDGE,"E2231"),sQuery(id+"F0.wireOp",EDGE,"E2232"),sQuery(id+"F0.wireOp",EDGE,"E2233"),sQuery(id+"F0.wireOp",EDGE,"E2234"),sQuery(id+"F0.wireOp",EDGE,"E2235"),sQuery(id+"F0.wireOp",EDGE,"E2236"),sQuery(id+"F0.wireOp",EDGE,"E2237"),sQuery(id+"F0.wireOp",EDGE,"E2238"),sQuery(id+"F0.wireOp",EDGE,"E2239"),sQuery(id+"F0.wireOp",EDGE,"E2240"),sQuery(id+"F0.wireOp",EDGE,"E2241"),sQuery(id+"F0.wireOp",EDGE,"E2242"),sQuery(id+"F0.wireOp",EDGE,"E2243"),sQuery(id+"F0.wireOp",EDGE,"E2244"),sQuery(id+"F0.wireOp",EDGE,"E2245"),sQuery(id+"F0.wireOp",EDGE,"E2246"),sQuery(id+"F0.wireOp",EDGE,"E2247"),sQuery(id+"F0.wireOp",EDGE,"E2248"),sQuery(id+"F0.wireOp",EDGE,"E2249"),sQuery(id+"F0.wireOp",EDGE,"E2250"),sQuery(id+"F0.wireOp",EDGE,"E2251"),sQuery(id+"F0.wireOp",EDGE,"E2252"),sQuery(id+"F0.wireOp",EDGE,"E2253"),sQuery(id+"F0.wireOp",EDGE,"E2254"),sQuery(id+"F0.wireOp",EDGE,"E2255"),sQuery(id+"F0.wireOp",EDGE,"E2256"),sQuery(id+"F0.wireOp",EDGE,"E2257"),sQuery(id+"F0.wireOp",EDGE,"E2258"),sQuery(id+"F0.wireOp",EDGE,"E2259"),sQuery(id+"F0.wireOp",EDGE,"E2260"),sQuery(id+"F0.wireOp",EDGE,"E2261"),sQuery(id+"F0.wireOp",EDGE,"E2262"),sQuery(id+"F0.wireOp",EDGE,"E2263"),sQuery(id+"F0.wireOp",EDGE,"E2264"),sQuery(id+"F0.wireOp",EDGE,"E2265"),sQuery(id+"F0.wireOp",EDGE,"E2266"),sQuery(id+"F0.wireOp",EDGE,"E2267"),sQuery(id+"F0.wireOp",EDGE,"E2268"),sQuery(id+"F0.wireOp",EDGE,"E2269"),sQuery(id+"F0.wireOp",EDGE,"E2270"),sQuery(id+"F0.wireOp",EDGE,"E2271"),sQuery(id+"F0.wireOp",EDGE,"E2272"),sQuery(id+"F0.wireOp",EDGE,"E2273"),sQuery(id+"F0.wireOp",EDGE,"E2274"),sQuery(id+"F0.wireOp",EDGE,"E2275"),sQuery(id+"F0.wireOp",EDGE,"E2276"),sQuery(id+"F0.wireOp",EDGE,"E2277"),sQuery(id+"F0.wireOp",EDGE,"E2278"),sQuery(id+"F0.wireOp",EDGE,"E2279"),sQuery(id+"F0.wireOp",EDGE,"E2280"),sQuery(id+"F0.wireOp",EDGE,"E2281"),sQuery(id+"F0.wireOp",EDGE,"E2282"),sQuery(id+"F0.wireOp",EDGE,"E2283"),sQuery(id+"F0.wireOp",EDGE,"E2284"),sQuery(id+"F0.wireOp",EDGE,"E2285"),sQuery(id+"F0.wireOp",EDGE,"E2385")])],"isStart":false});
            var Q7;
            Q7=makeQuery(id+"F1.opExtrude","CAP_FACE",FACE,{"disambiguationData":[OSD([sQuery(id+"F0.wireOp",EDGE,"E2084"),sQuery(id+"F0.wireOp",EDGE,"E2085"),sQuery(id+"F0.wireOp",EDGE,"E2086"),sQuery(id+"F0.wireOp",EDGE,"E2087"),sQuery(id+"F0.wireOp",EDGE,"E2096"),sQuery(id+"F0.wireOp",EDGE,"E2097"),sQuery(id+"F0.wireOp",EDGE,"E2098"),sQuery(id+"F0.wireOp",EDGE,"E2099"),sQuery(id+"F0.wireOp",EDGE,"E2100"),sQuery(id+"F0.wireOp",EDGE,"E2101"),sQuery(id+"F0.wireOp",EDGE,"E2102"),sQuery(id+"F0.wireOp",EDGE,"E2103"),sQuery(id+"F0.wireOp",EDGE,"E2106"),sQuery(id+"F0.wireOp",EDGE,"E2108"),sQuery(id+"F0.wireOp",EDGE,"E2109"),sQuery(id+"F0.wireOp",EDGE,"E2110"),sQuery(id+"F0.wireOp",EDGE,"E2111"),sQuery(id+"F0.wireOp",EDGE,"E2112"),sQuery(id+"F0.wireOp",EDGE,"E2113"),sQuery(id+"F0.wireOp",EDGE,"E2114"),sQuery(id+"F0.wireOp",EDGE,"E2115"),sQuery(id+"F0.wireOp",EDGE,"E2116"),sQuery(id+"F0.wireOp",EDGE,"E2117"),sQuery(id+"F0.wireOp",EDGE,"E2118"),sQuery(id+"F0.wireOp",EDGE,"E2119"),sQuery(id+"F0.wireOp",EDGE,"E2120"),sQuery(id+"F0.wireOp",EDGE,"E2121"),sQuery(id+"F0.wireOp",EDGE,"E2122"),sQuery(id+"F0.wireOp",EDGE,"E2123"),sQuery(id+"F0.wireOp",EDGE,"E2124"),sQuery(id+"F0.wireOp",EDGE,"E2125"),sQuery(id+"F0.wireOp",EDGE,"E2126"),sQuery(id+"F0.wireOp",EDGE,"E2127"),sQuery(id+"F0.wireOp",EDGE,"E2128"),sQuery(id+"F0.wireOp",EDGE,"E2129"),sQuery(id+"F0.wireOp",EDGE,"E2130"),sQuery(id+"F0.wireOp",EDGE,"E2131"),sQuery(id+"F0.wireOp",EDGE,"E2132"),sQuery(id+"F0.wireOp",EDGE,"E2133"),sQuery(id+"F0.wireOp",EDGE,"E2134"),sQuery(id+"F0.wireOp",EDGE,"E2135"),sQuery(id+"F0.wireOp",EDGE,"E2136"),sQuery(id+"F0.wireOp",EDGE,"E2137"),sQuery(id+"F0.wireOp",EDGE,"E2138"),sQuery(id+"F0.wireOp",EDGE,"E2139"),sQuery(id+"F0.wireOp",EDGE,"E2140"),sQuery(id+"F0.wireOp",EDGE,"E2141"),sQuery(id+"F0.wireOp",EDGE,"E2142"),sQuery(id+"F0.wireOp",EDGE,"E2143"),sQuery(id+"F0.wireOp",EDGE,"E2144"),sQuery(id+"F0.wireOp",EDGE,"E2145"),sQuery(id+"F0.wireOp",EDGE,"E2146"),sQuery(id+"F0.wireOp",EDGE,"E2147"),sQuery(id+"F0.wireOp",EDGE,"E2148"),sQuery(id+"F0.wireOp",EDGE,"E2149"),sQuery(id+"F0.wireOp",EDGE,"E2150"),sQuery(id+"F0.wireOp",EDGE,"E2151"),sQuery(id+"F0.wireOp",EDGE,"E2152"),sQuery(id+"F0.wireOp",EDGE,"E2153"),sQuery(id+"F0.wireOp",EDGE,"E2154"),sQuery(id+"F0.wireOp",EDGE,"E2155"),sQuery(id+"F0.wireOp",EDGE,"E2156"),sQuery(id+"F0.wireOp",EDGE,"E2157"),sQuery(id+"F0.wireOp",EDGE,"E2158"),sQuery(id+"F0.wireOp",EDGE,"E2159"),sQuery(id+"F0.wireOp",EDGE,"E2160"),sQuery(id+"F0.wireOp",EDGE,"E2161"),sQuery(id+"F0.wireOp",EDGE,"E2162"),sQuery(id+"F0.wireOp",EDGE,"E2163"),sQuery(id+"F0.wireOp",EDGE,"E2164"),sQuery(id+"F0.wireOp",EDGE,"E2165"),sQuery(id+"F0.wireOp",EDGE,"E2166"),sQuery(id+"F0.wireOp",EDGE,"E2167"),sQuery(id+"F0.wireOp",EDGE,"E2168"),sQuery(id+"F0.wireOp",EDGE,"E2169"),sQuery(id+"F0.wireOp",EDGE,"E2170"),sQuery(id+"F0.wireOp",EDGE,"E2171"),sQuery(id+"F0.wireOp",EDGE,"E2172"),sQuery(id+"F0.wireOp",EDGE,"E2173"),sQuery(id+"F0.wireOp",EDGE,"E2174"),sQuery(id+"F0.wireOp",EDGE,"E2175"),sQuery(id+"F0.wireOp",EDGE,"E2176"),sQuery(id+"F0.wireOp",EDGE,"E2177"),sQuery(id+"F0.wireOp",EDGE,"E2178"),sQuery(id+"F0.wireOp",EDGE,"E2179"),sQuery(id+"F0.wireOp",EDGE,"E2180"),sQuery(id+"F0.wireOp",EDGE,"E2181"),sQuery(id+"F0.wireOp",EDGE,"E2182"),sQuery(id+"F0.wireOp",EDGE,"E2183"),sQuery(id+"F0.wireOp",EDGE,"E2184"),sQuery(id+"F0.wireOp",EDGE,"E2205")])],"isStart":false});
            var Q8;
            Q8=makeQuery(id+"F1.opExtrude","CAP_FACE",FACE,{"disambiguationData":[OSD([sQuery(id+"F0.wireOp",EDGE,"E1979"),sQuery(id+"F0.wireOp",EDGE,"E1980"),sQuery(id+"F0.wireOp",EDGE,"E1981"),sQuery(id+"F0.wireOp",EDGE,"E1982"),sQuery(id+"F0.wireOp",EDGE,"E1991"),sQuery(id+"F0.wireOp",EDGE,"E1992"),sQuery(id+"F0.wireOp",EDGE,"E1993"),sQuery(id+"F0.wireOp",EDGE,"E1994"),sQuery(id+"F0.wireOp",EDGE,"E1995"),sQuery(id+"F0.wireOp",EDGE,"E1996"),sQuery(id+"F0.wireOp",EDGE,"E1997"),sQuery(id+"F0.wireOp",EDGE,"E1998"),sQuery(id+"F0.wireOp",EDGE,"E2001"),sQuery(id+"F0.wireOp",EDGE,"E2003"),sQuery(id+"F0.wireOp",EDGE,"E2004"),sQuery(id+"F0.wireOp",EDGE,"E2005"),sQuery(id+"F0.wireOp",EDGE,"E2006"),sQuery(id+"F0.wireOp",EDGE,"E2007"),sQuery(id+"F0.wireOp",EDGE,"E2008"),sQuery(id+"F0.wireOp",EDGE,"E2009"),sQuery(id+"F0.wireOp",EDGE,"E2010"),sQuery(id+"F0.wireOp",EDGE,"E2011"),sQuery(id+"F0.wireOp",EDGE,"E2012"),sQuery(id+"F0.wireOp",EDGE,"E2013"),sQuery(id+"F0.wireOp",EDGE,"E2014"),sQuery(id+"F0.wireOp",EDGE,"E2015"),sQuery(id+"F0.wireOp",EDGE,"E2016"),sQuery(id+"F0.wireOp",EDGE,"E2017"),sQuery(id+"F0.wireOp",EDGE,"E2018"),sQuery(id+"F0.wireOp",EDGE,"E2019"),sQuery(id+"F0.wireOp",EDGE,"E2020"),sQuery(id+"F0.wireOp",EDGE,"E2021"),sQuery(id+"F0.wireOp",EDGE,"E2022"),sQuery(id+"F0.wireOp",EDGE,"E2023"),sQuery(id+"F0.wireOp",EDGE,"E2024"),sQuery(id+"F0.wireOp",EDGE,"E2025"),sQuery(id+"F0.wireOp",EDGE,"E2026"),sQuery(id+"F0.wireOp",EDGE,"E2027"),sQuery(id+"F0.wireOp",EDGE,"E2028"),sQuery(id+"F0.wireOp",EDGE,"E2029"),sQuery(id+"F0.wireOp",EDGE,"E2030"),sQuery(id+"F0.wireOp",EDGE,"E2031"),sQuery(id+"F0.wireOp",EDGE,"E2032"),sQuery(id+"F0.wireOp",EDGE,"E2033"),sQuery(id+"F0.wireOp",EDGE,"E2034"),sQuery(id+"F0.wireOp",EDGE,"E2035"),sQuery(id+"F0.wireOp",EDGE,"E2036"),sQuery(id+"F0.wireOp",EDGE,"E2037"),sQuery(id+"F0.wireOp",EDGE,"E2038"),sQuery(id+"F0.wireOp",EDGE,"E2039"),sQuery(id+"F0.wireOp",EDGE,"E2040"),sQuery(id+"F0.wireOp",EDGE,"E2041"),sQuery(id+"F0.wireOp",EDGE,"E2042"),sQuery(id+"F0.wireOp",EDGE,"E2043"),sQuery(id+"F0.wireOp",EDGE,"E2044"),sQuery(id+"F0.wireOp",EDGE,"E2045"),sQuery(id+"F0.wireOp",EDGE,"E2046"),sQuery(id+"F0.wireOp",EDGE,"E2047"),sQuery(id+"F0.wireOp",EDGE,"E2048"),sQuery(id+"F0.wireOp",EDGE,"E2049"),sQuery(id+"F0.wireOp",EDGE,"E2050"),sQuery(id+"F0.wireOp",EDGE,"E2051"),sQuery(id+"F0.wireOp",EDGE,"E2052"),sQuery(id+"F0.wireOp",EDGE,"E2053"),sQuery(id+"F0.wireOp",EDGE,"E2054"),sQuery(id+"F0.wireOp",EDGE,"E2055"),sQuery(id+"F0.wireOp",EDGE,"E2056"),sQuery(id+"F0.wireOp",EDGE,"E2057"),sQuery(id+"F0.wireOp",EDGE,"E2058"),sQuery(id+"F0.wireOp",EDGE,"E2059"),sQuery(id+"F0.wireOp",EDGE,"E2060"),sQuery(id+"F0.wireOp",EDGE,"E2061"),sQuery(id+"F0.wireOp",EDGE,"E2062"),sQuery(id+"F0.wireOp",EDGE,"E2063"),sQuery(id+"F0.wireOp",EDGE,"E2064"),sQuery(id+"F0.wireOp",EDGE,"E2065"),sQuery(id+"F0.wireOp",EDGE,"E2066"),sQuery(id+"F0.wireOp",EDGE,"E2067"),sQuery(id+"F0.wireOp",EDGE,"E2068"),sQuery(id+"F0.wireOp",EDGE,"E2069"),sQuery(id+"F0.wireOp",EDGE,"E2070"),sQuery(id+"F0.wireOp",EDGE,"E2071"),sQuery(id+"F0.wireOp",EDGE,"E2072"),sQuery(id+"F0.wireOp",EDGE,"E2073"),sQuery(id+"F0.wireOp",EDGE,"E2074"),sQuery(id+"F0.wireOp",EDGE,"E2075"),sQuery(id+"F0.wireOp",EDGE,"E2076"),sQuery(id+"F0.wireOp",EDGE,"E2077"),sQuery(id+"F0.wireOp",EDGE,"E2078"),sQuery(id+"F0.wireOp",EDGE,"E2079"),sQuery(id+"F0.wireOp",EDGE,"E2080"),sQuery(id+"F0.wireOp",EDGE,"E2104")])],"isStart":false});
            var Q9;
            Q9=makeQuery(id+"F1.opExtrude","CAP_FACE",FACE,{"disambiguationData":[OSD([sQuery(id+"F0.wireOp",EDGE,"E1874"),sQuery(id+"F0.wireOp",EDGE,"E1875"),sQuery(id+"F0.wireOp",EDGE,"E1876"),sQuery(id+"F0.wireOp",EDGE,"E1877"),sQuery(id+"F0.wireOp",EDGE,"E1886"),sQuery(id+"F0.wireOp",EDGE,"E1887"),sQuery(id+"F0.wireOp",EDGE,"E1888"),sQuery(id+"F0.wireOp",EDGE,"E1889"),sQuery(id+"F0.wireOp",EDGE,"E1890"),sQuery(id+"F0.wireOp",EDGE,"E1891"),sQuery(id+"F0.wireOp",EDGE,"E1892"),sQuery(id+"F0.wireOp",EDGE,"E1893"),sQuery(id+"F0.wireOp",EDGE,"E1896"),sQuery(id+"F0.wireOp",EDGE,"E1898"),sQuery(id+"F0.wireOp",EDGE,"E1899"),sQuery(id+"F0.wireOp",EDGE,"E1900"),sQuery(id+"F0.wireOp",EDGE,"E1901"),sQuery(id+"F0.wireOp",EDGE,"E1902"),sQuery(id+"F0.wireOp",EDGE,"E1903"),sQuery(id+"F0.wireOp",EDGE,"E1904"),sQuery(id+"F0.wireOp",EDGE,"E1905"),sQuery(id+"F0.wireOp",EDGE,"E1906"),sQuery(id+"F0.wireOp",EDGE,"E1907"),sQuery(id+"F0.wireOp",EDGE,"E1908"),sQuery(id+"F0.wireOp",EDGE,"E1909"),sQuery(id+"F0.wireOp",EDGE,"E1910"),sQuery(id+"F0.wireOp",EDGE,"E1911"),sQuery(id+"F0.wireOp",EDGE,"E1912"),sQuery(id+"F0.wireOp",EDGE,"E1913"),sQuery(id+"F0.wireOp",EDGE,"E1914"),sQuery(id+"F0.wireOp",EDGE,"E1915"),sQuery(id+"F0.wireOp",EDGE,"E1916"),sQuery(id+"F0.wireOp",EDGE,"E1917"),sQuery(id+"F0.wireOp",EDGE,"E1918"),sQuery(id+"F0.wireOp",EDGE,"E1919"),sQuery(id+"F0.wireOp",EDGE,"E1920"),sQuery(id+"F0.wireOp",EDGE,"E1921"),sQuery(id+"F0.wireOp",EDGE,"E1922"),sQuery(id+"F0.wireOp",EDGE,"E1923"),sQuery(id+"F0.wireOp",EDGE,"E1924"),sQuery(id+"F0.wireOp",EDGE,"E1925"),sQuery(id+"F0.wireOp",EDGE,"E1926"),sQuery(id+"F0.wireOp",EDGE,"E1927"),sQuery(id+"F0.wireOp",EDGE,"E1928"),sQuery(id+"F0.wireOp",EDGE,"E1929"),sQuery(id+"F0.wireOp",EDGE,"E1930"),sQuery(id+"F0.wireOp",EDGE,"E1931"),sQuery(id+"F0.wireOp",EDGE,"E1932"),sQuery(id+"F0.wireOp",EDGE,"E1933"),sQuery(id+"F0.wireOp",EDGE,"E1934"),sQuery(id+"F0.wireOp",EDGE,"E1935"),sQuery(id+"F0.wireOp",EDGE,"E1936"),sQuery(id+"F0.wireOp",EDGE,"E1937"),sQuery(id+"F0.wireOp",EDGE,"E1938"),sQuery(id+"F0.wireOp",EDGE,"E1939"),sQuery(id+"F0.wireOp",EDGE,"E1940"),sQuery(id+"F0.wireOp",EDGE,"E1941"),sQuery(id+"F0.wireOp",EDGE,"E1942"),sQuery(id+"F0.wireOp",EDGE,"E1943"),sQuery(id+"F0.wireOp",EDGE,"E1944"),sQuery(id+"F0.wireOp",EDGE,"E1945"),sQuery(id+"F0.wireOp",EDGE,"E1946"),sQuery(id+"F0.wireOp",EDGE,"E1947"),sQuery(id+"F0.wireOp",EDGE,"E1948"),sQuery(id+"F0.wireOp",EDGE,"E1949"),sQuery(id+"F0.wireOp",EDGE,"E1950"),sQuery(id+"F0.wireOp",EDGE,"E1951"),sQuery(id+"F0.wireOp",EDGE,"E1952"),sQuery(id+"F0.wireOp",EDGE,"E1953"),sQuery(id+"F0.wireOp",EDGE,"E1954"),sQuery(id+"F0.wireOp",EDGE,"E1955"),sQuery(id+"F0.wireOp",EDGE,"E1956"),sQuery(id+"F0.wireOp",EDGE,"E1957"),sQuery(id+"F0.wireOp",EDGE,"E1958"),sQuery(id+"F0.wireOp",EDGE,"E1959"),sQuery(id+"F0.wireOp",EDGE,"E1960"),sQuery(id+"F0.wireOp",EDGE,"E1961"),sQuery(id+"F0.wireOp",EDGE,"E1962"),sQuery(id+"F0.wireOp",EDGE,"E1963"),sQuery(id+"F0.wireOp",EDGE,"E1964"),sQuery(id+"F0.wireOp",EDGE,"E1965"),sQuery(id+"F0.wireOp",EDGE,"E1966"),sQuery(id+"F0.wireOp",EDGE,"E1967"),sQuery(id+"F0.wireOp",EDGE,"E1968"),sQuery(id+"F0.wireOp",EDGE,"E1969"),sQuery(id+"F0.wireOp",EDGE,"E1970"),sQuery(id+"F0.wireOp",EDGE,"E1971"),sQuery(id+"F0.wireOp",EDGE,"E1972"),sQuery(id+"F0.wireOp",EDGE,"E1973"),sQuery(id+"F0.wireOp",EDGE,"E1974"),sQuery(id+"F0.wireOp",EDGE,"E1975"),sQuery(id+"F0.wireOp",EDGE,"E2407")])],"isStart":false});
            var Q10;
            Q10=makeQuery(id+"F1.opExtrude","CAP_FACE",FACE,{"disambiguationData":[OSD([sQuery(id+"F0.wireOp",EDGE,"E1769"),sQuery(id+"F0.wireOp",EDGE,"E1770"),sQuery(id+"F0.wireOp",EDGE,"E1771"),sQuery(id+"F0.wireOp",EDGE,"E1772"),sQuery(id+"F0.wireOp",EDGE,"E1781"),sQuery(id+"F0.wireOp",EDGE,"E1782"),sQuery(id+"F0.wireOp",EDGE,"E1783"),sQuery(id+"F0.wireOp",EDGE,"E1784"),sQuery(id+"F0.wireOp",EDGE,"E1785"),sQuery(id+"F0.wireOp",EDGE,"E1786"),sQuery(id+"F0.wireOp",EDGE,"E1787"),sQuery(id+"F0.wireOp",EDGE,"E1788"),sQuery(id+"F0.wireOp",EDGE,"E1791"),sQuery(id+"F0.wireOp",EDGE,"E1793"),sQuery(id+"F0.wireOp",EDGE,"E1794"),sQuery(id+"F0.wireOp",EDGE,"E1795"),sQuery(id+"F0.wireOp",EDGE,"E1796"),sQuery(id+"F0.wireOp",EDGE,"E1797"),sQuery(id+"F0.wireOp",EDGE,"E1798"),sQuery(id+"F0.wireOp",EDGE,"E1799"),sQuery(id+"F0.wireOp",EDGE,"E1800"),sQuery(id+"F0.wireOp",EDGE,"E1801"),sQuery(id+"F0.wireOp",EDGE,"E1802"),sQuery(id+"F0.wireOp",EDGE,"E1803"),sQuery(id+"F0.wireOp",EDGE,"E1804"),sQuery(id+"F0.wireOp",EDGE,"E1805"),sQuery(id+"F0.wireOp",EDGE,"E1806"),sQuery(id+"F0.wireOp",EDGE,"E1807"),sQuery(id+"F0.wireOp",EDGE,"E1808"),sQuery(id+"F0.wireOp",EDGE,"E1809"),sQuery(id+"F0.wireOp",EDGE,"E1810"),sQuery(id+"F0.wireOp",EDGE,"E1811"),sQuery(id+"F0.wireOp",EDGE,"E1812"),sQuery(id+"F0.wireOp",EDGE,"E1813"),sQuery(id+"F0.wireOp",EDGE,"E1814"),sQuery(id+"F0.wireOp",EDGE,"E1815"),sQuery(id+"F0.wireOp",EDGE,"E1816"),sQuery(id+"F0.wireOp",EDGE,"E1817"),sQuery(id+"F0.wireOp",EDGE,"E1818"),sQuery(id+"F0.wireOp",EDGE,"E1819"),sQuery(id+"F0.wireOp",EDGE,"E1820"),sQuery(id+"F0.wireOp",EDGE,"E1821"),sQuery(id+"F0.wireOp",EDGE,"E1822"),sQuery(id+"F0.wireOp",EDGE,"E1823"),sQuery(id+"F0.wireOp",EDGE,"E1824"),sQuery(id+"F0.wireOp",EDGE,"E1825"),sQuery(id+"F0.wireOp",EDGE,"E1826"),sQuery(id+"F0.wireOp",EDGE,"E1827"),sQuery(id+"F0.wireOp",EDGE,"E1828"),sQuery(id+"F0.wireOp",EDGE,"E1829"),sQuery(id+"F0.wireOp",EDGE,"E1830"),sQuery(id+"F0.wireOp",EDGE,"E1831"),sQuery(id+"F0.wireOp",EDGE,"E1832"),sQuery(id+"F0.wireOp",EDGE,"E1833"),sQuery(id+"F0.wireOp",EDGE,"E1834"),sQuery(id+"F0.wireOp",EDGE,"E1835"),sQuery(id+"F0.wireOp",EDGE,"E1836"),sQuery(id+"F0.wireOp",EDGE,"E1837"),sQuery(id+"F0.wireOp",EDGE,"E1838"),sQuery(id+"F0.wireOp",EDGE,"E1839"),sQuery(id+"F0.wireOp",EDGE,"E1840"),sQuery(id+"F0.wireOp",EDGE,"E1841"),sQuery(id+"F0.wireOp",EDGE,"E1842"),sQuery(id+"F0.wireOp",EDGE,"E1843"),sQuery(id+"F0.wireOp",EDGE,"E1844"),sQuery(id+"F0.wireOp",EDGE,"E1845"),sQuery(id+"F0.wireOp",EDGE,"E1846"),sQuery(id+"F0.wireOp",EDGE,"E1847"),sQuery(id+"F0.wireOp",EDGE,"E1848"),sQuery(id+"F0.wireOp",EDGE,"E1849"),sQuery(id+"F0.wireOp",EDGE,"E1850"),sQuery(id+"F0.wireOp",EDGE,"E1851"),sQuery(id+"F0.wireOp",EDGE,"E1852"),sQuery(id+"F0.wireOp",EDGE,"E1853"),sQuery(id+"F0.wireOp",EDGE,"E1854"),sQuery(id+"F0.wireOp",EDGE,"E1855"),sQuery(id+"F0.wireOp",EDGE,"E1856"),sQuery(id+"F0.wireOp",EDGE,"E1857"),sQuery(id+"F0.wireOp",EDGE,"E1858"),sQuery(id+"F0.wireOp",EDGE,"E1859"),sQuery(id+"F0.wireOp",EDGE,"E1860"),sQuery(id+"F0.wireOp",EDGE,"E1861"),sQuery(id+"F0.wireOp",EDGE,"E1862"),sQuery(id+"F0.wireOp",EDGE,"E1863"),sQuery(id+"F0.wireOp",EDGE,"E1864"),sQuery(id+"F0.wireOp",EDGE,"E1865"),sQuery(id+"F0.wireOp",EDGE,"E1866"),sQuery(id+"F0.wireOp",EDGE,"E1867"),sQuery(id+"F0.wireOp",EDGE,"E1868"),sQuery(id+"F0.wireOp",EDGE,"E1869"),sQuery(id+"F0.wireOp",EDGE,"E1870"),sQuery(id+"F0.wireOp",EDGE,"E1894")])],"isStart":false});
            var Q11;
            Q11=makeQuery(id+"F1.opExtrude","CAP_FACE",FACE,{"disambiguationData":[OSD([sQuery(id+"F0.wireOp",EDGE,"E1664"),sQuery(id+"F0.wireOp",EDGE,"E1665"),sQuery(id+"F0.wireOp",EDGE,"E1666"),sQuery(id+"F0.wireOp",EDGE,"E1667"),sQuery(id+"F0.wireOp",EDGE,"E1676"),sQuery(id+"F0.wireOp",EDGE,"E1677"),sQuery(id+"F0.wireOp",EDGE,"E1678"),sQuery(id+"F0.wireOp",EDGE,"E1679"),sQuery(id+"F0.wireOp",EDGE,"E1680"),sQuery(id+"F0.wireOp",EDGE,"E1681"),sQuery(id+"F0.wireOp",EDGE,"E1682"),sQuery(id+"F0.wireOp",EDGE,"E1683"),sQuery(id+"F0.wireOp",EDGE,"E1686"),sQuery(id+"F0.wireOp",EDGE,"E1688"),sQuery(id+"F0.wireOp",EDGE,"E1689"),sQuery(id+"F0.wireOp",EDGE,"E1690"),sQuery(id+"F0.wireOp",EDGE,"E1691"),sQuery(id+"F0.wireOp",EDGE,"E1692"),sQuery(id+"F0.wireOp",EDGE,"E1693"),sQuery(id+"F0.wireOp",EDGE,"E1694"),sQuery(id+"F0.wireOp",EDGE,"E1695"),sQuery(id+"F0.wireOp",EDGE,"E1696"),sQuery(id+"F0.wireOp",EDGE,"E1697"),sQuery(id+"F0.wireOp",EDGE,"E1698"),sQuery(id+"F0.wireOp",EDGE,"E1699"),sQuery(id+"F0.wireOp",EDGE,"E1700"),sQuery(id+"F0.wireOp",EDGE,"E1701"),sQuery(id+"F0.wireOp",EDGE,"E1702"),sQuery(id+"F0.wireOp",EDGE,"E1703"),sQuery(id+"F0.wireOp",EDGE,"E1704"),sQuery(id+"F0.wireOp",EDGE,"E1705"),sQuery(id+"F0.wireOp",EDGE,"E1706"),sQuery(id+"F0.wireOp",EDGE,"E1707"),sQuery(id+"F0.wireOp",EDGE,"E1708"),sQuery(id+"F0.wireOp",EDGE,"E1709"),sQuery(id+"F0.wireOp",EDGE,"E1710"),sQuery(id+"F0.wireOp",EDGE,"E1711"),sQuery(id+"F0.wireOp",EDGE,"E1712"),sQuery(id+"F0.wireOp",EDGE,"E1713"),sQuery(id+"F0.wireOp",EDGE,"E1714"),sQuery(id+"F0.wireOp",EDGE,"E1715"),sQuery(id+"F0.wireOp",EDGE,"E1716"),sQuery(id+"F0.wireOp",EDGE,"E1717"),sQuery(id+"F0.wireOp",EDGE,"E1718"),sQuery(id+"F0.wireOp",EDGE,"E1719"),sQuery(id+"F0.wireOp",EDGE,"E1720"),sQuery(id+"F0.wireOp",EDGE,"E1721"),sQuery(id+"F0.wireOp",EDGE,"E1722"),sQuery(id+"F0.wireOp",EDGE,"E1723"),sQuery(id+"F0.wireOp",EDGE,"E1724"),sQuery(id+"F0.wireOp",EDGE,"E1725"),sQuery(id+"F0.wireOp",EDGE,"E1726"),sQuery(id+"F0.wireOp",EDGE,"E1727"),sQuery(id+"F0.wireOp",EDGE,"E1728"),sQuery(id+"F0.wireOp",EDGE,"E1729"),sQuery(id+"F0.wireOp",EDGE,"E1730"),sQuery(id+"F0.wireOp",EDGE,"E1731"),sQuery(id+"F0.wireOp",EDGE,"E1732"),sQuery(id+"F0.wireOp",EDGE,"E1733"),sQuery(id+"F0.wireOp",EDGE,"E1734"),sQuery(id+"F0.wireOp",EDGE,"E1735"),sQuery(id+"F0.wireOp",EDGE,"E1736"),sQuery(id+"F0.wireOp",EDGE,"E1737"),sQuery(id+"F0.wireOp",EDGE,"E1738"),sQuery(id+"F0.wireOp",EDGE,"E1739"),sQuery(id+"F0.wireOp",EDGE,"E1740"),sQuery(id+"F0.wireOp",EDGE,"E1741"),sQuery(id+"F0.wireOp",EDGE,"E1742"),sQuery(id+"F0.wireOp",EDGE,"E1743"),sQuery(id+"F0.wireOp",EDGE,"E1744"),sQuery(id+"F0.wireOp",EDGE,"E1745"),sQuery(id+"F0.wireOp",EDGE,"E1746"),sQuery(id+"F0.wireOp",EDGE,"E1747"),sQuery(id+"F0.wireOp",EDGE,"E1748"),sQuery(id+"F0.wireOp",EDGE,"E1749"),sQuery(id+"F0.wireOp",EDGE,"E1750"),sQuery(id+"F0.wireOp",EDGE,"E1751"),sQuery(id+"F0.wireOp",EDGE,"E1752"),sQuery(id+"F0.wireOp",EDGE,"E1753"),sQuery(id+"F0.wireOp",EDGE,"E1754"),sQuery(id+"F0.wireOp",EDGE,"E1755"),sQuery(id+"F0.wireOp",EDGE,"E1756"),sQuery(id+"F0.wireOp",EDGE,"E1757"),sQuery(id+"F0.wireOp",EDGE,"E1758"),sQuery(id+"F0.wireOp",EDGE,"E1759"),sQuery(id+"F0.wireOp",EDGE,"E1760"),sQuery(id+"F0.wireOp",EDGE,"E1761"),sQuery(id+"F0.wireOp",EDGE,"E1762"),sQuery(id+"F0.wireOp",EDGE,"E1763"),sQuery(id+"F0.wireOp",EDGE,"E1764"),sQuery(id+"F0.wireOp",EDGE,"E1765"),sQuery(id+"F0.wireOp",EDGE,"E1789")])],"isStart":false});
            var Q12;
            Q12=makeQuery(id+"F1.opExtrude","CAP_FACE",FACE,{"disambiguationData":[OSD([sQuery(id+"F0.wireOp",EDGE,"E1555"),sQuery(id+"F0.wireOp",EDGE,"E1556"),sQuery(id+"F0.wireOp",EDGE,"E1557"),sQuery(id+"F0.wireOp",EDGE,"E1558"),sQuery(id+"F0.wireOp",EDGE,"E1567"),sQuery(id+"F0.wireOp",EDGE,"E1568"),sQuery(id+"F0.wireOp",EDGE,"E1569"),sQuery(id+"F0.wireOp",EDGE,"E1570"),sQuery(id+"F0.wireOp",EDGE,"E1571"),sQuery(id+"F0.wireOp",EDGE,"E1572"),sQuery(id+"F0.wireOp",EDGE,"E1573"),sQuery(id+"F0.wireOp",EDGE,"E1574"),sQuery(id+"F0.wireOp",EDGE,"E1577"),sQuery(id+"F0.wireOp",EDGE,"E1581"),sQuery(id+"F0.wireOp",EDGE,"E1583"),sQuery(id+"F0.wireOp",EDGE,"E1584"),sQuery(id+"F0.wireOp",EDGE,"E1585"),sQuery(id+"F0.wireOp",EDGE,"E1586"),sQuery(id+"F0.wireOp",EDGE,"E1587"),sQuery(id+"F0.wireOp",EDGE,"E1588"),sQuery(id+"F0.wireOp",EDGE,"E1589"),sQuery(id+"F0.wireOp",EDGE,"E1590"),sQuery(id+"F0.wireOp",EDGE,"E1591"),sQuery(id+"F0.wireOp",EDGE,"E1592"),sQuery(id+"F0.wireOp",EDGE,"E1593"),sQuery(id+"F0.wireOp",EDGE,"E1594"),sQuery(id+"F0.wireOp",EDGE,"E1595"),sQuery(id+"F0.wireOp",EDGE,"E1596"),sQuery(id+"F0.wireOp",EDGE,"E1597"),sQuery(id+"F0.wireOp",EDGE,"E1598"),sQuery(id+"F0.wireOp",EDGE,"E1599"),sQuery(id+"F0.wireOp",EDGE,"E1600"),sQuery(id+"F0.wireOp",EDGE,"E1601"),sQuery(id+"F0.wireOp",EDGE,"E1602"),sQuery(id+"F0.wireOp",EDGE,"E1603"),sQuery(id+"F0.wireOp",EDGE,"E1604"),sQuery(id+"F0.wireOp",EDGE,"E1605"),sQuery(id+"F0.wireOp",EDGE,"E1606"),sQuery(id+"F0.wireOp",EDGE,"E1607"),sQuery(id+"F0.wireOp",EDGE,"E1608"),sQuery(id+"F0.wireOp",EDGE,"E1609"),sQuery(id+"F0.wireOp",EDGE,"E1610"),sQuery(id+"F0.wireOp",EDGE,"E1611"),sQuery(id+"F0.wireOp",EDGE,"E1612"),sQuery(id+"F0.wireOp",EDGE,"E1613"),sQuery(id+"F0.wireOp",EDGE,"E1614"),sQuery(id+"F0.wireOp",EDGE,"E1615"),sQuery(id+"F0.wireOp",EDGE,"E1616"),sQuery(id+"F0.wireOp",EDGE,"E1617"),sQuery(id+"F0.wireOp",EDGE,"E1618"),sQuery(id+"F0.wireOp",EDGE,"E1619"),sQuery(id+"F0.wireOp",EDGE,"E1620"),sQuery(id+"F0.wireOp",EDGE,"E1621"),sQuery(id+"F0.wireOp",EDGE,"E1622"),sQuery(id+"F0.wireOp",EDGE,"E1623"),sQuery(id+"F0.wireOp",EDGE,"E1624"),sQuery(id+"F0.wireOp",EDGE,"E1625"),sQuery(id+"F0.wireOp",EDGE,"E1626"),sQuery(id+"F0.wireOp",EDGE,"E1627"),sQuery(id+"F0.wireOp",EDGE,"E1628"),sQuery(id+"F0.wireOp",EDGE,"E1629"),sQuery(id+"F0.wireOp",EDGE,"E1630"),sQuery(id+"F0.wireOp",EDGE,"E1631"),sQuery(id+"F0.wireOp",EDGE,"E1632"),sQuery(id+"F0.wireOp",EDGE,"E1633"),sQuery(id+"F0.wireOp",EDGE,"E1634"),sQuery(id+"F0.wireOp",EDGE,"E1635"),sQuery(id+"F0.wireOp",EDGE,"E1636"),sQuery(id+"F0.wireOp",EDGE,"E1637"),sQuery(id+"F0.wireOp",EDGE,"E1638"),sQuery(id+"F0.wireOp",EDGE,"E1639"),sQuery(id+"F0.wireOp",EDGE,"E1640"),sQuery(id+"F0.wireOp",EDGE,"E1641"),sQuery(id+"F0.wireOp",EDGE,"E1642"),sQuery(id+"F0.wireOp",EDGE,"E1643"),sQuery(id+"F0.wireOp",EDGE,"E1644"),sQuery(id+"F0.wireOp",EDGE,"E1645"),sQuery(id+"F0.wireOp",EDGE,"E1646"),sQuery(id+"F0.wireOp",EDGE,"E1647"),sQuery(id+"F0.wireOp",EDGE,"E1648"),sQuery(id+"F0.wireOp",EDGE,"E1649"),sQuery(id+"F0.wireOp",EDGE,"E1650"),sQuery(id+"F0.wireOp",EDGE,"E1651"),sQuery(id+"F0.wireOp",EDGE,"E1652"),sQuery(id+"F0.wireOp",EDGE,"E1653"),sQuery(id+"F0.wireOp",EDGE,"E1654"),sQuery(id+"F0.wireOp",EDGE,"E1655"),sQuery(id+"F0.wireOp",EDGE,"E1656"),sQuery(id+"F0.wireOp",EDGE,"E1657"),sQuery(id+"F0.wireOp",EDGE,"E1658"),sQuery(id+"F0.wireOp",EDGE,"E1659"),sQuery(id+"F0.wireOp",EDGE,"E1660"),sQuery(id+"F0.wireOp",EDGE,"E1684")])],"isStart":false});
            var Q13;
            Q13=makeQuery(id+"F1.opExtrude","CAP_FACE",FACE,{"disambiguationData":[OSD([sQuery(id+"F0.wireOp",EDGE,"E1454"),sQuery(id+"F0.wireOp",EDGE,"E1455"),sQuery(id+"F0.wireOp",EDGE,"E1456"),sQuery(id+"F0.wireOp",EDGE,"E1457"),sQuery(id+"F0.wireOp",EDGE,"E1466"),sQuery(id+"F0.wireOp",EDGE,"E1467"),sQuery(id+"F0.wireOp",EDGE,"E1468"),sQuery(id+"F0.wireOp",EDGE,"E1469"),sQuery(id+"F0.wireOp",EDGE,"E1470"),sQuery(id+"F0.wireOp",EDGE,"E1471"),sQuery(id+"F0.wireOp",EDGE,"E1472"),sQuery(id+"F0.wireOp",EDGE,"E1473"),sQuery(id+"F0.wireOp",EDGE,"E1474"),sQuery(id+"F0.wireOp",EDGE,"E1475"),sQuery(id+"F0.wireOp",EDGE,"E1476"),sQuery(id+"F0.wireOp",EDGE,"E1477"),sQuery(id+"F0.wireOp",EDGE,"E1478"),sQuery(id+"F0.wireOp",EDGE,"E1479"),sQuery(id+"F0.wireOp",EDGE,"E1480"),sQuery(id+"F0.wireOp",EDGE,"E1481"),sQuery(id+"F0.wireOp",EDGE,"E1482"),sQuery(id+"F0.wireOp",EDGE,"E1483"),sQuery(id+"F0.wireOp",EDGE,"E1484"),sQuery(id+"F0.wireOp",EDGE,"E1485"),sQuery(id+"F0.wireOp",EDGE,"E1486"),sQuery(id+"F0.wireOp",EDGE,"E1487"),sQuery(id+"F0.wireOp",EDGE,"E1488"),sQuery(id+"F0.wireOp",EDGE,"E1489"),sQuery(id+"F0.wireOp",EDGE,"E1490"),sQuery(id+"F0.wireOp",EDGE,"E1491"),sQuery(id+"F0.wireOp",EDGE,"E1492"),sQuery(id+"F0.wireOp",EDGE,"E1493"),sQuery(id+"F0.wireOp",EDGE,"E1494"),sQuery(id+"F0.wireOp",EDGE,"E1495"),sQuery(id+"F0.wireOp",EDGE,"E1496"),sQuery(id+"F0.wireOp",EDGE,"E1497"),sQuery(id+"F0.wireOp",EDGE,"E1498"),sQuery(id+"F0.wireOp",EDGE,"E1499"),sQuery(id+"F0.wireOp",EDGE,"E1500"),sQuery(id+"F0.wireOp",EDGE,"E1501"),sQuery(id+"F0.wireOp",EDGE,"E1502"),sQuery(id+"F0.wireOp",EDGE,"E1503"),sQuery(id+"F0.wireOp",EDGE,"E1504"),sQuery(id+"F0.wireOp",EDGE,"E1505"),sQuery(id+"F0.wireOp",EDGE,"E1506"),sQuery(id+"F0.wireOp",EDGE,"E1507"),sQuery(id+"F0.wireOp",EDGE,"E1508"),sQuery(id+"F0.wireOp",EDGE,"E1509"),sQuery(id+"F0.wireOp",EDGE,"E1510"),sQuery(id+"F0.wireOp",EDGE,"E1511"),sQuery(id+"F0.wireOp",EDGE,"E1512"),sQuery(id+"F0.wireOp",EDGE,"E1513"),sQuery(id+"F0.wireOp",EDGE,"E1514"),sQuery(id+"F0.wireOp",EDGE,"E1515"),sQuery(id+"F0.wireOp",EDGE,"E1516"),sQuery(id+"F0.wireOp",EDGE,"E1517"),sQuery(id+"F0.wireOp",EDGE,"E1518"),sQuery(id+"F0.wireOp",EDGE,"E1519"),sQuery(id+"F0.wireOp",EDGE,"E1520"),sQuery(id+"F0.wireOp",EDGE,"E1521"),sQuery(id+"F0.wireOp",EDGE,"E1522"),sQuery(id+"F0.wireOp",EDGE,"E1523"),sQuery(id+"F0.wireOp",EDGE,"E1524"),sQuery(id+"F0.wireOp",EDGE,"E1525"),sQuery(id+"F0.wireOp",EDGE,"E1526"),sQuery(id+"F0.wireOp",EDGE,"E1527"),sQuery(id+"F0.wireOp",EDGE,"E1528"),sQuery(id+"F0.wireOp",EDGE,"E1529"),sQuery(id+"F0.wireOp",EDGE,"E1530"),sQuery(id+"F0.wireOp",EDGE,"E1531"),sQuery(id+"F0.wireOp",EDGE,"E1532"),sQuery(id+"F0.wireOp",EDGE,"E1533"),sQuery(id+"F0.wireOp",EDGE,"E1534"),sQuery(id+"F0.wireOp",EDGE,"E1535"),sQuery(id+"F0.wireOp",EDGE,"E1536"),sQuery(id+"F0.wireOp",EDGE,"E1537"),sQuery(id+"F0.wireOp",EDGE,"E1538"),sQuery(id+"F0.wireOp",EDGE,"E1539"),sQuery(id+"F0.wireOp",EDGE,"E1540"),sQuery(id+"F0.wireOp",EDGE,"E1541"),sQuery(id+"F0.wireOp",EDGE,"E1542"),sQuery(id+"F0.wireOp",EDGE,"E1543"),sQuery(id+"F0.wireOp",EDGE,"E1544"),sQuery(id+"F0.wireOp",EDGE,"E1545"),sQuery(id+"F0.wireOp",EDGE,"E1546"),sQuery(id+"F0.wireOp",EDGE,"E1547"),sQuery(id+"F0.wireOp",EDGE,"E1548"),sQuery(id+"F0.wireOp",EDGE,"E1549"),sQuery(id+"F0.wireOp",EDGE,"E1550"),sQuery(id+"F0.wireOp",EDGE,"E1551"),sQuery(id+"F0.wireOp",EDGE,"E1579")])],"isStart":false});
            var Q14;
            Q14=makeQuery(id+"F1.opExtrude","CAP_FACE",FACE,{"disambiguationData":[OSD([sQuery(id+"F0.wireOp",EDGE,"E1349"),sQuery(id+"F0.wireOp",EDGE,"E1350"),sQuery(id+"F0.wireOp",EDGE,"E1351"),sQuery(id+"F0.wireOp",EDGE,"E1352"),sQuery(id+"F0.wireOp",EDGE,"E1361"),sQuery(id+"F0.wireOp",EDGE,"E1362"),sQuery(id+"F0.wireOp",EDGE,"E1363"),sQuery(id+"F0.wireOp",EDGE,"E1364"),sQuery(id+"F0.wireOp",EDGE,"E1365"),sQuery(id+"F0.wireOp",EDGE,"E1366"),sQuery(id+"F0.wireOp",EDGE,"E1367"),sQuery(id+"F0.wireOp",EDGE,"E1368"),sQuery(id+"F0.wireOp",EDGE,"E1371"),sQuery(id+"F0.wireOp",EDGE,"E1373"),sQuery(id+"F0.wireOp",EDGE,"E1374"),sQuery(id+"F0.wireOp",EDGE,"E1375"),sQuery(id+"F0.wireOp",EDGE,"E1376"),sQuery(id+"F0.wireOp",EDGE,"E1377"),sQuery(id+"F0.wireOp",EDGE,"E1378"),sQuery(id+"F0.wireOp",EDGE,"E1379"),sQuery(id+"F0.wireOp",EDGE,"E1380"),sQuery(id+"F0.wireOp",EDGE,"E1381"),sQuery(id+"F0.wireOp",EDGE,"E1382"),sQuery(id+"F0.wireOp",EDGE,"E1383"),sQuery(id+"F0.wireOp",EDGE,"E1384"),sQuery(id+"F0.wireOp",EDGE,"E1385"),sQuery(id+"F0.wireOp",EDGE,"E1386"),sQuery(id+"F0.wireOp",EDGE,"E1387"),sQuery(id+"F0.wireOp",EDGE,"E1388"),sQuery(id+"F0.wireOp",EDGE,"E1389"),sQuery(id+"F0.wireOp",EDGE,"E1390"),sQuery(id+"F0.wireOp",EDGE,"E1391"),sQuery(id+"F0.wireOp",EDGE,"E1392"),sQuery(id+"F0.wireOp",EDGE,"E1393"),sQuery(id+"F0.wireOp",EDGE,"E1394"),sQuery(id+"F0.wireOp",EDGE,"E1395"),sQuery(id+"F0.wireOp",EDGE,"E1396"),sQuery(id+"F0.wireOp",EDGE,"E1397"),sQuery(id+"F0.wireOp",EDGE,"E1398"),sQuery(id+"F0.wireOp",EDGE,"E1399"),sQuery(id+"F0.wireOp",EDGE,"E1400"),sQuery(id+"F0.wireOp",EDGE,"E1401"),sQuery(id+"F0.wireOp",EDGE,"E1402"),sQuery(id+"F0.wireOp",EDGE,"E1403"),sQuery(id+"F0.wireOp",EDGE,"E1404"),sQuery(id+"F0.wireOp",EDGE,"E1405"),sQuery(id+"F0.wireOp",EDGE,"E1406"),sQuery(id+"F0.wireOp",EDGE,"E1407"),sQuery(id+"F0.wireOp",EDGE,"E1408"),sQuery(id+"F0.wireOp",EDGE,"E1409"),sQuery(id+"F0.wireOp",EDGE,"E1410"),sQuery(id+"F0.wireOp",EDGE,"E1411"),sQuery(id+"F0.wireOp",EDGE,"E1412"),sQuery(id+"F0.wireOp",EDGE,"E1413"),sQuery(id+"F0.wireOp",EDGE,"E1414"),sQuery(id+"F0.wireOp",EDGE,"E1415"),sQuery(id+"F0.wireOp",EDGE,"E1416"),sQuery(id+"F0.wireOp",EDGE,"E1417"),sQuery(id+"F0.wireOp",EDGE,"E1418"),sQuery(id+"F0.wireOp",EDGE,"E1419"),sQuery(id+"F0.wireOp",EDGE,"E1420"),sQuery(id+"F0.wireOp",EDGE,"E1421"),sQuery(id+"F0.wireOp",EDGE,"E1422"),sQuery(id+"F0.wireOp",EDGE,"E1423"),sQuery(id+"F0.wireOp",EDGE,"E1424"),sQuery(id+"F0.wireOp",EDGE,"E1425"),sQuery(id+"F0.wireOp",EDGE,"E1426"),sQuery(id+"F0.wireOp",EDGE,"E1427"),sQuery(id+"F0.wireOp",EDGE,"E1428"),sQuery(id+"F0.wireOp",EDGE,"E1429"),sQuery(id+"F0.wireOp",EDGE,"E1430"),sQuery(id+"F0.wireOp",EDGE,"E1431"),sQuery(id+"F0.wireOp",EDGE,"E1432"),sQuery(id+"F0.wireOp",EDGE,"E1433"),sQuery(id+"F0.wireOp",EDGE,"E1434"),sQuery(id+"F0.wireOp",EDGE,"E1435"),sQuery(id+"F0.wireOp",EDGE,"E1436"),sQuery(id+"F0.wireOp",EDGE,"E1437"),sQuery(id+"F0.wireOp",EDGE,"E1438"),sQuery(id+"F0.wireOp",EDGE,"E1439"),sQuery(id+"F0.wireOp",EDGE,"E1440"),sQuery(id+"F0.wireOp",EDGE,"E1441"),sQuery(id+"F0.wireOp",EDGE,"E1442"),sQuery(id+"F0.wireOp",EDGE,"E1443"),sQuery(id+"F0.wireOp",EDGE,"E1444"),sQuery(id+"F0.wireOp",EDGE,"E1445"),sQuery(id+"F0.wireOp",EDGE,"E1446"),sQuery(id+"F0.wireOp",EDGE,"E1447"),sQuery(id+"F0.wireOp",EDGE,"E1448"),sQuery(id+"F0.wireOp",EDGE,"E1449"),sQuery(id+"F0.wireOp",EDGE,"E1450")])],"isStart":false});
            var Q15;
            Q15=makeQuery(id+"F1.opExtrude","CAP_FACE",FACE,{"disambiguationData":[OSD([sQuery(id+"F0.wireOp",EDGE,"E1244"),sQuery(id+"F0.wireOp",EDGE,"E1245"),sQuery(id+"F0.wireOp",EDGE,"E1246"),sQuery(id+"F0.wireOp",EDGE,"E1247"),sQuery(id+"F0.wireOp",EDGE,"E1256"),sQuery(id+"F0.wireOp",EDGE,"E1257"),sQuery(id+"F0.wireOp",EDGE,"E1258"),sQuery(id+"F0.wireOp",EDGE,"E1259"),sQuery(id+"F0.wireOp",EDGE,"E1260"),sQuery(id+"F0.wireOp",EDGE,"E1261"),sQuery(id+"F0.wireOp",EDGE,"E1262"),sQuery(id+"F0.wireOp",EDGE,"E1263"),sQuery(id+"F0.wireOp",EDGE,"E1266"),sQuery(id+"F0.wireOp",EDGE,"E1268"),sQuery(id+"F0.wireOp",EDGE,"E1269"),sQuery(id+"F0.wireOp",EDGE,"E1270"),sQuery(id+"F0.wireOp",EDGE,"E1271"),sQuery(id+"F0.wireOp",EDGE,"E1272"),sQuery(id+"F0.wireOp",EDGE,"E1273"),sQuery(id+"F0.wireOp",EDGE,"E1274"),sQuery(id+"F0.wireOp",EDGE,"E1275"),sQuery(id+"F0.wireOp",EDGE,"E1276"),sQuery(id+"F0.wireOp",EDGE,"E1277"),sQuery(id+"F0.wireOp",EDGE,"E1278"),sQuery(id+"F0.wireOp",EDGE,"E1279"),sQuery(id+"F0.wireOp",EDGE,"E1280"),sQuery(id+"F0.wireOp",EDGE,"E1281"),sQuery(id+"F0.wireOp",EDGE,"E1282"),sQuery(id+"F0.wireOp",EDGE,"E1283"),sQuery(id+"F0.wireOp",EDGE,"E1284"),sQuery(id+"F0.wireOp",EDGE,"E1285"),sQuery(id+"F0.wireOp",EDGE,"E1286"),sQuery(id+"F0.wireOp",EDGE,"E1287"),sQuery(id+"F0.wireOp",EDGE,"E1288"),sQuery(id+"F0.wireOp",EDGE,"E1289"),sQuery(id+"F0.wireOp",EDGE,"E1290"),sQuery(id+"F0.wireOp",EDGE,"E1291"),sQuery(id+"F0.wireOp",EDGE,"E1292"),sQuery(id+"F0.wireOp",EDGE,"E1293"),sQuery(id+"F0.wireOp",EDGE,"E1294"),sQuery(id+"F0.wireOp",EDGE,"E1295"),sQuery(id+"F0.wireOp",EDGE,"E1296"),sQuery(id+"F0.wireOp",EDGE,"E1297"),sQuery(id+"F0.wireOp",EDGE,"E1298"),sQuery(id+"F0.wireOp",EDGE,"E1299"),sQuery(id+"F0.wireOp",EDGE,"E1300"),sQuery(id+"F0.wireOp",EDGE,"E1301"),sQuery(id+"F0.wireOp",EDGE,"E1302"),sQuery(id+"F0.wireOp",EDGE,"E1303"),sQuery(id+"F0.wireOp",EDGE,"E1304"),sQuery(id+"F0.wireOp",EDGE,"E1305"),sQuery(id+"F0.wireOp",EDGE,"E1306"),sQuery(id+"F0.wireOp",EDGE,"E1307"),sQuery(id+"F0.wireOp",EDGE,"E1308"),sQuery(id+"F0.wireOp",EDGE,"E1309"),sQuery(id+"F0.wireOp",EDGE,"E1310"),sQuery(id+"F0.wireOp",EDGE,"E1311"),sQuery(id+"F0.wireOp",EDGE,"E1312"),sQuery(id+"F0.wireOp",EDGE,"E1313"),sQuery(id+"F0.wireOp",EDGE,"E1314"),sQuery(id+"F0.wireOp",EDGE,"E1315"),sQuery(id+"F0.wireOp",EDGE,"E1316"),sQuery(id+"F0.wireOp",EDGE,"E1317"),sQuery(id+"F0.wireOp",EDGE,"E1318"),sQuery(id+"F0.wireOp",EDGE,"E1319"),sQuery(id+"F0.wireOp",EDGE,"E1320"),sQuery(id+"F0.wireOp",EDGE,"E1321"),sQuery(id+"F0.wireOp",EDGE,"E1322"),sQuery(id+"F0.wireOp",EDGE,"E1323"),sQuery(id+"F0.wireOp",EDGE,"E1324"),sQuery(id+"F0.wireOp",EDGE,"E1325"),sQuery(id+"F0.wireOp",EDGE,"E1326"),sQuery(id+"F0.wireOp",EDGE,"E1327"),sQuery(id+"F0.wireOp",EDGE,"E1328"),sQuery(id+"F0.wireOp",EDGE,"E1329"),sQuery(id+"F0.wireOp",EDGE,"E1330"),sQuery(id+"F0.wireOp",EDGE,"E1331"),sQuery(id+"F0.wireOp",EDGE,"E1332"),sQuery(id+"F0.wireOp",EDGE,"E1333"),sQuery(id+"F0.wireOp",EDGE,"E1334"),sQuery(id+"F0.wireOp",EDGE,"E1335"),sQuery(id+"F0.wireOp",EDGE,"E1336"),sQuery(id+"F0.wireOp",EDGE,"E1337"),sQuery(id+"F0.wireOp",EDGE,"E1338"),sQuery(id+"F0.wireOp",EDGE,"E1339"),sQuery(id+"F0.wireOp",EDGE,"E1340"),sQuery(id+"F0.wireOp",EDGE,"E1341"),sQuery(id+"F0.wireOp",EDGE,"E1342"),sQuery(id+"F0.wireOp",EDGE,"E1343"),sQuery(id+"F0.wireOp",EDGE,"E1344"),sQuery(id+"F0.wireOp",EDGE,"E1345"),sQuery(id+"F0.wireOp",EDGE,"E1575")])],"isStart":false});
            var Q16;
            Q16=makeQuery(id+"F1.opExtrude","CAP_FACE",FACE,{"disambiguationData":[OSD([sQuery(id+"F0.wireOp",EDGE,"E1143"),sQuery(id+"F0.wireOp",EDGE,"E1144"),sQuery(id+"F0.wireOp",EDGE,"E1145"),sQuery(id+"F0.wireOp",EDGE,"E1146"),sQuery(id+"F0.wireOp",EDGE,"E1155"),sQuery(id+"F0.wireOp",EDGE,"E1156"),sQuery(id+"F0.wireOp",EDGE,"E1157"),sQuery(id+"F0.wireOp",EDGE,"E1158"),sQuery(id+"F0.wireOp",EDGE,"E1159"),sQuery(id+"F0.wireOp",EDGE,"E1160"),sQuery(id+"F0.wireOp",EDGE,"E1161"),sQuery(id+"F0.wireOp",EDGE,"E1162"),sQuery(id+"F0.wireOp",EDGE,"E1163"),sQuery(id+"F0.wireOp",EDGE,"E1164"),sQuery(id+"F0.wireOp",EDGE,"E1165"),sQuery(id+"F0.wireOp",EDGE,"E1166"),sQuery(id+"F0.wireOp",EDGE,"E1167"),sQuery(id+"F0.wireOp",EDGE,"E1168"),sQuery(id+"F0.wireOp",EDGE,"E1169"),sQuery(id+"F0.wireOp",EDGE,"E1170"),sQuery(id+"F0.wireOp",EDGE,"E1171"),sQuery(id+"F0.wireOp",EDGE,"E1172"),sQuery(id+"F0.wireOp",EDGE,"E1173"),sQuery(id+"F0.wireOp",EDGE,"E1174"),sQuery(id+"F0.wireOp",EDGE,"E1175"),sQuery(id+"F0.wireOp",EDGE,"E1176"),sQuery(id+"F0.wireOp",EDGE,"E1177"),sQuery(id+"F0.wireOp",EDGE,"E1178"),sQuery(id+"F0.wireOp",EDGE,"E1179"),sQuery(id+"F0.wireOp",EDGE,"E1180"),sQuery(id+"F0.wireOp",EDGE,"E1181"),sQuery(id+"F0.wireOp",EDGE,"E1182"),sQuery(id+"F0.wireOp",EDGE,"E1183"),sQuery(id+"F0.wireOp",EDGE,"E1184"),sQuery(id+"F0.wireOp",EDGE,"E1185"),sQuery(id+"F0.wireOp",EDGE,"E1186"),sQuery(id+"F0.wireOp",EDGE,"E1187"),sQuery(id+"F0.wireOp",EDGE,"E1188"),sQuery(id+"F0.wireOp",EDGE,"E1189"),sQuery(id+"F0.wireOp",EDGE,"E1190"),sQuery(id+"F0.wireOp",EDGE,"E1191"),sQuery(id+"F0.wireOp",EDGE,"E1192"),sQuery(id+"F0.wireOp",EDGE,"E1193"),sQuery(id+"F0.wireOp",EDGE,"E1194"),sQuery(id+"F0.wireOp",EDGE,"E1195"),sQuery(id+"F0.wireOp",EDGE,"E1196"),sQuery(id+"F0.wireOp",EDGE,"E1197"),sQuery(id+"F0.wireOp",EDGE,"E1198"),sQuery(id+"F0.wireOp",EDGE,"E1199"),sQuery(id+"F0.wireOp",EDGE,"E1200"),sQuery(id+"F0.wireOp",EDGE,"E1201"),sQuery(id+"F0.wireOp",EDGE,"E1202"),sQuery(id+"F0.wireOp",EDGE,"E1203"),sQuery(id+"F0.wireOp",EDGE,"E1204"),sQuery(id+"F0.wireOp",EDGE,"E1205"),sQuery(id+"F0.wireOp",EDGE,"E1206"),sQuery(id+"F0.wireOp",EDGE,"E1207"),sQuery(id+"F0.wireOp",EDGE,"E1208"),sQuery(id+"F0.wireOp",EDGE,"E1209"),sQuery(id+"F0.wireOp",EDGE,"E1210"),sQuery(id+"F0.wireOp",EDGE,"E1211"),sQuery(id+"F0.wireOp",EDGE,"E1212"),sQuery(id+"F0.wireOp",EDGE,"E1213"),sQuery(id+"F0.wireOp",EDGE,"E1214"),sQuery(id+"F0.wireOp",EDGE,"E1215"),sQuery(id+"F0.wireOp",EDGE,"E1216"),sQuery(id+"F0.wireOp",EDGE,"E1217"),sQuery(id+"F0.wireOp",EDGE,"E1218"),sQuery(id+"F0.wireOp",EDGE,"E1219"),sQuery(id+"F0.wireOp",EDGE,"E1220"),sQuery(id+"F0.wireOp",EDGE,"E1221"),sQuery(id+"F0.wireOp",EDGE,"E1222"),sQuery(id+"F0.wireOp",EDGE,"E1223"),sQuery(id+"F0.wireOp",EDGE,"E1224"),sQuery(id+"F0.wireOp",EDGE,"E1225"),sQuery(id+"F0.wireOp",EDGE,"E1226"),sQuery(id+"F0.wireOp",EDGE,"E1227"),sQuery(id+"F0.wireOp",EDGE,"E1228"),sQuery(id+"F0.wireOp",EDGE,"E1229"),sQuery(id+"F0.wireOp",EDGE,"E1230"),sQuery(id+"F0.wireOp",EDGE,"E1231"),sQuery(id+"F0.wireOp",EDGE,"E1232"),sQuery(id+"F0.wireOp",EDGE,"E1233"),sQuery(id+"F0.wireOp",EDGE,"E1234"),sQuery(id+"F0.wireOp",EDGE,"E1235"),sQuery(id+"F0.wireOp",EDGE,"E1236"),sQuery(id+"F0.wireOp",EDGE,"E1237"),sQuery(id+"F0.wireOp",EDGE,"E1238"),sQuery(id+"F0.wireOp",EDGE,"E1239"),sQuery(id+"F0.wireOp",EDGE,"E1240"),sQuery(id+"F0.wireOp",EDGE,"E1347")])],"isStart":false});
            var Q17;
            Q17=makeQuery(id+"F1.opExtrude","CAP_FACE",FACE,{"disambiguationData":[OSD([sQuery(id+"F0.wireOp",EDGE,"E1030"),sQuery(id+"F0.wireOp",EDGE,"E1031"),sQuery(id+"F0.wireOp",EDGE,"E1032"),sQuery(id+"F0.wireOp",EDGE,"E1033"),sQuery(id+"F0.wireOp",EDGE,"E1042"),sQuery(id+"F0.wireOp",EDGE,"E1043"),sQuery(id+"F0.wireOp",EDGE,"E1044"),sQuery(id+"F0.wireOp",EDGE,"E1045"),sQuery(id+"F0.wireOp",EDGE,"E1046"),sQuery(id+"F0.wireOp",EDGE,"E1047"),sQuery(id+"F0.wireOp",EDGE,"E1048"),sQuery(id+"F0.wireOp",EDGE,"E1049"),sQuery(id+"F0.wireOp",EDGE,"E1052"),sQuery(id+"F0.wireOp",EDGE,"E1056"),sQuery(id+"F0.wireOp",EDGE,"E1058"),sQuery(id+"F0.wireOp",EDGE,"E1059"),sQuery(id+"F0.wireOp",EDGE,"E1060"),sQuery(id+"F0.wireOp",EDGE,"E1061"),sQuery(id+"F0.wireOp",EDGE,"E1062"),sQuery(id+"F0.wireOp",EDGE,"E1063"),sQuery(id+"F0.wireOp",EDGE,"E1064"),sQuery(id+"F0.wireOp",EDGE,"E1065"),sQuery(id+"F0.wireOp",EDGE,"E1066"),sQuery(id+"F0.wireOp",EDGE,"E1067"),sQuery(id+"F0.wireOp",EDGE,"E1068"),sQuery(id+"F0.wireOp",EDGE,"E1069"),sQuery(id+"F0.wireOp",EDGE,"E1070"),sQuery(id+"F0.wireOp",EDGE,"E1071"),sQuery(id+"F0.wireOp",EDGE,"E1072"),sQuery(id+"F0.wireOp",EDGE,"E1073"),sQuery(id+"F0.wireOp",EDGE,"E1074"),sQuery(id+"F0.wireOp",EDGE,"E1075"),sQuery(id+"F0.wireOp",EDGE,"E1076"),sQuery(id+"F0.wireOp",EDGE,"E1077"),sQuery(id+"F0.wireOp",EDGE,"E1078"),sQuery(id+"F0.wireOp",EDGE,"E1079"),sQuery(id+"F0.wireOp",EDGE,"E1080"),sQuery(id+"F0.wireOp",EDGE,"E1081"),sQuery(id+"F0.wireOp",EDGE,"E1082"),sQuery(id+"F0.wireOp",EDGE,"E1083"),sQuery(id+"F0.wireOp",EDGE,"E1084"),sQuery(id+"F0.wireOp",EDGE,"E1085"),sQuery(id+"F0.wireOp",EDGE,"E1086"),sQuery(id+"F0.wireOp",EDGE,"E1087"),sQuery(id+"F0.wireOp",EDGE,"E1088"),sQuery(id+"F0.wireOp",EDGE,"E1089"),sQuery(id+"F0.wireOp",EDGE,"E1090"),sQuery(id+"F0.wireOp",EDGE,"E1091"),sQuery(id+"F0.wireOp",EDGE,"E1092"),sQuery(id+"F0.wireOp",EDGE,"E1093"),sQuery(id+"F0.wireOp",EDGE,"E1094"),sQuery(id+"F0.wireOp",EDGE,"E1095"),sQuery(id+"F0.wireOp",EDGE,"E1096"),sQuery(id+"F0.wireOp",EDGE,"E1097"),sQuery(id+"F0.wireOp",EDGE,"E1098"),sQuery(id+"F0.wireOp",EDGE,"E1099"),sQuery(id+"F0.wireOp",EDGE,"E1100"),sQuery(id+"F0.wireOp",EDGE,"E1101"),sQuery(id+"F0.wireOp",EDGE,"E1102"),sQuery(id+"F0.wireOp",EDGE,"E1103"),sQuery(id+"F0.wireOp",EDGE,"E1104"),sQuery(id+"F0.wireOp",EDGE,"E1105"),sQuery(id+"F0.wireOp",EDGE,"E1106"),sQuery(id+"F0.wireOp",EDGE,"E1107"),sQuery(id+"F0.wireOp",EDGE,"E1108"),sQuery(id+"F0.wireOp",EDGE,"E1109"),sQuery(id+"F0.wireOp",EDGE,"E1110"),sQuery(id+"F0.wireOp",EDGE,"E1111"),sQuery(id+"F0.wireOp",EDGE,"E1112"),sQuery(id+"F0.wireOp",EDGE,"E1113"),sQuery(id+"F0.wireOp",EDGE,"E1114"),sQuery(id+"F0.wireOp",EDGE,"E1115"),sQuery(id+"F0.wireOp",EDGE,"E1116"),sQuery(id+"F0.wireOp",EDGE,"E1117"),sQuery(id+"F0.wireOp",EDGE,"E1118"),sQuery(id+"F0.wireOp",EDGE,"E1119"),sQuery(id+"F0.wireOp",EDGE,"E1120"),sQuery(id+"F0.wireOp",EDGE,"E1121"),sQuery(id+"F0.wireOp",EDGE,"E1122"),sQuery(id+"F0.wireOp",EDGE,"E1123"),sQuery(id+"F0.wireOp",EDGE,"E1124"),sQuery(id+"F0.wireOp",EDGE,"E1125"),sQuery(id+"F0.wireOp",EDGE,"E1126"),sQuery(id+"F0.wireOp",EDGE,"E1127"),sQuery(id+"F0.wireOp",EDGE,"E1128"),sQuery(id+"F0.wireOp",EDGE,"E1129"),sQuery(id+"F0.wireOp",EDGE,"E1130"),sQuery(id+"F0.wireOp",EDGE,"E1131"),sQuery(id+"F0.wireOp",EDGE,"E1132"),sQuery(id+"F0.wireOp",EDGE,"E1133"),sQuery(id+"F0.wireOp",EDGE,"E1134"),sQuery(id+"F0.wireOp",EDGE,"E1135"),sQuery(id+"F0.wireOp",EDGE,"E1139")])],"isStart":false});
            var Q18;
            Q18=makeQuery(id+"F1.opExtrude","CAP_FACE",FACE,{"disambiguationData":[OSD([sQuery(id+"F0.wireOp",EDGE,"E925"),sQuery(id+"F0.wireOp",EDGE,"E926"),sQuery(id+"F0.wireOp",EDGE,"E927"),sQuery(id+"F0.wireOp",EDGE,"E928"),sQuery(id+"F0.wireOp",EDGE,"E937"),sQuery(id+"F0.wireOp",EDGE,"E938"),sQuery(id+"F0.wireOp",EDGE,"E939"),sQuery(id+"F0.wireOp",EDGE,"E940"),sQuery(id+"F0.wireOp",EDGE,"E941"),sQuery(id+"F0.wireOp",EDGE,"E942"),sQuery(id+"F0.wireOp",EDGE,"E943"),sQuery(id+"F0.wireOp",EDGE,"E944"),sQuery(id+"F0.wireOp",EDGE,"E947"),sQuery(id+"F0.wireOp",EDGE,"E949"),sQuery(id+"F0.wireOp",EDGE,"E950"),sQuery(id+"F0.wireOp",EDGE,"E951"),sQuery(id+"F0.wireOp",EDGE,"E952"),sQuery(id+"F0.wireOp",EDGE,"E953"),sQuery(id+"F0.wireOp",EDGE,"E954"),sQuery(id+"F0.wireOp",EDGE,"E955"),sQuery(id+"F0.wireOp",EDGE,"E956"),sQuery(id+"F0.wireOp",EDGE,"E957"),sQuery(id+"F0.wireOp",EDGE,"E958"),sQuery(id+"F0.wireOp",EDGE,"E959"),sQuery(id+"F0.wireOp",EDGE,"E960"),sQuery(id+"F0.wireOp",EDGE,"E961"),sQuery(id+"F0.wireOp",EDGE,"E962"),sQuery(id+"F0.wireOp",EDGE,"E963"),sQuery(id+"F0.wireOp",EDGE,"E964"),sQuery(id+"F0.wireOp",EDGE,"E965"),sQuery(id+"F0.wireOp",EDGE,"E966"),sQuery(id+"F0.wireOp",EDGE,"E967"),sQuery(id+"F0.wireOp",EDGE,"E968"),sQuery(id+"F0.wireOp",EDGE,"E969"),sQuery(id+"F0.wireOp",EDGE,"E970"),sQuery(id+"F0.wireOp",EDGE,"E971"),sQuery(id+"F0.wireOp",EDGE,"E972"),sQuery(id+"F0.wireOp",EDGE,"E973"),sQuery(id+"F0.wireOp",EDGE,"E974"),sQuery(id+"F0.wireOp",EDGE,"E975"),sQuery(id+"F0.wireOp",EDGE,"E976"),sQuery(id+"F0.wireOp",EDGE,"E977"),sQuery(id+"F0.wireOp",EDGE,"E978"),sQuery(id+"F0.wireOp",EDGE,"E979"),sQuery(id+"F0.wireOp",EDGE,"E980"),sQuery(id+"F0.wireOp",EDGE,"E981"),sQuery(id+"F0.wireOp",EDGE,"E982"),sQuery(id+"F0.wireOp",EDGE,"E983"),sQuery(id+"F0.wireOp",EDGE,"E984"),sQuery(id+"F0.wireOp",EDGE,"E985"),sQuery(id+"F0.wireOp",EDGE,"E986"),sQuery(id+"F0.wireOp",EDGE,"E987"),sQuery(id+"F0.wireOp",EDGE,"E988"),sQuery(id+"F0.wireOp",EDGE,"E989"),sQuery(id+"F0.wireOp",EDGE,"E990"),sQuery(id+"F0.wireOp",EDGE,"E991"),sQuery(id+"F0.wireOp",EDGE,"E992"),sQuery(id+"F0.wireOp",EDGE,"E993"),sQuery(id+"F0.wireOp",EDGE,"E994"),sQuery(id+"F0.wireOp",EDGE,"E995"),sQuery(id+"F0.wireOp",EDGE,"E996"),sQuery(id+"F0.wireOp",EDGE,"E997"),sQuery(id+"F0.wireOp",EDGE,"E998"),sQuery(id+"F0.wireOp",EDGE,"E999"),sQuery(id+"F0.wireOp",EDGE,"E1000"),sQuery(id+"F0.wireOp",EDGE,"E1001"),sQuery(id+"F0.wireOp",EDGE,"E1002"),sQuery(id+"F0.wireOp",EDGE,"E1003"),sQuery(id+"F0.wireOp",EDGE,"E1004"),sQuery(id+"F0.wireOp",EDGE,"E1005"),sQuery(id+"F0.wireOp",EDGE,"E1006"),sQuery(id+"F0.wireOp",EDGE,"E1007"),sQuery(id+"F0.wireOp",EDGE,"E1008"),sQuery(id+"F0.wireOp",EDGE,"E1009"),sQuery(id+"F0.wireOp",EDGE,"E1010"),sQuery(id+"F0.wireOp",EDGE,"E1011"),sQuery(id+"F0.wireOp",EDGE,"E1012"),sQuery(id+"F0.wireOp",EDGE,"E1013"),sQuery(id+"F0.wireOp",EDGE,"E1014"),sQuery(id+"F0.wireOp",EDGE,"E1015"),sQuery(id+"F0.wireOp",EDGE,"E1016"),sQuery(id+"F0.wireOp",EDGE,"E1017"),sQuery(id+"F0.wireOp",EDGE,"E1018"),sQuery(id+"F0.wireOp",EDGE,"E1019"),sQuery(id+"F0.wireOp",EDGE,"E1020"),sQuery(id+"F0.wireOp",EDGE,"E1021"),sQuery(id+"F0.wireOp",EDGE,"E1022"),sQuery(id+"F0.wireOp",EDGE,"E1023"),sQuery(id+"F0.wireOp",EDGE,"E1024"),sQuery(id+"F0.wireOp",EDGE,"E1025"),sQuery(id+"F0.wireOp",EDGE,"E1026"),sQuery(id+"F0.wireOp",EDGE,"E1137")])],"isStart":false});
            var Q19;
            Q19=makeQuery(id+"F1.opExtrude","CAP_FACE",FACE,{"disambiguationData":[OSD([sQuery(id+"F0.wireOp",EDGE,"E820"),sQuery(id+"F0.wireOp",EDGE,"E821"),sQuery(id+"F0.wireOp",EDGE,"E822"),sQuery(id+"F0.wireOp",EDGE,"E823"),sQuery(id+"F0.wireOp",EDGE,"E832"),sQuery(id+"F0.wireOp",EDGE,"E833"),sQuery(id+"F0.wireOp",EDGE,"E834"),sQuery(id+"F0.wireOp",EDGE,"E835"),sQuery(id+"F0.wireOp",EDGE,"E836"),sQuery(id+"F0.wireOp",EDGE,"E837"),sQuery(id+"F0.wireOp",EDGE,"E838"),sQuery(id+"F0.wireOp",EDGE,"E839"),sQuery(id+"F0.wireOp",EDGE,"E842"),sQuery(id+"F0.wireOp",EDGE,"E846"),sQuery(id+"F0.wireOp",EDGE,"E848"),sQuery(id+"F0.wireOp",EDGE,"E849"),sQuery(id+"F0.wireOp",EDGE,"E850"),sQuery(id+"F0.wireOp",EDGE,"E851"),sQuery(id+"F0.wireOp",EDGE,"E852"),sQuery(id+"F0.wireOp",EDGE,"E853"),sQuery(id+"F0.wireOp",EDGE,"E854"),sQuery(id+"F0.wireOp",EDGE,"E855"),sQuery(id+"F0.wireOp",EDGE,"E856"),sQuery(id+"F0.wireOp",EDGE,"E857"),sQuery(id+"F0.wireOp",EDGE,"E858"),sQuery(id+"F0.wireOp",EDGE,"E859"),sQuery(id+"F0.wireOp",EDGE,"E860"),sQuery(id+"F0.wireOp",EDGE,"E861"),sQuery(id+"F0.wireOp",EDGE,"E862"),sQuery(id+"F0.wireOp",EDGE,"E863"),sQuery(id+"F0.wireOp",EDGE,"E864"),sQuery(id+"F0.wireOp",EDGE,"E865"),sQuery(id+"F0.wireOp",EDGE,"E866"),sQuery(id+"F0.wireOp",EDGE,"E867"),sQuery(id+"F0.wireOp",EDGE,"E868"),sQuery(id+"F0.wireOp",EDGE,"E869"),sQuery(id+"F0.wireOp",EDGE,"E870"),sQuery(id+"F0.wireOp",EDGE,"E871"),sQuery(id+"F0.wireOp",EDGE,"E872"),sQuery(id+"F0.wireOp",EDGE,"E873"),sQuery(id+"F0.wireOp",EDGE,"E874"),sQuery(id+"F0.wireOp",EDGE,"E875"),sQuery(id+"F0.wireOp",EDGE,"E876"),sQuery(id+"F0.wireOp",EDGE,"E877"),sQuery(id+"F0.wireOp",EDGE,"E878"),sQuery(id+"F0.wireOp",EDGE,"E879"),sQuery(id+"F0.wireOp",EDGE,"E880"),sQuery(id+"F0.wireOp",EDGE,"E881"),sQuery(id+"F0.wireOp",EDGE,"E882"),sQuery(id+"F0.wireOp",EDGE,"E883"),sQuery(id+"F0.wireOp",EDGE,"E884"),sQuery(id+"F0.wireOp",EDGE,"E885"),sQuery(id+"F0.wireOp",EDGE,"E886"),sQuery(id+"F0.wireOp",EDGE,"E887"),sQuery(id+"F0.wireOp",EDGE,"E888"),sQuery(id+"F0.wireOp",EDGE,"E889"),sQuery(id+"F0.wireOp",EDGE,"E890"),sQuery(id+"F0.wireOp",EDGE,"E891"),sQuery(id+"F0.wireOp",EDGE,"E892"),sQuery(id+"F0.wireOp",EDGE,"E893"),sQuery(id+"F0.wireOp",EDGE,"E894"),sQuery(id+"F0.wireOp",EDGE,"E895"),sQuery(id+"F0.wireOp",EDGE,"E896"),sQuery(id+"F0.wireOp",EDGE,"E897"),sQuery(id+"F0.wireOp",EDGE,"E898"),sQuery(id+"F0.wireOp",EDGE,"E899"),sQuery(id+"F0.wireOp",EDGE,"E900"),sQuery(id+"F0.wireOp",EDGE,"E901"),sQuery(id+"F0.wireOp",EDGE,"E902"),sQuery(id+"F0.wireOp",EDGE,"E903"),sQuery(id+"F0.wireOp",EDGE,"E904"),sQuery(id+"F0.wireOp",EDGE,"E905"),sQuery(id+"F0.wireOp",EDGE,"E906"),sQuery(id+"F0.wireOp",EDGE,"E907"),sQuery(id+"F0.wireOp",EDGE,"E908"),sQuery(id+"F0.wireOp",EDGE,"E909"),sQuery(id+"F0.wireOp",EDGE,"E910"),sQuery(id+"F0.wireOp",EDGE,"E911"),sQuery(id+"F0.wireOp",EDGE,"E912"),sQuery(id+"F0.wireOp",EDGE,"E913"),sQuery(id+"F0.wireOp",EDGE,"E914"),sQuery(id+"F0.wireOp",EDGE,"E915"),sQuery(id+"F0.wireOp",EDGE,"E916"),sQuery(id+"F0.wireOp",EDGE,"E917"),sQuery(id+"F0.wireOp",EDGE,"E918"),sQuery(id+"F0.wireOp",EDGE,"E919"),sQuery(id+"F0.wireOp",EDGE,"E920"),sQuery(id+"F0.wireOp",EDGE,"E921"),sQuery(id+"F0.wireOp",EDGE,"E922"),sQuery(id+"F0.wireOp",EDGE,"E923"),sQuery(id+"F0.wireOp",EDGE,"E924"),sQuery(id+"F0.wireOp",EDGE,"E1999")])],"isStart":false});
            var Q20;
            Q20=makeQuery(id+"F1.opExtrude","CAP_FACE",FACE,{"disambiguationData":[OSD([sQuery(id+"F0.wireOp",EDGE,"E711"),sQuery(id+"F0.wireOp",EDGE,"E712"),sQuery(id+"F0.wireOp",EDGE,"E713"),sQuery(id+"F0.wireOp",EDGE,"E714"),sQuery(id+"F0.wireOp",EDGE,"E723"),sQuery(id+"F0.wireOp",EDGE,"E724"),sQuery(id+"F0.wireOp",EDGE,"E725"),sQuery(id+"F0.wireOp",EDGE,"E726"),sQuery(id+"F0.wireOp",EDGE,"E727"),sQuery(id+"F0.wireOp",EDGE,"E728"),sQuery(id+"F0.wireOp",EDGE,"E729"),sQuery(id+"F0.wireOp",EDGE,"E730"),sQuery(id+"F0.wireOp",EDGE,"E733"),sQuery(id+"F0.wireOp",EDGE,"E737"),sQuery(id+"F0.wireOp",EDGE,"E739"),sQuery(id+"F0.wireOp",EDGE,"E740"),sQuery(id+"F0.wireOp",EDGE,"E741"),sQuery(id+"F0.wireOp",EDGE,"E742"),sQuery(id+"F0.wireOp",EDGE,"E743"),sQuery(id+"F0.wireOp",EDGE,"E744"),sQuery(id+"F0.wireOp",EDGE,"E745"),sQuery(id+"F0.wireOp",EDGE,"E746"),sQuery(id+"F0.wireOp",EDGE,"E747"),sQuery(id+"F0.wireOp",EDGE,"E748"),sQuery(id+"F0.wireOp",EDGE,"E749"),sQuery(id+"F0.wireOp",EDGE,"E750"),sQuery(id+"F0.wireOp",EDGE,"E751"),sQuery(id+"F0.wireOp",EDGE,"E752"),sQuery(id+"F0.wireOp",EDGE,"E753"),sQuery(id+"F0.wireOp",EDGE,"E754"),sQuery(id+"F0.wireOp",EDGE,"E755"),sQuery(id+"F0.wireOp",EDGE,"E756"),sQuery(id+"F0.wireOp",EDGE,"E757"),sQuery(id+"F0.wireOp",EDGE,"E758"),sQuery(id+"F0.wireOp",EDGE,"E759"),sQuery(id+"F0.wireOp",EDGE,"E760"),sQuery(id+"F0.wireOp",EDGE,"E761"),sQuery(id+"F0.wireOp",EDGE,"E762"),sQuery(id+"F0.wireOp",EDGE,"E763"),sQuery(id+"F0.wireOp",EDGE,"E764"),sQuery(id+"F0.wireOp",EDGE,"E765"),sQuery(id+"F0.wireOp",EDGE,"E766"),sQuery(id+"F0.wireOp",EDGE,"E767"),sQuery(id+"F0.wireOp",EDGE,"E768"),sQuery(id+"F0.wireOp",EDGE,"E769"),sQuery(id+"F0.wireOp",EDGE,"E770"),sQuery(id+"F0.wireOp",EDGE,"E771"),sQuery(id+"F0.wireOp",EDGE,"E772"),sQuery(id+"F0.wireOp",EDGE,"E773"),sQuery(id+"F0.wireOp",EDGE,"E774"),sQuery(id+"F0.wireOp",EDGE,"E775"),sQuery(id+"F0.wireOp",EDGE,"E776"),sQuery(id+"F0.wireOp",EDGE,"E777"),sQuery(id+"F0.wireOp",EDGE,"E778"),sQuery(id+"F0.wireOp",EDGE,"E779"),sQuery(id+"F0.wireOp",EDGE,"E780"),sQuery(id+"F0.wireOp",EDGE,"E781"),sQuery(id+"F0.wireOp",EDGE,"E782"),sQuery(id+"F0.wireOp",EDGE,"E783"),sQuery(id+"F0.wireOp",EDGE,"E784"),sQuery(id+"F0.wireOp",EDGE,"E785"),sQuery(id+"F0.wireOp",EDGE,"E786"),sQuery(id+"F0.wireOp",EDGE,"E787"),sQuery(id+"F0.wireOp",EDGE,"E788"),sQuery(id+"F0.wireOp",EDGE,"E789"),sQuery(id+"F0.wireOp",EDGE,"E790"),sQuery(id+"F0.wireOp",EDGE,"E791"),sQuery(id+"F0.wireOp",EDGE,"E792"),sQuery(id+"F0.wireOp",EDGE,"E793"),sQuery(id+"F0.wireOp",EDGE,"E794"),sQuery(id+"F0.wireOp",EDGE,"E795"),sQuery(id+"F0.wireOp",EDGE,"E796"),sQuery(id+"F0.wireOp",EDGE,"E797"),sQuery(id+"F0.wireOp",EDGE,"E798"),sQuery(id+"F0.wireOp",EDGE,"E799"),sQuery(id+"F0.wireOp",EDGE,"E800"),sQuery(id+"F0.wireOp",EDGE,"E801"),sQuery(id+"F0.wireOp",EDGE,"E802"),sQuery(id+"F0.wireOp",EDGE,"E803"),sQuery(id+"F0.wireOp",EDGE,"E804"),sQuery(id+"F0.wireOp",EDGE,"E805"),sQuery(id+"F0.wireOp",EDGE,"E806"),sQuery(id+"F0.wireOp",EDGE,"E807"),sQuery(id+"F0.wireOp",EDGE,"E808"),sQuery(id+"F0.wireOp",EDGE,"E809"),sQuery(id+"F0.wireOp",EDGE,"E810"),sQuery(id+"F0.wireOp",EDGE,"E811"),sQuery(id+"F0.wireOp",EDGE,"E812"),sQuery(id+"F0.wireOp",EDGE,"E813"),sQuery(id+"F0.wireOp",EDGE,"E814"),sQuery(id+"F0.wireOp",EDGE,"E815"),sQuery(id+"F0.wireOp",EDGE,"E816")])],"isStart":false});
            var Q21;
            Q21=makeQuery(id+"F1.opExtrude","CAP_FACE",FACE,{"disambiguationData":[OSD([sQuery(id+"F0.wireOp",EDGE,"E610"),sQuery(id+"F0.wireOp",EDGE,"E611"),sQuery(id+"F0.wireOp",EDGE,"E612"),sQuery(id+"F0.wireOp",EDGE,"E613"),sQuery(id+"F0.wireOp",EDGE,"E622"),sQuery(id+"F0.wireOp",EDGE,"E623"),sQuery(id+"F0.wireOp",EDGE,"E624"),sQuery(id+"F0.wireOp",EDGE,"E625"),sQuery(id+"F0.wireOp",EDGE,"E626"),sQuery(id+"F0.wireOp",EDGE,"E627"),sQuery(id+"F0.wireOp",EDGE,"E628"),sQuery(id+"F0.wireOp",EDGE,"E629"),sQuery(id+"F0.wireOp",EDGE,"E632"),sQuery(id+"F0.wireOp",EDGE,"E634"),sQuery(id+"F0.wireOp",EDGE,"E635"),sQuery(id+"F0.wireOp",EDGE,"E636"),sQuery(id+"F0.wireOp",EDGE,"E637"),sQuery(id+"F0.wireOp",EDGE,"E638"),sQuery(id+"F0.wireOp",EDGE,"E639"),sQuery(id+"F0.wireOp",EDGE,"E640"),sQuery(id+"F0.wireOp",EDGE,"E641"),sQuery(id+"F0.wireOp",EDGE,"E642"),sQuery(id+"F0.wireOp",EDGE,"E643"),sQuery(id+"F0.wireOp",EDGE,"E644"),sQuery(id+"F0.wireOp",EDGE,"E645"),sQuery(id+"F0.wireOp",EDGE,"E646"),sQuery(id+"F0.wireOp",EDGE,"E647"),sQuery(id+"F0.wireOp",EDGE,"E648"),sQuery(id+"F0.wireOp",EDGE,"E649"),sQuery(id+"F0.wireOp",EDGE,"E650"),sQuery(id+"F0.wireOp",EDGE,"E651"),sQuery(id+"F0.wireOp",EDGE,"E652"),sQuery(id+"F0.wireOp",EDGE,"E653"),sQuery(id+"F0.wireOp",EDGE,"E654"),sQuery(id+"F0.wireOp",EDGE,"E655"),sQuery(id+"F0.wireOp",EDGE,"E656"),sQuery(id+"F0.wireOp",EDGE,"E657"),sQuery(id+"F0.wireOp",EDGE,"E658"),sQuery(id+"F0.wireOp",EDGE,"E659"),sQuery(id+"F0.wireOp",EDGE,"E660"),sQuery(id+"F0.wireOp",EDGE,"E661"),sQuery(id+"F0.wireOp",EDGE,"E662"),sQuery(id+"F0.wireOp",EDGE,"E663"),sQuery(id+"F0.wireOp",EDGE,"E664"),sQuery(id+"F0.wireOp",EDGE,"E665"),sQuery(id+"F0.wireOp",EDGE,"E666"),sQuery(id+"F0.wireOp",EDGE,"E667"),sQuery(id+"F0.wireOp",EDGE,"E668"),sQuery(id+"F0.wireOp",EDGE,"E669"),sQuery(id+"F0.wireOp",EDGE,"E670"),sQuery(id+"F0.wireOp",EDGE,"E671"),sQuery(id+"F0.wireOp",EDGE,"E672"),sQuery(id+"F0.wireOp",EDGE,"E673"),sQuery(id+"F0.wireOp",EDGE,"E674"),sQuery(id+"F0.wireOp",EDGE,"E675"),sQuery(id+"F0.wireOp",EDGE,"E676"),sQuery(id+"F0.wireOp",EDGE,"E677"),sQuery(id+"F0.wireOp",EDGE,"E678"),sQuery(id+"F0.wireOp",EDGE,"E679"),sQuery(id+"F0.wireOp",EDGE,"E680"),sQuery(id+"F0.wireOp",EDGE,"E681"),sQuery(id+"F0.wireOp",EDGE,"E682"),sQuery(id+"F0.wireOp",EDGE,"E683"),sQuery(id+"F0.wireOp",EDGE,"E684"),sQuery(id+"F0.wireOp",EDGE,"E685"),sQuery(id+"F0.wireOp",EDGE,"E686"),sQuery(id+"F0.wireOp",EDGE,"E687"),sQuery(id+"F0.wireOp",EDGE,"E688"),sQuery(id+"F0.wireOp",EDGE,"E689"),sQuery(id+"F0.wireOp",EDGE,"E690"),sQuery(id+"F0.wireOp",EDGE,"E691"),sQuery(id+"F0.wireOp",EDGE,"E692"),sQuery(id+"F0.wireOp",EDGE,"E693"),sQuery(id+"F0.wireOp",EDGE,"E694"),sQuery(id+"F0.wireOp",EDGE,"E695"),sQuery(id+"F0.wireOp",EDGE,"E696"),sQuery(id+"F0.wireOp",EDGE,"E697"),sQuery(id+"F0.wireOp",EDGE,"E698"),sQuery(id+"F0.wireOp",EDGE,"E699"),sQuery(id+"F0.wireOp",EDGE,"E700"),sQuery(id+"F0.wireOp",EDGE,"E701"),sQuery(id+"F0.wireOp",EDGE,"E702"),sQuery(id+"F0.wireOp",EDGE,"E703"),sQuery(id+"F0.wireOp",EDGE,"E704"),sQuery(id+"F0.wireOp",EDGE,"E705"),sQuery(id+"F0.wireOp",EDGE,"E706"),sQuery(id+"F0.wireOp",EDGE,"E707"),sQuery(id+"F0.wireOp",EDGE,"E708"),sQuery(id+"F0.wireOp",EDGE,"E709"),sQuery(id+"F0.wireOp",EDGE,"E710"),sQuery(id+"F0.wireOp",EDGE,"E731")])],"isStart":false});
            var Q22;
            Q22=makeQuery(id+"F1.opExtrude","CAP_FACE",FACE,{"disambiguationData":[OSD([sQuery(id+"F0.wireOp",EDGE,"E513"),sQuery(id+"F0.wireOp",EDGE,"E514"),sQuery(id+"F0.wireOp",EDGE,"E515"),sQuery(id+"F0.wireOp",EDGE,"E516"),sQuery(id+"F0.wireOp",EDGE,"E525"),sQuery(id+"F0.wireOp",EDGE,"E526"),sQuery(id+"F0.wireOp",EDGE,"E527"),sQuery(id+"F0.wireOp",EDGE,"E528"),sQuery(id+"F0.wireOp",EDGE,"E529"),sQuery(id+"F0.wireOp",EDGE,"E530"),sQuery(id+"F0.wireOp",EDGE,"E531"),sQuery(id+"F0.wireOp",EDGE,"E532"),sQuery(id+"F0.wireOp",EDGE,"E533"),sQuery(id+"F0.wireOp",EDGE,"E534"),sQuery(id+"F0.wireOp",EDGE,"E535"),sQuery(id+"F0.wireOp",EDGE,"E536"),sQuery(id+"F0.wireOp",EDGE,"E537"),sQuery(id+"F0.wireOp",EDGE,"E538"),sQuery(id+"F0.wireOp",EDGE,"E539"),sQuery(id+"F0.wireOp",EDGE,"E540"),sQuery(id+"F0.wireOp",EDGE,"E541"),sQuery(id+"F0.wireOp",EDGE,"E542"),sQuery(id+"F0.wireOp",EDGE,"E543"),sQuery(id+"F0.wireOp",EDGE,"E544"),sQuery(id+"F0.wireOp",EDGE,"E545"),sQuery(id+"F0.wireOp",EDGE,"E546"),sQuery(id+"F0.wireOp",EDGE,"E547"),sQuery(id+"F0.wireOp",EDGE,"E548"),sQuery(id+"F0.wireOp",EDGE,"E549"),sQuery(id+"F0.wireOp",EDGE,"E550"),sQuery(id+"F0.wireOp",EDGE,"E551"),sQuery(id+"F0.wireOp",EDGE,"E552"),sQuery(id+"F0.wireOp",EDGE,"E553"),sQuery(id+"F0.wireOp",EDGE,"E554"),sQuery(id+"F0.wireOp",EDGE,"E555"),sQuery(id+"F0.wireOp",EDGE,"E556"),sQuery(id+"F0.wireOp",EDGE,"E557"),sQuery(id+"F0.wireOp",EDGE,"E558"),sQuery(id+"F0.wireOp",EDGE,"E559"),sQuery(id+"F0.wireOp",EDGE,"E560"),sQuery(id+"F0.wireOp",EDGE,"E561"),sQuery(id+"F0.wireOp",EDGE,"E562"),sQuery(id+"F0.wireOp",EDGE,"E563"),sQuery(id+"F0.wireOp",EDGE,"E564"),sQuery(id+"F0.wireOp",EDGE,"E565"),sQuery(id+"F0.wireOp",EDGE,"E566"),sQuery(id+"F0.wireOp",EDGE,"E567"),sQuery(id+"F0.wireOp",EDGE,"E568"),sQuery(id+"F0.wireOp",EDGE,"E569"),sQuery(id+"F0.wireOp",EDGE,"E570"),sQuery(id+"F0.wireOp",EDGE,"E571"),sQuery(id+"F0.wireOp",EDGE,"E572"),sQuery(id+"F0.wireOp",EDGE,"E573"),sQuery(id+"F0.wireOp",EDGE,"E574"),sQuery(id+"F0.wireOp",EDGE,"E575"),sQuery(id+"F0.wireOp",EDGE,"E576"),sQuery(id+"F0.wireOp",EDGE,"E577"),sQuery(id+"F0.wireOp",EDGE,"E578"),sQuery(id+"F0.wireOp",EDGE,"E579"),sQuery(id+"F0.wireOp",EDGE,"E580"),sQuery(id+"F0.wireOp",EDGE,"E581"),sQuery(id+"F0.wireOp",EDGE,"E582"),sQuery(id+"F0.wireOp",EDGE,"E583"),sQuery(id+"F0.wireOp",EDGE,"E584"),sQuery(id+"F0.wireOp",EDGE,"E585"),sQuery(id+"F0.wireOp",EDGE,"E586"),sQuery(id+"F0.wireOp",EDGE,"E587"),sQuery(id+"F0.wireOp",EDGE,"E588"),sQuery(id+"F0.wireOp",EDGE,"E589"),sQuery(id+"F0.wireOp",EDGE,"E590"),sQuery(id+"F0.wireOp",EDGE,"E591"),sQuery(id+"F0.wireOp",EDGE,"E592"),sQuery(id+"F0.wireOp",EDGE,"E593"),sQuery(id+"F0.wireOp",EDGE,"E594"),sQuery(id+"F0.wireOp",EDGE,"E595"),sQuery(id+"F0.wireOp",EDGE,"E596"),sQuery(id+"F0.wireOp",EDGE,"E597"),sQuery(id+"F0.wireOp",EDGE,"E598"),sQuery(id+"F0.wireOp",EDGE,"E599"),sQuery(id+"F0.wireOp",EDGE,"E600"),sQuery(id+"F0.wireOp",EDGE,"E601"),sQuery(id+"F0.wireOp",EDGE,"E602"),sQuery(id+"F0.wireOp",EDGE,"E603"),sQuery(id+"F0.wireOp",EDGE,"E604"),sQuery(id+"F0.wireOp",EDGE,"E605"),sQuery(id+"F0.wireOp",EDGE,"E606"),sQuery(id+"F0.wireOp",EDGE,"E607"),sQuery(id+"F0.wireOp",EDGE,"E608"),sQuery(id+"F0.wireOp",EDGE,"E609"),sQuery(id+"F0.wireOp",EDGE,"E630"),sQuery(id+"F0.wireOp",EDGE,"E840")])],"isStart":false});
            var Q23;
            Q23=makeQuery(id+"F1.opExtrude","CAP_FACE",FACE,{"disambiguationData":[OSD([sQuery(id+"F0.wireOp",EDGE,"E408"),sQuery(id+"F0.wireOp",EDGE,"E409"),sQuery(id+"F0.wireOp",EDGE,"E410"),sQuery(id+"F0.wireOp",EDGE,"E411"),sQuery(id+"F0.wireOp",EDGE,"E420"),sQuery(id+"F0.wireOp",EDGE,"E421"),sQuery(id+"F0.wireOp",EDGE,"E422"),sQuery(id+"F0.wireOp",EDGE,"E423"),sQuery(id+"F0.wireOp",EDGE,"E424"),sQuery(id+"F0.wireOp",EDGE,"E425"),sQuery(id+"F0.wireOp",EDGE,"E426"),sQuery(id+"F0.wireOp",EDGE,"E427"),sQuery(id+"F0.wireOp",EDGE,"E430"),sQuery(id+"F0.wireOp",EDGE,"E432"),sQuery(id+"F0.wireOp",EDGE,"E433"),sQuery(id+"F0.wireOp",EDGE,"E434"),sQuery(id+"F0.wireOp",EDGE,"E435"),sQuery(id+"F0.wireOp",EDGE,"E436"),sQuery(id+"F0.wireOp",EDGE,"E437"),sQuery(id+"F0.wireOp",EDGE,"E438"),sQuery(id+"F0.wireOp",EDGE,"E439"),sQuery(id+"F0.wireOp",EDGE,"E440"),sQuery(id+"F0.wireOp",EDGE,"E441"),sQuery(id+"F0.wireOp",EDGE,"E442"),sQuery(id+"F0.wireOp",EDGE,"E443"),sQuery(id+"F0.wireOp",EDGE,"E444"),sQuery(id+"F0.wireOp",EDGE,"E445"),sQuery(id+"F0.wireOp",EDGE,"E446"),sQuery(id+"F0.wireOp",EDGE,"E447"),sQuery(id+"F0.wireOp",EDGE,"E448"),sQuery(id+"F0.wireOp",EDGE,"E449"),sQuery(id+"F0.wireOp",EDGE,"E450"),sQuery(id+"F0.wireOp",EDGE,"E451"),sQuery(id+"F0.wireOp",EDGE,"E452"),sQuery(id+"F0.wireOp",EDGE,"E453"),sQuery(id+"F0.wireOp",EDGE,"E454"),sQuery(id+"F0.wireOp",EDGE,"E455"),sQuery(id+"F0.wireOp",EDGE,"E456"),sQuery(id+"F0.wireOp",EDGE,"E457"),sQuery(id+"F0.wireOp",EDGE,"E458"),sQuery(id+"F0.wireOp",EDGE,"E459"),sQuery(id+"F0.wireOp",EDGE,"E460"),sQuery(id+"F0.wireOp",EDGE,"E461"),sQuery(id+"F0.wireOp",EDGE,"E462"),sQuery(id+"F0.wireOp",EDGE,"E463"),sQuery(id+"F0.wireOp",EDGE,"E464"),sQuery(id+"F0.wireOp",EDGE,"E465"),sQuery(id+"F0.wireOp",EDGE,"E466"),sQuery(id+"F0.wireOp",EDGE,"E467"),sQuery(id+"F0.wireOp",EDGE,"E468"),sQuery(id+"F0.wireOp",EDGE,"E469"),sQuery(id+"F0.wireOp",EDGE,"E470"),sQuery(id+"F0.wireOp",EDGE,"E471"),sQuery(id+"F0.wireOp",EDGE,"E472"),sQuery(id+"F0.wireOp",EDGE,"E473"),sQuery(id+"F0.wireOp",EDGE,"E474"),sQuery(id+"F0.wireOp",EDGE,"E475"),sQuery(id+"F0.wireOp",EDGE,"E476"),sQuery(id+"F0.wireOp",EDGE,"E477"),sQuery(id+"F0.wireOp",EDGE,"E478"),sQuery(id+"F0.wireOp",EDGE,"E479"),sQuery(id+"F0.wireOp",EDGE,"E480"),sQuery(id+"F0.wireOp",EDGE,"E481"),sQuery(id+"F0.wireOp",EDGE,"E482"),sQuery(id+"F0.wireOp",EDGE,"E483"),sQuery(id+"F0.wireOp",EDGE,"E484"),sQuery(id+"F0.wireOp",EDGE,"E485"),sQuery(id+"F0.wireOp",EDGE,"E486"),sQuery(id+"F0.wireOp",EDGE,"E487"),sQuery(id+"F0.wireOp",EDGE,"E488"),sQuery(id+"F0.wireOp",EDGE,"E489"),sQuery(id+"F0.wireOp",EDGE,"E490"),sQuery(id+"F0.wireOp",EDGE,"E491"),sQuery(id+"F0.wireOp",EDGE,"E492"),sQuery(id+"F0.wireOp",EDGE,"E493"),sQuery(id+"F0.wireOp",EDGE,"E494"),sQuery(id+"F0.wireOp",EDGE,"E495"),sQuery(id+"F0.wireOp",EDGE,"E496"),sQuery(id+"F0.wireOp",EDGE,"E497"),sQuery(id+"F0.wireOp",EDGE,"E498"),sQuery(id+"F0.wireOp",EDGE,"E499"),sQuery(id+"F0.wireOp",EDGE,"E500"),sQuery(id+"F0.wireOp",EDGE,"E501"),sQuery(id+"F0.wireOp",EDGE,"E502"),sQuery(id+"F0.wireOp",EDGE,"E503"),sQuery(id+"F0.wireOp",EDGE,"E504"),sQuery(id+"F0.wireOp",EDGE,"E505"),sQuery(id+"F0.wireOp",EDGE,"E506"),sQuery(id+"F0.wireOp",EDGE,"E507"),sQuery(id+"F0.wireOp",EDGE,"E508"),sQuery(id+"F0.wireOp",EDGE,"E509"),sQuery(id+"F0.wireOp",EDGE,"E945")])],"isStart":false});
            var Q24;
            Q24=makeQuery(id+"F1.opExtrude","CAP_FACE",FACE,{"disambiguationData":[OSD([sQuery(id+"F0.wireOp",EDGE,"E307"),sQuery(id+"F0.wireOp",EDGE,"E308"),sQuery(id+"F0.wireOp",EDGE,"E309"),sQuery(id+"F0.wireOp",EDGE,"E310"),sQuery(id+"F0.wireOp",EDGE,"E319"),sQuery(id+"F0.wireOp",EDGE,"E320"),sQuery(id+"F0.wireOp",EDGE,"E321"),sQuery(id+"F0.wireOp",EDGE,"E322"),sQuery(id+"F0.wireOp",EDGE,"E323"),sQuery(id+"F0.wireOp",EDGE,"E324"),sQuery(id+"F0.wireOp",EDGE,"E325"),sQuery(id+"F0.wireOp",EDGE,"E326"),sQuery(id+"F0.wireOp",EDGE,"E329"),sQuery(id+"F0.wireOp",EDGE,"E331"),sQuery(id+"F0.wireOp",EDGE,"E332"),sQuery(id+"F0.wireOp",EDGE,"E333"),sQuery(id+"F0.wireOp",EDGE,"E334"),sQuery(id+"F0.wireOp",EDGE,"E335"),sQuery(id+"F0.wireOp",EDGE,"E336"),sQuery(id+"F0.wireOp",EDGE,"E337"),sQuery(id+"F0.wireOp",EDGE,"E338"),sQuery(id+"F0.wireOp",EDGE,"E339"),sQuery(id+"F0.wireOp",EDGE,"E340"),sQuery(id+"F0.wireOp",EDGE,"E341"),sQuery(id+"F0.wireOp",EDGE,"E342"),sQuery(id+"F0.wireOp",EDGE,"E343"),sQuery(id+"F0.wireOp",EDGE,"E344"),sQuery(id+"F0.wireOp",EDGE,"E345"),sQuery(id+"F0.wireOp",EDGE,"E346"),sQuery(id+"F0.wireOp",EDGE,"E347"),sQuery(id+"F0.wireOp",EDGE,"E348"),sQuery(id+"F0.wireOp",EDGE,"E349"),sQuery(id+"F0.wireOp",EDGE,"E350"),sQuery(id+"F0.wireOp",EDGE,"E351"),sQuery(id+"F0.wireOp",EDGE,"E352"),sQuery(id+"F0.wireOp",EDGE,"E353"),sQuery(id+"F0.wireOp",EDGE,"E354"),sQuery(id+"F0.wireOp",EDGE,"E355"),sQuery(id+"F0.wireOp",EDGE,"E356"),sQuery(id+"F0.wireOp",EDGE,"E357"),sQuery(id+"F0.wireOp",EDGE,"E358"),sQuery(id+"F0.wireOp",EDGE,"E359"),sQuery(id+"F0.wireOp",EDGE,"E360"),sQuery(id+"F0.wireOp",EDGE,"E361"),sQuery(id+"F0.wireOp",EDGE,"E362"),sQuery(id+"F0.wireOp",EDGE,"E363"),sQuery(id+"F0.wireOp",EDGE,"E364"),sQuery(id+"F0.wireOp",EDGE,"E365"),sQuery(id+"F0.wireOp",EDGE,"E366"),sQuery(id+"F0.wireOp",EDGE,"E367"),sQuery(id+"F0.wireOp",EDGE,"E368"),sQuery(id+"F0.wireOp",EDGE,"E369"),sQuery(id+"F0.wireOp",EDGE,"E370"),sQuery(id+"F0.wireOp",EDGE,"E371"),sQuery(id+"F0.wireOp",EDGE,"E372"),sQuery(id+"F0.wireOp",EDGE,"E373"),sQuery(id+"F0.wireOp",EDGE,"E374"),sQuery(id+"F0.wireOp",EDGE,"E375"),sQuery(id+"F0.wireOp",EDGE,"E376"),sQuery(id+"F0.wireOp",EDGE,"E377"),sQuery(id+"F0.wireOp",EDGE,"E378"),sQuery(id+"F0.wireOp",EDGE,"E379"),sQuery(id+"F0.wireOp",EDGE,"E380"),sQuery(id+"F0.wireOp",EDGE,"E381"),sQuery(id+"F0.wireOp",EDGE,"E382"),sQuery(id+"F0.wireOp",EDGE,"E383"),sQuery(id+"F0.wireOp",EDGE,"E384"),sQuery(id+"F0.wireOp",EDGE,"E385"),sQuery(id+"F0.wireOp",EDGE,"E386"),sQuery(id+"F0.wireOp",EDGE,"E387"),sQuery(id+"F0.wireOp",EDGE,"E388"),sQuery(id+"F0.wireOp",EDGE,"E389"),sQuery(id+"F0.wireOp",EDGE,"E390"),sQuery(id+"F0.wireOp",EDGE,"E391"),sQuery(id+"F0.wireOp",EDGE,"E392"),sQuery(id+"F0.wireOp",EDGE,"E393"),sQuery(id+"F0.wireOp",EDGE,"E394"),sQuery(id+"F0.wireOp",EDGE,"E395"),sQuery(id+"F0.wireOp",EDGE,"E396"),sQuery(id+"F0.wireOp",EDGE,"E397"),sQuery(id+"F0.wireOp",EDGE,"E398"),sQuery(id+"F0.wireOp",EDGE,"E399"),sQuery(id+"F0.wireOp",EDGE,"E400"),sQuery(id+"F0.wireOp",EDGE,"E401"),sQuery(id+"F0.wireOp",EDGE,"E402"),sQuery(id+"F0.wireOp",EDGE,"E403"),sQuery(id+"F0.wireOp",EDGE,"E404"),sQuery(id+"F0.wireOp",EDGE,"E405"),sQuery(id+"F0.wireOp",EDGE,"E406"),sQuery(id+"F0.wireOp",EDGE,"E407"),sQuery(id+"F0.wireOp",EDGE,"E428"),sQuery(id+"F0.wireOp",EDGE,"E1050")])],"isStart":false});
            var Q25;
            Q25=makeQuery(id+"F1.opExtrude","CAP_FACE",FACE,{"disambiguationData":[OSD([sQuery(id+"F0.wireOp",EDGE,"E206"),sQuery(id+"F0.wireOp",EDGE,"E207"),sQuery(id+"F0.wireOp",EDGE,"E208"),sQuery(id+"F0.wireOp",EDGE,"E209"),sQuery(id+"F0.wireOp",EDGE,"E218"),sQuery(id+"F0.wireOp",EDGE,"E219"),sQuery(id+"F0.wireOp",EDGE,"E220"),sQuery(id+"F0.wireOp",EDGE,"E221"),sQuery(id+"F0.wireOp",EDGE,"E222"),sQuery(id+"F0.wireOp",EDGE,"E223"),sQuery(id+"F0.wireOp",EDGE,"E224"),sQuery(id+"F0.wireOp",EDGE,"E225"),sQuery(id+"F0.wireOp",EDGE,"E226"),sQuery(id+"F0.wireOp",EDGE,"E227"),sQuery(id+"F0.wireOp",EDGE,"E228"),sQuery(id+"F0.wireOp",EDGE,"E229"),sQuery(id+"F0.wireOp",EDGE,"E230"),sQuery(id+"F0.wireOp",EDGE,"E231"),sQuery(id+"F0.wireOp",EDGE,"E232"),sQuery(id+"F0.wireOp",EDGE,"E233"),sQuery(id+"F0.wireOp",EDGE,"E234"),sQuery(id+"F0.wireOp",EDGE,"E235"),sQuery(id+"F0.wireOp",EDGE,"E236"),sQuery(id+"F0.wireOp",EDGE,"E237"),sQuery(id+"F0.wireOp",EDGE,"E238"),sQuery(id+"F0.wireOp",EDGE,"E239"),sQuery(id+"F0.wireOp",EDGE,"E240"),sQuery(id+"F0.wireOp",EDGE,"E241"),sQuery(id+"F0.wireOp",EDGE,"E242"),sQuery(id+"F0.wireOp",EDGE,"E243"),sQuery(id+"F0.wireOp",EDGE,"E244"),sQuery(id+"F0.wireOp",EDGE,"E245"),sQuery(id+"F0.wireOp",EDGE,"E246"),sQuery(id+"F0.wireOp",EDGE,"E247"),sQuery(id+"F0.wireOp",EDGE,"E248"),sQuery(id+"F0.wireOp",EDGE,"E249"),sQuery(id+"F0.wireOp",EDGE,"E250"),sQuery(id+"F0.wireOp",EDGE,"E251"),sQuery(id+"F0.wireOp",EDGE,"E252"),sQuery(id+"F0.wireOp",EDGE,"E253"),sQuery(id+"F0.wireOp",EDGE,"E254"),sQuery(id+"F0.wireOp",EDGE,"E255"),sQuery(id+"F0.wireOp",EDGE,"E256"),sQuery(id+"F0.wireOp",EDGE,"E257"),sQuery(id+"F0.wireOp",EDGE,"E258"),sQuery(id+"F0.wireOp",EDGE,"E259"),sQuery(id+"F0.wireOp",EDGE,"E260"),sQuery(id+"F0.wireOp",EDGE,"E261"),sQuery(id+"F0.wireOp",EDGE,"E262"),sQuery(id+"F0.wireOp",EDGE,"E263"),sQuery(id+"F0.wireOp",EDGE,"E264"),sQuery(id+"F0.wireOp",EDGE,"E265"),sQuery(id+"F0.wireOp",EDGE,"E266"),sQuery(id+"F0.wireOp",EDGE,"E267"),sQuery(id+"F0.wireOp",EDGE,"E268"),sQuery(id+"F0.wireOp",EDGE,"E269"),sQuery(id+"F0.wireOp",EDGE,"E270"),sQuery(id+"F0.wireOp",EDGE,"E271"),sQuery(id+"F0.wireOp",EDGE,"E272"),sQuery(id+"F0.wireOp",EDGE,"E273"),sQuery(id+"F0.wireOp",EDGE,"E274"),sQuery(id+"F0.wireOp",EDGE,"E275"),sQuery(id+"F0.wireOp",EDGE,"E276"),sQuery(id+"F0.wireOp",EDGE,"E277"),sQuery(id+"F0.wireOp",EDGE,"E278"),sQuery(id+"F0.wireOp",EDGE,"E279"),sQuery(id+"F0.wireOp",EDGE,"E280"),sQuery(id+"F0.wireOp",EDGE,"E281"),sQuery(id+"F0.wireOp",EDGE,"E282"),sQuery(id+"F0.wireOp",EDGE,"E283"),sQuery(id+"F0.wireOp",EDGE,"E284"),sQuery(id+"F0.wireOp",EDGE,"E285"),sQuery(id+"F0.wireOp",EDGE,"E286"),sQuery(id+"F0.wireOp",EDGE,"E287"),sQuery(id+"F0.wireOp",EDGE,"E288"),sQuery(id+"F0.wireOp",EDGE,"E289"),sQuery(id+"F0.wireOp",EDGE,"E290"),sQuery(id+"F0.wireOp",EDGE,"E291"),sQuery(id+"F0.wireOp",EDGE,"E292"),sQuery(id+"F0.wireOp",EDGE,"E293"),sQuery(id+"F0.wireOp",EDGE,"E294"),sQuery(id+"F0.wireOp",EDGE,"E295"),sQuery(id+"F0.wireOp",EDGE,"E296"),sQuery(id+"F0.wireOp",EDGE,"E297"),sQuery(id+"F0.wireOp",EDGE,"E298"),sQuery(id+"F0.wireOp",EDGE,"E299"),sQuery(id+"F0.wireOp",EDGE,"E300"),sQuery(id+"F0.wireOp",EDGE,"E301"),sQuery(id+"F0.wireOp",EDGE,"E302"),sQuery(id+"F0.wireOp",EDGE,"E303"),sQuery(id+"F0.wireOp",EDGE,"E327")])],"isStart":false});
            var Q26;
            Q26=makeQuery(id+"F1.opExtrude","CAP_FACE",FACE,{"disambiguationData":[OSD([sQuery(id+"F0.wireOp",EDGE,"E101"),sQuery(id+"F0.wireOp",EDGE,"E102"),sQuery(id+"F0.wireOp",EDGE,"E103"),sQuery(id+"F0.wireOp",EDGE,"E104"),sQuery(id+"F0.wireOp",EDGE,"E113"),sQuery(id+"F0.wireOp",EDGE,"E114"),sQuery(id+"F0.wireOp",EDGE,"E115"),sQuery(id+"F0.wireOp",EDGE,"E116"),sQuery(id+"F0.wireOp",EDGE,"E117"),sQuery(id+"F0.wireOp",EDGE,"E118"),sQuery(id+"F0.wireOp",EDGE,"E119"),sQuery(id+"F0.wireOp",EDGE,"E120"),sQuery(id+"F0.wireOp",EDGE,"E121"),sQuery(id+"F0.wireOp",EDGE,"E122"),sQuery(id+"F0.wireOp",EDGE,"E123"),sQuery(id+"F0.wireOp",EDGE,"E124"),sQuery(id+"F0.wireOp",EDGE,"E125"),sQuery(id+"F0.wireOp",EDGE,"E126"),sQuery(id+"F0.wireOp",EDGE,"E127"),sQuery(id+"F0.wireOp",EDGE,"E128"),sQuery(id+"F0.wireOp",EDGE,"E129"),sQuery(id+"F0.wireOp",EDGE,"E130"),sQuery(id+"F0.wireOp",EDGE,"E131"),sQuery(id+"F0.wireOp",EDGE,"E132"),sQuery(id+"F0.wireOp",EDGE,"E133"),sQuery(id+"F0.wireOp",EDGE,"E134"),sQuery(id+"F0.wireOp",EDGE,"E135"),sQuery(id+"F0.wireOp",EDGE,"E136"),sQuery(id+"F0.wireOp",EDGE,"E137"),sQuery(id+"F0.wireOp",EDGE,"E138"),sQuery(id+"F0.wireOp",EDGE,"E139"),sQuery(id+"F0.wireOp",EDGE,"E140"),sQuery(id+"F0.wireOp",EDGE,"E141"),sQuery(id+"F0.wireOp",EDGE,"E142"),sQuery(id+"F0.wireOp",EDGE,"E143"),sQuery(id+"F0.wireOp",EDGE,"E144"),sQuery(id+"F0.wireOp",EDGE,"E145"),sQuery(id+"F0.wireOp",EDGE,"E146"),sQuery(id+"F0.wireOp",EDGE,"E147"),sQuery(id+"F0.wireOp",EDGE,"E148"),sQuery(id+"F0.wireOp",EDGE,"E149"),sQuery(id+"F0.wireOp",EDGE,"E150"),sQuery(id+"F0.wireOp",EDGE,"E151"),sQuery(id+"F0.wireOp",EDGE,"E152"),sQuery(id+"F0.wireOp",EDGE,"E153"),sQuery(id+"F0.wireOp",EDGE,"E154"),sQuery(id+"F0.wireOp",EDGE,"E155"),sQuery(id+"F0.wireOp",EDGE,"E156"),sQuery(id+"F0.wireOp",EDGE,"E157"),sQuery(id+"F0.wireOp",EDGE,"E158"),sQuery(id+"F0.wireOp",EDGE,"E159"),sQuery(id+"F0.wireOp",EDGE,"E160"),sQuery(id+"F0.wireOp",EDGE,"E161"),sQuery(id+"F0.wireOp",EDGE,"E162"),sQuery(id+"F0.wireOp",EDGE,"E163"),sQuery(id+"F0.wireOp",EDGE,"E164"),sQuery(id+"F0.wireOp",EDGE,"E165"),sQuery(id+"F0.wireOp",EDGE,"E166"),sQuery(id+"F0.wireOp",EDGE,"E167"),sQuery(id+"F0.wireOp",EDGE,"E168"),sQuery(id+"F0.wireOp",EDGE,"E169"),sQuery(id+"F0.wireOp",EDGE,"E170"),sQuery(id+"F0.wireOp",EDGE,"E171"),sQuery(id+"F0.wireOp",EDGE,"E172"),sQuery(id+"F0.wireOp",EDGE,"E173"),sQuery(id+"F0.wireOp",EDGE,"E174"),sQuery(id+"F0.wireOp",EDGE,"E175"),sQuery(id+"F0.wireOp",EDGE,"E176"),sQuery(id+"F0.wireOp",EDGE,"E177"),sQuery(id+"F0.wireOp",EDGE,"E178"),sQuery(id+"F0.wireOp",EDGE,"E179"),sQuery(id+"F0.wireOp",EDGE,"E180"),sQuery(id+"F0.wireOp",EDGE,"E181"),sQuery(id+"F0.wireOp",EDGE,"E182"),sQuery(id+"F0.wireOp",EDGE,"E183"),sQuery(id+"F0.wireOp",EDGE,"E184"),sQuery(id+"F0.wireOp",EDGE,"E185"),sQuery(id+"F0.wireOp",EDGE,"E186"),sQuery(id+"F0.wireOp",EDGE,"E187"),sQuery(id+"F0.wireOp",EDGE,"E188"),sQuery(id+"F0.wireOp",EDGE,"E189"),sQuery(id+"F0.wireOp",EDGE,"E190"),sQuery(id+"F0.wireOp",EDGE,"E191"),sQuery(id+"F0.wireOp",EDGE,"E192"),sQuery(id+"F0.wireOp",EDGE,"E193"),sQuery(id+"F0.wireOp",EDGE,"E194"),sQuery(id+"F0.wireOp",EDGE,"E195"),sQuery(id+"F0.wireOp",EDGE,"E196"),sQuery(id+"F0.wireOp",EDGE,"E197"),sQuery(id+"F0.wireOp",EDGE,"E198"),sQuery(id+"F0.wireOp",EDGE,"E202")])],"isStart":false});
            var Q27;
            Q27=makeQuery(id+"F1.opExtrude","CAP_FACE",FACE,{"disambiguationData":[OSD([sQuery(id+"F0.wireOp",EDGE,"E0"),sQuery(id+"F0.wireOp",EDGE,"E1"),sQuery(id+"F0.wireOp",EDGE,"E2"),sQuery(id+"F0.wireOp",EDGE,"E3"),sQuery(id+"F0.wireOp",EDGE,"E12"),sQuery(id+"F0.wireOp",EDGE,"E13"),sQuery(id+"F0.wireOp",EDGE,"E14"),sQuery(id+"F0.wireOp",EDGE,"E15"),sQuery(id+"F0.wireOp",EDGE,"E16"),sQuery(id+"F0.wireOp",EDGE,"E17"),sQuery(id+"F0.wireOp",EDGE,"E18"),sQuery(id+"F0.wireOp",EDGE,"E19"),sQuery(id+"F0.wireOp",EDGE,"E20"),sQuery(id+"F0.wireOp",EDGE,"E21"),sQuery(id+"F0.wireOp",EDGE,"E22"),sQuery(id+"F0.wireOp",EDGE,"E23"),sQuery(id+"F0.wireOp",EDGE,"E24"),sQuery(id+"F0.wireOp",EDGE,"E25"),sQuery(id+"F0.wireOp",EDGE,"E26"),sQuery(id+"F0.wireOp",EDGE,"E27"),sQuery(id+"F0.wireOp",EDGE,"E28"),sQuery(id+"F0.wireOp",EDGE,"E29"),sQuery(id+"F0.wireOp",EDGE,"E30"),sQuery(id+"F0.wireOp",EDGE,"E31"),sQuery(id+"F0.wireOp",EDGE,"E32"),sQuery(id+"F0.wireOp",EDGE,"E33"),sQuery(id+"F0.wireOp",EDGE,"E34"),sQuery(id+"F0.wireOp",EDGE,"E35"),sQuery(id+"F0.wireOp",EDGE,"E36"),sQuery(id+"F0.wireOp",EDGE,"E37"),sQuery(id+"F0.wireOp",EDGE,"E38"),sQuery(id+"F0.wireOp",EDGE,"E39"),sQuery(id+"F0.wireOp",EDGE,"E40"),sQuery(id+"F0.wireOp",EDGE,"E41"),sQuery(id+"F0.wireOp",EDGE,"E42"),sQuery(id+"F0.wireOp",EDGE,"E43"),sQuery(id+"F0.wireOp",EDGE,"E44"),sQuery(id+"F0.wireOp",EDGE,"E45"),sQuery(id+"F0.wireOp",EDGE,"E46"),sQuery(id+"F0.wireOp",EDGE,"E47"),sQuery(id+"F0.wireOp",EDGE,"E48"),sQuery(id+"F0.wireOp",EDGE,"E49"),sQuery(id+"F0.wireOp",EDGE,"E50"),sQuery(id+"F0.wireOp",EDGE,"E51"),sQuery(id+"F0.wireOp",EDGE,"E52"),sQuery(id+"F0.wireOp",EDGE,"E53"),sQuery(id+"F0.wireOp",EDGE,"E54"),sQuery(id+"F0.wireOp",EDGE,"E55"),sQuery(id+"F0.wireOp",EDGE,"E56"),sQuery(id+"F0.wireOp",EDGE,"E57"),sQuery(id+"F0.wireOp",EDGE,"E58"),sQuery(id+"F0.wireOp",EDGE,"E59"),sQuery(id+"F0.wireOp",EDGE,"E60"),sQuery(id+"F0.wireOp",EDGE,"E61"),sQuery(id+"F0.wireOp",EDGE,"E62"),sQuery(id+"F0.wireOp",EDGE,"E63"),sQuery(id+"F0.wireOp",EDGE,"E64"),sQuery(id+"F0.wireOp",EDGE,"E65"),sQuery(id+"F0.wireOp",EDGE,"E66"),sQuery(id+"F0.wireOp",EDGE,"E67"),sQuery(id+"F0.wireOp",EDGE,"E68"),sQuery(id+"F0.wireOp",EDGE,"E69"),sQuery(id+"F0.wireOp",EDGE,"E70"),sQuery(id+"F0.wireOp",EDGE,"E71"),sQuery(id+"F0.wireOp",EDGE,"E72"),sQuery(id+"F0.wireOp",EDGE,"E73"),sQuery(id+"F0.wireOp",EDGE,"E74"),sQuery(id+"F0.wireOp",EDGE,"E75"),sQuery(id+"F0.wireOp",EDGE,"E76"),sQuery(id+"F0.wireOp",EDGE,"E77"),sQuery(id+"F0.wireOp",EDGE,"E78"),sQuery(id+"F0.wireOp",EDGE,"E79"),sQuery(id+"F0.wireOp",EDGE,"E80"),sQuery(id+"F0.wireOp",EDGE,"E81"),sQuery(id+"F0.wireOp",EDGE,"E82"),sQuery(id+"F0.wireOp",EDGE,"E83"),sQuery(id+"F0.wireOp",EDGE,"E84"),sQuery(id+"F0.wireOp",EDGE,"E85"),sQuery(id+"F0.wireOp",EDGE,"E86"),sQuery(id+"F0.wireOp",EDGE,"E87"),sQuery(id+"F0.wireOp",EDGE,"E88"),sQuery(id+"F0.wireOp",EDGE,"E89"),sQuery(id+"F0.wireOp",EDGE,"E90"),sQuery(id+"F0.wireOp",EDGE,"E91"),sQuery(id+"F0.wireOp",EDGE,"E92"),sQuery(id+"F0.wireOp",EDGE,"E93"),sQuery(id+"F0.wireOp",EDGE,"E94"),sQuery(id+"F0.wireOp",EDGE,"E95"),sQuery(id+"F0.wireOp",EDGE,"E96"),sQuery(id+"F0.wireOp",EDGE,"E97"),sQuery(id+"F0.wireOp",EDGE,"E1369")])],"isStart":false});
            extrude(context, id + "F6", {"entities" : qUnion([Q0, Q1, Q2, Q3, Q4, Q5, Q6, Q7, Q8, Q9, Q10, Q11, Q12, Q13, Q14, Q15, Q16, Q17, Q18, Q19, Q20, Q21, Q22, Q23, Q24, Q25, Q26, Q27]), "operationType" : NewBodyOperationType.ADD, "depth" : 4 * mm, "offsetDistance" : 25 * mm});
        }
    });
